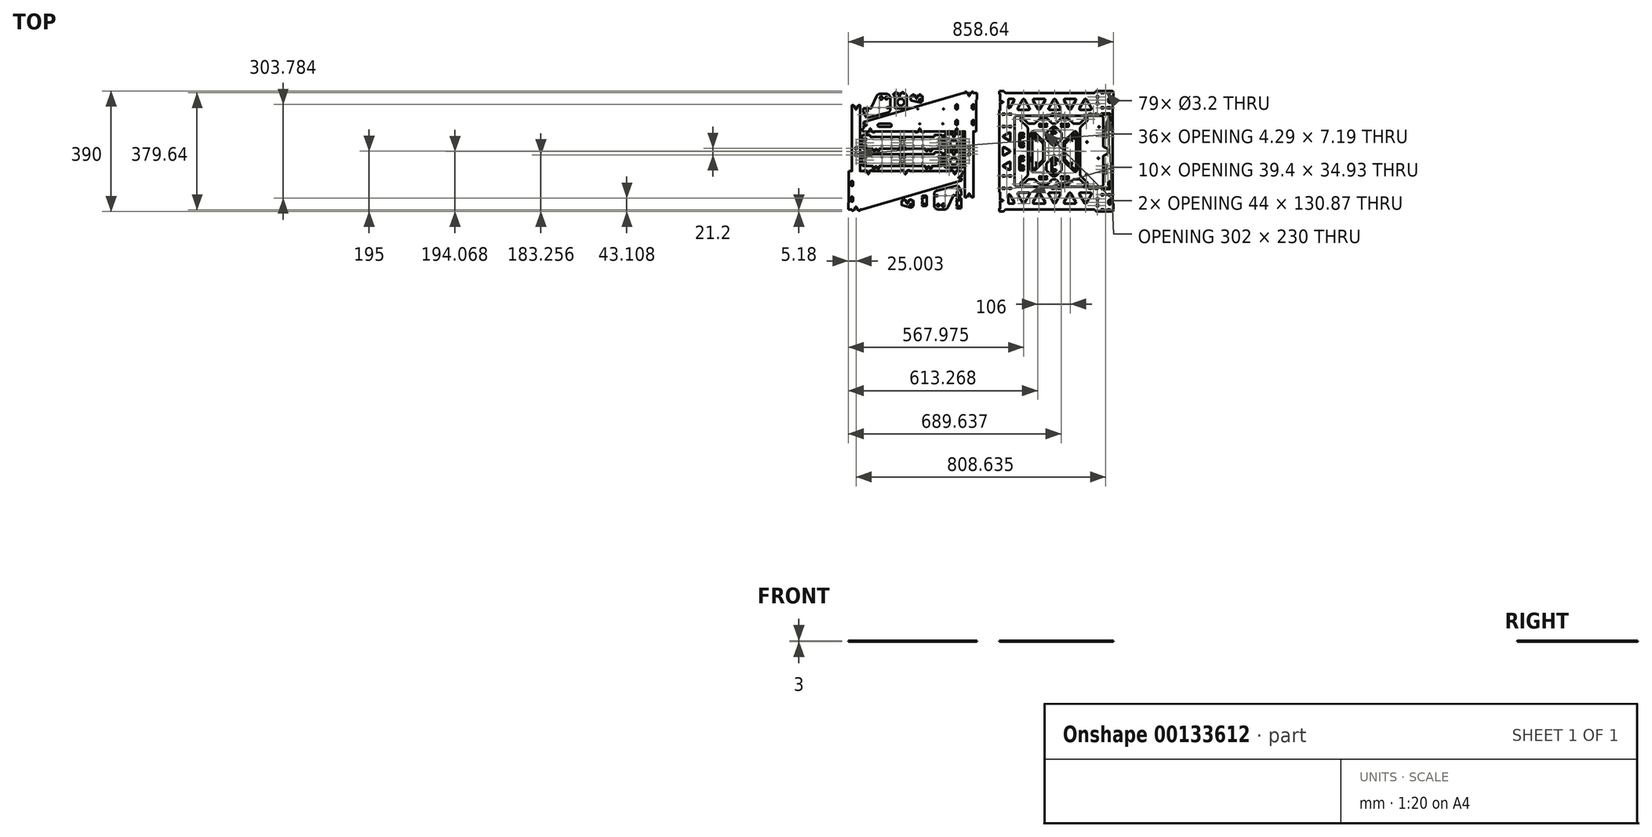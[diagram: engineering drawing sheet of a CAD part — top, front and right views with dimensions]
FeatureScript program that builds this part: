
annotation { "Feature Type Name" : "Feature", "Feature Type Description" : "" }
export const myFeature = defineFeature(function(context is Context, id is Id, definition is map)
    precondition{}
    {
        {
            var Q0;
            Q0=qCreatedBy(makeId("Top.planeOp"),FACE);
            var sketch = newSketch(context, id + "F0", { "sketchPlane" : qUnion([Q0])});
            skLineSegment(sketch, "E0", {"start": v(427.32, 168) * mm, "end": v(429.32, 170) * mm});
            skLineSegment(sketch, "E1", {"start": v(429.32, 170) * mm, "end": v(429.32, 190) * mm});
            skArc(sketch, "E2", {"start": v(429.32, 190) * mm, "mid": v(427.85, 193.54) * mm, "end": v(424.32, 195) * mm});
            skLineSegment(sketch, "E3", {"start": v(424.32, 195) * mm, "end": v(372.97, 195) * mm});
            skArc(sketch, "E4", {"start": v(365.22, 189) * mm, "mid": v(370.12, 190.68) * mm, "end": v(372.97, 195) * mm});
            skLineSegment(sketch, "E5", {"start": v(365.22, 189) * mm, "end": v(82.06, 189) * mm});
            skArc(sketch, "E6", {"start": v(74.32, 195) * mm, "mid": v(77.16, 190.68) * mm, "end": v(82.06, 189) * mm});
            skLineSegment(sketch, "E7", {"start": v(74.32, 195) * mm, "end": v(59.32, 195) * mm});
            skLineSegment(sketch, "E8", {"start": v(59.32, 195) * mm, "end": v(59.32, 185) * mm});
            skLineSegment(sketch, "E9", {"start": v(59.32, 185) * mm, "end": v(61.55, 185) * mm});
            skArc(sketch, "E10", {"start": v(61.55, 185) * mm, "mid": v(61.8, 185.07) * mm, "end": v(61.98, 185.25) * mm});
            skArc(sketch, "E11", {"start": v(62.67, 184.57) * mm, "mid": v(62.77, 185.35) * mm, "end": v(61.98, 185.25) * mm});
            skArc(sketch, "E12", {"start": v(62.67, 184.57) * mm, "mid": v(62.48, 184.38) * mm, "end": v(62.42, 184.13) * mm});
            skLineSegment(sketch, "E13", {"start": v(62.42, 184.13) * mm, "end": v(62.42, 160.78) * mm});
            skLineSegment(sketch, "E14", {"start": v(62.42, 160.78) * mm, "end": v(65.42, 160.78) * mm});
            skLineSegment(sketch, "E15", {"start": v(65.42, 160.78) * mm, "end": v(65.42, 162.05) * mm});
            skLineSegment(sketch, "E16", {"start": v(65.42, 162.05) * mm, "end": v(69.42, 162.05) * mm});
            skLineSegment(sketch, "E17", {"start": v(69.42, 162.05) * mm, "end": v(69.42, 160.78) * mm});
            skLineSegment(sketch, "E18", {"start": v(69.42, 160.78) * mm, "end": v(72.42, 160.78) * mm});
            skLineSegment(sketch, "E19", {"start": v(72.42, 160.78) * mm, "end": v(72.42, 157.57) * mm});
            skLineSegment(sketch, "E20", {"start": v(72.42, 157.57) * mm, "end": v(69.42, 157.57) * mm});
            skLineSegment(sketch, "E21", {"start": v(69.42, 157.57) * mm, "end": v(69.42, 156.3) * mm});
            skLineSegment(sketch, "E22", {"start": v(69.42, 156.3) * mm, "end": v(65.42, 156.3) * mm});
            skLineSegment(sketch, "E23", {"start": v(65.42, 156.3) * mm, "end": v(65.42, 157.57) * mm});
            skLineSegment(sketch, "E24", {"start": v(65.42, 157.57) * mm, "end": v(62.42, 157.57) * mm});
            skLineSegment(sketch, "E25", {"start": v(62.42, 157.57) * mm, "end": v(62.42, 134.22) * mm});
            skArc(sketch, "E26", {"start": v(62.42, 134.22) * mm, "mid": v(62.48, 133.97) * mm, "end": v(62.67, 133.78) * mm});
            skArc(sketch, "E27", {"start": v(61.98, 133.1) * mm, "mid": v(62.77, 133) * mm, "end": v(62.67, 133.78) * mm});
            skArc(sketch, "E28", {"start": v(61.98, 133.1) * mm, "mid": v(61.8, 133.28) * mm, "end": v(61.55, 133.35) * mm});
            skLineSegment(sketch, "E29", {"start": v(61.55, 133.35) * mm, "end": v(59.32, 133.35) * mm});
            skLineSegment(sketch, "E30", {"start": v(59.32, 133.35) * mm, "end": v(59.32, -133.35) * mm});
            skLineSegment(sketch, "E31", {"start": v(59.32, -133.35) * mm, "end": v(61.55, -133.35) * mm});
            skArc(sketch, "E32", {"start": v(61.55, -133.35) * mm, "mid": v(61.8, -133.28) * mm, "end": v(61.98, -133.1) * mm});
            skArc(sketch, "E33", {"start": v(62.67, -133.78) * mm, "mid": v(62.77, -133) * mm, "end": v(61.98, -133.1) * mm});
            skArc(sketch, "E34", {"start": v(62.67, -133.78) * mm, "mid": v(62.48, -133.97) * mm, "end": v(62.42, -134.22) * mm});
            skLineSegment(sketch, "E35", {"start": v(62.42, -134.22) * mm, "end": v(62.42, -157.57) * mm});
            skLineSegment(sketch, "E36", {"start": v(62.42, -157.57) * mm, "end": v(65.42, -157.57) * mm});
            skLineSegment(sketch, "E37", {"start": v(65.42, -157.57) * mm, "end": v(65.42, -156.3) * mm});
            skLineSegment(sketch, "E38", {"start": v(65.42, -156.3) * mm, "end": v(69.42, -156.3) * mm});
            skLineSegment(sketch, "E39", {"start": v(69.42, -156.3) * mm, "end": v(69.42, -157.57) * mm});
            skLineSegment(sketch, "E40", {"start": v(69.42, -157.57) * mm, "end": v(72.42, -157.57) * mm});
            skLineSegment(sketch, "E41", {"start": v(72.42, -157.57) * mm, "end": v(72.42, -160.78) * mm});
            skLineSegment(sketch, "E42", {"start": v(72.42, -160.78) * mm, "end": v(69.42, -160.78) * mm});
            skLineSegment(sketch, "E43", {"start": v(69.42, -160.78) * mm, "end": v(69.42, -162.05) * mm});
            skLineSegment(sketch, "E44", {"start": v(69.42, -162.05) * mm, "end": v(65.42, -162.05) * mm});
            skLineSegment(sketch, "E45", {"start": v(65.42, -162.05) * mm, "end": v(65.42, -160.78) * mm});
            skLineSegment(sketch, "E46", {"start": v(65.42, -160.78) * mm, "end": v(62.42, -160.78) * mm});
            skLineSegment(sketch, "E47", {"start": v(62.42, -160.78) * mm, "end": v(62.42, -184.13) * mm});
            skArc(sketch, "E48", {"start": v(62.42, -184.13) * mm, "mid": v(62.48, -184.38) * mm, "end": v(62.67, -184.57) * mm});
            skArc(sketch, "E49", {"start": v(61.98, -185.25) * mm, "mid": v(62.77, -185.35) * mm, "end": v(62.67, -184.57) * mm});
            skArc(sketch, "E50", {"start": v(61.98, -185.25) * mm, "mid": v(61.8, -185.07) * mm, "end": v(61.55, -185) * mm});
            skLineSegment(sketch, "E51", {"start": v(61.55, -185) * mm, "end": v(59.32, -185) * mm});
            skLineSegment(sketch, "E52", {"start": v(59.32, -185) * mm, "end": v(59.32, -195) * mm});
            skLineSegment(sketch, "E53", {"start": v(59.32, -195) * mm, "end": v(74.32, -195) * mm});
            skArc(sketch, "E54", {"start": v(82.06, -189) * mm, "mid": v(77.16, -190.68) * mm, "end": v(74.32, -195) * mm});
            skLineSegment(sketch, "E55", {"start": v(82.06, -189) * mm, "end": v(365.22, -189) * mm});
            skArc(sketch, "E56", {"start": v(372.97, -195) * mm, "mid": v(370.12, -190.68) * mm, "end": v(365.22, -189) * mm});
            skLineSegment(sketch, "E57", {"start": v(372.97, -195) * mm, "end": v(424.32, -195) * mm});
            skArc(sketch, "E58", {"start": v(424.32, -195) * mm, "mid": v(427.85, -193.54) * mm, "end": v(429.32, -190) * mm});
            skLineSegment(sketch, "E59", {"start": v(429.32, -190) * mm, "end": v(429.32, -170) * mm});
            skLineSegment(sketch, "E60", {"start": v(429.32, -170) * mm, "end": v(427.32, -168) * mm});
            skLineSegment(sketch, "E61", {"start": v(427.32, -168) * mm, "end": v(427.32, 168) * mm});
            skLineSegment(sketch, "E62", {"start": v(411.32, -6.72) * mm, "end": v(411.32, 6.73) * mm});
            skArc(sketch, "E63", {"start": v(411.32, 6.73) * mm, "mid": v(411, 7.8) * mm, "end": v(410.16, 8.54) * mm});
            skLineSegment(sketch, "E64", {"start": v(410.16, 8.54) * mm, "end": v(397.35, 14.51) * mm});
            skArc(sketch, "E65", {"start": v(396.2, 16.33) * mm, "mid": v(396.5, 15.25) * mm, "end": v(397.35, 14.51) * mm});
            skLineSegment(sketch, "E66", {"start": v(396.2, 16.33) * mm, "end": v(396.2, 107) * mm});
            skArc(sketch, "E67", {"start": v(396.2, 107) * mm, "mid": v(393.86, 112.65) * mm, "end": v(388.21, 115) * mm});
            skLineSegment(sketch, "E68", {"start": v(388.21, 115) * mm, "end": v(117.32, 115) * mm});
            skArc(sketch, "E69", {"start": v(117.32, 115) * mm, "mid": v(111.66, 112.66) * mm, "end": v(109.32, 107) * mm});
            skLineSegment(sketch, "E70", {"start": v(109.32, 107) * mm, "end": v(109.32, -107) * mm});
            skArc(sketch, "E71", {"start": v(109.32, -107) * mm, "mid": v(111.66, -112.66) * mm, "end": v(117.32, -115) * mm});
            skLineSegment(sketch, "E72", {"start": v(117.32, -115) * mm, "end": v(388.21, -115) * mm});
            skArc(sketch, "E73", {"start": v(388.21, -115) * mm, "mid": v(393.86, -112.65) * mm, "end": v(396.2, -107) * mm});
            skLineSegment(sketch, "E74", {"start": v(396.2, -107) * mm, "end": v(396.2, -16.23) * mm});
            skArc(sketch, "E75", {"start": v(397.36, -14.41) * mm, "mid": v(396.5, -15.15) * mm, "end": v(396.2, -16.23) * mm});
            skLineSegment(sketch, "E76", {"start": v(397.36, -14.41) * mm, "end": v(410.15, -8.54) * mm});
            skArc(sketch, "E77", {"start": v(410.15, -8.54) * mm, "mid": v(411, -7.8) * mm, "end": v(411.32, -6.72) * mm});
            skLineSegment(sketch, "E78", {"start": v(355.36, -134.43) * mm, "end": v(321.95, -134.43) * mm});
            skArc(sketch, "E79", {"start": v(321.95, -134.43) * mm, "mid": v(319.36, -135.93) * mm, "end": v(319.36, -138.93) * mm});
            skLineSegment(sketch, "E80", {"start": v(319.36, -138.93) * mm, "end": v(336.06, -167.86) * mm});
            skArc(sketch, "E81", {"start": v(336.06, -167.86) * mm, "mid": v(338.66, -169.36) * mm, "end": v(341.25, -167.86) * mm});
            skLineSegment(sketch, "E82", {"start": v(341.25, -167.86) * mm, "end": v(357.95, -138.93) * mm});
            skArc(sketch, "E83", {"start": v(357.95, -138.93) * mm, "mid": v(357.95, -135.93) * mm, "end": v(355.36, -134.43) * mm});
            skLineSegment(sketch, "E84", {"start": v(305.36, -169.36) * mm, "end": v(271.96, -169.36) * mm});
            skArc(sketch, "E85", {"start": v(269.36, -164.86) * mm, "mid": v(269.36, -167.86) * mm, "end": v(271.96, -169.36) * mm});
            skLineSegment(sketch, "E86", {"start": v(269.36, -164.86) * mm, "end": v(286.06, -135.93) * mm});
            skArc(sketch, "E87", {"start": v(291.25, -135.93) * mm, "mid": v(288.66, -134.43) * mm, "end": v(286.06, -135.93) * mm});
            skLineSegment(sketch, "E88", {"start": v(291.25, -135.93) * mm, "end": v(307.96, -164.86) * mm});
            skArc(sketch, "E89", {"start": v(305.36, -169.36) * mm, "mid": v(307.96, -167.86) * mm, "end": v(307.96, -164.86) * mm});
            skLineSegment(sketch, "E90", {"start": v(255.36, -134.43) * mm, "end": v(221.95, -134.43) * mm});
            skArc(sketch, "E91", {"start": v(221.95, -134.43) * mm, "mid": v(219.36, -135.93) * mm, "end": v(219.36, -138.93) * mm});
            skLineSegment(sketch, "E92", {"start": v(219.36, -138.93) * mm, "end": v(236.06, -167.86) * mm});
            skArc(sketch, "E93", {"start": v(236.06, -167.86) * mm, "mid": v(238.66, -169.36) * mm, "end": v(241.25, -167.86) * mm});
            skLineSegment(sketch, "E94", {"start": v(241.25, -167.86) * mm, "end": v(257.95, -138.93) * mm});
            skArc(sketch, "E95", {"start": v(257.95, -138.93) * mm, "mid": v(257.95, -135.93) * mm, "end": v(255.36, -134.43) * mm});
            skLineSegment(sketch, "E96", {"start": v(205.36, -169.36) * mm, "end": v(171.96, -169.36) * mm});
            skArc(sketch, "E97", {"start": v(169.36, -164.86) * mm, "mid": v(169.36, -167.86) * mm, "end": v(171.96, -169.36) * mm});
            skLineSegment(sketch, "E98", {"start": v(169.36, -164.86) * mm, "end": v(186.06, -135.93) * mm});
            skArc(sketch, "E99", {"start": v(191.25, -135.93) * mm, "mid": v(188.66, -134.43) * mm, "end": v(186.06, -135.93) * mm});
            skLineSegment(sketch, "E100", {"start": v(191.25, -135.93) * mm, "end": v(207.96, -164.86) * mm});
            skArc(sketch, "E101", {"start": v(205.36, -169.36) * mm, "mid": v(207.96, -167.86) * mm, "end": v(207.96, -164.86) * mm});
            skLineSegment(sketch, "E102", {"start": v(155.36, -134.43) * mm, "end": v(121.95, -134.43) * mm});
            skArc(sketch, "E103", {"start": v(121.95, -134.43) * mm, "mid": v(119.36, -135.93) * mm, "end": v(119.36, -138.93) * mm});
            skLineSegment(sketch, "E104", {"start": v(119.36, -138.93) * mm, "end": v(136.06, -167.86) * mm});
            skArc(sketch, "E105", {"start": v(136.06, -167.86) * mm, "mid": v(138.66, -169.36) * mm, "end": v(141.25, -167.86) * mm});
            skLineSegment(sketch, "E106", {"start": v(141.25, -167.86) * mm, "end": v(157.95, -138.93) * mm});
            skArc(sketch, "E107", {"start": v(157.95, -138.93) * mm, "mid": v(157.95, -135.93) * mm, "end": v(155.36, -134.43) * mm});
            skLineSegment(sketch, "E108", {"start": v(355.36, 134.43) * mm, "end": v(321.95, 134.43) * mm});
            skArc(sketch, "E109", {"start": v(319.36, 138.93) * mm, "mid": v(319.36, 135.93) * mm, "end": v(321.95, 134.43) * mm});
            skLineSegment(sketch, "E110", {"start": v(319.36, 138.93) * mm, "end": v(336.06, 167.86) * mm});
            skArc(sketch, "E111", {"start": v(341.25, 167.86) * mm, "mid": v(338.66, 169.36) * mm, "end": v(336.06, 167.86) * mm});
            skLineSegment(sketch, "E112", {"start": v(341.25, 167.86) * mm, "end": v(357.95, 138.93) * mm});
            skArc(sketch, "E113", {"start": v(355.36, 134.43) * mm, "mid": v(357.95, 135.93) * mm, "end": v(357.95, 138.93) * mm});
            skLineSegment(sketch, "E114", {"start": v(305.36, 169.36) * mm, "end": v(271.96, 169.36) * mm});
            skArc(sketch, "E115", {"start": v(271.96, 169.36) * mm, "mid": v(269.36, 167.86) * mm, "end": v(269.36, 164.86) * mm});
            skLineSegment(sketch, "E116", {"start": v(269.36, 164.86) * mm, "end": v(286.06, 135.93) * mm});
            skArc(sketch, "E117", {"start": v(286.06, 135.93) * mm, "mid": v(288.66, 134.43) * mm, "end": v(291.25, 135.93) * mm});
            skLineSegment(sketch, "E118", {"start": v(291.25, 135.93) * mm, "end": v(307.96, 164.86) * mm});
            skArc(sketch, "E119", {"start": v(307.96, 164.86) * mm, "mid": v(307.96, 167.86) * mm, "end": v(305.36, 169.36) * mm});
            skLineSegment(sketch, "E120", {"start": v(255.36, 134.43) * mm, "end": v(221.95, 134.43) * mm});
            skArc(sketch, "E121", {"start": v(219.36, 138.93) * mm, "mid": v(219.36, 135.93) * mm, "end": v(221.95, 134.43) * mm});
            skLineSegment(sketch, "E122", {"start": v(219.36, 138.93) * mm, "end": v(236.06, 167.86) * mm});
            skArc(sketch, "E123", {"start": v(241.25, 167.86) * mm, "mid": v(238.66, 169.36) * mm, "end": v(236.06, 167.86) * mm});
            skLineSegment(sketch, "E124", {"start": v(241.25, 167.86) * mm, "end": v(257.95, 138.93) * mm});
            skArc(sketch, "E125", {"start": v(255.36, 134.43) * mm, "mid": v(257.95, 135.93) * mm, "end": v(257.95, 138.93) * mm});
            skLineSegment(sketch, "E126", {"start": v(205.36, 169.36) * mm, "end": v(171.96, 169.36) * mm});
            skArc(sketch, "E127", {"start": v(171.96, 169.36) * mm, "mid": v(169.36, 167.86) * mm, "end": v(169.36, 164.86) * mm});
            skLineSegment(sketch, "E128", {"start": v(169.36, 164.86) * mm, "end": v(186.06, 135.93) * mm});
            skArc(sketch, "E129", {"start": v(186.06, 135.93) * mm, "mid": v(188.66, 134.43) * mm, "end": v(191.25, 135.93) * mm});
            skLineSegment(sketch, "E130", {"start": v(191.25, 135.93) * mm, "end": v(207.96, 164.86) * mm});
            skArc(sketch, "E131", {"start": v(207.96, 164.86) * mm, "mid": v(207.96, 167.86) * mm, "end": v(205.36, 169.36) * mm});
            skLineSegment(sketch, "E132", {"start": v(155.36, 134.43) * mm, "end": v(121.95, 134.43) * mm});
            skArc(sketch, "E133", {"start": v(119.36, 138.93) * mm, "mid": v(119.36, 135.93) * mm, "end": v(121.95, 134.43) * mm});
            skLineSegment(sketch, "E134", {"start": v(119.36, 138.93) * mm, "end": v(136.06, 167.86) * mm});
            skArc(sketch, "E135", {"start": v(141.25, 167.86) * mm, "mid": v(138.66, 169.36) * mm, "end": v(136.06, 167.86) * mm});
            skLineSegment(sketch, "E136", {"start": v(141.25, 167.86) * mm, "end": v(157.95, 138.93) * mm});
            skArc(sketch, "E137", {"start": v(155.36, 134.43) * mm, "mid": v(157.95, 135.93) * mm, "end": v(157.95, 138.93) * mm});
            skLineSegment(sketch, "E138", {"start": v(95.2, -36.24) * mm, "end": v(95.2, -58.78) * mm});
            skArc(sketch, "E139", {"start": v(92.16, -60.54) * mm, "mid": v(94.19, -60.54) * mm, "end": v(95.2, -58.78) * mm});
            skLineSegment(sketch, "E140", {"start": v(92.16, -60.54) * mm, "end": v(72.64, -49.26) * mm});
            skArc(sketch, "E141", {"start": v(72.64, -45.75) * mm, "mid": v(71.62, -47.5) * mm, "end": v(72.64, -49.26) * mm});
            skLineSegment(sketch, "E142", {"start": v(72.64, -45.75) * mm, "end": v(92.16, -34.48) * mm});
            skArc(sketch, "E143", {"start": v(95.2, -36.24) * mm, "mid": v(94.19, -34.48) * mm, "end": v(92.16, -34.48) * mm});
            skLineSegment(sketch, "E144", {"start": v(71.62, 11.26) * mm, "end": v(71.62, -11.28) * mm});
            skArc(sketch, "E145", {"start": v(71.62, -11.28) * mm, "mid": v(72.64, -13.04) * mm, "end": v(74.66, -13.04) * mm});
            skLineSegment(sketch, "E146", {"start": v(74.66, -13.04) * mm, "end": v(94.19, -1.76) * mm});
            skArc(sketch, "E147", {"start": v(94.19, -1.76) * mm, "mid": v(95.2, 0) * mm, "end": v(94.19, 1.75) * mm});
            skLineSegment(sketch, "E148", {"start": v(94.19, 1.75) * mm, "end": v(74.66, 13.02) * mm});
            skArc(sketch, "E149", {"start": v(74.66, 13.02) * mm, "mid": v(72.64, 13.02) * mm, "end": v(71.62, 11.26) * mm});
            skLineSegment(sketch, "E150", {"start": v(95.2, 58.77) * mm, "end": v(95.2, 36.23) * mm});
            skArc(sketch, "E151", {"start": v(92.16, 34.47) * mm, "mid": v(94.19, 34.47) * mm, "end": v(95.2, 36.23) * mm});
            skLineSegment(sketch, "E152", {"start": v(92.16, 34.47) * mm, "end": v(72.64, 45.75) * mm});
            skArc(sketch, "E153", {"start": v(72.64, 49.25) * mm, "mid": v(71.62, 47.5) * mm, "end": v(72.64, 45.75) * mm});
            skLineSegment(sketch, "E154", {"start": v(72.64, 49.25) * mm, "end": v(92.16, 60.53) * mm});
            skArc(sketch, "E155", {"start": v(95.2, 58.77) * mm, "mid": v(94.19, 60.53) * mm, "end": v(92.16, 60.53) * mm});
            skLineSegment(sketch, "E156", {"start": v(421.32, -169) * mm, "end": v(421.32, -161) * mm});
            skArc(sketch, "E157", {"start": v(421.32, -161) * mm, "mid": v(417.32, -157) * mm, "end": v(413.32, -161) * mm});
            skLineSegment(sketch, "E158", {"start": v(413.32, -161) * mm, "end": v(413.32, -169) * mm});
            skArc(sketch, "E159", {"start": v(413.32, -169) * mm, "mid": v(417.32, -173) * mm, "end": v(421.32, -169) * mm});
            skLineSegment(sketch, "E160", {"start": v(421.32, -109) * mm, "end": v(421.32, -101) * mm});
            skArc(sketch, "E161", {"start": v(421.32, -101) * mm, "mid": v(417.32, -97) * mm, "end": v(413.32, -101) * mm});
            skLineSegment(sketch, "E162", {"start": v(413.32, -101) * mm, "end": v(413.32, -109) * mm});
            skArc(sketch, "E163", {"start": v(413.32, -109) * mm, "mid": v(417.32, -113) * mm, "end": v(421.32, -109) * mm});
            skLineSegment(sketch, "E164", {"start": v(421.32, 101) * mm, "end": v(421.32, 109) * mm});
            skArc(sketch, "E165", {"start": v(421.32, 109) * mm, "mid": v(417.32, 113) * mm, "end": v(413.32, 109) * mm});
            skLineSegment(sketch, "E166", {"start": v(413.32, 109) * mm, "end": v(413.32, 101) * mm});
            skArc(sketch, "E167", {"start": v(413.32, 101) * mm, "mid": v(417.32, 97) * mm, "end": v(421.32, 101) * mm});
            skLineSegment(sketch, "E168", {"start": v(421.32, 161) * mm, "end": v(421.32, 169) * mm});
            skArc(sketch, "E169", {"start": v(421.32, 169) * mm, "mid": v(417.32, 173) * mm, "end": v(413.32, 169) * mm});
            skLineSegment(sketch, "E170", {"start": v(413.32, 169) * mm, "end": v(413.32, 161) * mm});
            skArc(sketch, "E171", {"start": v(413.32, 161) * mm, "mid": v(417.32, 157) * mm, "end": v(421.32, 161) * mm});
            skLineSegment(sketch, "E172", {"start": v(404.32, 118.38) * mm, "end": v(391.17, 118.38) * mm});
            skArc(sketch, "E173", {"start": v(390.27, 118.86) * mm, "mid": v(390.16, 118.07) * mm, "end": v(390.95, 118.18) * mm});
            skArc(sketch, "E174", {"start": v(390.27, 118.86) * mm, "mid": v(390.45, 119.04) * mm, "end": v(390.52, 119.3) * mm});
            skArc(sketch, "E175", {"start": v(411.82, -189.04) * mm, "mid": v(411.75, -188.79) * mm, "end": v(411.57, -188.6) * mm});
            skArc(sketch, "E176", {"start": v(412.25, -187.92) * mm, "mid": v(411.46, -187.82) * mm, "end": v(411.57, -188.6) * mm});
            skArc(sketch, "E177", {"start": v(412.25, -187.92) * mm, "mid": v(412.43, -188.1) * mm, "end": v(412.68, -188.17) * mm});
            skLineSegment(sketch, "E178", {"start": v(412.68, -188.17) * mm, "end": v(417.15, -188.17) * mm});
            skArc(sketch, "E179", {"start": v(417.15, -188.17) * mm, "mid": v(417.4, -188.1) * mm, "end": v(417.58, -187.92) * mm});
            skArc(sketch, "E180", {"start": v(418.27, -188.6) * mm, "mid": v(418.37, -187.82) * mm, "end": v(417.58, -187.92) * mm});
            skArc(sketch, "E181", {"start": v(418.27, -188.6) * mm, "mid": v(418.08, -188.79) * mm, "end": v(418.02, -189.04) * mm});
            skLineSegment(sketch, "E182", {"start": v(418.02, -189.04) * mm, "end": v(418.02, -190.6) * mm});
            skArc(sketch, "E183", {"start": v(418.02, -190.6) * mm, "mid": v(418.08, -190.85) * mm, "end": v(418.27, -191.04) * mm});
            skArc(sketch, "E184", {"start": v(417.58, -191.72) * mm, "mid": v(418.37, -191.82) * mm, "end": v(418.27, -191.04) * mm});
            skArc(sketch, "E185", {"start": v(417.58, -191.72) * mm, "mid": v(417.4, -191.54) * mm, "end": v(417.15, -191.47) * mm});
            skLineSegment(sketch, "E186", {"start": v(417.15, -191.47) * mm, "end": v(412.68, -191.47) * mm});
            skArc(sketch, "E187", {"start": v(412.68, -191.47) * mm, "mid": v(412.43, -191.54) * mm, "end": v(412.25, -191.72) * mm});
            skArc(sketch, "E188", {"start": v(411.57, -191.04) * mm, "mid": v(411.46, -191.82) * mm, "end": v(412.25, -191.72) * mm});
            skArc(sketch, "E189", {"start": v(411.57, -191.04) * mm, "mid": v(411.75, -190.85) * mm, "end": v(411.82, -190.6) * mm});
            skLineSegment(sketch, "E190", {"start": v(411.82, -190.6) * mm, "end": v(411.82, -189.04) * mm});
            skArc(sketch, "E191", {"start": v(390.62, -189.04) * mm, "mid": v(390.55, -188.79) * mm, "end": v(390.37, -188.6) * mm});
            skArc(sketch, "E192", {"start": v(391.05, -187.92) * mm, "mid": v(390.26, -187.82) * mm, "end": v(390.37, -188.6) * mm});
            skArc(sketch, "E193", {"start": v(391.05, -187.92) * mm, "mid": v(391.23, -188.1) * mm, "end": v(391.48, -188.17) * mm});
            skLineSegment(sketch, "E194", {"start": v(391.48, -188.17) * mm, "end": v(395.95, -188.17) * mm});
            skArc(sketch, "E195", {"start": v(395.95, -188.17) * mm, "mid": v(396.2, -188.1) * mm, "end": v(396.38, -187.92) * mm});
            skArc(sketch, "E196", {"start": v(397.07, -188.6) * mm, "mid": v(397.17, -187.82) * mm, "end": v(396.38, -187.92) * mm});
            skArc(sketch, "E197", {"start": v(397.07, -188.6) * mm, "mid": v(396.88, -188.79) * mm, "end": v(396.82, -189.04) * mm});
            skLineSegment(sketch, "E198", {"start": v(396.82, -189.04) * mm, "end": v(396.82, -190.6) * mm});
            skArc(sketch, "E199", {"start": v(396.82, -190.6) * mm, "mid": v(396.88, -190.85) * mm, "end": v(397.07, -191.04) * mm});
            skArc(sketch, "E200", {"start": v(396.38, -191.72) * mm, "mid": v(397.17, -191.82) * mm, "end": v(397.07, -191.04) * mm});
            skArc(sketch, "E201", {"start": v(396.38, -191.72) * mm, "mid": v(396.2, -191.54) * mm, "end": v(395.95, -191.47) * mm});
            skLineSegment(sketch, "E202", {"start": v(395.95, -191.47) * mm, "end": v(391.48, -191.47) * mm});
            skArc(sketch, "E203", {"start": v(391.48, -191.47) * mm, "mid": v(391.23, -191.54) * mm, "end": v(391.05, -191.72) * mm});
            skArc(sketch, "E204", {"start": v(390.37, -191.04) * mm, "mid": v(390.26, -191.82) * mm, "end": v(391.05, -191.72) * mm});
            skArc(sketch, "E205", {"start": v(390.37, -191.04) * mm, "mid": v(390.55, -190.85) * mm, "end": v(390.62, -190.6) * mm});
            skLineSegment(sketch, "E206", {"start": v(390.62, -190.6) * mm, "end": v(390.62, -189.04) * mm});
            skArc(sketch, "E207", {"start": v(376.89, -179) * mm, "mid": v(376.64, -179.07) * mm, "end": v(376.46, -179.25) * mm});
            skArc(sketch, "E208", {"start": v(375.77, -178.57) * mm, "mid": v(375.67, -179.35) * mm, "end": v(376.46, -179.25) * mm});
            skArc(sketch, "E209", {"start": v(375.77, -178.57) * mm, "mid": v(375.96, -178.38) * mm, "end": v(376.02, -178.13) * mm});
            skLineSegment(sketch, "E210", {"start": v(376.02, -178.13) * mm, "end": v(376.02, -173.67) * mm});
            skArc(sketch, "E211", {"start": v(376.02, -173.67) * mm, "mid": v(375.96, -173.42) * mm, "end": v(375.77, -173.23) * mm});
            skArc(sketch, "E212", {"start": v(376.46, -172.55) * mm, "mid": v(375.67, -172.45) * mm, "end": v(375.77, -173.23) * mm});
            skArc(sketch, "E213", {"start": v(376.46, -172.55) * mm, "mid": v(376.64, -172.73) * mm, "end": v(376.89, -172.8) * mm});
            skLineSegment(sketch, "E214", {"start": v(376.89, -172.8) * mm, "end": v(378.46, -172.8) * mm});
            skArc(sketch, "E215", {"start": v(378.46, -172.8) * mm, "mid": v(378.7, -172.73) * mm, "end": v(378.89, -172.55) * mm});
            skArc(sketch, "E216", {"start": v(379.57, -173.23) * mm, "mid": v(379.68, -172.45) * mm, "end": v(378.89, -172.55) * mm});
            skArc(sketch, "E217", {"start": v(379.57, -173.23) * mm, "mid": v(379.39, -173.42) * mm, "end": v(379.32, -173.67) * mm});
            skLineSegment(sketch, "E218", {"start": v(379.32, -173.67) * mm, "end": v(379.32, -178.13) * mm});
            skArc(sketch, "E219", {"start": v(379.32, -178.13) * mm, "mid": v(379.39, -178.38) * mm, "end": v(379.57, -178.57) * mm});
            skArc(sketch, "E220", {"start": v(378.89, -179.25) * mm, "mid": v(379.68, -179.35) * mm, "end": v(379.57, -178.57) * mm});
            skArc(sketch, "E221", {"start": v(378.89, -179.25) * mm, "mid": v(378.7, -179.07) * mm, "end": v(378.46, -179) * mm});
            skLineSegment(sketch, "E222", {"start": v(378.46, -179) * mm, "end": v(376.89, -179) * mm});
            skArc(sketch, "E223", {"start": v(376.89, -157.8) * mm, "mid": v(376.64, -157.87) * mm, "end": v(376.46, -158.05) * mm});
            skArc(sketch, "E224", {"start": v(375.77, -157.37) * mm, "mid": v(375.67, -158.15) * mm, "end": v(376.46, -158.05) * mm});
            skArc(sketch, "E225", {"start": v(375.77, -157.37) * mm, "mid": v(375.96, -157.18) * mm, "end": v(376.02, -156.93) * mm});
            skLineSegment(sketch, "E226", {"start": v(376.02, -156.93) * mm, "end": v(376.02, -152.47) * mm});
            skArc(sketch, "E227", {"start": v(376.02, -152.47) * mm, "mid": v(375.96, -152.22) * mm, "end": v(375.77, -152.03) * mm});
            skArc(sketch, "E228", {"start": v(376.46, -151.35) * mm, "mid": v(375.67, -151.25) * mm, "end": v(375.77, -152.03) * mm});
            skArc(sketch, "E229", {"start": v(376.46, -151.35) * mm, "mid": v(376.64, -151.53) * mm, "end": v(376.89, -151.6) * mm});
            skLineSegment(sketch, "E230", {"start": v(376.89, -151.6) * mm, "end": v(378.46, -151.6) * mm});
            skArc(sketch, "E231", {"start": v(378.46, -151.6) * mm, "mid": v(378.7, -151.53) * mm, "end": v(378.89, -151.35) * mm});
            skArc(sketch, "E232", {"start": v(379.57, -152.03) * mm, "mid": v(379.68, -151.25) * mm, "end": v(378.89, -151.35) * mm});
            skArc(sketch, "E233", {"start": v(379.57, -152.03) * mm, "mid": v(379.39, -152.22) * mm, "end": v(379.32, -152.47) * mm});
            skLineSegment(sketch, "E234", {"start": v(379.32, -152.47) * mm, "end": v(379.32, -156.93) * mm});
            skArc(sketch, "E235", {"start": v(379.32, -156.93) * mm, "mid": v(379.39, -157.18) * mm, "end": v(379.57, -157.37) * mm});
            skArc(sketch, "E236", {"start": v(378.89, -158.05) * mm, "mid": v(379.68, -158.15) * mm, "end": v(379.57, -157.37) * mm});
            skArc(sketch, "E237", {"start": v(378.89, -158.05) * mm, "mid": v(378.7, -157.87) * mm, "end": v(378.46, -157.8) * mm});
            skLineSegment(sketch, "E238", {"start": v(378.46, -157.8) * mm, "end": v(376.89, -157.8) * mm});
            skArc(sketch, "E239", {"start": v(411.82, -140) * mm, "mid": v(411.75, -139.75) * mm, "end": v(411.57, -139.56) * mm});
            skArc(sketch, "E240", {"start": v(412.25, -138.88) * mm, "mid": v(411.46, -138.78) * mm, "end": v(411.57, -139.56) * mm});
            skArc(sketch, "E241", {"start": v(412.25, -138.88) * mm, "mid": v(412.43, -139.06) * mm, "end": v(412.68, -139.13) * mm});
            skLineSegment(sketch, "E242", {"start": v(412.68, -139.13) * mm, "end": v(417.15, -139.13) * mm});
            skArc(sketch, "E243", {"start": v(417.15, -139.13) * mm, "mid": v(417.4, -139.06) * mm, "end": v(417.58, -138.88) * mm});
            skArc(sketch, "E244", {"start": v(418.27, -139.56) * mm, "mid": v(418.37, -138.78) * mm, "end": v(417.58, -138.88) * mm});
            skArc(sketch, "E245", {"start": v(418.27, -139.56) * mm, "mid": v(418.08, -139.75) * mm, "end": v(418.02, -140) * mm});
            skLineSegment(sketch, "E246", {"start": v(418.02, -140) * mm, "end": v(418.02, -141.56) * mm});
            skArc(sketch, "E247", {"start": v(418.02, -141.56) * mm, "mid": v(418.08, -141.81) * mm, "end": v(418.27, -142) * mm});
            skArc(sketch, "E248", {"start": v(417.58, -142.68) * mm, "mid": v(418.37, -142.78) * mm, "end": v(418.27, -142) * mm});
            skArc(sketch, "E249", {"start": v(417.58, -142.68) * mm, "mid": v(417.4, -142.5) * mm, "end": v(417.15, -142.43) * mm});
            skLineSegment(sketch, "E250", {"start": v(417.15, -142.43) * mm, "end": v(412.68, -142.43) * mm});
            skArc(sketch, "E251", {"start": v(412.68, -142.43) * mm, "mid": v(412.43, -142.5) * mm, "end": v(412.25, -142.68) * mm});
            skArc(sketch, "E252", {"start": v(411.57, -142) * mm, "mid": v(411.46, -142.78) * mm, "end": v(412.25, -142.68) * mm});
            skArc(sketch, "E253", {"start": v(411.57, -142) * mm, "mid": v(411.75, -141.81) * mm, "end": v(411.82, -141.56) * mm});
            skLineSegment(sketch, "E254", {"start": v(411.82, -141.56) * mm, "end": v(411.82, -140) * mm});
            skArc(sketch, "E255", {"start": v(390.62, -140) * mm, "mid": v(390.55, -139.75) * mm, "end": v(390.37, -139.56) * mm});
            skArc(sketch, "E256", {"start": v(391.05, -138.88) * mm, "mid": v(390.26, -138.78) * mm, "end": v(390.37, -139.56) * mm});
            skArc(sketch, "E257", {"start": v(391.05, -138.88) * mm, "mid": v(391.23, -139.06) * mm, "end": v(391.48, -139.13) * mm});
            skLineSegment(sketch, "E258", {"start": v(391.48, -139.13) * mm, "end": v(395.95, -139.13) * mm});
            skArc(sketch, "E259", {"start": v(395.95, -139.13) * mm, "mid": v(396.2, -139.06) * mm, "end": v(396.38, -138.88) * mm});
            skArc(sketch, "E260", {"start": v(397.07, -139.56) * mm, "mid": v(397.17, -138.78) * mm, "end": v(396.38, -138.88) * mm});
            skArc(sketch, "E261", {"start": v(397.07, -139.56) * mm, "mid": v(396.88, -139.75) * mm, "end": v(396.82, -140) * mm});
            skLineSegment(sketch, "E262", {"start": v(396.82, -140) * mm, "end": v(396.82, -141.56) * mm});
            skArc(sketch, "E263", {"start": v(396.82, -141.56) * mm, "mid": v(396.88, -141.81) * mm, "end": v(397.07, -142) * mm});
            skArc(sketch, "E264", {"start": v(396.38, -142.68) * mm, "mid": v(397.17, -142.78) * mm, "end": v(397.07, -142) * mm});
            skArc(sketch, "E265", {"start": v(396.38, -142.68) * mm, "mid": v(396.2, -142.5) * mm, "end": v(395.95, -142.43) * mm});
            skLineSegment(sketch, "E266", {"start": v(395.95, -142.43) * mm, "end": v(391.48, -142.43) * mm});
            skArc(sketch, "E267", {"start": v(391.48, -142.43) * mm, "mid": v(391.23, -142.5) * mm, "end": v(391.05, -142.68) * mm});
            skArc(sketch, "E268", {"start": v(390.37, -142) * mm, "mid": v(390.26, -142.78) * mm, "end": v(391.05, -142.68) * mm});
            skArc(sketch, "E269", {"start": v(390.37, -142) * mm, "mid": v(390.55, -141.81) * mm, "end": v(390.62, -141.56) * mm});
            skLineSegment(sketch, "E270", {"start": v(390.62, -141.56) * mm, "end": v(390.62, -140) * mm});
            skArc(sketch, "E271", {"start": v(371.57, -121.4) * mm, "mid": v(371.75, -121.2) * mm, "end": v(371.82, -120.96) * mm});
            skArc(sketch, "E272", {"start": v(371.57, -121.4) * mm, "mid": v(371.46, -122.18) * mm, "end": v(372.25, -122.07) * mm});
            skArc(sketch, "E273", {"start": v(372.68, -121.82) * mm, "mid": v(372.43, -121.9) * mm, "end": v(372.25, -122.07) * mm});
            skLineSegment(sketch, "E274", {"start": v(372.68, -121.82) * mm, "end": v(377.15, -121.82) * mm});
            skArc(sketch, "E275", {"start": v(377.58, -122.07) * mm, "mid": v(377.4, -121.9) * mm, "end": v(377.15, -121.82) * mm});
            skArc(sketch, "E276", {"start": v(377.58, -122.07) * mm, "mid": v(378.37, -122.18) * mm, "end": v(378.27, -121.4) * mm});
            skArc(sketch, "E277", {"start": v(378.02, -120.96) * mm, "mid": v(378.08, -121.2) * mm, "end": v(378.27, -121.4) * mm});
            skLineSegment(sketch, "E278", {"start": v(378.02, -120.96) * mm, "end": v(378.02, -119.4) * mm});
            skArc(sketch, "E279", {"start": v(378.27, -118.96) * mm, "mid": v(378.08, -119.14) * mm, "end": v(378.02, -119.4) * mm});
            skArc(sketch, "E280", {"start": v(378.27, -118.96) * mm, "mid": v(378.37, -118.17) * mm, "end": v(377.58, -118.28) * mm});
            skArc(sketch, "E281", {"start": v(377.15, -118.52) * mm, "mid": v(377.4, -118.46) * mm, "end": v(377.58, -118.28) * mm});
            skLineSegment(sketch, "E282", {"start": v(377.15, -118.52) * mm, "end": v(372.68, -118.53) * mm});
            skArc(sketch, "E283", {"start": v(372.25, -118.28) * mm, "mid": v(372.43, -118.46) * mm, "end": v(372.68, -118.53) * mm});
            skArc(sketch, "E284", {"start": v(372.25, -118.28) * mm, "mid": v(371.46, -118.17) * mm, "end": v(371.57, -118.96) * mm});
            skArc(sketch, "E285", {"start": v(371.82, -119.4) * mm, "mid": v(371.75, -119.14) * mm, "end": v(371.57, -118.96) * mm});
            skLineSegment(sketch, "E286", {"start": v(371.82, -119.4) * mm, "end": v(371.82, -120.96) * mm});
            skArc(sketch, "E287", {"start": v(350.37, -121.4) * mm, "mid": v(350.55, -121.2) * mm, "end": v(350.62, -120.96) * mm});
            skArc(sketch, "E288", {"start": v(350.37, -121.4) * mm, "mid": v(350.26, -122.18) * mm, "end": v(351.05, -122.07) * mm});
            skArc(sketch, "E289", {"start": v(351.48, -121.82) * mm, "mid": v(351.23, -121.9) * mm, "end": v(351.05, -122.07) * mm});
            skLineSegment(sketch, "E290", {"start": v(351.48, -121.82) * mm, "end": v(355.95, -121.82) * mm});
            skArc(sketch, "E291", {"start": v(356.38, -122.07) * mm, "mid": v(356.2, -121.9) * mm, "end": v(355.95, -121.82) * mm});
            skArc(sketch, "E292", {"start": v(356.38, -122.07) * mm, "mid": v(357.17, -122.18) * mm, "end": v(357.07, -121.4) * mm});
            skArc(sketch, "E293", {"start": v(356.82, -120.96) * mm, "mid": v(356.88, -121.2) * mm, "end": v(357.07, -121.4) * mm});
            skLineSegment(sketch, "E294", {"start": v(356.82, -120.96) * mm, "end": v(356.82, -119.4) * mm});
            skArc(sketch, "E295", {"start": v(357.07, -118.96) * mm, "mid": v(356.88, -119.14) * mm, "end": v(356.82, -119.4) * mm});
            skArc(sketch, "E296", {"start": v(357.07, -118.96) * mm, "mid": v(357.17, -118.17) * mm, "end": v(356.38, -118.28) * mm});
            skArc(sketch, "E297", {"start": v(355.95, -118.52) * mm, "mid": v(356.2, -118.46) * mm, "end": v(356.38, -118.28) * mm});
            skLineSegment(sketch, "E298", {"start": v(355.95, -118.52) * mm, "end": v(351.48, -118.53) * mm});
            skArc(sketch, "E299", {"start": v(351.05, -118.28) * mm, "mid": v(351.23, -118.46) * mm, "end": v(351.48, -118.53) * mm});
            skArc(sketch, "E300", {"start": v(351.05, -118.28) * mm, "mid": v(350.26, -118.17) * mm, "end": v(350.37, -118.96) * mm});
            skArc(sketch, "E301", {"start": v(350.62, -119.4) * mm, "mid": v(350.55, -119.14) * mm, "end": v(350.37, -118.96) * mm});
            skLineSegment(sketch, "E302", {"start": v(350.62, -119.4) * mm, "end": v(350.62, -120.96) * mm});
            skArc(sketch, "E303", {"start": v(251.82, -119.4) * mm, "mid": v(251.75, -119.14) * mm, "end": v(251.57, -118.96) * mm});
            skArc(sketch, "E304", {"start": v(252.25, -118.28) * mm, "mid": v(251.46, -118.17) * mm, "end": v(251.57, -118.96) * mm});
            skArc(sketch, "E305", {"start": v(252.25, -118.28) * mm, "mid": v(252.43, -118.46) * mm, "end": v(252.68, -118.53) * mm});
            skLineSegment(sketch, "E306", {"start": v(252.68, -118.53) * mm, "end": v(257.15, -118.53) * mm});
            skArc(sketch, "E307", {"start": v(257.15, -118.53) * mm, "mid": v(257.4, -118.46) * mm, "end": v(257.58, -118.28) * mm});
            skArc(sketch, "E308", {"start": v(258.27, -118.96) * mm, "mid": v(258.37, -118.17) * mm, "end": v(257.58, -118.28) * mm});
            skArc(sketch, "E309", {"start": v(258.27, -118.96) * mm, "mid": v(258.08, -119.14) * mm, "end": v(258.02, -119.4) * mm});
            skLineSegment(sketch, "E310", {"start": v(258.02, -119.4) * mm, "end": v(258.02, -120.96) * mm});
            skArc(sketch, "E311", {"start": v(258.02, -120.96) * mm, "mid": v(258.08, -121.2) * mm, "end": v(258.27, -121.4) * mm});
            skArc(sketch, "E312", {"start": v(257.58, -122.07) * mm, "mid": v(258.37, -122.18) * mm, "end": v(258.27, -121.4) * mm});
            skArc(sketch, "E313", {"start": v(257.58, -122.07) * mm, "mid": v(257.4, -121.9) * mm, "end": v(257.15, -121.82) * mm});
            skLineSegment(sketch, "E314", {"start": v(257.15, -121.82) * mm, "end": v(252.68, -121.82) * mm});
            skArc(sketch, "E315", {"start": v(252.68, -121.82) * mm, "mid": v(252.43, -121.9) * mm, "end": v(252.25, -122.07) * mm});
            skArc(sketch, "E316", {"start": v(251.57, -121.4) * mm, "mid": v(251.46, -122.18) * mm, "end": v(252.25, -122.07) * mm});
            skArc(sketch, "E317", {"start": v(251.57, -121.4) * mm, "mid": v(251.75, -121.2) * mm, "end": v(251.82, -120.96) * mm});
            skLineSegment(sketch, "E318", {"start": v(251.82, -120.96) * mm, "end": v(251.82, -119.4) * mm});
            skArc(sketch, "E319", {"start": v(230.62, -119.4) * mm, "mid": v(230.55, -119.14) * mm, "end": v(230.37, -118.96) * mm});
            skArc(sketch, "E320", {"start": v(231.05, -118.28) * mm, "mid": v(230.26, -118.17) * mm, "end": v(230.37, -118.96) * mm});
            skArc(sketch, "E321", {"start": v(231.05, -118.28) * mm, "mid": v(231.23, -118.46) * mm, "end": v(231.48, -118.53) * mm});
            skLineSegment(sketch, "E322", {"start": v(231.48, -118.53) * mm, "end": v(235.95, -118.53) * mm});
            skArc(sketch, "E323", {"start": v(235.95, -118.53) * mm, "mid": v(236.2, -118.46) * mm, "end": v(236.38, -118.28) * mm});
            skArc(sketch, "E324", {"start": v(237.07, -118.96) * mm, "mid": v(237.17, -118.17) * mm, "end": v(236.38, -118.28) * mm});
            skArc(sketch, "E325", {"start": v(237.07, -118.96) * mm, "mid": v(236.88, -119.14) * mm, "end": v(236.82, -119.4) * mm});
            skLineSegment(sketch, "E326", {"start": v(236.82, -119.4) * mm, "end": v(236.82, -120.96) * mm});
            skArc(sketch, "E327", {"start": v(236.82, -120.96) * mm, "mid": v(236.88, -121.2) * mm, "end": v(237.07, -121.4) * mm});
            skArc(sketch, "E328", {"start": v(236.38, -122.07) * mm, "mid": v(237.17, -122.18) * mm, "end": v(237.07, -121.4) * mm});
            skArc(sketch, "E329", {"start": v(236.38, -122.07) * mm, "mid": v(236.2, -121.9) * mm, "end": v(235.95, -121.82) * mm});
            skLineSegment(sketch, "E330", {"start": v(235.95, -121.82) * mm, "end": v(231.48, -121.82) * mm});
            skArc(sketch, "E331", {"start": v(231.48, -121.82) * mm, "mid": v(231.23, -121.9) * mm, "end": v(231.05, -122.07) * mm});
            skArc(sketch, "E332", {"start": v(230.37, -121.4) * mm, "mid": v(230.26, -122.18) * mm, "end": v(231.05, -122.07) * mm});
            skArc(sketch, "E333", {"start": v(230.37, -121.4) * mm, "mid": v(230.55, -121.2) * mm, "end": v(230.62, -120.96) * mm});
            skLineSegment(sketch, "E334", {"start": v(230.62, -120.96) * mm, "end": v(230.62, -119.4) * mm});
            skArc(sketch, "E335", {"start": v(91.82, -119.4) * mm, "mid": v(91.75, -119.14) * mm, "end": v(91.57, -118.96) * mm});
            skArc(sketch, "E336", {"start": v(92.25, -118.28) * mm, "mid": v(91.46, -118.17) * mm, "end": v(91.57, -118.96) * mm});
            skArc(sketch, "E337", {"start": v(92.25, -118.28) * mm, "mid": v(92.43, -118.46) * mm, "end": v(92.68, -118.53) * mm});
            skLineSegment(sketch, "E338", {"start": v(92.68, -118.53) * mm, "end": v(97.15, -118.53) * mm});
            skArc(sketch, "E339", {"start": v(97.15, -118.53) * mm, "mid": v(97.4, -118.46) * mm, "end": v(97.58, -118.28) * mm});
            skArc(sketch, "E340", {"start": v(98.27, -118.96) * mm, "mid": v(98.37, -118.17) * mm, "end": v(97.58, -118.28) * mm});
            skArc(sketch, "E341", {"start": v(98.27, -118.96) * mm, "mid": v(98.08, -119.14) * mm, "end": v(98.02, -119.4) * mm});
            skLineSegment(sketch, "E342", {"start": v(98.02, -119.4) * mm, "end": v(98.02, -120.96) * mm});
            skArc(sketch, "E343", {"start": v(98.02, -120.96) * mm, "mid": v(98.08, -121.2) * mm, "end": v(98.27, -121.4) * mm});
            skArc(sketch, "E344", {"start": v(97.58, -122.07) * mm, "mid": v(98.37, -122.18) * mm, "end": v(98.27, -121.4) * mm});
            skArc(sketch, "E345", {"start": v(97.58, -122.07) * mm, "mid": v(97.4, -121.9) * mm, "end": v(97.15, -121.82) * mm});
            skLineSegment(sketch, "E346", {"start": v(97.15, -121.82) * mm, "end": v(92.68, -121.82) * mm});
            skArc(sketch, "E347", {"start": v(92.68, -121.82) * mm, "mid": v(92.43, -121.9) * mm, "end": v(92.25, -122.07) * mm});
            skArc(sketch, "E348", {"start": v(91.57, -121.4) * mm, "mid": v(91.46, -122.18) * mm, "end": v(92.25, -122.07) * mm});
            skArc(sketch, "E349", {"start": v(91.57, -121.4) * mm, "mid": v(91.75, -121.2) * mm, "end": v(91.82, -120.96) * mm});
            skLineSegment(sketch, "E350", {"start": v(91.82, -120.96) * mm, "end": v(91.82, -119.4) * mm});
            skArc(sketch, "E351", {"start": v(70.62, -119.4) * mm, "mid": v(70.55, -119.14) * mm, "end": v(70.37, -118.96) * mm});
            skArc(sketch, "E352", {"start": v(71.05, -118.28) * mm, "mid": v(70.26, -118.17) * mm, "end": v(70.37, -118.96) * mm});
            skArc(sketch, "E353", {"start": v(71.05, -118.28) * mm, "mid": v(71.23, -118.46) * mm, "end": v(71.48, -118.53) * mm});
            skLineSegment(sketch, "E354", {"start": v(71.48, -118.53) * mm, "end": v(75.95, -118.53) * mm});
            skArc(sketch, "E355", {"start": v(75.95, -118.53) * mm, "mid": v(76.2, -118.46) * mm, "end": v(76.38, -118.28) * mm});
            skArc(sketch, "E356", {"start": v(77.07, -118.96) * mm, "mid": v(77.17, -118.17) * mm, "end": v(76.38, -118.28) * mm});
            skArc(sketch, "E357", {"start": v(77.07, -118.96) * mm, "mid": v(76.88, -119.14) * mm, "end": v(76.82, -119.4) * mm});
            skLineSegment(sketch, "E358", {"start": v(76.82, -119.4) * mm, "end": v(76.82, -120.96) * mm});
            skArc(sketch, "E359", {"start": v(76.82, -120.96) * mm, "mid": v(76.88, -121.2) * mm, "end": v(77.07, -121.4) * mm});
            skArc(sketch, "E360", {"start": v(76.38, -122.07) * mm, "mid": v(77.17, -122.18) * mm, "end": v(77.07, -121.4) * mm});
            skArc(sketch, "E361", {"start": v(76.38, -122.07) * mm, "mid": v(76.2, -121.9) * mm, "end": v(75.95, -121.82) * mm});
            skLineSegment(sketch, "E362", {"start": v(75.95, -121.82) * mm, "end": v(71.48, -121.82) * mm});
            skArc(sketch, "E363", {"start": v(71.48, -121.82) * mm, "mid": v(71.23, -121.9) * mm, "end": v(71.05, -122.07) * mm});
            skArc(sketch, "E364", {"start": v(70.37, -121.4) * mm, "mid": v(70.26, -122.18) * mm, "end": v(71.05, -122.07) * mm});
            skArc(sketch, "E365", {"start": v(70.37, -121.4) * mm, "mid": v(70.55, -121.2) * mm, "end": v(70.62, -120.96) * mm});
            skLineSegment(sketch, "E366", {"start": v(70.62, -120.96) * mm, "end": v(70.62, -119.4) * mm});
            skArc(sketch, "E367", {"start": v(371.57, 118.96) * mm, "mid": v(371.75, 119.14) * mm, "end": v(371.82, 119.4) * mm});
            skArc(sketch, "E368", {"start": v(371.57, 118.96) * mm, "mid": v(371.46, 118.17) * mm, "end": v(372.25, 118.28) * mm});
            skArc(sketch, "E369", {"start": v(372.68, 118.53) * mm, "mid": v(372.43, 118.46) * mm, "end": v(372.25, 118.28) * mm});
            skLineSegment(sketch, "E370", {"start": v(372.68, 118.53) * mm, "end": v(377.15, 118.53) * mm});
            skArc(sketch, "E371", {"start": v(377.58, 118.28) * mm, "mid": v(377.4, 118.46) * mm, "end": v(377.15, 118.53) * mm});
            skArc(sketch, "E372", {"start": v(377.58, 118.28) * mm, "mid": v(378.37, 118.17) * mm, "end": v(378.27, 118.96) * mm});
            skArc(sketch, "E373", {"start": v(378.02, 119.4) * mm, "mid": v(378.08, 119.14) * mm, "end": v(378.27, 118.96) * mm});
            skLineSegment(sketch, "E374", {"start": v(378.02, 119.4) * mm, "end": v(378.02, 120.96) * mm});
            skArc(sketch, "E375", {"start": v(378.27, 121.4) * mm, "mid": v(378.08, 121.2) * mm, "end": v(378.02, 120.96) * mm});
            skArc(sketch, "E376", {"start": v(378.27, 121.4) * mm, "mid": v(378.37, 122.18) * mm, "end": v(377.58, 122.07) * mm});
            skArc(sketch, "E377", {"start": v(377.15, 121.83) * mm, "mid": v(377.4, 121.9) * mm, "end": v(377.58, 122.07) * mm});
            skLineSegment(sketch, "E378", {"start": v(377.15, 121.83) * mm, "end": v(372.68, 121.82) * mm});
            skArc(sketch, "E379", {"start": v(372.25, 122.07) * mm, "mid": v(372.43, 121.9) * mm, "end": v(372.68, 121.82) * mm});
            skArc(sketch, "E380", {"start": v(372.25, 122.07) * mm, "mid": v(371.46, 122.18) * mm, "end": v(371.57, 121.4) * mm});
            skArc(sketch, "E381", {"start": v(371.82, 120.96) * mm, "mid": v(371.75, 121.2) * mm, "end": v(371.57, 121.4) * mm});
            skLineSegment(sketch, "E382", {"start": v(371.82, 120.96) * mm, "end": v(371.82, 119.4) * mm});
            skArc(sketch, "E383", {"start": v(350.37, 118.96) * mm, "mid": v(350.55, 119.14) * mm, "end": v(350.62, 119.4) * mm});
            skArc(sketch, "E384", {"start": v(350.37, 118.96) * mm, "mid": v(350.26, 118.17) * mm, "end": v(351.05, 118.28) * mm});
            skArc(sketch, "E385", {"start": v(351.48, 118.53) * mm, "mid": v(351.23, 118.46) * mm, "end": v(351.05, 118.28) * mm});
            skLineSegment(sketch, "E386", {"start": v(351.48, 118.53) * mm, "end": v(355.95, 118.53) * mm});
            skArc(sketch, "E387", {"start": v(356.38, 118.28) * mm, "mid": v(356.2, 118.46) * mm, "end": v(355.95, 118.53) * mm});
            skArc(sketch, "E388", {"start": v(356.38, 118.28) * mm, "mid": v(357.17, 118.17) * mm, "end": v(357.07, 118.96) * mm});
            skArc(sketch, "E389", {"start": v(356.82, 119.4) * mm, "mid": v(356.88, 119.14) * mm, "end": v(357.07, 118.96) * mm});
            skLineSegment(sketch, "E390", {"start": v(356.82, 119.4) * mm, "end": v(356.82, 120.96) * mm});
            skArc(sketch, "E391", {"start": v(357.07, 121.4) * mm, "mid": v(356.88, 121.2) * mm, "end": v(356.82, 120.96) * mm});
            skArc(sketch, "E392", {"start": v(357.07, 121.4) * mm, "mid": v(357.17, 122.18) * mm, "end": v(356.38, 122.07) * mm});
            skArc(sketch, "E393", {"start": v(355.95, 121.83) * mm, "mid": v(356.2, 121.9) * mm, "end": v(356.38, 122.07) * mm});
            skLineSegment(sketch, "E394", {"start": v(355.95, 121.83) * mm, "end": v(351.48, 121.82) * mm});
            skArc(sketch, "E395", {"start": v(351.05, 122.07) * mm, "mid": v(351.23, 121.9) * mm, "end": v(351.48, 121.82) * mm});
            skArc(sketch, "E396", {"start": v(351.05, 122.07) * mm, "mid": v(350.26, 122.18) * mm, "end": v(350.37, 121.4) * mm});
            skArc(sketch, "E397", {"start": v(350.62, 120.96) * mm, "mid": v(350.55, 121.2) * mm, "end": v(350.37, 121.4) * mm});
            skLineSegment(sketch, "E398", {"start": v(350.62, 120.96) * mm, "end": v(350.62, 119.4) * mm});
            skArc(sketch, "E399", {"start": v(251.82, 120.96) * mm, "mid": v(251.75, 121.2) * mm, "end": v(251.57, 121.4) * mm});
            skArc(sketch, "E400", {"start": v(252.25, 122.07) * mm, "mid": v(251.46, 122.18) * mm, "end": v(251.57, 121.4) * mm});
            skArc(sketch, "E401", {"start": v(252.25, 122.07) * mm, "mid": v(252.43, 121.9) * mm, "end": v(252.68, 121.82) * mm});
            skLineSegment(sketch, "E402", {"start": v(252.68, 121.82) * mm, "end": v(257.15, 121.82) * mm});
            skArc(sketch, "E403", {"start": v(257.15, 121.82) * mm, "mid": v(257.4, 121.9) * mm, "end": v(257.58, 122.07) * mm});
            skArc(sketch, "E404", {"start": v(258.27, 121.4) * mm, "mid": v(258.37, 122.18) * mm, "end": v(257.58, 122.07) * mm});
            skArc(sketch, "E405", {"start": v(258.27, 121.4) * mm, "mid": v(258.08, 121.2) * mm, "end": v(258.02, 120.96) * mm});
            skLineSegment(sketch, "E406", {"start": v(258.02, 120.96) * mm, "end": v(258.02, 119.4) * mm});
            skArc(sketch, "E407", {"start": v(258.02, 119.4) * mm, "mid": v(258.08, 119.14) * mm, "end": v(258.27, 118.96) * mm});
            skArc(sketch, "E408", {"start": v(257.58, 118.28) * mm, "mid": v(258.37, 118.17) * mm, "end": v(258.27, 118.96) * mm});
            skArc(sketch, "E409", {"start": v(257.58, 118.28) * mm, "mid": v(257.4, 118.46) * mm, "end": v(257.15, 118.53) * mm});
            skLineSegment(sketch, "E410", {"start": v(257.15, 118.53) * mm, "end": v(252.68, 118.53) * mm});
            skArc(sketch, "E411", {"start": v(252.68, 118.53) * mm, "mid": v(252.43, 118.46) * mm, "end": v(252.25, 118.28) * mm});
            skArc(sketch, "E412", {"start": v(251.57, 118.96) * mm, "mid": v(251.46, 118.17) * mm, "end": v(252.25, 118.28) * mm});
            skArc(sketch, "E413", {"start": v(251.57, 118.96) * mm, "mid": v(251.75, 119.14) * mm, "end": v(251.82, 119.4) * mm});
            skLineSegment(sketch, "E414", {"start": v(251.82, 119.4) * mm, "end": v(251.82, 120.96) * mm});
            skArc(sketch, "E415", {"start": v(230.62, 120.96) * mm, "mid": v(230.55, 121.2) * mm, "end": v(230.37, 121.4) * mm});
            skArc(sketch, "E416", {"start": v(231.05, 122.07) * mm, "mid": v(230.26, 122.18) * mm, "end": v(230.37, 121.4) * mm});
            skArc(sketch, "E417", {"start": v(231.05, 122.07) * mm, "mid": v(231.23, 121.9) * mm, "end": v(231.48, 121.82) * mm});
            skLineSegment(sketch, "E418", {"start": v(231.48, 121.82) * mm, "end": v(235.95, 121.82) * mm});
            skArc(sketch, "E419", {"start": v(235.95, 121.82) * mm, "mid": v(236.2, 121.9) * mm, "end": v(236.38, 122.07) * mm});
            skArc(sketch, "E420", {"start": v(237.07, 121.4) * mm, "mid": v(237.17, 122.18) * mm, "end": v(236.38, 122.07) * mm});
            skArc(sketch, "E421", {"start": v(237.07, 121.4) * mm, "mid": v(236.88, 121.2) * mm, "end": v(236.82, 120.96) * mm});
            skLineSegment(sketch, "E422", {"start": v(236.82, 120.96) * mm, "end": v(236.82, 119.4) * mm});
            skArc(sketch, "E423", {"start": v(236.82, 119.4) * mm, "mid": v(236.88, 119.14) * mm, "end": v(237.07, 118.96) * mm});
            skArc(sketch, "E424", {"start": v(236.38, 118.28) * mm, "mid": v(237.17, 118.17) * mm, "end": v(237.07, 118.96) * mm});
            skArc(sketch, "E425", {"start": v(236.38, 118.28) * mm, "mid": v(236.2, 118.46) * mm, "end": v(235.95, 118.53) * mm});
            skLineSegment(sketch, "E426", {"start": v(235.95, 118.53) * mm, "end": v(231.48, 118.53) * mm});
            skArc(sketch, "E427", {"start": v(231.48, 118.53) * mm, "mid": v(231.23, 118.46) * mm, "end": v(231.05, 118.28) * mm});
            skArc(sketch, "E428", {"start": v(230.37, 118.96) * mm, "mid": v(230.26, 118.17) * mm, "end": v(231.05, 118.28) * mm});
            skArc(sketch, "E429", {"start": v(230.37, 118.96) * mm, "mid": v(230.55, 119.14) * mm, "end": v(230.62, 119.4) * mm});
            skLineSegment(sketch, "E430", {"start": v(230.62, 119.4) * mm, "end": v(230.62, 120.96) * mm});
            skArc(sketch, "E431", {"start": v(91.82, 120.96) * mm, "mid": v(91.75, 121.2) * mm, "end": v(91.57, 121.4) * mm});
            skArc(sketch, "E432", {"start": v(92.25, 122.07) * mm, "mid": v(91.46, 122.18) * mm, "end": v(91.57, 121.4) * mm});
            skArc(sketch, "E433", {"start": v(92.25, 122.07) * mm, "mid": v(92.43, 121.9) * mm, "end": v(92.68, 121.82) * mm});
            skLineSegment(sketch, "E434", {"start": v(92.68, 121.82) * mm, "end": v(97.15, 121.82) * mm});
            skArc(sketch, "E435", {"start": v(97.15, 121.82) * mm, "mid": v(97.4, 121.9) * mm, "end": v(97.58, 122.07) * mm});
            skArc(sketch, "E436", {"start": v(98.27, 121.4) * mm, "mid": v(98.37, 122.18) * mm, "end": v(97.58, 122.07) * mm});
            skArc(sketch, "E437", {"start": v(98.27, 121.4) * mm, "mid": v(98.08, 121.2) * mm, "end": v(98.02, 120.96) * mm});
            skLineSegment(sketch, "E438", {"start": v(98.02, 120.96) * mm, "end": v(98.02, 119.4) * mm});
            skArc(sketch, "E439", {"start": v(98.02, 119.4) * mm, "mid": v(98.08, 119.14) * mm, "end": v(98.27, 118.96) * mm});
            skArc(sketch, "E440", {"start": v(97.58, 118.28) * mm, "mid": v(98.37, 118.17) * mm, "end": v(98.27, 118.96) * mm});
            skArc(sketch, "E441", {"start": v(97.58, 118.28) * mm, "mid": v(97.4, 118.46) * mm, "end": v(97.15, 118.53) * mm});
            skLineSegment(sketch, "E442", {"start": v(97.15, 118.53) * mm, "end": v(92.68, 118.53) * mm});
            skArc(sketch, "E443", {"start": v(92.68, 118.53) * mm, "mid": v(92.43, 118.46) * mm, "end": v(92.25, 118.28) * mm});
            skArc(sketch, "E444", {"start": v(91.57, 118.96) * mm, "mid": v(91.46, 118.17) * mm, "end": v(92.25, 118.28) * mm});
            skArc(sketch, "E445", {"start": v(91.57, 118.96) * mm, "mid": v(91.75, 119.14) * mm, "end": v(91.82, 119.4) * mm});
            skLineSegment(sketch, "E446", {"start": v(91.82, 119.4) * mm, "end": v(91.82, 120.96) * mm});
            skArc(sketch, "E447", {"start": v(70.62, 120.96) * mm, "mid": v(70.55, 121.2) * mm, "end": v(70.37, 121.4) * mm});
            skArc(sketch, "E448", {"start": v(71.05, 122.07) * mm, "mid": v(70.26, 122.18) * mm, "end": v(70.37, 121.4) * mm});
            skArc(sketch, "E449", {"start": v(71.05, 122.07) * mm, "mid": v(71.23, 121.9) * mm, "end": v(71.48, 121.82) * mm});
            skLineSegment(sketch, "E450", {"start": v(71.48, 121.82) * mm, "end": v(75.95, 121.82) * mm});
            skArc(sketch, "E451", {"start": v(75.95, 121.82) * mm, "mid": v(76.2, 121.9) * mm, "end": v(76.38, 122.07) * mm});
            skArc(sketch, "E452", {"start": v(77.07, 121.4) * mm, "mid": v(77.17, 122.18) * mm, "end": v(76.38, 122.07) * mm});
            skArc(sketch, "E453", {"start": v(77.07, 121.4) * mm, "mid": v(76.88, 121.2) * mm, "end": v(76.82, 120.96) * mm});
            skLineSegment(sketch, "E454", {"start": v(76.82, 120.96) * mm, "end": v(76.82, 119.4) * mm});
            skArc(sketch, "E455", {"start": v(76.82, 119.4) * mm, "mid": v(76.88, 119.14) * mm, "end": v(77.07, 118.96) * mm});
            skArc(sketch, "E456", {"start": v(76.38, 118.28) * mm, "mid": v(77.17, 118.17) * mm, "end": v(77.07, 118.96) * mm});
            skArc(sketch, "E457", {"start": v(76.38, 118.28) * mm, "mid": v(76.2, 118.46) * mm, "end": v(75.95, 118.53) * mm});
            skLineSegment(sketch, "E458", {"start": v(75.95, 118.53) * mm, "end": v(71.48, 118.53) * mm});
            skArc(sketch, "E459", {"start": v(71.48, 118.53) * mm, "mid": v(71.23, 118.46) * mm, "end": v(71.05, 118.28) * mm});
            skArc(sketch, "E460", {"start": v(70.37, 118.96) * mm, "mid": v(70.26, 118.17) * mm, "end": v(71.05, 118.28) * mm});
            skArc(sketch, "E461", {"start": v(70.37, 118.96) * mm, "mid": v(70.55, 119.14) * mm, "end": v(70.62, 119.4) * mm});
            skLineSegment(sketch, "E462", {"start": v(70.62, 119.4) * mm, "end": v(70.62, 120.96) * mm});
            skArc(sketch, "E463", {"start": v(411.57, 139.56) * mm, "mid": v(411.75, 139.75) * mm, "end": v(411.82, 140) * mm});
            skArc(sketch, "E464", {"start": v(411.57, 139.56) * mm, "mid": v(411.46, 138.78) * mm, "end": v(412.25, 138.88) * mm});
            skArc(sketch, "E465", {"start": v(412.68, 139.13) * mm, "mid": v(412.43, 139.06) * mm, "end": v(412.25, 138.88) * mm});
            skLineSegment(sketch, "E466", {"start": v(412.68, 139.13) * mm, "end": v(417.15, 139.13) * mm});
            skArc(sketch, "E467", {"start": v(417.58, 138.88) * mm, "mid": v(417.4, 139.06) * mm, "end": v(417.15, 139.13) * mm});
            skArc(sketch, "E468", {"start": v(417.58, 138.88) * mm, "mid": v(418.37, 138.78) * mm, "end": v(418.27, 139.56) * mm});
            skArc(sketch, "E469", {"start": v(418.02, 140) * mm, "mid": v(418.08, 139.75) * mm, "end": v(418.27, 139.56) * mm});
            skLineSegment(sketch, "E470", {"start": v(418.02, 140) * mm, "end": v(418.02, 141.56) * mm});
            skArc(sketch, "E471", {"start": v(418.27, 142) * mm, "mid": v(418.08, 141.81) * mm, "end": v(418.02, 141.56) * mm});
            skArc(sketch, "E472", {"start": v(418.27, 142) * mm, "mid": v(418.37, 142.78) * mm, "end": v(417.58, 142.68) * mm});
            skArc(sketch, "E473", {"start": v(417.15, 142.43) * mm, "mid": v(417.4, 142.5) * mm, "end": v(417.58, 142.68) * mm});
            skLineSegment(sketch, "E474", {"start": v(417.15, 142.43) * mm, "end": v(412.68, 142.43) * mm});
            skArc(sketch, "E475", {"start": v(412.25, 142.68) * mm, "mid": v(412.43, 142.5) * mm, "end": v(412.68, 142.43) * mm});
            skArc(sketch, "E476", {"start": v(412.25, 142.68) * mm, "mid": v(411.46, 142.78) * mm, "end": v(411.57, 142) * mm});
            skArc(sketch, "E477", {"start": v(411.82, 141.56) * mm, "mid": v(411.75, 141.81) * mm, "end": v(411.57, 142) * mm});
            skLineSegment(sketch, "E478", {"start": v(411.82, 141.56) * mm, "end": v(411.82, 140) * mm});
            skArc(sketch, "E479", {"start": v(390.37, 139.56) * mm, "mid": v(390.55, 139.75) * mm, "end": v(390.62, 140) * mm});
            skArc(sketch, "E480", {"start": v(390.37, 139.56) * mm, "mid": v(390.26, 138.78) * mm, "end": v(391.05, 138.88) * mm});
            skArc(sketch, "E481", {"start": v(391.48, 139.13) * mm, "mid": v(391.23, 139.06) * mm, "end": v(391.05, 138.88) * mm});
            skLineSegment(sketch, "E482", {"start": v(391.48, 139.13) * mm, "end": v(395.95, 139.13) * mm});
            skArc(sketch, "E483", {"start": v(396.38, 138.88) * mm, "mid": v(396.2, 139.06) * mm, "end": v(395.95, 139.13) * mm});
            skArc(sketch, "E484", {"start": v(396.38, 138.88) * mm, "mid": v(397.17, 138.78) * mm, "end": v(397.07, 139.56) * mm});
            skArc(sketch, "E485", {"start": v(396.82, 140) * mm, "mid": v(396.88, 139.75) * mm, "end": v(397.07, 139.56) * mm});
            skLineSegment(sketch, "E486", {"start": v(396.82, 140) * mm, "end": v(396.82, 141.56) * mm});
            skArc(sketch, "E487", {"start": v(397.07, 142) * mm, "mid": v(396.88, 141.81) * mm, "end": v(396.82, 141.56) * mm});
            skArc(sketch, "E488", {"start": v(397.07, 142) * mm, "mid": v(397.17, 142.78) * mm, "end": v(396.38, 142.68) * mm});
            skArc(sketch, "E489", {"start": v(395.95, 142.43) * mm, "mid": v(396.2, 142.5) * mm, "end": v(396.38, 142.68) * mm});
            skLineSegment(sketch, "E490", {"start": v(395.95, 142.43) * mm, "end": v(391.48, 142.43) * mm});
            skArc(sketch, "E491", {"start": v(391.05, 142.68) * mm, "mid": v(391.23, 142.5) * mm, "end": v(391.48, 142.43) * mm});
            skArc(sketch, "E492", {"start": v(391.05, 142.68) * mm, "mid": v(390.26, 142.78) * mm, "end": v(390.37, 142) * mm});
            skArc(sketch, "E493", {"start": v(390.62, 141.56) * mm, "mid": v(390.55, 141.81) * mm, "end": v(390.37, 142) * mm});
            skLineSegment(sketch, "E494", {"start": v(390.62, 141.56) * mm, "end": v(390.62, 140) * mm});
            skArc(sketch, "E495", {"start": v(376.46, 158.05) * mm, "mid": v(376.64, 157.87) * mm, "end": v(376.89, 157.8) * mm});
            skArc(sketch, "E496", {"start": v(376.46, 158.05) * mm, "mid": v(375.67, 158.15) * mm, "end": v(375.77, 157.37) * mm});
            skArc(sketch, "E497", {"start": v(376.02, 156.93) * mm, "mid": v(375.96, 157.18) * mm, "end": v(375.77, 157.37) * mm});
            skLineSegment(sketch, "E498", {"start": v(376.02, 156.93) * mm, "end": v(376.02, 152.47) * mm});
            skArc(sketch, "E499", {"start": v(375.77, 152.03) * mm, "mid": v(375.96, 152.22) * mm, "end": v(376.02, 152.47) * mm});
            skArc(sketch, "E500", {"start": v(375.77, 152.03) * mm, "mid": v(375.67, 151.25) * mm, "end": v(376.46, 151.35) * mm});
            skArc(sketch, "E501", {"start": v(376.89, 151.6) * mm, "mid": v(376.64, 151.53) * mm, "end": v(376.46, 151.35) * mm});
            skLineSegment(sketch, "E502", {"start": v(376.89, 151.6) * mm, "end": v(378.46, 151.6) * mm});
            skArc(sketch, "E503", {"start": v(378.89, 151.35) * mm, "mid": v(378.7, 151.53) * mm, "end": v(378.46, 151.6) * mm});
            skArc(sketch, "E504", {"start": v(378.89, 151.35) * mm, "mid": v(379.68, 151.25) * mm, "end": v(379.57, 152.03) * mm});
            skArc(sketch, "E505", {"start": v(379.32, 152.47) * mm, "mid": v(379.39, 152.22) * mm, "end": v(379.57, 152.03) * mm});
            skLineSegment(sketch, "E506", {"start": v(379.32, 152.47) * mm, "end": v(379.32, 156.93) * mm});
            skArc(sketch, "E507", {"start": v(379.57, 157.37) * mm, "mid": v(379.39, 157.18) * mm, "end": v(379.32, 156.93) * mm});
            skArc(sketch, "E508", {"start": v(379.57, 157.37) * mm, "mid": v(379.68, 158.15) * mm, "end": v(378.89, 158.05) * mm});
            skArc(sketch, "E509", {"start": v(378.46, 157.8) * mm, "mid": v(378.7, 157.87) * mm, "end": v(378.89, 158.05) * mm});
            skLineSegment(sketch, "E510", {"start": v(378.46, 157.8) * mm, "end": v(376.89, 157.8) * mm});
            skArc(sketch, "E511", {"start": v(376.46, 179.25) * mm, "mid": v(376.64, 179.07) * mm, "end": v(376.89, 179) * mm});
            skArc(sketch, "E512", {"start": v(376.46, 179.25) * mm, "mid": v(375.67, 179.35) * mm, "end": v(375.77, 178.57) * mm});
            skArc(sketch, "E513", {"start": v(376.02, 178.13) * mm, "mid": v(375.96, 178.38) * mm, "end": v(375.77, 178.57) * mm});
            skLineSegment(sketch, "E514", {"start": v(376.02, 178.13) * mm, "end": v(376.02, 173.67) * mm});
            skArc(sketch, "E515", {"start": v(375.77, 173.23) * mm, "mid": v(375.96, 173.42) * mm, "end": v(376.02, 173.67) * mm});
            skArc(sketch, "E516", {"start": v(375.77, 173.23) * mm, "mid": v(375.67, 172.45) * mm, "end": v(376.46, 172.55) * mm});
            skArc(sketch, "E517", {"start": v(376.89, 172.8) * mm, "mid": v(376.64, 172.73) * mm, "end": v(376.46, 172.55) * mm});
            skLineSegment(sketch, "E518", {"start": v(376.89, 172.8) * mm, "end": v(378.46, 172.8) * mm});
            skArc(sketch, "E519", {"start": v(378.89, 172.55) * mm, "mid": v(378.7, 172.73) * mm, "end": v(378.46, 172.8) * mm});
            skArc(sketch, "E520", {"start": v(378.89, 172.55) * mm, "mid": v(379.68, 172.45) * mm, "end": v(379.57, 173.23) * mm});
            skArc(sketch, "E521", {"start": v(379.32, 173.67) * mm, "mid": v(379.39, 173.42) * mm, "end": v(379.57, 173.23) * mm});
            skLineSegment(sketch, "E522", {"start": v(379.32, 173.67) * mm, "end": v(379.32, 178.13) * mm});
            skArc(sketch, "E523", {"start": v(379.57, 178.57) * mm, "mid": v(379.39, 178.38) * mm, "end": v(379.32, 178.13) * mm});
            skArc(sketch, "E524", {"start": v(379.57, 178.57) * mm, "mid": v(379.68, 179.35) * mm, "end": v(378.89, 179.25) * mm});
            skArc(sketch, "E525", {"start": v(378.46, 179) * mm, "mid": v(378.7, 179.07) * mm, "end": v(378.89, 179.25) * mm});
            skLineSegment(sketch, "E526", {"start": v(378.46, 179) * mm, "end": v(376.89, 179) * mm});
            skArc(sketch, "E527", {"start": v(411.57, 188.6) * mm, "mid": v(411.75, 188.79) * mm, "end": v(411.82, 189.04) * mm});
            skArc(sketch, "E528", {"start": v(411.57, 188.6) * mm, "mid": v(411.46, 187.82) * mm, "end": v(412.25, 187.92) * mm});
            skArc(sketch, "E529", {"start": v(412.68, 188.17) * mm, "mid": v(412.43, 188.1) * mm, "end": v(412.25, 187.92) * mm});
            skLineSegment(sketch, "E530", {"start": v(412.68, 188.17) * mm, "end": v(417.15, 188.17) * mm});
            skArc(sketch, "E531", {"start": v(417.58, 187.92) * mm, "mid": v(417.4, 188.1) * mm, "end": v(417.15, 188.17) * mm});
            skArc(sketch, "E532", {"start": v(417.58, 187.92) * mm, "mid": v(418.37, 187.82) * mm, "end": v(418.27, 188.6) * mm});
            skArc(sketch, "E533", {"start": v(418.02, 189.04) * mm, "mid": v(418.08, 188.79) * mm, "end": v(418.27, 188.6) * mm});
            skLineSegment(sketch, "E534", {"start": v(418.02, 189.04) * mm, "end": v(418.02, 190.6) * mm});
            skArc(sketch, "E535", {"start": v(418.27, 191.04) * mm, "mid": v(418.08, 190.85) * mm, "end": v(418.02, 190.6) * mm});
            skArc(sketch, "E536", {"start": v(418.27, 191.04) * mm, "mid": v(418.37, 191.82) * mm, "end": v(417.58, 191.72) * mm});
            skArc(sketch, "E537", {"start": v(417.15, 191.47) * mm, "mid": v(417.4, 191.54) * mm, "end": v(417.58, 191.72) * mm});
            skLineSegment(sketch, "E538", {"start": v(417.15, 191.47) * mm, "end": v(412.68, 191.47) * mm});
            skArc(sketch, "E539", {"start": v(412.25, 191.72) * mm, "mid": v(412.43, 191.54) * mm, "end": v(412.68, 191.47) * mm});
            skArc(sketch, "E540", {"start": v(412.25, 191.72) * mm, "mid": v(411.46, 191.82) * mm, "end": v(411.57, 191.04) * mm});
            skArc(sketch, "E541", {"start": v(411.82, 190.6) * mm, "mid": v(411.75, 190.85) * mm, "end": v(411.57, 191.04) * mm});
            skLineSegment(sketch, "E542", {"start": v(411.82, 190.6) * mm, "end": v(411.82, 189.04) * mm});
            skArc(sketch, "E543", {"start": v(390.37, 188.6) * mm, "mid": v(390.55, 188.79) * mm, "end": v(390.62, 189.04) * mm});
            skArc(sketch, "E544", {"start": v(390.37, 188.6) * mm, "mid": v(390.26, 187.82) * mm, "end": v(391.05, 187.92) * mm});
            skArc(sketch, "E545", {"start": v(391.48, 188.17) * mm, "mid": v(391.23, 188.1) * mm, "end": v(391.05, 187.92) * mm});
            skLineSegment(sketch, "E546", {"start": v(391.48, 188.17) * mm, "end": v(395.95, 188.17) * mm});
            skArc(sketch, "E547", {"start": v(396.38, 187.92) * mm, "mid": v(396.2, 188.1) * mm, "end": v(395.95, 188.17) * mm});
            skArc(sketch, "E548", {"start": v(396.38, 187.92) * mm, "mid": v(397.17, 187.82) * mm, "end": v(397.07, 188.6) * mm});
            skArc(sketch, "E549", {"start": v(396.82, 189.04) * mm, "mid": v(396.88, 188.79) * mm, "end": v(397.07, 188.6) * mm});
            skLineSegment(sketch, "E550", {"start": v(396.82, 189.04) * mm, "end": v(396.82, 190.6) * mm});
            skArc(sketch, "E551", {"start": v(397.07, 191.04) * mm, "mid": v(396.88, 190.85) * mm, "end": v(396.82, 190.6) * mm});
            skArc(sketch, "E552", {"start": v(397.07, 191.04) * mm, "mid": v(397.17, 191.82) * mm, "end": v(396.38, 191.72) * mm});
            skArc(sketch, "E553", {"start": v(395.95, 191.47) * mm, "mid": v(396.2, 191.54) * mm, "end": v(396.38, 191.72) * mm});
            skLineSegment(sketch, "E554", {"start": v(395.95, 191.47) * mm, "end": v(391.48, 191.47) * mm});
            skArc(sketch, "E555", {"start": v(391.05, 191.72) * mm, "mid": v(391.23, 191.54) * mm, "end": v(391.48, 191.47) * mm});
            skArc(sketch, "E556", {"start": v(391.05, 191.72) * mm, "mid": v(390.26, 191.82) * mm, "end": v(390.37, 191.04) * mm});
            skArc(sketch, "E557", {"start": v(390.62, 190.6) * mm, "mid": v(390.55, 190.85) * mm, "end": v(390.37, 191.04) * mm});
            skLineSegment(sketch, "E558", {"start": v(390.62, 190.6) * mm, "end": v(390.62, 189.04) * mm});
            skCircle(sketch, "E559", {"center": v(404.32, -189.82) * mm, "radius": 1.6 * mm});
            skCircle(sketch, "E560", {"center": v(377.67, -165.3) * mm, "radius": 1.6 * mm});
            skCircle(sketch, "E561", {"center": v(404.32, -140.78) * mm, "radius": 1.6 * mm});
            skCircle(sketch, "E562", {"center": v(364.32, -120.17) * mm, "radius": 1.6 * mm});
            skCircle(sketch, "E563", {"center": v(244.32, -120.18) * mm, "radius": 1.6 * mm});
            skCircle(sketch, "E564", {"center": v(84.32, -120.18) * mm, "radius": 1.6 * mm});
            skCircle(sketch, "E565", {"center": v(364.32, 120.18) * mm, "radius": 1.6 * mm});
            skCircle(sketch, "E566", {"center": v(244.32, 120.17) * mm, "radius": 1.6 * mm});
            skCircle(sketch, "E567", {"center": v(84.32, 120.17) * mm, "radius": 1.6 * mm});
            skCircle(sketch, "E568", {"center": v(404.32, 140.78) * mm, "radius": 1.6 * mm});
            skCircle(sketch, "E569", {"center": v(377.67, 165.3) * mm, "radius": 1.6 * mm});
            skCircle(sketch, "E570", {"center": v(404.32, 189.82) * mm, "radius": 1.6 * mm});
            skArc(sketch, "E571", {"start": v(-390.28, -188.9) * mm, "mid": v(-390.1, -189.08) * mm, "end": v(-389.85, -189.14) * mm});
            skArc(sketch, "E572", {"start": v(-390.28, -188.9) * mm, "mid": v(-391.07, -188.8) * mm, "end": v(-390.97, -189.58) * mm});
            skArc(sketch, "E573", {"start": v(-390.72, -190.01) * mm, "mid": v(-390.78, -189.76) * mm, "end": v(-390.97, -189.58) * mm});
            skLineSegment(sketch, "E574", {"start": v(-390.72, -190.01) * mm, "end": v(-390.72, -191.64) * mm});
            skArc(sketch, "E575", {"start": v(-391.22, -192.14) * mm, "mid": v(-390.86, -192) * mm, "end": v(-390.72, -191.64) * mm});
            skLineSegment(sketch, "E576", {"start": v(-391.22, -192.14) * mm, "end": v(-396.22, -192.14) * mm});
            skArc(sketch, "E577", {"start": v(-396.72, -191.64) * mm, "mid": v(-396.57, -192) * mm, "end": v(-396.22, -192.14) * mm});
            skLineSegment(sketch, "E578", {"start": v(-396.72, -191.64) * mm, "end": v(-396.72, -190.01) * mm});
            skArc(sketch, "E579", {"start": v(-396.47, -189.58) * mm, "mid": v(-396.65, -189.76) * mm, "end": v(-396.72, -190.01) * mm});
            skArc(sketch, "E580", {"start": v(-396.47, -189.58) * mm, "mid": v(-396.36, -188.8) * mm, "end": v(-397.15, -188.9) * mm});
            skArc(sketch, "E581", {"start": v(-397.58, -189.14) * mm, "mid": v(-397.33, -189.08) * mm, "end": v(-397.15, -188.9) * mm});
            skLineSegment(sketch, "E582", {"start": v(-397.58, -189.14) * mm, "end": v(-402.72, -189.14) * mm});
            skLineSegment(sketch, "E583", {"start": v(-402.72, -189.14) * mm, "end": v(-402.72, -186.14) * mm});
            skLineSegment(sketch, "E584", {"start": v(-402.72, -186.14) * mm, "end": v(-401.44, -186.14) * mm});
            skLineSegment(sketch, "E585", {"start": v(-401.44, -186.14) * mm, "end": v(-401.44, -182.14) * mm});
            skLineSegment(sketch, "E586", {"start": v(-401.44, -182.14) * mm, "end": v(-402.72, -182.14) * mm});
            skLineSegment(sketch, "E587", {"start": v(-402.72, -182.14) * mm, "end": v(-402.72, -179.14) * mm});
            skLineSegment(sketch, "E588", {"start": v(-402.72, -179.14) * mm, "end": v(-405.92, -179.14) * mm});
            skLineSegment(sketch, "E589", {"start": v(-405.92, -179.14) * mm, "end": v(-405.92, -182.14) * mm});
            skLineSegment(sketch, "E590", {"start": v(-405.92, -182.14) * mm, "end": v(-407.2, -182.14) * mm});
            skLineSegment(sketch, "E591", {"start": v(-407.2, -182.14) * mm, "end": v(-407.2, -186.14) * mm});
            skLineSegment(sketch, "E592", {"start": v(-407.2, -186.14) * mm, "end": v(-405.92, -186.14) * mm});
            skLineSegment(sketch, "E593", {"start": v(-405.92, -186.14) * mm, "end": v(-405.92, -189.14) * mm});
            skLineSegment(sketch, "E594", {"start": v(-405.92, -189.14) * mm, "end": v(-411.05, -189.14) * mm});
            skArc(sketch, "E595", {"start": v(-411.48, -188.9) * mm, "mid": v(-411.3, -189.08) * mm, "end": v(-411.05, -189.14) * mm});
            skArc(sketch, "E596", {"start": v(-411.48, -188.9) * mm, "mid": v(-412.27, -188.8) * mm, "end": v(-412.17, -189.58) * mm});
            skArc(sketch, "E597", {"start": v(-411.92, -190.01) * mm, "mid": v(-411.98, -189.76) * mm, "end": v(-412.17, -189.58) * mm});
            skLineSegment(sketch, "E598", {"start": v(-411.92, -190.01) * mm, "end": v(-411.92, -191.64) * mm});
            skArc(sketch, "E599", {"start": v(-412.42, -192.14) * mm, "mid": v(-412.06, -192) * mm, "end": v(-411.92, -191.64) * mm});
            skLineSegment(sketch, "E600", {"start": v(-412.42, -192.14) * mm, "end": v(-417.42, -192.14) * mm});
            skArc(sketch, "E601", {"start": v(-417.92, -191.64) * mm, "mid": v(-417.77, -192) * mm, "end": v(-417.42, -192.14) * mm});
            skLineSegment(sketch, "E602", {"start": v(-417.92, -191.64) * mm, "end": v(-417.92, -190.01) * mm});
            skArc(sketch, "E603", {"start": v(-417.67, -189.58) * mm, "mid": v(-417.85, -189.76) * mm, "end": v(-417.92, -190.01) * mm});
            skArc(sketch, "E604", {"start": v(-417.67, -189.58) * mm, "mid": v(-417.56, -188.8) * mm, "end": v(-418.35, -188.9) * mm});
            skArc(sketch, "E605", {"start": v(-418.78, -189.14) * mm, "mid": v(-418.53, -189.08) * mm, "end": v(-418.35, -188.9) * mm});
            skLineSegment(sketch, "E606", {"start": v(-418.78, -189.14) * mm, "end": v(-429.32, -189.14) * mm});
            skLineSegment(sketch, "E607", {"start": v(-429.32, -189.14) * mm, "end": v(-429.32, -168.14) * mm});
            skLineSegment(sketch, "E608", {"start": v(-429.32, -168.14) * mm, "end": v(-427.32, -166.14) * mm});
            skLineSegment(sketch, "E609", {"start": v(-427.32, -166.14) * mm, "end": v(-427.32, -64.14) * mm});
            skLineSegment(sketch, "E610", {"start": v(-427.32, -64.14) * mm, "end": v(-418.78, -64.14) * mm});
            skArc(sketch, "E611", {"start": v(-418.35, -64.4) * mm, "mid": v(-418.53, -64.21) * mm, "end": v(-418.78, -64.14) * mm});
            skArc(sketch, "E612", {"start": v(-418.35, -64.4) * mm, "mid": v(-417.56, -64.5) * mm, "end": v(-417.67, -63.71) * mm});
            skArc(sketch, "E613", {"start": v(-417.92, -63.28) * mm, "mid": v(-417.85, -63.53) * mm, "end": v(-417.67, -63.71) * mm});
            skLineSegment(sketch, "E614", {"start": v(-417.92, -63.28) * mm, "end": v(-417.92, 148.36) * mm});
            skArc(sketch, "E615", {"start": v(-417.42, 148.86) * mm, "mid": v(-417.77, 148.7) * mm, "end": v(-417.92, 148.36) * mm});
            skLineSegment(sketch, "E616", {"start": v(-417.42, 148.86) * mm, "end": v(-412.42, 148.86) * mm});
            skArc(sketch, "E617", {"start": v(-411.92, 148.36) * mm, "mid": v(-412.06, 148.7) * mm, "end": v(-412.42, 148.86) * mm});
            skLineSegment(sketch, "E618", {"start": v(-411.92, 148.36) * mm, "end": v(-411.92, 146.72) * mm});
            skArc(sketch, "E619", {"start": v(-412.17, 146.29) * mm, "mid": v(-411.98, 146.47) * mm, "end": v(-411.92, 146.72) * mm});
            skArc(sketch, "E620", {"start": v(-412.17, 146.29) * mm, "mid": v(-412.27, 145.5) * mm, "end": v(-411.48, 145.6) * mm});
            skArc(sketch, "E621", {"start": v(-411.05, 145.86) * mm, "mid": v(-411.3, 145.79) * mm, "end": v(-411.48, 145.6) * mm});
            skLineSegment(sketch, "E622", {"start": v(-411.05, 145.86) * mm, "end": v(-405.92, 145.86) * mm});
            skLineSegment(sketch, "E623", {"start": v(-405.92, 145.86) * mm, "end": v(-405.92, 142.86) * mm});
            skLineSegment(sketch, "E624", {"start": v(-405.92, 142.86) * mm, "end": v(-407.2, 142.86) * mm});
            skLineSegment(sketch, "E625", {"start": v(-407.2, 142.86) * mm, "end": v(-407.2, 138.86) * mm});
            skLineSegment(sketch, "E626", {"start": v(-407.2, 138.86) * mm, "end": v(-405.92, 138.86) * mm});
            skLineSegment(sketch, "E627", {"start": v(-405.92, 138.86) * mm, "end": v(-405.92, 135.86) * mm});
            skLineSegment(sketch, "E628", {"start": v(-405.92, 135.86) * mm, "end": v(-402.72, 135.86) * mm});
            skLineSegment(sketch, "E629", {"start": v(-402.72, 135.86) * mm, "end": v(-402.72, 138.86) * mm});
            skLineSegment(sketch, "E630", {"start": v(-402.72, 138.86) * mm, "end": v(-401.44, 138.86) * mm});
            skLineSegment(sketch, "E631", {"start": v(-401.44, 138.86) * mm, "end": v(-401.44, 142.86) * mm});
            skLineSegment(sketch, "E632", {"start": v(-401.44, 142.86) * mm, "end": v(-402.72, 142.86) * mm});
            skLineSegment(sketch, "E633", {"start": v(-402.72, 142.86) * mm, "end": v(-402.72, 145.86) * mm});
            skLineSegment(sketch, "E634", {"start": v(-402.72, 145.86) * mm, "end": v(-397.58, 145.86) * mm});
            skArc(sketch, "E635", {"start": v(-397.15, 145.6) * mm, "mid": v(-397.33, 145.79) * mm, "end": v(-397.58, 145.86) * mm});
            skArc(sketch, "E636", {"start": v(-397.15, 145.6) * mm, "mid": v(-396.36, 145.5) * mm, "end": v(-396.47, 146.29) * mm});
            skArc(sketch, "E637", {"start": v(-396.72, 146.72) * mm, "mid": v(-396.65, 146.47) * mm, "end": v(-396.47, 146.29) * mm});
            skLineSegment(sketch, "E638", {"start": v(-396.72, 146.72) * mm, "end": v(-396.72, 148.36) * mm});
            skArc(sketch, "E639", {"start": v(-396.22, 148.86) * mm, "mid": v(-396.57, 148.7) * mm, "end": v(-396.72, 148.36) * mm});
            skLineSegment(sketch, "E640", {"start": v(-396.22, 148.86) * mm, "end": v(-391.22, 148.86) * mm});
            skArc(sketch, "E641", {"start": v(-390.72, 148.36) * mm, "mid": v(-390.86, 148.7) * mm, "end": v(-391.22, 148.86) * mm});
            skLineSegment(sketch, "E642", {"start": v(-390.72, 148.36) * mm, "end": v(-390.72, -63.28) * mm});
            skArc(sketch, "E643", {"start": v(-390.97, -63.71) * mm, "mid": v(-390.78, -63.53) * mm, "end": v(-390.72, -63.28) * mm});
            skArc(sketch, "E644", {"start": v(-390.97, -63.71) * mm, "mid": v(-391.07, -64.5) * mm, "end": v(-390.28, -64.4) * mm});
            skArc(sketch, "E645", {"start": v(-389.85, -64.14) * mm, "mid": v(-390.1, -64.21) * mm, "end": v(-390.28, -64.4) * mm});
            skLineSegment(sketch, "E646", {"start": v(-389.85, -64.14) * mm, "end": v(-378.78, -64.14) * mm});
            skArc(sketch, "E647", {"start": v(-378.35, -64.4) * mm, "mid": v(-378.53, -64.21) * mm, "end": v(-378.78, -64.14) * mm});
            skArc(sketch, "E648", {"start": v(-378.35, -64.4) * mm, "mid": v(-377.56, -64.5) * mm, "end": v(-377.67, -63.71) * mm});
            skArc(sketch, "E649", {"start": v(-377.92, -63.28) * mm, "mid": v(-377.85, -63.53) * mm, "end": v(-377.67, -63.71) * mm});
            skLineSegment(sketch, "E650", {"start": v(-377.92, -63.28) * mm, "end": v(-377.92, -61.64) * mm});
            skArc(sketch, "E651", {"start": v(-377.42, -61.14) * mm, "mid": v(-377.77, -61.3) * mm, "end": v(-377.92, -61.64) * mm});
            skLineSegment(sketch, "E652", {"start": v(-377.42, -61.14) * mm, "end": v(-372.42, -61.14) * mm});
            skArc(sketch, "E653", {"start": v(-371.92, -61.64) * mm, "mid": v(-372.06, -61.3) * mm, "end": v(-372.42, -61.14) * mm});
            skLineSegment(sketch, "E654", {"start": v(-371.92, -61.64) * mm, "end": v(-371.92, -63.28) * mm});
            skArc(sketch, "E655", {"start": v(-372.17, -63.71) * mm, "mid": v(-371.98, -63.53) * mm, "end": v(-371.92, -63.28) * mm});
            skArc(sketch, "E656", {"start": v(-372.17, -63.71) * mm, "mid": v(-372.27, -64.5) * mm, "end": v(-371.48, -64.4) * mm});
            skArc(sketch, "E657", {"start": v(-371.05, -64.14) * mm, "mid": v(-371.3, -64.21) * mm, "end": v(-371.48, -64.4) * mm});
            skLineSegment(sketch, "E658", {"start": v(-371.05, -64.14) * mm, "end": v(-365.92, -64.14) * mm});
            skLineSegment(sketch, "E659", {"start": v(-365.92, -64.14) * mm, "end": v(-365.92, -67.14) * mm});
            skLineSegment(sketch, "E660", {"start": v(-365.92, -67.14) * mm, "end": v(-367.2, -67.14) * mm});
            skLineSegment(sketch, "E661", {"start": v(-367.2, -67.14) * mm, "end": v(-367.2, -71.14) * mm});
            skLineSegment(sketch, "E662", {"start": v(-367.2, -71.14) * mm, "end": v(-365.92, -71.14) * mm});
            skLineSegment(sketch, "E663", {"start": v(-365.92, -71.14) * mm, "end": v(-365.92, -74.14) * mm});
            skLineSegment(sketch, "E664", {"start": v(-365.92, -74.14) * mm, "end": v(-362.72, -74.14) * mm});
            skLineSegment(sketch, "E665", {"start": v(-362.72, -74.14) * mm, "end": v(-362.72, -71.14) * mm});
            skLineSegment(sketch, "E666", {"start": v(-362.72, -71.14) * mm, "end": v(-361.44, -71.14) * mm});
            skLineSegment(sketch, "E667", {"start": v(-361.44, -71.14) * mm, "end": v(-361.44, -67.14) * mm});
            skLineSegment(sketch, "E668", {"start": v(-361.44, -67.14) * mm, "end": v(-362.72, -67.14) * mm});
            skLineSegment(sketch, "E669", {"start": v(-362.72, -67.14) * mm, "end": v(-362.72, -64.14) * mm});
            skLineSegment(sketch, "E670", {"start": v(-362.72, -64.14) * mm, "end": v(-357.58, -64.14) * mm});
            skArc(sketch, "E671", {"start": v(-357.15, -64.4) * mm, "mid": v(-357.33, -64.21) * mm, "end": v(-357.58, -64.14) * mm});
            skArc(sketch, "E672", {"start": v(-357.15, -64.4) * mm, "mid": v(-356.36, -64.5) * mm, "end": v(-356.47, -63.71) * mm});
            skArc(sketch, "E673", {"start": v(-356.72, -63.28) * mm, "mid": v(-356.65, -63.53) * mm, "end": v(-356.47, -63.71) * mm});
            skLineSegment(sketch, "E674", {"start": v(-356.72, -63.28) * mm, "end": v(-356.72, -61.64) * mm});
            skArc(sketch, "E675", {"start": v(-356.22, -61.14) * mm, "mid": v(-356.57, -61.3) * mm, "end": v(-356.72, -61.64) * mm});
            skLineSegment(sketch, "E676", {"start": v(-356.22, -61.14) * mm, "end": v(-351.22, -61.14) * mm});
            skArc(sketch, "E677", {"start": v(-350.72, -61.64) * mm, "mid": v(-350.86, -61.3) * mm, "end": v(-351.22, -61.14) * mm});
            skLineSegment(sketch, "E678", {"start": v(-350.72, -61.64) * mm, "end": v(-350.72, -63.28) * mm});
            skArc(sketch, "E679", {"start": v(-350.97, -63.71) * mm, "mid": v(-350.78, -63.53) * mm, "end": v(-350.72, -63.28) * mm});
            skArc(sketch, "E680", {"start": v(-350.97, -63.71) * mm, "mid": v(-351.07, -64.5) * mm, "end": v(-350.28, -64.4) * mm});
            skArc(sketch, "E681", {"start": v(-349.85, -64.14) * mm, "mid": v(-350.1, -64.21) * mm, "end": v(-350.28, -64.4) * mm});
            skLineSegment(sketch, "E682", {"start": v(-349.85, -64.14) * mm, "end": v(-258.78, -64.14) * mm});
            skArc(sketch, "E683", {"start": v(-258.35, -64.4) * mm, "mid": v(-258.53, -64.21) * mm, "end": v(-258.78, -64.14) * mm});
            skArc(sketch, "E684", {"start": v(-258.35, -64.4) * mm, "mid": v(-257.56, -64.5) * mm, "end": v(-257.67, -63.71) * mm});
            skArc(sketch, "E685", {"start": v(-257.92, -63.28) * mm, "mid": v(-257.85, -63.53) * mm, "end": v(-257.67, -63.71) * mm});
            skLineSegment(sketch, "E686", {"start": v(-257.92, -63.28) * mm, "end": v(-257.92, -61.64) * mm});
            skArc(sketch, "E687", {"start": v(-257.42, -61.14) * mm, "mid": v(-257.77, -61.3) * mm, "end": v(-257.92, -61.64) * mm});
            skLineSegment(sketch, "E688", {"start": v(-257.42, -61.14) * mm, "end": v(-252.42, -61.14) * mm});
            skArc(sketch, "E689", {"start": v(-251.92, -61.64) * mm, "mid": v(-252.06, -61.3) * mm, "end": v(-252.42, -61.14) * mm});
            skLineSegment(sketch, "E690", {"start": v(-251.92, -61.64) * mm, "end": v(-251.92, -63.28) * mm});
            skArc(sketch, "E691", {"start": v(-252.17, -63.71) * mm, "mid": v(-251.98, -63.53) * mm, "end": v(-251.92, -63.28) * mm});
            skArc(sketch, "E692", {"start": v(-252.17, -63.71) * mm, "mid": v(-252.27, -64.5) * mm, "end": v(-251.48, -64.4) * mm});
            skArc(sketch, "E693", {"start": v(-251.05, -64.14) * mm, "mid": v(-251.3, -64.21) * mm, "end": v(-251.48, -64.4) * mm});
            skLineSegment(sketch, "E694", {"start": v(-251.05, -64.14) * mm, "end": v(-245.92, -64.14) * mm});
            skLineSegment(sketch, "E695", {"start": v(-245.92, -64.14) * mm, "end": v(-245.92, -67.14) * mm});
            skLineSegment(sketch, "E696", {"start": v(-245.92, -67.14) * mm, "end": v(-247.2, -67.14) * mm});
            skLineSegment(sketch, "E697", {"start": v(-247.2, -67.14) * mm, "end": v(-247.2, -71.14) * mm});
            skLineSegment(sketch, "E698", {"start": v(-247.2, -71.14) * mm, "end": v(-245.92, -71.14) * mm});
            skLineSegment(sketch, "E699", {"start": v(-245.92, -71.14) * mm, "end": v(-245.92, -74.14) * mm});
            skLineSegment(sketch, "E700", {"start": v(-245.92, -74.14) * mm, "end": v(-242.72, -74.14) * mm});
            skLineSegment(sketch, "E701", {"start": v(-242.72, -74.14) * mm, "end": v(-242.72, -71.14) * mm});
            skLineSegment(sketch, "E702", {"start": v(-242.72, -71.14) * mm, "end": v(-241.44, -71.14) * mm});
            skLineSegment(sketch, "E703", {"start": v(-241.44, -71.14) * mm, "end": v(-241.44, -67.14) * mm});
            skLineSegment(sketch, "E704", {"start": v(-241.44, -67.14) * mm, "end": v(-242.72, -67.14) * mm});
            skLineSegment(sketch, "E705", {"start": v(-242.72, -67.14) * mm, "end": v(-242.72, -64.14) * mm});
            skLineSegment(sketch, "E706", {"start": v(-242.72, -64.14) * mm, "end": v(-237.58, -64.14) * mm});
            skArc(sketch, "E707", {"start": v(-237.15, -64.4) * mm, "mid": v(-237.33, -64.21) * mm, "end": v(-237.58, -64.14) * mm});
            skArc(sketch, "E708", {"start": v(-237.15, -64.4) * mm, "mid": v(-236.36, -64.5) * mm, "end": v(-236.47, -63.71) * mm});
            skArc(sketch, "E709", {"start": v(-236.72, -63.28) * mm, "mid": v(-236.65, -63.53) * mm, "end": v(-236.47, -63.71) * mm});
            skLineSegment(sketch, "E710", {"start": v(-236.72, -63.28) * mm, "end": v(-236.72, -61.64) * mm});
            skArc(sketch, "E711", {"start": v(-236.22, -61.14) * mm, "mid": v(-236.57, -61.3) * mm, "end": v(-236.72, -61.64) * mm});
            skLineSegment(sketch, "E712", {"start": v(-236.22, -61.14) * mm, "end": v(-231.22, -61.14) * mm});
            skArc(sketch, "E713", {"start": v(-230.72, -61.64) * mm, "mid": v(-230.86, -61.3) * mm, "end": v(-231.22, -61.14) * mm});
            skLineSegment(sketch, "E714", {"start": v(-230.72, -61.64) * mm, "end": v(-230.72, -63.28) * mm});
            skArc(sketch, "E715", {"start": v(-230.97, -63.71) * mm, "mid": v(-230.78, -63.53) * mm, "end": v(-230.72, -63.28) * mm});
            skArc(sketch, "E716", {"start": v(-230.97, -63.71) * mm, "mid": v(-231.07, -64.5) * mm, "end": v(-230.28, -64.4) * mm});
            skArc(sketch, "E717", {"start": v(-229.85, -64.14) * mm, "mid": v(-230.1, -64.21) * mm, "end": v(-230.28, -64.4) * mm});
            skLineSegment(sketch, "E718", {"start": v(-229.85, -64.14) * mm, "end": v(-98.78, -64.14) * mm});
            skArc(sketch, "E719", {"start": v(-98.35, -64.4) * mm, "mid": v(-98.53, -64.21) * mm, "end": v(-98.78, -64.14) * mm});
            skArc(sketch, "E720", {"start": v(-98.35, -64.4) * mm, "mid": v(-97.56, -64.5) * mm, "end": v(-97.67, -63.71) * mm});
            skArc(sketch, "E721", {"start": v(-97.92, -63.28) * mm, "mid": v(-97.85, -63.53) * mm, "end": v(-97.67, -63.71) * mm});
            skLineSegment(sketch, "E722", {"start": v(-97.92, -63.28) * mm, "end": v(-97.92, -61.64) * mm});
            skArc(sketch, "E723", {"start": v(-97.42, -61.14) * mm, "mid": v(-97.77, -61.3) * mm, "end": v(-97.92, -61.64) * mm});
            skLineSegment(sketch, "E724", {"start": v(-97.42, -61.14) * mm, "end": v(-92.42, -61.14) * mm});
            skArc(sketch, "E725", {"start": v(-91.92, -61.64) * mm, "mid": v(-92.06, -61.3) * mm, "end": v(-92.42, -61.14) * mm});
            skLineSegment(sketch, "E726", {"start": v(-91.92, -61.64) * mm, "end": v(-91.92, -63.28) * mm});
            skArc(sketch, "E727", {"start": v(-92.17, -63.71) * mm, "mid": v(-91.98, -63.53) * mm, "end": v(-91.92, -63.28) * mm});
            skArc(sketch, "E728", {"start": v(-92.17, -63.71) * mm, "mid": v(-92.27, -64.5) * mm, "end": v(-91.48, -64.4) * mm});
            skArc(sketch, "E729", {"start": v(-91.05, -64.14) * mm, "mid": v(-91.3, -64.21) * mm, "end": v(-91.48, -64.4) * mm});
            skLineSegment(sketch, "E730", {"start": v(-91.05, -64.14) * mm, "end": v(-85.92, -64.14) * mm});
            skLineSegment(sketch, "E731", {"start": v(-85.92, -64.14) * mm, "end": v(-85.92, -67.14) * mm});
            skLineSegment(sketch, "E732", {"start": v(-85.92, -67.14) * mm, "end": v(-87.2, -67.14) * mm});
            skLineSegment(sketch, "E733", {"start": v(-87.2, -67.14) * mm, "end": v(-87.2, -71.14) * mm});
            skLineSegment(sketch, "E734", {"start": v(-87.2, -71.14) * mm, "end": v(-85.92, -71.14) * mm});
            skLineSegment(sketch, "E735", {"start": v(-85.92, -71.14) * mm, "end": v(-85.92, -74.14) * mm});
            skLineSegment(sketch, "E736", {"start": v(-85.92, -74.14) * mm, "end": v(-82.72, -74.14) * mm});
            skLineSegment(sketch, "E737", {"start": v(-82.72, -74.14) * mm, "end": v(-82.72, -71.14) * mm});
            skLineSegment(sketch, "E738", {"start": v(-82.72, -71.14) * mm, "end": v(-81.44, -71.14) * mm});
            skLineSegment(sketch, "E739", {"start": v(-81.44, -71.14) * mm, "end": v(-81.44, -67.14) * mm});
            skLineSegment(sketch, "E740", {"start": v(-81.44, -67.14) * mm, "end": v(-82.72, -67.14) * mm});
            skLineSegment(sketch, "E741", {"start": v(-82.72, -67.14) * mm, "end": v(-82.72, -64.14) * mm});
            skLineSegment(sketch, "E742", {"start": v(-82.72, -64.14) * mm, "end": v(-77.58, -64.14) * mm});
            skArc(sketch, "E743", {"start": v(-77.15, -64.4) * mm, "mid": v(-77.33, -64.21) * mm, "end": v(-77.58, -64.14) * mm});
            skArc(sketch, "E744", {"start": v(-77.15, -64.4) * mm, "mid": v(-76.36, -64.5) * mm, "end": v(-76.47, -63.71) * mm});
            skArc(sketch, "E745", {"start": v(-76.72, -63.28) * mm, "mid": v(-76.65, -63.53) * mm, "end": v(-76.47, -63.71) * mm});
            skLineSegment(sketch, "E746", {"start": v(-76.72, -63.28) * mm, "end": v(-76.72, -61.64) * mm});
            skArc(sketch, "E747", {"start": v(-76.22, -61.14) * mm, "mid": v(-76.57, -61.3) * mm, "end": v(-76.72, -61.64) * mm});
            skLineSegment(sketch, "E748", {"start": v(-76.22, -61.14) * mm, "end": v(-71.22, -61.14) * mm});
            skArc(sketch, "E749", {"start": v(-70.72, -61.64) * mm, "mid": v(-70.86, -61.3) * mm, "end": v(-71.22, -61.14) * mm});
            skLineSegment(sketch, "E750", {"start": v(-70.72, -61.64) * mm, "end": v(-70.72, -63.28) * mm});
            skArc(sketch, "E751", {"start": v(-70.97, -63.71) * mm, "mid": v(-70.78, -63.53) * mm, "end": v(-70.72, -63.28) * mm});
            skArc(sketch, "E752", {"start": v(-70.97, -63.71) * mm, "mid": v(-71.07, -64.5) * mm, "end": v(-70.28, -64.4) * mm});
            skArc(sketch, "E753", {"start": v(-69.85, -64.14) * mm, "mid": v(-70.1, -64.21) * mm, "end": v(-70.28, -64.4) * mm});
            skLineSegment(sketch, "E754", {"start": v(-69.85, -64.14) * mm, "end": v(-59.32, -64.14) * mm});
            skLineSegment(sketch, "E755", {"start": v(-59.32, -64.14) * mm, "end": v(-59.32, -74.8) * mm});
            skLineSegment(sketch, "E756", {"start": v(-59.32, -74.8) * mm, "end": v(-61.55, -74.8) * mm});
            skArc(sketch, "E757", {"start": v(-61.98, -74.54) * mm, "mid": v(-61.8, -74.73) * mm, "end": v(-61.55, -74.8) * mm});
            skArc(sketch, "E758", {"start": v(-61.98, -74.54) * mm, "mid": v(-62.77, -74.44) * mm, "end": v(-62.67, -75.23) * mm});
            skArc(sketch, "E759", {"start": v(-62.42, -75.66) * mm, "mid": v(-62.48, -75.41) * mm, "end": v(-62.67, -75.23) * mm});
            skLineSegment(sketch, "E760", {"start": v(-62.42, -75.66) * mm, "end": v(-62.42, -83.2) * mm});
            skLineSegment(sketch, "E761", {"start": v(-62.42, -83.2) * mm, "end": v(-65.42, -83.2) * mm});
            skLineSegment(sketch, "E762", {"start": v(-65.42, -83.2) * mm, "end": v(-65.42, -81.92) * mm});
            skLineSegment(sketch, "E763", {"start": v(-65.42, -81.92) * mm, "end": v(-69.42, -81.92) * mm});
            skLineSegment(sketch, "E764", {"start": v(-69.42, -81.92) * mm, "end": v(-69.42, -83.2) * mm});
            skLineSegment(sketch, "E765", {"start": v(-69.42, -83.2) * mm, "end": v(-72.42, -83.2) * mm});
            skLineSegment(sketch, "E766", {"start": v(-72.42, -83.2) * mm, "end": v(-72.42, -86.4) * mm});
            skLineSegment(sketch, "E767", {"start": v(-72.42, -86.4) * mm, "end": v(-69.42, -86.4) * mm});
            skLineSegment(sketch, "E768", {"start": v(-69.42, -86.4) * mm, "end": v(-69.42, -87.67) * mm});
            skLineSegment(sketch, "E769", {"start": v(-69.42, -87.67) * mm, "end": v(-65.42, -87.67) * mm});
            skLineSegment(sketch, "E770", {"start": v(-65.42, -87.67) * mm, "end": v(-65.42, -86.4) * mm});
            skLineSegment(sketch, "E771", {"start": v(-65.42, -86.4) * mm, "end": v(-62.42, -86.4) * mm});
            skLineSegment(sketch, "E772", {"start": v(-62.42, -86.4) * mm, "end": v(-62.42, -95.14) * mm});
            skLineSegment(sketch, "E773", {"start": v(-62.42, -95.14) * mm, "end": v(-384.87, -189.14) * mm});
            skLineSegment(sketch, "E774", {"start": v(-384.87, -189.14) * mm, "end": v(-389.85, -189.14) * mm});
            skArc(sketch, "E775", {"start": v(-244.48, -159.86) * mm, "mid": v(-244.73, -159.93) * mm, "end": v(-244.91, -160.1) * mm});
            skArc(sketch, "E776", {"start": v(-245.6, -159.43) * mm, "mid": v(-245.7, -160.21) * mm, "end": v(-244.91, -160.1) * mm});
            skArc(sketch, "E777", {"start": v(-245.6, -159.43) * mm, "mid": v(-245.41, -159.24) * mm, "end": v(-245.34, -159) * mm});
            skLineSegment(sketch, "E778", {"start": v(-245.34, -159) * mm, "end": v(-245.34, -157.36) * mm});
            skArc(sketch, "E779", {"start": v(-245.34, -157.36) * mm, "mid": v(-245.5, -157) * mm, "end": v(-245.84, -156.86) * mm});
            skLineSegment(sketch, "E780", {"start": v(-245.84, -156.86) * mm, "end": v(-250.84, -156.86) * mm});
            skArc(sketch, "E781", {"start": v(-250.84, -156.86) * mm, "mid": v(-251.2, -157) * mm, "end": v(-251.34, -157.36) * mm});
            skLineSegment(sketch, "E782", {"start": v(-251.34, -157.36) * mm, "end": v(-251.34, -159) * mm});
            skArc(sketch, "E783", {"start": v(-251.34, -159) * mm, "mid": v(-251.28, -159.24) * mm, "end": v(-251.1, -159.43) * mm});
            skArc(sketch, "E784", {"start": v(-251.78, -160.1) * mm, "mid": v(-251, -160.21) * mm, "end": v(-251.1, -159.43) * mm});
            skArc(sketch, "E785", {"start": v(-251.78, -160.1) * mm, "mid": v(-251.96, -159.93) * mm, "end": v(-252.21, -159.86) * mm});
            skLineSegment(sketch, "E786", {"start": v(-252.21, -159.86) * mm, "end": v(-256.74, -159.86) * mm});
            skLineSegment(sketch, "E787", {"start": v(-256.74, -159.86) * mm, "end": v(-256.74, -173.27) * mm});
            skArc(sketch, "E788", {"start": v(-256.74, -173.27) * mm, "mid": v(-256.31, -174.51) * mm, "end": v(-255.2, -175.22) * mm});
            skLineSegment(sketch, "E789", {"start": v(-255.2, -175.22) * mm, "end": v(-227.32, -181.68) * mm});
            skArc(sketch, "E790", {"start": v(-227.32, -181.68) * mm, "mid": v(-221.39, -180.34) * mm, "end": v(-218.74, -174.86) * mm});
            skLineSegment(sketch, "E791", {"start": v(-218.74, -174.86) * mm, "end": v(-218.74, -159.86) * mm});
            skLineSegment(sketch, "E792", {"start": v(-218.74, -159.86) * mm, "end": v(-223.28, -159.86) * mm});
            skArc(sketch, "E793", {"start": v(-223.28, -159.86) * mm, "mid": v(-223.53, -159.93) * mm, "end": v(-223.71, -160.1) * mm});
            skArc(sketch, "E794", {"start": v(-224.4, -159.43) * mm, "mid": v(-224.5, -160.21) * mm, "end": v(-223.71, -160.1) * mm});
            skArc(sketch, "E795", {"start": v(-224.4, -159.43) * mm, "mid": v(-224.21, -159.24) * mm, "end": v(-224.14, -159) * mm});
            skLineSegment(sketch, "E796", {"start": v(-224.14, -159) * mm, "end": v(-224.14, -157.36) * mm});
            skArc(sketch, "E797", {"start": v(-224.14, -157.36) * mm, "mid": v(-224.3, -157) * mm, "end": v(-224.64, -156.86) * mm});
            skLineSegment(sketch, "E798", {"start": v(-224.64, -156.86) * mm, "end": v(-229.64, -156.86) * mm});
            skArc(sketch, "E799", {"start": v(-229.64, -156.86) * mm, "mid": v(-230, -157) * mm, "end": v(-230.14, -157.36) * mm});
            skLineSegment(sketch, "E800", {"start": v(-230.14, -157.36) * mm, "end": v(-230.14, -159) * mm});
            skArc(sketch, "E801", {"start": v(-230.14, -159) * mm, "mid": v(-230.08, -159.24) * mm, "end": v(-229.9, -159.43) * mm});
            skArc(sketch, "E802", {"start": v(-230.58, -160.1) * mm, "mid": v(-229.8, -160.21) * mm, "end": v(-229.9, -159.43) * mm});
            skArc(sketch, "E803", {"start": v(-230.58, -160.1) * mm, "mid": v(-230.76, -159.93) * mm, "end": v(-231.01, -159.86) * mm});
            skLineSegment(sketch, "E804", {"start": v(-231.01, -159.86) * mm, "end": v(-236.14, -159.86) * mm});
            skLineSegment(sketch, "E805", {"start": v(-236.14, -159.86) * mm, "end": v(-236.14, -162.86) * mm});
            skLineSegment(sketch, "E806", {"start": v(-236.14, -162.86) * mm, "end": v(-234.87, -162.86) * mm});
            skLineSegment(sketch, "E807", {"start": v(-234.87, -162.86) * mm, "end": v(-234.87, -166.86) * mm});
            skLineSegment(sketch, "E808", {"start": v(-234.87, -166.86) * mm, "end": v(-236.14, -166.86) * mm});
            skLineSegment(sketch, "E809", {"start": v(-236.14, -166.86) * mm, "end": v(-236.14, -169.86) * mm});
            skLineSegment(sketch, "E810", {"start": v(-236.14, -169.86) * mm, "end": v(-239.34, -169.86) * mm});
            skLineSegment(sketch, "E811", {"start": v(-239.34, -169.86) * mm, "end": v(-239.34, -166.86) * mm});
            skLineSegment(sketch, "E812", {"start": v(-239.34, -166.86) * mm, "end": v(-240.62, -166.86) * mm});
            skLineSegment(sketch, "E813", {"start": v(-240.62, -166.86) * mm, "end": v(-240.62, -162.86) * mm});
            skLineSegment(sketch, "E814", {"start": v(-240.62, -162.86) * mm, "end": v(-239.34, -162.86) * mm});
            skLineSegment(sketch, "E815", {"start": v(-239.34, -162.86) * mm, "end": v(-239.34, -159.86) * mm});
            skLineSegment(sketch, "E816", {"start": v(-239.34, -159.86) * mm, "end": v(-244.48, -159.86) * mm});
            skCircle(sketch, "E817", {"center": v(-225.74, -174.86) * mm, "radius": 4 * mm});
            skArc(sketch, "E818", {"start": v(-214.7, 179.98) * mm, "mid": v(-214.95, 179.92) * mm, "end": v(-215.13, 179.73) * mm});
            skArc(sketch, "E819", {"start": v(-215.81, 180.42) * mm, "mid": v(-215.92, 179.63) * mm, "end": v(-215.13, 179.73) * mm});
            skArc(sketch, "E820", {"start": v(-215.81, 180.42) * mm, "mid": v(-215.63, 180.6) * mm, "end": v(-215.56, 180.85) * mm});
            skLineSegment(sketch, "E821", {"start": v(-215.56, 180.85) * mm, "end": v(-215.56, 182.48) * mm});
            skArc(sketch, "E822", {"start": v(-215.56, 182.48) * mm, "mid": v(-215.7, 182.84) * mm, "end": v(-216.06, 182.98) * mm});
            skLineSegment(sketch, "E823", {"start": v(-216.06, 182.98) * mm, "end": v(-221.06, 182.98) * mm});
            skArc(sketch, "E824", {"start": v(-221.06, 182.98) * mm, "mid": v(-221.42, 182.84) * mm, "end": v(-221.56, 182.48) * mm});
            skLineSegment(sketch, "E825", {"start": v(-221.56, 182.48) * mm, "end": v(-221.56, 180.85) * mm});
            skArc(sketch, "E826", {"start": v(-221.56, 180.85) * mm, "mid": v(-221.5, 180.6) * mm, "end": v(-221.31, 180.42) * mm});
            skArc(sketch, "E827", {"start": v(-222, 179.73) * mm, "mid": v(-221.2, 179.63) * mm, "end": v(-221.31, 180.42) * mm});
            skArc(sketch, "E828", {"start": v(-222, 179.73) * mm, "mid": v(-222.18, 179.92) * mm, "end": v(-222.43, 179.98) * mm});
            skLineSegment(sketch, "E829", {"start": v(-222.43, 179.98) * mm, "end": v(-226.96, 179.98) * mm});
            skLineSegment(sketch, "E830", {"start": v(-226.96, 179.98) * mm, "end": v(-226.96, 166.57) * mm});
            skArc(sketch, "E831", {"start": v(-226.96, 166.57) * mm, "mid": v(-226.53, 165.33) * mm, "end": v(-225.41, 164.62) * mm});
            skLineSegment(sketch, "E832", {"start": v(-225.41, 164.62) * mm, "end": v(-197.54, 158.17) * mm});
            skArc(sketch, "E833", {"start": v(-197.54, 158.17) * mm, "mid": v(-191.6, 159.5) * mm, "end": v(-188.96, 164.98) * mm});
            skLineSegment(sketch, "E834", {"start": v(-188.96, 164.98) * mm, "end": v(-188.96, 179.98) * mm});
            skLineSegment(sketch, "E835", {"start": v(-188.96, 179.98) * mm, "end": v(-193.5, 179.98) * mm});
            skArc(sketch, "E836", {"start": v(-193.5, 179.98) * mm, "mid": v(-193.75, 179.92) * mm, "end": v(-193.93, 179.73) * mm});
            skArc(sketch, "E837", {"start": v(-194.61, 180.42) * mm, "mid": v(-194.72, 179.63) * mm, "end": v(-193.93, 179.73) * mm});
            skArc(sketch, "E838", {"start": v(-194.61, 180.42) * mm, "mid": v(-194.43, 180.6) * mm, "end": v(-194.36, 180.85) * mm});
            skLineSegment(sketch, "E839", {"start": v(-194.36, 180.85) * mm, "end": v(-194.36, 182.48) * mm});
            skArc(sketch, "E840", {"start": v(-194.36, 182.48) * mm, "mid": v(-194.5, 182.84) * mm, "end": v(-194.86, 182.98) * mm});
            skLineSegment(sketch, "E841", {"start": v(-194.86, 182.98) * mm, "end": v(-199.86, 182.98) * mm});
            skArc(sketch, "E842", {"start": v(-199.86, 182.98) * mm, "mid": v(-200.22, 182.84) * mm, "end": v(-200.36, 182.48) * mm});
            skLineSegment(sketch, "E843", {"start": v(-200.36, 182.48) * mm, "end": v(-200.36, 180.85) * mm});
            skArc(sketch, "E844", {"start": v(-200.36, 180.85) * mm, "mid": v(-200.3, 180.6) * mm, "end": v(-200.11, 180.42) * mm});
            skArc(sketch, "E845", {"start": v(-200.8, 179.73) * mm, "mid": v(-200, 179.63) * mm, "end": v(-200.11, 180.42) * mm});
            skArc(sketch, "E846", {"start": v(-200.8, 179.73) * mm, "mid": v(-200.98, 179.92) * mm, "end": v(-201.23, 179.98) * mm});
            skLineSegment(sketch, "E847", {"start": v(-201.23, 179.98) * mm, "end": v(-206.36, 179.98) * mm});
            skLineSegment(sketch, "E848", {"start": v(-206.36, 179.98) * mm, "end": v(-206.36, 176.98) * mm});
            skLineSegment(sketch, "E849", {"start": v(-206.36, 176.98) * mm, "end": v(-205.09, 176.98) * mm});
            skLineSegment(sketch, "E850", {"start": v(-205.09, 176.98) * mm, "end": v(-205.09, 172.98) * mm});
            skLineSegment(sketch, "E851", {"start": v(-205.09, 172.98) * mm, "end": v(-206.36, 172.98) * mm});
            skLineSegment(sketch, "E852", {"start": v(-206.36, 172.98) * mm, "end": v(-206.36, 169.98) * mm});
            skLineSegment(sketch, "E853", {"start": v(-206.36, 169.98) * mm, "end": v(-209.56, 169.98) * mm});
            skLineSegment(sketch, "E854", {"start": v(-209.56, 169.98) * mm, "end": v(-209.56, 172.98) * mm});
            skLineSegment(sketch, "E855", {"start": v(-209.56, 172.98) * mm, "end": v(-210.84, 172.98) * mm});
            skLineSegment(sketch, "E856", {"start": v(-210.84, 172.98) * mm, "end": v(-210.84, 176.98) * mm});
            skLineSegment(sketch, "E857", {"start": v(-210.84, 176.98) * mm, "end": v(-209.56, 176.98) * mm});
            skLineSegment(sketch, "E858", {"start": v(-209.56, 176.98) * mm, "end": v(-209.56, 179.98) * mm});
            skLineSegment(sketch, "E859", {"start": v(-209.56, 179.98) * mm, "end": v(-214.7, 179.98) * mm});
            skCircle(sketch, "E860", {"center": v(-195.96, 164.98) * mm, "radius": 4 * mm});
            skLineSegment(sketch, "E861", {"start": v(94.25, -141.12) * mm, "end": v(107.96, -164.86) * mm});
            skArc(sketch, "E862", {"start": v(105.36, -169.36) * mm, "mid": v(107.96, -167.86) * mm, "end": v(107.96, -164.86) * mm});
            skLineSegment(sketch, "E863", {"start": v(88.66, -166.36) * mm, "end": v(88.66, -142.62) * mm});
            skArc(sketch, "E864", {"start": v(94.25, -141.12) * mm, "mid": v(90.88, -139.73) * mm, "end": v(88.66, -142.62) * mm});
            skLineSegment(sketch, "E865", {"start": v(91.66, -169.36) * mm, "end": v(105.36, -169.36) * mm});
            skArc(sketch, "E866", {"start": v(88.66, -166.36) * mm, "mid": v(89.53, -168.48) * mm, "end": v(91.66, -169.36) * mm});
            skLineSegment(sketch, "E867", {"start": v(94.25, 141.12) * mm, "end": v(107.96, 164.86) * mm});
            skArc(sketch, "E868", {"start": v(107.96, 164.86) * mm, "mid": v(107.96, 167.86) * mm, "end": v(105.36, 169.36) * mm});
            skLineSegment(sketch, "E869", {"start": v(88.66, 166.36) * mm, "end": v(88.66, 142.62) * mm});
            skArc(sketch, "E870", {"start": v(88.66, 142.62) * mm, "mid": v(90.88, 139.73) * mm, "end": v(94.25, 141.12) * mm});
            skLineSegment(sketch, "E871", {"start": v(91.66, 169.36) * mm, "end": v(105.36, 169.36) * mm});
            skArc(sketch, "E872", {"start": v(91.66, 169.36) * mm, "mid": v(89.53, 168.48) * mm, "end": v(88.66, 166.36) * mm});
            skArc(sketch, "E873", {"start": v(403.53, -72.23) * mm, "mid": v(403.28, -72.3) * mm, "end": v(403.1, -72.48) * mm});
            skArc(sketch, "E874", {"start": v(402.42, -71.8) * mm, "mid": v(402.31, -72.58) * mm, "end": v(403.1, -72.48) * mm});
            skArc(sketch, "E875", {"start": v(402.42, -71.8) * mm, "mid": v(402.6, -71.6) * mm, "end": v(402.67, -71.36) * mm});
            skLineSegment(sketch, "E876", {"start": v(402.67, -71.36) * mm, "end": v(402.67, -66.9) * mm});
            skArc(sketch, "E877", {"start": v(402.67, -66.9) * mm, "mid": v(402.6, -66.64) * mm, "end": v(402.42, -66.46) * mm});
            skArc(sketch, "E878", {"start": v(403.1, -65.78) * mm, "mid": v(402.31, -65.67) * mm, "end": v(402.42, -66.46) * mm});
            skArc(sketch, "E879", {"start": v(403.1, -65.78) * mm, "mid": v(403.28, -65.96) * mm, "end": v(403.53, -66.03) * mm});
            skLineSegment(sketch, "E880", {"start": v(403.53, -66.03) * mm, "end": v(405.1, -66.03) * mm});
            skArc(sketch, "E881", {"start": v(405.1, -66.03) * mm, "mid": v(405.35, -65.96) * mm, "end": v(405.53, -65.78) * mm});
            skArc(sketch, "E882", {"start": v(406.22, -66.46) * mm, "mid": v(406.32, -65.67) * mm, "end": v(405.53, -65.78) * mm});
            skArc(sketch, "E883", {"start": v(406.22, -66.46) * mm, "mid": v(406.03, -66.64) * mm, "end": v(405.97, -66.9) * mm});
            skLineSegment(sketch, "E884", {"start": v(405.97, -66.9) * mm, "end": v(405.97, -71.36) * mm});
            skArc(sketch, "E885", {"start": v(405.97, -71.36) * mm, "mid": v(406.03, -71.6) * mm, "end": v(406.22, -71.8) * mm});
            skArc(sketch, "E886", {"start": v(405.53, -72.48) * mm, "mid": v(406.32, -72.58) * mm, "end": v(406.22, -71.8) * mm});
            skArc(sketch, "E887", {"start": v(405.53, -72.48) * mm, "mid": v(405.35, -72.3) * mm, "end": v(405.1, -72.23) * mm});
            skLineSegment(sketch, "E888", {"start": v(405.1, -72.23) * mm, "end": v(403.53, -72.23) * mm});
            skArc(sketch, "E889", {"start": v(403.53, -51.03) * mm, "mid": v(403.28, -51.1) * mm, "end": v(403.1, -51.28) * mm});
            skArc(sketch, "E890", {"start": v(402.42, -50.6) * mm, "mid": v(402.31, -51.38) * mm, "end": v(403.1, -51.28) * mm});
            skArc(sketch, "E891", {"start": v(402.42, -50.6) * mm, "mid": v(402.6, -50.4) * mm, "end": v(402.67, -50.16) * mm});
            skLineSegment(sketch, "E892", {"start": v(402.67, -50.16) * mm, "end": v(402.67, -45.7) * mm});
            skArc(sketch, "E893", {"start": v(402.67, -45.7) * mm, "mid": v(402.6, -45.44) * mm, "end": v(402.42, -45.26) * mm});
            skArc(sketch, "E894", {"start": v(403.1, -44.58) * mm, "mid": v(402.31, -44.47) * mm, "end": v(402.42, -45.26) * mm});
            skArc(sketch, "E895", {"start": v(403.1, -44.58) * mm, "mid": v(403.28, -44.76) * mm, "end": v(403.53, -44.83) * mm});
            skLineSegment(sketch, "E896", {"start": v(403.53, -44.83) * mm, "end": v(405.1, -44.83) * mm});
            skArc(sketch, "E897", {"start": v(405.1, -44.83) * mm, "mid": v(405.35, -44.76) * mm, "end": v(405.53, -44.58) * mm});
            skArc(sketch, "E898", {"start": v(406.22, -45.26) * mm, "mid": v(406.32, -44.47) * mm, "end": v(405.53, -44.58) * mm});
            skArc(sketch, "E899", {"start": v(406.22, -45.26) * mm, "mid": v(406.03, -45.44) * mm, "end": v(405.97, -45.7) * mm});
            skLineSegment(sketch, "E900", {"start": v(405.97, -45.7) * mm, "end": v(405.97, -50.16) * mm});
            skArc(sketch, "E901", {"start": v(405.97, -50.16) * mm, "mid": v(406.03, -50.4) * mm, "end": v(406.22, -50.6) * mm});
            skArc(sketch, "E902", {"start": v(405.53, -51.28) * mm, "mid": v(406.32, -51.38) * mm, "end": v(406.22, -50.6) * mm});
            skArc(sketch, "E903", {"start": v(405.53, -51.28) * mm, "mid": v(405.35, -51.1) * mm, "end": v(405.1, -51.03) * mm});
            skLineSegment(sketch, "E904", {"start": v(405.1, -51.03) * mm, "end": v(403.53, -51.03) * mm});
            skCircle(sketch, "E905", {"center": v(404.32, -58.53) * mm, "radius": 1.6 * mm});
            skArc(sketch, "E906", {"start": v(-405.1, 6.36) * mm, "mid": v(-405.35, 6.29) * mm, "end": v(-405.53, 6.1) * mm});
            skArc(sketch, "E907", {"start": v(-406.22, 6.79) * mm, "mid": v(-406.32, 6) * mm, "end": v(-405.53, 6.1) * mm});
            skArc(sketch, "E908", {"start": v(-406.22, 6.79) * mm, "mid": v(-406.03, 6.97) * mm, "end": v(-405.97, 7.22) * mm});
            skLineSegment(sketch, "E909", {"start": v(-405.97, 7.22) * mm, "end": v(-405.97, 11.69) * mm});
            skArc(sketch, "E910", {"start": v(-405.97, 11.69) * mm, "mid": v(-406.03, 11.94) * mm, "end": v(-406.22, 12.12) * mm});
            skArc(sketch, "E911", {"start": v(-405.53, 12.8) * mm, "mid": v(-406.32, 12.9) * mm, "end": v(-406.22, 12.12) * mm});
            skArc(sketch, "E912", {"start": v(-405.53, 12.8) * mm, "mid": v(-405.35, 12.62) * mm, "end": v(-405.1, 12.56) * mm});
            skLineSegment(sketch, "E913", {"start": v(-405.1, 12.56) * mm, "end": v(-403.53, 12.56) * mm});
            skArc(sketch, "E914", {"start": v(-403.53, 12.56) * mm, "mid": v(-403.28, 12.62) * mm, "end": v(-403.1, 12.8) * mm});
            skArc(sketch, "E915", {"start": v(-402.42, 12.12) * mm, "mid": v(-402.31, 12.9) * mm, "end": v(-403.1, 12.8) * mm});
            skArc(sketch, "E916", {"start": v(-402.42, 12.12) * mm, "mid": v(-402.6, 11.94) * mm, "end": v(-402.67, 11.69) * mm});
            skLineSegment(sketch, "E917", {"start": v(-402.67, 11.69) * mm, "end": v(-402.67, 7.22) * mm});
            skArc(sketch, "E918", {"start": v(-402.67, 7.22) * mm, "mid": v(-402.6, 6.97) * mm, "end": v(-402.42, 6.79) * mm});
            skArc(sketch, "E919", {"start": v(-403.1, 6.1) * mm, "mid": v(-402.31, 6) * mm, "end": v(-402.42, 6.79) * mm});
            skArc(sketch, "E920", {"start": v(-403.1, 6.1) * mm, "mid": v(-403.28, 6.29) * mm, "end": v(-403.53, 6.36) * mm});
            skLineSegment(sketch, "E921", {"start": v(-403.53, 6.36) * mm, "end": v(-405.1, 6.36) * mm});
            skArc(sketch, "E922", {"start": v(-405.1, -14.84) * mm, "mid": v(-405.35, -14.91) * mm, "end": v(-405.53, -15.1) * mm});
            skArc(sketch, "E923", {"start": v(-406.22, -14.41) * mm, "mid": v(-406.32, -15.2) * mm, "end": v(-405.53, -15.1) * mm});
            skArc(sketch, "E924", {"start": v(-406.22, -14.41) * mm, "mid": v(-406.03, -14.23) * mm, "end": v(-405.97, -13.98) * mm});
            skLineSegment(sketch, "E925", {"start": v(-405.97, -13.98) * mm, "end": v(-405.97, -9.51) * mm});
            skArc(sketch, "E926", {"start": v(-405.97, -9.51) * mm, "mid": v(-406.03, -9.26) * mm, "end": v(-406.22, -9.08) * mm});
            skArc(sketch, "E927", {"start": v(-405.53, -8.4) * mm, "mid": v(-406.32, -8.3) * mm, "end": v(-406.22, -9.08) * mm});
            skArc(sketch, "E928", {"start": v(-405.53, -8.4) * mm, "mid": v(-405.35, -8.58) * mm, "end": v(-405.1, -8.64) * mm});
            skLineSegment(sketch, "E929", {"start": v(-405.1, -8.64) * mm, "end": v(-403.53, -8.64) * mm});
            skArc(sketch, "E930", {"start": v(-403.53, -8.64) * mm, "mid": v(-403.28, -8.58) * mm, "end": v(-403.1, -8.4) * mm});
            skArc(sketch, "E931", {"start": v(-402.42, -9.08) * mm, "mid": v(-402.31, -8.3) * mm, "end": v(-403.1, -8.4) * mm});
            skArc(sketch, "E932", {"start": v(-402.42, -9.08) * mm, "mid": v(-402.6, -9.26) * mm, "end": v(-402.67, -9.51) * mm});
            skLineSegment(sketch, "E933", {"start": v(-402.67, -9.51) * mm, "end": v(-402.67, -13.98) * mm});
            skArc(sketch, "E934", {"start": v(-402.67, -13.98) * mm, "mid": v(-402.6, -14.23) * mm, "end": v(-402.42, -14.41) * mm});
            skArc(sketch, "E935", {"start": v(-403.1, -15.1) * mm, "mid": v(-402.31, -15.2) * mm, "end": v(-402.42, -14.41) * mm});
            skArc(sketch, "E936", {"start": v(-403.1, -15.1) * mm, "mid": v(-403.28, -14.91) * mm, "end": v(-403.53, -14.84) * mm});
            skLineSegment(sketch, "E937", {"start": v(-403.53, -14.84) * mm, "end": v(-405.1, -14.84) * mm});
            skCircle(sketch, "E938", {"center": v(-404.32, -1.14) * mm, "radius": 1.6 * mm});
            skArc(sketch, "E939", {"start": v(403.53, 44.83) * mm, "mid": v(403.28, 44.76) * mm, "end": v(403.1, 44.58) * mm});
            skArc(sketch, "E940", {"start": v(402.42, 45.26) * mm, "mid": v(402.31, 44.47) * mm, "end": v(403.1, 44.58) * mm});
            skArc(sketch, "E941", {"start": v(402.42, 45.26) * mm, "mid": v(402.6, 45.44) * mm, "end": v(402.67, 45.7) * mm});
            skLineSegment(sketch, "E942", {"start": v(402.67, 45.7) * mm, "end": v(402.67, 50.16) * mm});
            skArc(sketch, "E943", {"start": v(402.67, 50.16) * mm, "mid": v(402.6, 50.4) * mm, "end": v(402.42, 50.6) * mm});
            skArc(sketch, "E944", {"start": v(403.1, 51.28) * mm, "mid": v(402.31, 51.38) * mm, "end": v(402.42, 50.6) * mm});
            skArc(sketch, "E945", {"start": v(403.1, 51.28) * mm, "mid": v(403.28, 51.1) * mm, "end": v(403.53, 51.03) * mm});
            skLineSegment(sketch, "E946", {"start": v(403.53, 51.03) * mm, "end": v(405.1, 51.03) * mm});
            skArc(sketch, "E947", {"start": v(405.1, 51.03) * mm, "mid": v(405.35, 51.1) * mm, "end": v(405.53, 51.28) * mm});
            skArc(sketch, "E948", {"start": v(406.22, 50.6) * mm, "mid": v(406.32, 51.38) * mm, "end": v(405.53, 51.28) * mm});
            skArc(sketch, "E949", {"start": v(406.22, 50.6) * mm, "mid": v(406.03, 50.4) * mm, "end": v(405.97, 50.16) * mm});
            skLineSegment(sketch, "E950", {"start": v(405.97, 50.16) * mm, "end": v(405.97, 45.7) * mm});
            skArc(sketch, "E951", {"start": v(405.97, 45.7) * mm, "mid": v(406.03, 45.44) * mm, "end": v(406.22, 45.26) * mm});
            skArc(sketch, "E952", {"start": v(405.53, 44.58) * mm, "mid": v(406.32, 44.47) * mm, "end": v(406.22, 45.26) * mm});
            skArc(sketch, "E953", {"start": v(405.53, 44.58) * mm, "mid": v(405.35, 44.76) * mm, "end": v(405.1, 44.83) * mm});
            skLineSegment(sketch, "E954", {"start": v(405.1, 44.83) * mm, "end": v(403.53, 44.83) * mm});
            skArc(sketch, "E955", {"start": v(403.53, 66.03) * mm, "mid": v(403.28, 65.96) * mm, "end": v(403.1, 65.78) * mm});
            skArc(sketch, "E956", {"start": v(402.42, 66.46) * mm, "mid": v(402.31, 65.67) * mm, "end": v(403.1, 65.78) * mm});
            skArc(sketch, "E957", {"start": v(402.42, 66.46) * mm, "mid": v(402.6, 66.64) * mm, "end": v(402.67, 66.9) * mm});
            skLineSegment(sketch, "E958", {"start": v(402.67, 66.9) * mm, "end": v(402.67, 71.36) * mm});
            skArc(sketch, "E959", {"start": v(402.67, 71.36) * mm, "mid": v(402.6, 71.6) * mm, "end": v(402.42, 71.8) * mm});
            skArc(sketch, "E960", {"start": v(403.1, 72.48) * mm, "mid": v(402.31, 72.58) * mm, "end": v(402.42, 71.8) * mm});
            skArc(sketch, "E961", {"start": v(403.1, 72.48) * mm, "mid": v(403.28, 72.3) * mm, "end": v(403.53, 72.23) * mm});
            skLineSegment(sketch, "E962", {"start": v(403.53, 72.23) * mm, "end": v(405.1, 72.23) * mm});
            skArc(sketch, "E963", {"start": v(405.1, 72.23) * mm, "mid": v(405.35, 72.3) * mm, "end": v(405.53, 72.48) * mm});
            skArc(sketch, "E964", {"start": v(406.22, 71.8) * mm, "mid": v(406.32, 72.58) * mm, "end": v(405.53, 72.48) * mm});
            skArc(sketch, "E965", {"start": v(406.22, 71.8) * mm, "mid": v(406.03, 71.6) * mm, "end": v(405.97, 71.36) * mm});
            skLineSegment(sketch, "E966", {"start": v(405.97, 71.36) * mm, "end": v(405.97, 66.9) * mm});
            skArc(sketch, "E967", {"start": v(405.97, 66.9) * mm, "mid": v(406.03, 66.64) * mm, "end": v(406.22, 66.46) * mm});
            skArc(sketch, "E968", {"start": v(405.53, 65.78) * mm, "mid": v(406.32, 65.67) * mm, "end": v(406.22, 66.46) * mm});
            skArc(sketch, "E969", {"start": v(405.53, 65.78) * mm, "mid": v(405.35, 65.96) * mm, "end": v(405.1, 66.03) * mm});
            skLineSegment(sketch, "E970", {"start": v(405.1, 66.03) * mm, "end": v(403.53, 66.03) * mm});
            skCircle(sketch, "E971", {"center": v(404.32, 58.53) * mm, "radius": 1.6 * mm});
            skArc(sketch, "E972", {"start": v(-51.9, 188.7) * mm, "mid": v(-52.08, 188.88) * mm, "end": v(-52.33, 188.95) * mm});
            skArc(sketch, "E973", {"start": v(-51.9, 188.7) * mm, "mid": v(-51.1, 188.6) * mm, "end": v(-51.21, 189.38) * mm});
            skArc(sketch, "E974", {"start": v(-51.46, 189.81) * mm, "mid": v(-51.4, 189.56) * mm, "end": v(-51.21, 189.38) * mm});
            skLineSegment(sketch, "E975", {"start": v(-51.46, 189.81) * mm, "end": v(-51.46, 191.45) * mm});
            skArc(sketch, "E976", {"start": v(-50.96, 191.95) * mm, "mid": v(-51.31, 191.8) * mm, "end": v(-51.46, 191.45) * mm});
            skLineSegment(sketch, "E977", {"start": v(-50.96, 191.95) * mm, "end": v(-45.96, 191.95) * mm});
            skArc(sketch, "E978", {"start": v(-45.46, 191.45) * mm, "mid": v(-45.6, 191.8) * mm, "end": v(-45.96, 191.95) * mm});
            skLineSegment(sketch, "E979", {"start": v(-45.46, 191.45) * mm, "end": v(-45.46, 189.81) * mm});
            skArc(sketch, "E980", {"start": v(-45.71, 189.38) * mm, "mid": v(-45.53, 189.56) * mm, "end": v(-45.46, 189.81) * mm});
            skArc(sketch, "E981", {"start": v(-45.71, 189.38) * mm, "mid": v(-45.81, 188.6) * mm, "end": v(-45.03, 188.7) * mm});
            skArc(sketch, "E982", {"start": v(-44.6, 188.95) * mm, "mid": v(-44.85, 188.88) * mm, "end": v(-45.03, 188.7) * mm});
            skLineSegment(sketch, "E983", {"start": v(-44.6, 188.95) * mm, "end": v(-39.46, 188.95) * mm});
            skLineSegment(sketch, "E984", {"start": v(-39.46, 188.95) * mm, "end": v(-39.46, 185.95) * mm});
            skLineSegment(sketch, "E985", {"start": v(-39.46, 185.95) * mm, "end": v(-40.74, 185.95) * mm});
            skLineSegment(sketch, "E986", {"start": v(-40.74, 185.95) * mm, "end": v(-40.74, 181.95) * mm});
            skLineSegment(sketch, "E987", {"start": v(-40.74, 181.95) * mm, "end": v(-39.46, 181.95) * mm});
            skLineSegment(sketch, "E988", {"start": v(-39.46, 181.95) * mm, "end": v(-39.46, 178.95) * mm});
            skLineSegment(sketch, "E989", {"start": v(-39.46, 178.95) * mm, "end": v(-36.26, 178.95) * mm});
            skLineSegment(sketch, "E990", {"start": v(-36.26, 178.95) * mm, "end": v(-36.26, 181.95) * mm});
            skLineSegment(sketch, "E991", {"start": v(-36.26, 181.95) * mm, "end": v(-34.99, 181.95) * mm});
            skLineSegment(sketch, "E992", {"start": v(-34.99, 181.95) * mm, "end": v(-34.99, 185.95) * mm});
            skLineSegment(sketch, "E993", {"start": v(-34.99, 185.95) * mm, "end": v(-36.26, 185.95) * mm});
            skLineSegment(sketch, "E994", {"start": v(-36.26, 185.95) * mm, "end": v(-36.26, 188.95) * mm});
            skLineSegment(sketch, "E995", {"start": v(-36.26, 188.95) * mm, "end": v(-31.13, 188.95) * mm});
            skArc(sketch, "E996", {"start": v(-30.7, 188.7) * mm, "mid": v(-30.88, 188.88) * mm, "end": v(-31.13, 188.95) * mm});
            skArc(sketch, "E997", {"start": v(-30.7, 188.7) * mm, "mid": v(-29.9, 188.6) * mm, "end": v(-30.01, 189.38) * mm});
            skArc(sketch, "E998", {"start": v(-30.26, 189.81) * mm, "mid": v(-30.2, 189.56) * mm, "end": v(-30.01, 189.38) * mm});
            skLineSegment(sketch, "E999", {"start": v(-30.26, 189.81) * mm, "end": v(-30.26, 191.45) * mm});
            skArc(sketch, "E1000", {"start": v(-29.76, 191.95) * mm, "mid": v(-30.11, 191.8) * mm, "end": v(-30.26, 191.45) * mm});
            skLineSegment(sketch, "E1001", {"start": v(-29.76, 191.95) * mm, "end": v(-24.76, 191.95) * mm});
            skArc(sketch, "E1002", {"start": v(-24.26, 191.45) * mm, "mid": v(-24.4, 191.8) * mm, "end": v(-24.76, 191.95) * mm});
            skLineSegment(sketch, "E1003", {"start": v(-24.26, 191.45) * mm, "end": v(-24.26, 189.81) * mm});
            skArc(sketch, "E1004", {"start": v(-24.51, 189.38) * mm, "mid": v(-24.33, 189.56) * mm, "end": v(-24.26, 189.81) * mm});
            skArc(sketch, "E1005", {"start": v(-24.51, 189.38) * mm, "mid": v(-24.61, 188.6) * mm, "end": v(-23.83, 188.7) * mm});
            skArc(sketch, "E1006", {"start": v(-23.4, 188.95) * mm, "mid": v(-23.65, 188.88) * mm, "end": v(-23.83, 188.7) * mm});
            skLineSegment(sketch, "E1007", {"start": v(-23.4, 188.95) * mm, "end": v(-12.86, 188.95) * mm});
            skLineSegment(sketch, "E1008", {"start": v(-12.86, 188.95) * mm, "end": v(-12.86, 167.95) * mm});
            skLineSegment(sketch, "E1009", {"start": v(-12.86, 167.95) * mm, "end": v(-14.86, 165.95) * mm});
            skLineSegment(sketch, "E1010", {"start": v(-14.86, 165.95) * mm, "end": v(-14.86, 63.95) * mm});
            skLineSegment(sketch, "E1011", {"start": v(-14.86, 63.95) * mm, "end": v(-23.4, 63.95) * mm});
            skArc(sketch, "E1012", {"start": v(-23.83, 64.2) * mm, "mid": v(-23.65, 64.02) * mm, "end": v(-23.4, 63.95) * mm});
            skArc(sketch, "E1013", {"start": v(-23.83, 64.2) * mm, "mid": v(-24.61, 64.3) * mm, "end": v(-24.51, 63.52) * mm});
            skArc(sketch, "E1014", {"start": v(-24.26, 63.08) * mm, "mid": v(-24.33, 63.33) * mm, "end": v(-24.51, 63.52) * mm});
            skArc(sketch, "E1015", {"start": v(-51.21, 63.52) * mm, "mid": v(-51.4, 63.33) * mm, "end": v(-51.46, 63.08) * mm});
            skArc(sketch, "E1016", {"start": v(-51.21, 63.52) * mm, "mid": v(-51.1, 64.3) * mm, "end": v(-51.9, 64.2) * mm});
            skArc(sketch, "E1017", {"start": v(-52.33, 63.95) * mm, "mid": v(-52.08, 64.02) * mm, "end": v(-51.9, 64.2) * mm});
            skLineSegment(sketch, "E1018", {"start": v(-52.33, 63.95) * mm, "end": v(-63.4, 63.95) * mm});
            skArc(sketch, "E1019", {"start": v(-63.83, 64.2) * mm, "mid": v(-63.65, 64.02) * mm, "end": v(-63.4, 63.95) * mm});
            skArc(sketch, "E1020", {"start": v(-63.83, 64.2) * mm, "mid": v(-64.61, 64.3) * mm, "end": v(-64.51, 63.52) * mm});
            skArc(sketch, "E1021", {"start": v(-64.26, 63.08) * mm, "mid": v(-64.33, 63.33) * mm, "end": v(-64.51, 63.52) * mm});
            skLineSegment(sketch, "E1022", {"start": v(-64.26, 63.08) * mm, "end": v(-64.26, 61.45) * mm});
            skArc(sketch, "E1023", {"start": v(-64.76, 60.95) * mm, "mid": v(-64.4, 61.1) * mm, "end": v(-64.26, 61.45) * mm});
            skLineSegment(sketch, "E1024", {"start": v(-64.76, 60.95) * mm, "end": v(-69.76, 60.95) * mm});
            skArc(sketch, "E1025", {"start": v(-70.26, 61.45) * mm, "mid": v(-70.11, 61.1) * mm, "end": v(-69.76, 60.95) * mm});
            skLineSegment(sketch, "E1026", {"start": v(-70.26, 61.45) * mm, "end": v(-70.26, 63.08) * mm});
            skArc(sketch, "E1027", {"start": v(-70.01, 63.52) * mm, "mid": v(-70.2, 63.33) * mm, "end": v(-70.26, 63.08) * mm});
            skArc(sketch, "E1028", {"start": v(-70.01, 63.52) * mm, "mid": v(-69.9, 64.3) * mm, "end": v(-70.7, 64.2) * mm});
            skArc(sketch, "E1029", {"start": v(-71.13, 63.95) * mm, "mid": v(-70.88, 64.02) * mm, "end": v(-70.7, 64.2) * mm});
            skLineSegment(sketch, "E1030", {"start": v(-71.13, 63.95) * mm, "end": v(-76.26, 63.95) * mm});
            skLineSegment(sketch, "E1031", {"start": v(-76.26, 63.95) * mm, "end": v(-76.26, 66.95) * mm});
            skLineSegment(sketch, "E1032", {"start": v(-76.26, 66.95) * mm, "end": v(-74.99, 66.95) * mm});
            skLineSegment(sketch, "E1033", {"start": v(-74.99, 66.95) * mm, "end": v(-74.99, 70.95) * mm});
            skLineSegment(sketch, "E1034", {"start": v(-74.99, 70.95) * mm, "end": v(-76.26, 70.95) * mm});
            skLineSegment(sketch, "E1035", {"start": v(-76.26, 70.95) * mm, "end": v(-76.26, 73.95) * mm});
            skLineSegment(sketch, "E1036", {"start": v(-76.26, 73.95) * mm, "end": v(-79.46, 73.95) * mm});
            skLineSegment(sketch, "E1037", {"start": v(-79.46, 73.95) * mm, "end": v(-79.46, 70.95) * mm});
            skLineSegment(sketch, "E1038", {"start": v(-79.46, 70.95) * mm, "end": v(-80.74, 70.95) * mm});
            skLineSegment(sketch, "E1039", {"start": v(-80.74, 70.95) * mm, "end": v(-80.74, 66.95) * mm});
            skLineSegment(sketch, "E1040", {"start": v(-80.74, 66.95) * mm, "end": v(-79.46, 66.95) * mm});
            skLineSegment(sketch, "E1041", {"start": v(-79.46, 66.95) * mm, "end": v(-79.46, 63.95) * mm});
            skLineSegment(sketch, "E1042", {"start": v(-79.46, 63.95) * mm, "end": v(-84.6, 63.95) * mm});
            skArc(sketch, "E1043", {"start": v(-85.03, 64.2) * mm, "mid": v(-84.85, 64.02) * mm, "end": v(-84.6, 63.95) * mm});
            skArc(sketch, "E1044", {"start": v(-85.03, 64.2) * mm, "mid": v(-85.81, 64.3) * mm, "end": v(-85.71, 63.52) * mm});
            skArc(sketch, "E1045", {"start": v(-85.46, 63.08) * mm, "mid": v(-85.53, 63.33) * mm, "end": v(-85.71, 63.52) * mm});
            skLineSegment(sketch, "E1046", {"start": v(-85.46, 63.08) * mm, "end": v(-85.46, 61.45) * mm});
            skArc(sketch, "E1047", {"start": v(-85.96, 60.95) * mm, "mid": v(-85.6, 61.1) * mm, "end": v(-85.46, 61.45) * mm});
            skLineSegment(sketch, "E1048", {"start": v(-85.96, 60.95) * mm, "end": v(-90.96, 60.95) * mm});
            skArc(sketch, "E1049", {"start": v(-91.46, 61.45) * mm, "mid": v(-91.31, 61.1) * mm, "end": v(-90.96, 60.95) * mm});
            skLineSegment(sketch, "E1050", {"start": v(-91.46, 61.45) * mm, "end": v(-91.46, 63.08) * mm});
            skArc(sketch, "E1051", {"start": v(-91.21, 63.52) * mm, "mid": v(-91.4, 63.33) * mm, "end": v(-91.46, 63.08) * mm});
            skArc(sketch, "E1052", {"start": v(-91.21, 63.52) * mm, "mid": v(-91.1, 64.3) * mm, "end": v(-91.9, 64.2) * mm});
            skArc(sketch, "E1053", {"start": v(-92.33, 63.95) * mm, "mid": v(-92.08, 64.02) * mm, "end": v(-91.9, 64.2) * mm});
            skLineSegment(sketch, "E1054", {"start": v(-92.33, 63.95) * mm, "end": v(-183.4, 63.95) * mm});
            skArc(sketch, "E1055", {"start": v(-183.83, 64.2) * mm, "mid": v(-183.65, 64.02) * mm, "end": v(-183.4, 63.95) * mm});
            skArc(sketch, "E1056", {"start": v(-183.83, 64.2) * mm, "mid": v(-184.61, 64.3) * mm, "end": v(-184.51, 63.52) * mm});
            skArc(sketch, "E1057", {"start": v(-184.26, 63.08) * mm, "mid": v(-184.33, 63.33) * mm, "end": v(-184.51, 63.52) * mm});
            skLineSegment(sketch, "E1058", {"start": v(-184.26, 63.08) * mm, "end": v(-184.26, 61.45) * mm});
            skArc(sketch, "E1059", {"start": v(-184.76, 60.95) * mm, "mid": v(-184.4, 61.1) * mm, "end": v(-184.26, 61.45) * mm});
            skLineSegment(sketch, "E1060", {"start": v(-184.76, 60.95) * mm, "end": v(-189.76, 60.95) * mm});
            skArc(sketch, "E1061", {"start": v(-190.26, 61.45) * mm, "mid": v(-190.11, 61.1) * mm, "end": v(-189.76, 60.95) * mm});
            skLineSegment(sketch, "E1062", {"start": v(-190.26, 61.45) * mm, "end": v(-190.26, 63.08) * mm});
            skArc(sketch, "E1063", {"start": v(-190.01, 63.52) * mm, "mid": v(-190.2, 63.33) * mm, "end": v(-190.26, 63.08) * mm});
            skArc(sketch, "E1064", {"start": v(-190.01, 63.52) * mm, "mid": v(-189.9, 64.3) * mm, "end": v(-190.7, 64.2) * mm});
            skArc(sketch, "E1065", {"start": v(-191.13, 63.95) * mm, "mid": v(-190.88, 64.02) * mm, "end": v(-190.7, 64.2) * mm});
            skLineSegment(sketch, "E1066", {"start": v(-191.13, 63.95) * mm, "end": v(-196.26, 63.95) * mm});
            skLineSegment(sketch, "E1067", {"start": v(-196.26, 63.95) * mm, "end": v(-196.26, 66.95) * mm});
            skLineSegment(sketch, "E1068", {"start": v(-196.26, 66.95) * mm, "end": v(-194.99, 66.95) * mm});
            skLineSegment(sketch, "E1069", {"start": v(-194.99, 66.95) * mm, "end": v(-194.99, 70.95) * mm});
            skLineSegment(sketch, "E1070", {"start": v(-194.99, 70.95) * mm, "end": v(-196.26, 70.95) * mm});
            skLineSegment(sketch, "E1071", {"start": v(-196.26, 70.95) * mm, "end": v(-196.26, 73.95) * mm});
            skLineSegment(sketch, "E1072", {"start": v(-196.26, 73.95) * mm, "end": v(-199.46, 73.95) * mm});
            skLineSegment(sketch, "E1073", {"start": v(-199.46, 73.95) * mm, "end": v(-199.46, 70.95) * mm});
            skLineSegment(sketch, "E1074", {"start": v(-199.46, 70.95) * mm, "end": v(-200.74, 70.95) * mm});
            skLineSegment(sketch, "E1075", {"start": v(-200.74, 70.95) * mm, "end": v(-200.74, 66.95) * mm});
            skLineSegment(sketch, "E1076", {"start": v(-200.74, 66.95) * mm, "end": v(-199.46, 66.95) * mm});
            skLineSegment(sketch, "E1077", {"start": v(-199.46, 66.95) * mm, "end": v(-199.46, 63.95) * mm});
            skLineSegment(sketch, "E1078", {"start": v(-199.46, 63.95) * mm, "end": v(-204.6, 63.95) * mm});
            skArc(sketch, "E1079", {"start": v(-205.03, 64.2) * mm, "mid": v(-204.85, 64.02) * mm, "end": v(-204.6, 63.95) * mm});
            skArc(sketch, "E1080", {"start": v(-205.03, 64.2) * mm, "mid": v(-205.81, 64.3) * mm, "end": v(-205.71, 63.52) * mm});
            skArc(sketch, "E1081", {"start": v(-205.46, 63.08) * mm, "mid": v(-205.53, 63.33) * mm, "end": v(-205.71, 63.52) * mm});
            skLineSegment(sketch, "E1082", {"start": v(-205.46, 63.08) * mm, "end": v(-205.46, 61.45) * mm});
            skArc(sketch, "E1083", {"start": v(-205.96, 60.95) * mm, "mid": v(-205.6, 61.1) * mm, "end": v(-205.46, 61.45) * mm});
            skLineSegment(sketch, "E1084", {"start": v(-205.96, 60.95) * mm, "end": v(-210.96, 60.95) * mm});
            skArc(sketch, "E1085", {"start": v(-211.46, 61.45) * mm, "mid": v(-211.31, 61.1) * mm, "end": v(-210.96, 60.95) * mm});
            skLineSegment(sketch, "E1086", {"start": v(-211.46, 61.45) * mm, "end": v(-211.46, 63.08) * mm});
            skArc(sketch, "E1087", {"start": v(-211.21, 63.52) * mm, "mid": v(-211.4, 63.33) * mm, "end": v(-211.46, 63.08) * mm});
            skArc(sketch, "E1088", {"start": v(-211.21, 63.52) * mm, "mid": v(-211.1, 64.3) * mm, "end": v(-211.9, 64.2) * mm});
            skArc(sketch, "E1089", {"start": v(-212.33, 63.95) * mm, "mid": v(-212.08, 64.02) * mm, "end": v(-211.9, 64.2) * mm});
            skLineSegment(sketch, "E1090", {"start": v(-212.33, 63.95) * mm, "end": v(-343.4, 63.95) * mm});
            skArc(sketch, "E1091", {"start": v(-343.83, 64.2) * mm, "mid": v(-343.65, 64.02) * mm, "end": v(-343.4, 63.95) * mm});
            skArc(sketch, "E1092", {"start": v(-343.83, 64.2) * mm, "mid": v(-344.61, 64.3) * mm, "end": v(-344.51, 63.52) * mm});
            skArc(sketch, "E1093", {"start": v(-344.26, 63.08) * mm, "mid": v(-344.33, 63.33) * mm, "end": v(-344.51, 63.52) * mm});
            skLineSegment(sketch, "E1094", {"start": v(-344.26, 63.08) * mm, "end": v(-344.26, 61.45) * mm});
            skArc(sketch, "E1095", {"start": v(-344.76, 60.95) * mm, "mid": v(-344.4, 61.1) * mm, "end": v(-344.26, 61.45) * mm});
            skLineSegment(sketch, "E1096", {"start": v(-344.76, 60.95) * mm, "end": v(-349.76, 60.95) * mm});
            skArc(sketch, "E1097", {"start": v(-350.26, 61.45) * mm, "mid": v(-350.11, 61.1) * mm, "end": v(-349.76, 60.95) * mm});
            skLineSegment(sketch, "E1098", {"start": v(-350.26, 61.45) * mm, "end": v(-350.26, 63.08) * mm});
            skArc(sketch, "E1099", {"start": v(-350.01, 63.52) * mm, "mid": v(-350.2, 63.33) * mm, "end": v(-350.26, 63.08) * mm});
            skArc(sketch, "E1100", {"start": v(-350.01, 63.52) * mm, "mid": v(-349.9, 64.3) * mm, "end": v(-350.7, 64.2) * mm});
            skArc(sketch, "E1101", {"start": v(-351.13, 63.95) * mm, "mid": v(-350.88, 64.02) * mm, "end": v(-350.7, 64.2) * mm});
            skLineSegment(sketch, "E1102", {"start": v(-351.13, 63.95) * mm, "end": v(-356.26, 63.95) * mm});
            skLineSegment(sketch, "E1103", {"start": v(-356.26, 63.95) * mm, "end": v(-356.26, 66.95) * mm});
            skLineSegment(sketch, "E1104", {"start": v(-356.26, 66.95) * mm, "end": v(-354.99, 66.95) * mm});
            skLineSegment(sketch, "E1105", {"start": v(-354.99, 66.95) * mm, "end": v(-354.99, 70.95) * mm});
            skLineSegment(sketch, "E1106", {"start": v(-354.99, 70.95) * mm, "end": v(-356.26, 70.95) * mm});
            skLineSegment(sketch, "E1107", {"start": v(-356.26, 70.95) * mm, "end": v(-356.26, 73.95) * mm});
            skLineSegment(sketch, "E1108", {"start": v(-356.26, 73.95) * mm, "end": v(-359.46, 73.95) * mm});
            skLineSegment(sketch, "E1109", {"start": v(-359.46, 73.95) * mm, "end": v(-359.46, 70.95) * mm});
            skLineSegment(sketch, "E1110", {"start": v(-359.46, 70.95) * mm, "end": v(-360.74, 70.95) * mm});
            skLineSegment(sketch, "E1111", {"start": v(-360.74, 70.95) * mm, "end": v(-360.74, 66.95) * mm});
            skLineSegment(sketch, "E1112", {"start": v(-360.74, 66.95) * mm, "end": v(-359.46, 66.95) * mm});
            skLineSegment(sketch, "E1113", {"start": v(-359.46, 66.95) * mm, "end": v(-359.46, 63.95) * mm});
            skLineSegment(sketch, "E1114", {"start": v(-359.46, 63.95) * mm, "end": v(-364.6, 63.95) * mm});
            skArc(sketch, "E1115", {"start": v(-365.03, 64.2) * mm, "mid": v(-364.85, 64.02) * mm, "end": v(-364.6, 63.95) * mm});
            skArc(sketch, "E1116", {"start": v(-365.03, 64.2) * mm, "mid": v(-365.81, 64.3) * mm, "end": v(-365.71, 63.52) * mm});
            skArc(sketch, "E1117", {"start": v(-365.46, 63.08) * mm, "mid": v(-365.53, 63.33) * mm, "end": v(-365.71, 63.52) * mm});
            skLineSegment(sketch, "E1118", {"start": v(-365.46, 63.08) * mm, "end": v(-365.46, 61.45) * mm});
            skArc(sketch, "E1119", {"start": v(-365.96, 60.95) * mm, "mid": v(-365.6, 61.1) * mm, "end": v(-365.46, 61.45) * mm});
            skLineSegment(sketch, "E1120", {"start": v(-365.96, 60.95) * mm, "end": v(-370.96, 60.95) * mm});
            skArc(sketch, "E1121", {"start": v(-371.46, 61.45) * mm, "mid": v(-371.31, 61.1) * mm, "end": v(-370.96, 60.95) * mm});
            skLineSegment(sketch, "E1122", {"start": v(-371.46, 61.45) * mm, "end": v(-371.46, 63.08) * mm});
            skArc(sketch, "E1123", {"start": v(-371.21, 63.52) * mm, "mid": v(-371.4, 63.33) * mm, "end": v(-371.46, 63.08) * mm});
            skArc(sketch, "E1124", {"start": v(-371.21, 63.52) * mm, "mid": v(-371.1, 64.3) * mm, "end": v(-371.9, 64.2) * mm});
            skArc(sketch, "E1125", {"start": v(-372.33, 63.95) * mm, "mid": v(-372.08, 64.02) * mm, "end": v(-371.9, 64.2) * mm});
            skLineSegment(sketch, "E1126", {"start": v(-372.33, 63.95) * mm, "end": v(-382.86, 63.95) * mm});
            skLineSegment(sketch, "E1127", {"start": v(-382.86, 63.95) * mm, "end": v(-382.86, 74.6) * mm});
            skLineSegment(sketch, "E1128", {"start": v(-382.86, 74.6) * mm, "end": v(-380.63, 74.6) * mm});
            skArc(sketch, "E1129", {"start": v(-380.2, 74.35) * mm, "mid": v(-380.38, 74.53) * mm, "end": v(-380.63, 74.6) * mm});
            skArc(sketch, "E1130", {"start": v(-380.2, 74.35) * mm, "mid": v(-379.4, 74.24) * mm, "end": v(-379.51, 75.03) * mm});
            skArc(sketch, "E1131", {"start": v(-379.76, 75.46) * mm, "mid": v(-379.7, 75.21) * mm, "end": v(-379.51, 75.03) * mm});
            skLineSegment(sketch, "E1132", {"start": v(-379.76, 75.46) * mm, "end": v(-379.76, 83) * mm});
            skLineSegment(sketch, "E1133", {"start": v(-379.76, 83) * mm, "end": v(-376.76, 83) * mm});
            skLineSegment(sketch, "E1134", {"start": v(-376.76, 83) * mm, "end": v(-376.76, 81.72) * mm});
            skLineSegment(sketch, "E1135", {"start": v(-376.76, 81.72) * mm, "end": v(-372.76, 81.72) * mm});
            skLineSegment(sketch, "E1136", {"start": v(-372.76, 81.72) * mm, "end": v(-372.76, 83) * mm});
            skLineSegment(sketch, "E1137", {"start": v(-372.76, 83) * mm, "end": v(-369.76, 83) * mm});
            skLineSegment(sketch, "E1138", {"start": v(-369.76, 83) * mm, "end": v(-369.76, 86.2) * mm});
            skLineSegment(sketch, "E1139", {"start": v(-369.76, 86.2) * mm, "end": v(-372.76, 86.2) * mm});
            skLineSegment(sketch, "E1140", {"start": v(-372.76, 86.2) * mm, "end": v(-372.76, 87.47) * mm});
            skLineSegment(sketch, "E1141", {"start": v(-372.76, 87.47) * mm, "end": v(-376.76, 87.47) * mm});
            skLineSegment(sketch, "E1142", {"start": v(-376.76, 87.47) * mm, "end": v(-376.76, 86.2) * mm});
            skLineSegment(sketch, "E1143", {"start": v(-376.76, 86.2) * mm, "end": v(-379.76, 86.2) * mm});
            skLineSegment(sketch, "E1144", {"start": v(-379.76, 86.2) * mm, "end": v(-379.76, 94.95) * mm});
            skLineSegment(sketch, "E1145", {"start": v(-379.76, 94.95) * mm, "end": v(-57.31, 188.95) * mm});
            skLineSegment(sketch, "E1146", {"start": v(-57.31, 188.95) * mm, "end": v(-52.33, 188.95) * mm});
            skLineSegment(sketch, "E1147", {"start": v(-293.86, 88.95) * mm, "end": v(-328.86, 88.95) * mm});
            skArc(sketch, "E1148", {"start": v(-328.86, 88.95) * mm, "mid": v(-333.86, 83.95) * mm, "end": v(-328.86, 78.95) * mm});
            skLineSegment(sketch, "E1149", {"start": v(-328.86, 78.95) * mm, "end": v(-293.86, 78.95) * mm});
            skArc(sketch, "E1150", {"start": v(-293.86, 78.95) * mm, "mid": v(-288.86, 83.95) * mm, "end": v(-293.86, 88.95) * mm});
            skLineSegment(sketch, "E1151", {"start": v(-20.86, 88.95) * mm, "end": v(-20.86, 96.95) * mm});
            skArc(sketch, "E1152", {"start": v(-20.86, 96.95) * mm, "mid": v(-24.86, 100.95) * mm, "end": v(-28.86, 96.95) * mm});
            skLineSegment(sketch, "E1153", {"start": v(-28.86, 96.95) * mm, "end": v(-28.86, 88.95) * mm});
            skArc(sketch, "E1154", {"start": v(-28.86, 88.95) * mm, "mid": v(-24.86, 84.95) * mm, "end": v(-20.86, 88.95) * mm});
            skLineSegment(sketch, "E1155", {"start": v(-20.86, 139.68) * mm, "end": v(-20.86, 147.68) * mm});
            skArc(sketch, "E1156", {"start": v(-20.86, 147.68) * mm, "mid": v(-24.86, 151.68) * mm, "end": v(-28.86, 147.68) * mm});
            skLineSegment(sketch, "E1157", {"start": v(-28.86, 147.68) * mm, "end": v(-28.86, 139.68) * mm});
            skArc(sketch, "E1158", {"start": v(-28.86, 139.68) * mm, "mid": v(-24.86, 135.68) * mm, "end": v(-20.86, 139.68) * mm});
            skLineSegment(sketch, "E1159", {"start": v(-24.26, 63.08) * mm, "end": v(-24.26, -148.55) * mm});
            skArc(sketch, "E1160", {"start": v(-24.76, -149.05) * mm, "mid": v(-24.4, -148.9) * mm, "end": v(-24.26, -148.55) * mm});
            skLineSegment(sketch, "E1161", {"start": v(-24.76, -149.05) * mm, "end": v(-29.76, -149.05) * mm});
            skArc(sketch, "E1162", {"start": v(-30.26, -148.55) * mm, "mid": v(-30.11, -148.9) * mm, "end": v(-29.76, -149.05) * mm});
            skLineSegment(sketch, "E1163", {"start": v(-30.26, -148.55) * mm, "end": v(-30.26, -146.92) * mm});
            skArc(sketch, "E1164", {"start": v(-30.01, -146.48) * mm, "mid": v(-30.2, -146.67) * mm, "end": v(-30.26, -146.92) * mm});
            skArc(sketch, "E1165", {"start": v(-30.01, -146.48) * mm, "mid": v(-29.9, -145.7) * mm, "end": v(-30.7, -145.8) * mm});
            skArc(sketch, "E1166", {"start": v(-31.13, -146.05) * mm, "mid": v(-30.88, -145.98) * mm, "end": v(-30.7, -145.8) * mm});
            skLineSegment(sketch, "E1167", {"start": v(-31.13, -146.05) * mm, "end": v(-36.26, -146.05) * mm});
            skLineSegment(sketch, "E1168", {"start": v(-36.26, -146.05) * mm, "end": v(-36.26, -143.05) * mm});
            skLineSegment(sketch, "E1169", {"start": v(-36.26, -143.05) * mm, "end": v(-34.99, -143.05) * mm});
            skLineSegment(sketch, "E1170", {"start": v(-34.99, -143.05) * mm, "end": v(-34.99, -139.05) * mm});
            skLineSegment(sketch, "E1171", {"start": v(-34.99, -139.05) * mm, "end": v(-36.26, -139.05) * mm});
            skLineSegment(sketch, "E1172", {"start": v(-36.26, -139.05) * mm, "end": v(-36.26, -136.05) * mm});
            skLineSegment(sketch, "E1173", {"start": v(-36.26, -136.05) * mm, "end": v(-39.46, -136.05) * mm});
            skLineSegment(sketch, "E1174", {"start": v(-39.46, -136.05) * mm, "end": v(-39.46, -139.05) * mm});
            skLineSegment(sketch, "E1175", {"start": v(-39.46, -139.05) * mm, "end": v(-40.74, -139.05) * mm});
            skLineSegment(sketch, "E1176", {"start": v(-40.74, -139.05) * mm, "end": v(-40.74, -143.05) * mm});
            skLineSegment(sketch, "E1177", {"start": v(-40.74, -143.05) * mm, "end": v(-39.46, -143.05) * mm});
            skLineSegment(sketch, "E1178", {"start": v(-39.46, -143.05) * mm, "end": v(-39.46, -146.05) * mm});
            skLineSegment(sketch, "E1179", {"start": v(-39.46, -146.05) * mm, "end": v(-44.6, -146.05) * mm});
            skArc(sketch, "E1180", {"start": v(-45.03, -145.8) * mm, "mid": v(-44.85, -145.98) * mm, "end": v(-44.6, -146.05) * mm});
            skArc(sketch, "E1181", {"start": v(-45.03, -145.8) * mm, "mid": v(-45.81, -145.7) * mm, "end": v(-45.71, -146.48) * mm});
            skArc(sketch, "E1182", {"start": v(-45.46, -146.92) * mm, "mid": v(-45.53, -146.67) * mm, "end": v(-45.71, -146.48) * mm});
            skLineSegment(sketch, "E1183", {"start": v(-45.46, -146.92) * mm, "end": v(-45.46, -148.55) * mm});
            skArc(sketch, "E1184", {"start": v(-45.96, -149.05) * mm, "mid": v(-45.6, -148.9) * mm, "end": v(-45.46, -148.55) * mm});
            skLineSegment(sketch, "E1185", {"start": v(-45.96, -149.05) * mm, "end": v(-50.96, -149.05) * mm});
            skArc(sketch, "E1186", {"start": v(-51.46, -148.55) * mm, "mid": v(-51.31, -148.9) * mm, "end": v(-50.96, -149.05) * mm});
            skLineSegment(sketch, "E1187", {"start": v(-51.46, -148.55) * mm, "end": v(-51.46, 63.08) * mm});
            skArc(sketch, "E1188", {"start": v(-37.08, -6.55) * mm, "mid": v(-36.83, -6.48) * mm, "end": v(-36.64, -6.3) * mm});
            skArc(sketch, "E1189", {"start": v(-35.96, -6.98) * mm, "mid": v(-35.86, -6.2) * mm, "end": v(-36.64, -6.3) * mm});
            skArc(sketch, "E1190", {"start": v(-35.96, -6.98) * mm, "mid": v(-36.14, -7.17) * mm, "end": v(-36.21, -7.42) * mm});
            skLineSegment(sketch, "E1191", {"start": v(-36.21, -7.42) * mm, "end": v(-36.21, -11.89) * mm});
            skArc(sketch, "E1192", {"start": v(-36.21, -11.89) * mm, "mid": v(-36.14, -12.14) * mm, "end": v(-35.96, -12.32) * mm});
            skArc(sketch, "E1193", {"start": v(-36.64, -13) * mm, "mid": v(-35.86, -13.1) * mm, "end": v(-35.96, -12.32) * mm});
            skArc(sketch, "E1194", {"start": v(-36.64, -13) * mm, "mid": v(-36.83, -12.82) * mm, "end": v(-37.08, -12.75) * mm});
            skLineSegment(sketch, "E1195", {"start": v(-37.08, -12.75) * mm, "end": v(-38.65, -12.75) * mm});
            skArc(sketch, "E1196", {"start": v(-38.65, -12.75) * mm, "mid": v(-38.9, -12.82) * mm, "end": v(-39.08, -13) * mm});
            skArc(sketch, "E1197", {"start": v(-39.76, -12.32) * mm, "mid": v(-39.86, -13.1) * mm, "end": v(-39.08, -13) * mm});
            skArc(sketch, "E1198", {"start": v(-39.76, -12.32) * mm, "mid": v(-39.58, -12.14) * mm, "end": v(-39.51, -11.89) * mm});
            skLineSegment(sketch, "E1199", {"start": v(-39.51, -11.89) * mm, "end": v(-39.51, -7.42) * mm});
            skArc(sketch, "E1200", {"start": v(-39.51, -7.42) * mm, "mid": v(-39.58, -7.17) * mm, "end": v(-39.76, -6.98) * mm});
            skArc(sketch, "E1201", {"start": v(-39.08, -6.3) * mm, "mid": v(-39.86, -6.2) * mm, "end": v(-39.76, -6.98) * mm});
            skArc(sketch, "E1202", {"start": v(-39.08, -6.3) * mm, "mid": v(-38.9, -6.48) * mm, "end": v(-38.65, -6.55) * mm});
            skLineSegment(sketch, "E1203", {"start": v(-38.65, -6.55) * mm, "end": v(-37.08, -6.55) * mm});
            skArc(sketch, "E1204", {"start": v(-37.08, 14.65) * mm, "mid": v(-36.83, 14.72) * mm, "end": v(-36.64, 14.9) * mm});
            skArc(sketch, "E1205", {"start": v(-35.96, 14.22) * mm, "mid": v(-35.86, 15) * mm, "end": v(-36.64, 14.9) * mm});
            skArc(sketch, "E1206", {"start": v(-35.96, 14.22) * mm, "mid": v(-36.14, 14.03) * mm, "end": v(-36.21, 13.78) * mm});
            skLineSegment(sketch, "E1207", {"start": v(-36.21, 13.78) * mm, "end": v(-36.21, 9.31) * mm});
            skArc(sketch, "E1208", {"start": v(-36.21, 9.31) * mm, "mid": v(-36.14, 9.06) * mm, "end": v(-35.96, 8.88) * mm});
            skArc(sketch, "E1209", {"start": v(-36.64, 8.2) * mm, "mid": v(-35.86, 8.1) * mm, "end": v(-35.96, 8.88) * mm});
            skArc(sketch, "E1210", {"start": v(-36.64, 8.2) * mm, "mid": v(-36.83, 8.38) * mm, "end": v(-37.08, 8.45) * mm});
            skLineSegment(sketch, "E1211", {"start": v(-37.08, 8.45) * mm, "end": v(-38.65, 8.45) * mm});
            skArc(sketch, "E1212", {"start": v(-38.65, 8.45) * mm, "mid": v(-38.9, 8.38) * mm, "end": v(-39.08, 8.2) * mm});
            skArc(sketch, "E1213", {"start": v(-39.76, 8.88) * mm, "mid": v(-39.86, 8.1) * mm, "end": v(-39.08, 8.2) * mm});
            skArc(sketch, "E1214", {"start": v(-39.76, 8.88) * mm, "mid": v(-39.58, 9.06) * mm, "end": v(-39.51, 9.31) * mm});
            skLineSegment(sketch, "E1215", {"start": v(-39.51, 9.31) * mm, "end": v(-39.51, 13.78) * mm});
            skArc(sketch, "E1216", {"start": v(-39.51, 13.78) * mm, "mid": v(-39.58, 14.03) * mm, "end": v(-39.76, 14.22) * mm});
            skArc(sketch, "E1217", {"start": v(-39.08, 14.9) * mm, "mid": v(-39.86, 15) * mm, "end": v(-39.76, 14.22) * mm});
            skArc(sketch, "E1218", {"start": v(-39.08, 14.9) * mm, "mid": v(-38.9, 14.72) * mm, "end": v(-38.65, 14.65) * mm});
            skLineSegment(sketch, "E1219", {"start": v(-38.65, 14.65) * mm, "end": v(-37.08, 14.65) * mm});
            skCircle(sketch, "E1220", {"center": v(-37.86, 0.95) * mm, "radius": 1.6 * mm});
            skLineSegment(sketch, "E1221", {"start": v(-262.47, 177.78) * mm, "end": v(-265.67, 177.78) * mm});
            skLineSegment(sketch, "E1222", {"start": v(-265.67, 177.78) * mm, "end": v(-265.67, 180.78) * mm});
            skLineSegment(sketch, "E1223", {"start": v(-265.67, 180.78) * mm, "end": v(-266.95, 180.78) * mm});
            skLineSegment(sketch, "E1224", {"start": v(-266.95, 180.78) * mm, "end": v(-266.95, 184.78) * mm});
            skLineSegment(sketch, "E1225", {"start": v(-266.95, 184.78) * mm, "end": v(-265.67, 184.78) * mm});
            skLineSegment(sketch, "E1226", {"start": v(-265.67, 184.78) * mm, "end": v(-265.67, 187.78) * mm});
            skLineSegment(sketch, "E1227", {"start": v(-265.67, 187.78) * mm, "end": v(-270.8, 187.78) * mm});
            skArc(sketch, "E1228", {"start": v(-270.8, 187.78) * mm, "mid": v(-271.05, 187.71) * mm, "end": v(-271.24, 187.53) * mm});
            skArc(sketch, "E1229", {"start": v(-271.92, 188.21) * mm, "mid": v(-272.02, 187.42) * mm, "end": v(-271.24, 187.53) * mm});
            skArc(sketch, "E1230", {"start": v(-271.92, 188.21) * mm, "mid": v(-271.74, 188.4) * mm, "end": v(-271.67, 188.64) * mm});
            skLineSegment(sketch, "E1231", {"start": v(-271.67, 188.64) * mm, "end": v(-271.67, 190.28) * mm});
            skArc(sketch, "E1232", {"start": v(-271.67, 190.28) * mm, "mid": v(-271.82, 190.63) * mm, "end": v(-272.17, 190.78) * mm});
            skLineSegment(sketch, "E1233", {"start": v(-272.17, 190.78) * mm, "end": v(-277.17, 190.78) * mm});
            skArc(sketch, "E1234", {"start": v(-277.17, 190.78) * mm, "mid": v(-277.52, 190.63) * mm, "end": v(-277.67, 190.28) * mm});
            skLineSegment(sketch, "E1235", {"start": v(-277.67, 190.28) * mm, "end": v(-277.67, 188.64) * mm});
            skArc(sketch, "E1236", {"start": v(-277.67, 188.64) * mm, "mid": v(-277.6, 188.4) * mm, "end": v(-277.42, 188.21) * mm});
            skArc(sketch, "E1237", {"start": v(-278.1, 187.53) * mm, "mid": v(-277.32, 187.42) * mm, "end": v(-277.42, 188.21) * mm});
            skArc(sketch, "E1238", {"start": v(-278.1, 187.53) * mm, "mid": v(-278.29, 187.71) * mm, "end": v(-278.54, 187.78) * mm});
            skLineSegment(sketch, "E1239", {"start": v(-278.54, 187.78) * mm, "end": v(-283.07, 187.78) * mm});
            skLineSegment(sketch, "E1240", {"start": v(-283.07, 187.78) * mm, "end": v(-283.07, 182.58) * mm});
            skLineSegment(sketch, "E1241", {"start": v(-278.07, 175.27) * mm, "end": v(-278.07, 140.78) * mm});
            skArc(sketch, "E1242", {"start": v(-278.07, 140.78) * mm, "mid": v(-277.48, 139.36) * mm, "end": v(-276.07, 138.78) * mm});
            skLineSegment(sketch, "E1243", {"start": v(-276.07, 138.78) * mm, "end": v(-242.07, 138.78) * mm});
            skArc(sketch, "E1244", {"start": v(-242.07, 138.78) * mm, "mid": v(-240.66, 139.36) * mm, "end": v(-240.07, 140.78) * mm});
            skLineSegment(sketch, "E1245", {"start": v(-240.07, 140.78) * mm, "end": v(-240.07, 180.8) * mm});
            skArc(sketch, "E1246", {"start": v(-249.6, 187.78) * mm, "mid": v(-249.85, 187.71) * mm, "end": v(-250.04, 187.53) * mm});
            skArc(sketch, "E1247", {"start": v(-250.72, 188.21) * mm, "mid": v(-250.82, 187.42) * mm, "end": v(-250.04, 187.53) * mm});
            skArc(sketch, "E1248", {"start": v(-250.72, 188.21) * mm, "mid": v(-250.54, 188.4) * mm, "end": v(-250.47, 188.64) * mm});
            skLineSegment(sketch, "E1249", {"start": v(-250.47, 188.64) * mm, "end": v(-250.47, 190.28) * mm});
            skArc(sketch, "E1250", {"start": v(-250.47, 190.28) * mm, "mid": v(-250.62, 190.63) * mm, "end": v(-250.97, 190.78) * mm});
            skLineSegment(sketch, "E1251", {"start": v(-250.97, 190.78) * mm, "end": v(-255.97, 190.78) * mm});
            skArc(sketch, "E1252", {"start": v(-255.97, 190.78) * mm, "mid": v(-256.32, 190.63) * mm, "end": v(-256.47, 190.28) * mm});
            skLineSegment(sketch, "E1253", {"start": v(-256.47, 190.28) * mm, "end": v(-256.47, 188.64) * mm});
            skArc(sketch, "E1254", {"start": v(-256.47, 188.64) * mm, "mid": v(-256.4, 188.4) * mm, "end": v(-256.22, 188.21) * mm});
            skArc(sketch, "E1255", {"start": v(-256.9, 187.53) * mm, "mid": v(-256.12, 187.42) * mm, "end": v(-256.22, 188.21) * mm});
            skArc(sketch, "E1256", {"start": v(-256.9, 187.53) * mm, "mid": v(-257.09, 187.71) * mm, "end": v(-257.34, 187.78) * mm});
            skLineSegment(sketch, "E1257", {"start": v(-257.34, 187.78) * mm, "end": v(-262.47, 187.78) * mm});
            skLineSegment(sketch, "E1258", {"start": v(-262.47, 187.78) * mm, "end": v(-262.47, 184.78) * mm});
            skLineSegment(sketch, "E1259", {"start": v(-262.47, 184.78) * mm, "end": v(-261.2, 184.78) * mm});
            skLineSegment(sketch, "E1260", {"start": v(-261.2, 184.78) * mm, "end": v(-261.2, 180.78) * mm});
            skLineSegment(sketch, "E1261", {"start": v(-261.2, 180.78) * mm, "end": v(-262.47, 180.78) * mm});
            skLineSegment(sketch, "E1262", {"start": v(-262.47, 180.78) * mm, "end": v(-262.47, 177.78) * mm});
            skCircle(sketch, "E1263", {"center": v(-259.07, 159) * mm, "radius": 11.1 * mm});
            skCircle(sketch, "E1264", {"center": v(-243.57, 174.5) * mm, "radius": 1.6 * mm});
            skCircle(sketch, "E1265", {"center": v(-243.57, 143.5) * mm, "radius": 1.6 * mm});
            skCircle(sketch, "E1266", {"center": v(-274.57, 174.5) * mm, "radius": 1.6 * mm});
            skCircle(sketch, "E1267", {"center": v(-274.57, 143.5) * mm, "radius": 1.6 * mm});
            skLineSegment(sketch, "E1268", {"start": v(-240.27, 181.4) * mm, "end": v(-245.07, 187.78) * mm});
            skLineSegment(sketch, "E1269", {"start": v(-278.27, 175.87) * mm, "end": v(-282.87, 181.97) * mm});
            skArc(sketch, "E1270", {"start": v(-240.07, 180.8) * mm, "mid": v(-240.12, 181.12) * mm, "end": v(-240.27, 181.4) * mm});
            skArc(sketch, "E1271", {"start": v(-278.07, 175.27) * mm, "mid": v(-278.12, 175.58) * mm, "end": v(-278.27, 175.87) * mm});
            skArc(sketch, "E1272", {"start": v(-283.07, 182.58) * mm, "mid": v(-283.02, 182.26) * mm, "end": v(-282.87, 181.97) * mm});
            skLineSegment(sketch, "E1273", {"start": v(-245.07, 187.78) * mm, "end": v(-249.6, 187.78) * mm});
            skLineSegment(sketch, "E1274", {"start": v(-151.77, -10.15) * mm, "end": v(-356.65, -10.15) * mm});
            skLineSegment(sketch, "E1275", {"start": v(-357.6, -9.45) * mm, "end": v(-359.17, -4.47) * mm});
            skLineSegment(sketch, "E1276", {"start": v(-360.12, -3.76) * mm, "end": v(-379.39, -3.76) * mm});
            skArc(sketch, "E1277", {"start": v(-379.39, -3.76) * mm, "mid": v(-382.92, -5.23) * mm, "end": v(-384.39, -8.76) * mm});
            skLineSegment(sketch, "E1278", {"start": v(-384.39, -8.76) * mm, "end": v(-384.39, -43.15) * mm});
            skArc(sketch, "E1279", {"start": v(-384.39, -43.15) * mm, "mid": v(-382.92, -46.69) * mm, "end": v(-379.39, -48.15) * mm});
            skLineSegment(sketch, "E1280", {"start": v(-379.39, -48.15) * mm, "end": v(-349.71, -48.15) * mm});
            skArc(sketch, "E1281", {"start": v(-349.21, -48.65) * mm, "mid": v(-349.36, -48.3) * mm, "end": v(-349.71, -48.15) * mm});
            skArc(sketch, "E1282", {"start": v(-328.71, -48.15) * mm, "mid": v(-329.07, -48.3) * mm, "end": v(-329.21, -48.65) * mm});
            skLineSegment(sketch, "E1283", {"start": v(-328.71, -48.15) * mm, "end": v(-179.7, -48.15) * mm});
            skArc(sketch, "E1284", {"start": v(-179.2, -48.65) * mm, "mid": v(-179.36, -48.3) * mm, "end": v(-179.7, -48.15) * mm});
            skLineSegment(sketch, "E1285", {"start": v(-179.2, -48.65) * mm, "end": v(-179.2, -54.15) * mm});
            skArc(sketch, "E1286", {"start": v(-179.2, -54.15) * mm, "mid": v(-178.62, -55.56) * mm, "end": v(-177.2, -56.15) * mm});
            skLineSegment(sketch, "E1287", {"start": v(-177.2, -56.15) * mm, "end": v(-172.9, -56.15) * mm});
            skArc(sketch, "E1288", {"start": v(-165.94, -55.37) * mm, "mid": v(-169.2, -49.2) * mm, "end": v(-172.48, -55.37) * mm});
            skLineSegment(sketch, "E1289", {"start": v(-165.53, -56.15) * mm, "end": v(-161.2, -56.15) * mm});
            skArc(sketch, "E1290", {"start": v(-161.2, -56.15) * mm, "mid": v(-159.8, -55.56) * mm, "end": v(-159.2, -54.15) * mm});
            skLineSegment(sketch, "E1291", {"start": v(-159.2, -54.15) * mm, "end": v(-159.2, -48.65) * mm});
            skArc(sketch, "E1292", {"start": v(-158.7, -48.15) * mm, "mid": v(-159.06, -48.3) * mm, "end": v(-159.2, -48.65) * mm});
            skLineSegment(sketch, "E1293", {"start": v(-158.7, -48.15) * mm, "end": v(-129.04, -48.15) * mm});
            skArc(sketch, "E1294", {"start": v(-129.04, -48.15) * mm, "mid": v(-125.5, -46.69) * mm, "end": v(-124.04, -43.15) * mm});
            skLineSegment(sketch, "E1295", {"start": v(-124.04, -43.15) * mm, "end": v(-124.04, -8.76) * mm});
            skArc(sketch, "E1296", {"start": v(-124.04, -8.76) * mm, "mid": v(-125.5, -5.23) * mm, "end": v(-129.04, -3.76) * mm});
            skLineSegment(sketch, "E1297", {"start": v(-129.04, -3.76) * mm, "end": v(-148.3, -3.76) * mm});
            skLineSegment(sketch, "E1298", {"start": v(-149.26, -4.47) * mm, "end": v(-150.82, -9.45) * mm});
            skArc(sketch, "E1299", {"start": v(-134.82, -21.26) * mm, "mid": v(-135.07, -21.33) * mm, "end": v(-135.25, -21.51) * mm});
            skArc(sketch, "E1300", {"start": v(-135.94, -20.83) * mm, "mid": v(-136.04, -21.62) * mm, "end": v(-135.25, -21.51) * mm});
            skArc(sketch, "E1301", {"start": v(-135.94, -20.83) * mm, "mid": v(-135.75, -20.65) * mm, "end": v(-135.69, -20.4) * mm});
            skLineSegment(sketch, "E1302", {"start": v(-135.69, -20.4) * mm, "end": v(-135.69, -15.93) * mm});
            skArc(sketch, "E1303", {"start": v(-135.69, -15.93) * mm, "mid": v(-135.75, -15.68) * mm, "end": v(-135.94, -15.5) * mm});
            skArc(sketch, "E1304", {"start": v(-135.25, -14.81) * mm, "mid": v(-136.04, -14.71) * mm, "end": v(-135.94, -15.5) * mm});
            skArc(sketch, "E1305", {"start": v(-135.25, -14.81) * mm, "mid": v(-135.07, -15) * mm, "end": v(-134.82, -15.06) * mm});
            skLineSegment(sketch, "E1306", {"start": v(-134.82, -15.06) * mm, "end": v(-133.25, -15.06) * mm});
            skArc(sketch, "E1307", {"start": v(-133.25, -15.06) * mm, "mid": v(-133, -15) * mm, "end": v(-132.82, -14.81) * mm});
            skArc(sketch, "E1308", {"start": v(-132.14, -15.5) * mm, "mid": v(-132.03, -14.71) * mm, "end": v(-132.82, -14.81) * mm});
            skArc(sketch, "E1309", {"start": v(-132.14, -15.5) * mm, "mid": v(-132.32, -15.68) * mm, "end": v(-132.39, -15.93) * mm});
            skLineSegment(sketch, "E1310", {"start": v(-132.39, -15.93) * mm, "end": v(-132.39, -20.4) * mm});
            skArc(sketch, "E1311", {"start": v(-132.39, -20.4) * mm, "mid": v(-132.32, -20.65) * mm, "end": v(-132.14, -20.83) * mm});
            skArc(sketch, "E1312", {"start": v(-132.82, -21.51) * mm, "mid": v(-132.03, -21.62) * mm, "end": v(-132.14, -20.83) * mm});
            skArc(sketch, "E1313", {"start": v(-132.82, -21.51) * mm, "mid": v(-133, -21.33) * mm, "end": v(-133.25, -21.26) * mm});
            skLineSegment(sketch, "E1314", {"start": v(-133.25, -21.26) * mm, "end": v(-134.82, -21.26) * mm});
            skArc(sketch, "E1315", {"start": v(-134.82, -42.46) * mm, "mid": v(-135.07, -42.53) * mm, "end": v(-135.25, -42.71) * mm});
            skArc(sketch, "E1316", {"start": v(-135.94, -42.03) * mm, "mid": v(-136.04, -42.82) * mm, "end": v(-135.25, -42.71) * mm});
            skArc(sketch, "E1317", {"start": v(-135.94, -42.03) * mm, "mid": v(-135.75, -41.85) * mm, "end": v(-135.69, -41.6) * mm});
            skLineSegment(sketch, "E1318", {"start": v(-135.69, -41.6) * mm, "end": v(-135.69, -37.13) * mm});
            skArc(sketch, "E1319", {"start": v(-135.69, -37.13) * mm, "mid": v(-135.75, -36.88) * mm, "end": v(-135.94, -36.7) * mm});
            skArc(sketch, "E1320", {"start": v(-135.25, -36.01) * mm, "mid": v(-136.04, -35.91) * mm, "end": v(-135.94, -36.7) * mm});
            skArc(sketch, "E1321", {"start": v(-135.25, -36.01) * mm, "mid": v(-135.07, -36.2) * mm, "end": v(-134.82, -36.26) * mm});
            skLineSegment(sketch, "E1322", {"start": v(-134.82, -36.26) * mm, "end": v(-133.25, -36.26) * mm});
            skArc(sketch, "E1323", {"start": v(-133.25, -36.26) * mm, "mid": v(-133, -36.2) * mm, "end": v(-132.82, -36.01) * mm});
            skArc(sketch, "E1324", {"start": v(-132.14, -36.7) * mm, "mid": v(-132.03, -35.91) * mm, "end": v(-132.82, -36.01) * mm});
            skArc(sketch, "E1325", {"start": v(-132.14, -36.7) * mm, "mid": v(-132.32, -36.88) * mm, "end": v(-132.39, -37.13) * mm});
            skLineSegment(sketch, "E1326", {"start": v(-132.39, -37.13) * mm, "end": v(-132.39, -41.6) * mm});
            skArc(sketch, "E1327", {"start": v(-132.39, -41.6) * mm, "mid": v(-132.32, -41.85) * mm, "end": v(-132.14, -42.03) * mm});
            skArc(sketch, "E1328", {"start": v(-132.82, -42.71) * mm, "mid": v(-132.03, -42.82) * mm, "end": v(-132.14, -42.03) * mm});
            skArc(sketch, "E1329", {"start": v(-132.82, -42.71) * mm, "mid": v(-133, -42.53) * mm, "end": v(-133.25, -42.46) * mm});
            skLineSegment(sketch, "E1330", {"start": v(-133.25, -42.46) * mm, "end": v(-134.82, -42.46) * mm});
            skArc(sketch, "E1331", {"start": v(-373.17, -21.51) * mm, "mid": v(-373.35, -21.33) * mm, "end": v(-373.6, -21.26) * mm});
            skArc(sketch, "E1332", {"start": v(-373.17, -21.51) * mm, "mid": v(-372.38, -21.62) * mm, "end": v(-372.49, -20.83) * mm});
            skArc(sketch, "E1333", {"start": v(-372.74, -20.4) * mm, "mid": v(-372.67, -20.65) * mm, "end": v(-372.49, -20.83) * mm});
            skLineSegment(sketch, "E1334", {"start": v(-372.74, -20.4) * mm, "end": v(-372.74, -15.93) * mm});
            skArc(sketch, "E1335", {"start": v(-372.49, -15.5) * mm, "mid": v(-372.67, -15.68) * mm, "end": v(-372.74, -15.93) * mm});
            skArc(sketch, "E1336", {"start": v(-372.49, -15.5) * mm, "mid": v(-372.38, -14.71) * mm, "end": v(-373.17, -14.81) * mm});
            skArc(sketch, "E1337", {"start": v(-373.6, -15.06) * mm, "mid": v(-373.35, -15) * mm, "end": v(-373.17, -14.81) * mm});
            skLineSegment(sketch, "E1338", {"start": v(-373.6, -15.06) * mm, "end": v(-375.17, -15.06) * mm});
            skArc(sketch, "E1339", {"start": v(-375.6, -14.81) * mm, "mid": v(-375.42, -15) * mm, "end": v(-375.17, -15.06) * mm});
            skArc(sketch, "E1340", {"start": v(-375.6, -14.81) * mm, "mid": v(-376.4, -14.71) * mm, "end": v(-376.29, -15.5) * mm});
            skArc(sketch, "E1341", {"start": v(-376.04, -15.93) * mm, "mid": v(-376.1, -15.68) * mm, "end": v(-376.29, -15.5) * mm});
            skLineSegment(sketch, "E1342", {"start": v(-376.04, -15.93) * mm, "end": v(-376.04, -20.4) * mm});
            skArc(sketch, "E1343", {"start": v(-376.29, -20.83) * mm, "mid": v(-376.1, -20.65) * mm, "end": v(-376.04, -20.4) * mm});
            skArc(sketch, "E1344", {"start": v(-376.29, -20.83) * mm, "mid": v(-376.4, -21.62) * mm, "end": v(-375.6, -21.51) * mm});
            skArc(sketch, "E1345", {"start": v(-375.17, -21.26) * mm, "mid": v(-375.42, -21.33) * mm, "end": v(-375.6, -21.51) * mm});
            skLineSegment(sketch, "E1346", {"start": v(-375.17, -21.26) * mm, "end": v(-373.6, -21.26) * mm});
            skArc(sketch, "E1347", {"start": v(-373.17, -42.71) * mm, "mid": v(-373.35, -42.53) * mm, "end": v(-373.6, -42.46) * mm});
            skArc(sketch, "E1348", {"start": v(-373.17, -42.71) * mm, "mid": v(-372.38, -42.82) * mm, "end": v(-372.49, -42.03) * mm});
            skArc(sketch, "E1349", {"start": v(-372.74, -41.6) * mm, "mid": v(-372.67, -41.85) * mm, "end": v(-372.49, -42.03) * mm});
            skLineSegment(sketch, "E1350", {"start": v(-372.74, -41.6) * mm, "end": v(-372.74, -37.13) * mm});
            skArc(sketch, "E1351", {"start": v(-372.49, -36.7) * mm, "mid": v(-372.67, -36.88) * mm, "end": v(-372.74, -37.13) * mm});
            skArc(sketch, "E1352", {"start": v(-372.49, -36.7) * mm, "mid": v(-372.38, -35.91) * mm, "end": v(-373.17, -36.01) * mm});
            skArc(sketch, "E1353", {"start": v(-373.6, -36.26) * mm, "mid": v(-373.35, -36.2) * mm, "end": v(-373.17, -36.01) * mm});
            skLineSegment(sketch, "E1354", {"start": v(-373.6, -36.26) * mm, "end": v(-375.17, -36.26) * mm});
            skArc(sketch, "E1355", {"start": v(-375.6, -36.01) * mm, "mid": v(-375.42, -36.2) * mm, "end": v(-375.17, -36.26) * mm});
            skArc(sketch, "E1356", {"start": v(-375.6, -36.01) * mm, "mid": v(-376.4, -35.91) * mm, "end": v(-376.29, -36.7) * mm});
            skArc(sketch, "E1357", {"start": v(-376.04, -37.13) * mm, "mid": v(-376.1, -36.88) * mm, "end": v(-376.29, -36.7) * mm});
            skLineSegment(sketch, "E1358", {"start": v(-376.04, -37.13) * mm, "end": v(-376.04, -41.6) * mm});
            skArc(sketch, "E1359", {"start": v(-376.29, -42.03) * mm, "mid": v(-376.1, -41.85) * mm, "end": v(-376.04, -41.6) * mm});
            skArc(sketch, "E1360", {"start": v(-376.29, -42.03) * mm, "mid": v(-376.4, -42.82) * mm, "end": v(-375.6, -42.71) * mm});
            skArc(sketch, "E1361", {"start": v(-375.17, -42.46) * mm, "mid": v(-375.42, -42.53) * mm, "end": v(-375.6, -42.71) * mm});
            skLineSegment(sketch, "E1362", {"start": v(-375.17, -42.46) * mm, "end": v(-373.6, -42.46) * mm});
            skCircle(sketch, "E1363", {"center": v(-134.04, -28.76) * mm, "radius": 1.6 * mm});
            skCircle(sketch, "E1364", {"center": v(-188.21, -18.76) * mm, "radius": 1.6 * mm});
            skCircle(sketch, "E1365", {"center": v(-188.21, -38.76) * mm, "radius": 1.6 * mm});
            skCircle(sketch, "E1366", {"center": v(-219.21, -18.76) * mm, "radius": 1.6 * mm});
            skCircle(sketch, "E1367", {"center": v(-219.21, -38.76) * mm, "radius": 1.6 * mm});
            skCircle(sketch, "E1368", {"center": v(-289.21, -18.76) * mm, "radius": 1.6 * mm});
            skCircle(sketch, "E1369", {"center": v(-289.21, -38.76) * mm, "radius": 1.6 * mm});
            skCircle(sketch, "E1370", {"center": v(-320.21, -18.76) * mm, "radius": 1.6 * mm});
            skCircle(sketch, "E1371", {"center": v(-320.21, -38.76) * mm, "radius": 1.6 * mm});
            skCircle(sketch, "E1372", {"center": v(-374.39, -28.76) * mm, "radius": 1.6 * mm});
            skArc(sketch, "E1373", {"start": v(-357.6, -9.45) * mm, "mid": v(-357.24, -9.96) * mm, "end": v(-356.65, -10.15) * mm});
            skArc(sketch, "E1374", {"start": v(-359.17, -4.47) * mm, "mid": v(-359.53, -3.96) * mm, "end": v(-360.12, -3.76) * mm});
            skArc(sketch, "E1375", {"start": v(-151.77, -10.15) * mm, "mid": v(-151.18, -9.96) * mm, "end": v(-150.82, -9.45) * mm});
            skArc(sketch, "E1376", {"start": v(-148.3, -3.76) * mm, "mid": v(-148.9, -3.96) * mm, "end": v(-149.26, -4.47) * mm});
            skArc(sketch, "E1377", {"start": v(-172.9, -56.15) * mm, "mid": v(-172.45, -55.88) * mm, "end": v(-172.48, -55.37) * mm});
            skArc(sketch, "E1378", {"start": v(-165.94, -55.37) * mm, "mid": v(-165.97, -55.88) * mm, "end": v(-165.53, -56.15) * mm});
            skArc(sketch, "E1379", {"start": v(-349.21, -54.15) * mm, "mid": v(-348.63, -55.56) * mm, "end": v(-347.21, -56.15) * mm});
            skLineSegment(sketch, "E1380", {"start": v(-347.21, -56.15) * mm, "end": v(-342.9, -56.15) * mm});
            skLineSegment(sketch, "E1381", {"start": v(-335.53, -56.15) * mm, "end": v(-331.21, -56.15) * mm});
            skArc(sketch, "E1382", {"start": v(-331.21, -56.15) * mm, "mid": v(-329.8, -55.56) * mm, "end": v(-329.21, -54.15) * mm});
            skArc(sketch, "E1383", {"start": v(-342.9, -56.15) * mm, "mid": v(-342.46, -55.88) * mm, "end": v(-342.48, -55.37) * mm});
            skArc(sketch, "E1384", {"start": v(-335.94, -55.37) * mm, "mid": v(-335.97, -55.88) * mm, "end": v(-335.53, -56.15) * mm});
            skLineSegment(sketch, "E1385", {"start": v(-329.21, -54.15) * mm, "end": v(-329.21, -48.65) * mm});
            skArc(sketch, "E1386", {"start": v(-335.94, -55.37) * mm, "mid": v(-339.21, -49.2) * mm, "end": v(-342.48, -55.37) * mm});
            skLineSegment(sketch, "E1387", {"start": v(-349.21, -48.65) * mm, "end": v(-349.21, -54.15) * mm});
            skLineSegment(sketch, "E1388", {"start": v(-151.77, 46.42) * mm, "end": v(-356.65, 46.42) * mm});
            skLineSegment(sketch, "E1389", {"start": v(-357.6, 47.12) * mm, "end": v(-359.17, 52.1) * mm});
            skLineSegment(sketch, "E1390", {"start": v(-360.12, 52.8) * mm, "end": v(-379.39, 52.8) * mm});
            skArc(sketch, "E1391", {"start": v(-379.39, 52.8) * mm, "mid": v(-382.92, 51.35) * mm, "end": v(-384.39, 47.8) * mm});
            skLineSegment(sketch, "E1392", {"start": v(-384.39, 47.8) * mm, "end": v(-384.39, 13.42) * mm});
            skArc(sketch, "E1393", {"start": v(-384.39, 13.42) * mm, "mid": v(-382.92, 9.89) * mm, "end": v(-379.39, 8.42) * mm});
            skLineSegment(sketch, "E1394", {"start": v(-379.39, 8.42) * mm, "end": v(-349.71, 8.42) * mm});
            skArc(sketch, "E1395", {"start": v(-349.21, 7.92) * mm, "mid": v(-349.36, 8.28) * mm, "end": v(-349.71, 8.42) * mm});
            skArc(sketch, "E1396", {"start": v(-328.71, 8.42) * mm, "mid": v(-329.07, 8.28) * mm, "end": v(-329.21, 7.92) * mm});
            skLineSegment(sketch, "E1397", {"start": v(-328.71, 8.42) * mm, "end": v(-179.7, 8.42) * mm});
            skArc(sketch, "E1398", {"start": v(-179.2, 7.92) * mm, "mid": v(-179.36, 8.28) * mm, "end": v(-179.7, 8.42) * mm});
            skLineSegment(sketch, "E1399", {"start": v(-179.2, 7.92) * mm, "end": v(-179.2, 2.42) * mm});
            skArc(sketch, "E1400", {"start": v(-179.2, 2.42) * mm, "mid": v(-178.62, 1) * mm, "end": v(-177.2, 0.42) * mm});
            skLineSegment(sketch, "E1401", {"start": v(-177.2, 0.42) * mm, "end": v(-172.9, 0.42) * mm});
            skArc(sketch, "E1402", {"start": v(-165.94, 1.2) * mm, "mid": v(-169.2, 7.37) * mm, "end": v(-172.48, 1.2) * mm});
            skLineSegment(sketch, "E1403", {"start": v(-165.53, 0.42) * mm, "end": v(-161.2, 0.42) * mm});
            skArc(sketch, "E1404", {"start": v(-161.2, 0.42) * mm, "mid": v(-159.8, 1) * mm, "end": v(-159.2, 2.42) * mm});
            skLineSegment(sketch, "E1405", {"start": v(-159.2, 2.42) * mm, "end": v(-159.2, 7.92) * mm});
            skArc(sketch, "E1406", {"start": v(-158.7, 8.42) * mm, "mid": v(-159.06, 8.28) * mm, "end": v(-159.2, 7.92) * mm});
            skLineSegment(sketch, "E1407", {"start": v(-158.7, 8.42) * mm, "end": v(-129.04, 8.42) * mm});
            skArc(sketch, "E1408", {"start": v(-129.04, 8.42) * mm, "mid": v(-125.5, 9.89) * mm, "end": v(-124.04, 13.42) * mm});
            skLineSegment(sketch, "E1409", {"start": v(-124.04, 13.42) * mm, "end": v(-124.04, 47.8) * mm});
            skArc(sketch, "E1410", {"start": v(-124.04, 47.8) * mm, "mid": v(-125.5, 51.35) * mm, "end": v(-129.04, 52.8) * mm});
            skLineSegment(sketch, "E1411", {"start": v(-129.04, 52.8) * mm, "end": v(-148.3, 52.8) * mm});
            skLineSegment(sketch, "E1412", {"start": v(-149.26, 52.1) * mm, "end": v(-150.82, 47.12) * mm});
            skArc(sketch, "E1413", {"start": v(-134.82, 35.3) * mm, "mid": v(-135.07, 35.24) * mm, "end": v(-135.25, 35.06) * mm});
            skArc(sketch, "E1414", {"start": v(-135.94, 35.74) * mm, "mid": v(-136.04, 34.96) * mm, "end": v(-135.25, 35.06) * mm});
            skArc(sketch, "E1415", {"start": v(-135.94, 35.74) * mm, "mid": v(-135.75, 35.93) * mm, "end": v(-135.69, 36.18) * mm});
            skLineSegment(sketch, "E1416", {"start": v(-135.69, 36.18) * mm, "end": v(-135.69, 40.64) * mm});
            skArc(sketch, "E1417", {"start": v(-135.69, 40.64) * mm, "mid": v(-135.75, 40.9) * mm, "end": v(-135.94, 41.08) * mm});
            skArc(sketch, "E1418", {"start": v(-135.25, 41.76) * mm, "mid": v(-136.04, 41.86) * mm, "end": v(-135.94, 41.08) * mm});
            skArc(sketch, "E1419", {"start": v(-135.25, 41.76) * mm, "mid": v(-135.07, 41.58) * mm, "end": v(-134.82, 41.5) * mm});
            skLineSegment(sketch, "E1420", {"start": v(-134.82, 41.5) * mm, "end": v(-133.25, 41.5) * mm});
            skArc(sketch, "E1421", {"start": v(-133.25, 41.5) * mm, "mid": v(-133, 41.58) * mm, "end": v(-132.82, 41.76) * mm});
            skArc(sketch, "E1422", {"start": v(-132.14, 41.08) * mm, "mid": v(-132.03, 41.86) * mm, "end": v(-132.82, 41.76) * mm});
            skArc(sketch, "E1423", {"start": v(-132.14, 41.08) * mm, "mid": v(-132.32, 40.9) * mm, "end": v(-132.39, 40.64) * mm});
            skLineSegment(sketch, "E1424", {"start": v(-132.39, 40.64) * mm, "end": v(-132.39, 36.18) * mm});
            skArc(sketch, "E1425", {"start": v(-132.39, 36.18) * mm, "mid": v(-132.32, 35.93) * mm, "end": v(-132.14, 35.74) * mm});
            skArc(sketch, "E1426", {"start": v(-132.82, 35.06) * mm, "mid": v(-132.03, 34.96) * mm, "end": v(-132.14, 35.74) * mm});
            skArc(sketch, "E1427", {"start": v(-132.82, 35.06) * mm, "mid": v(-133, 35.24) * mm, "end": v(-133.25, 35.3) * mm});
            skLineSegment(sketch, "E1428", {"start": v(-133.25, 35.3) * mm, "end": v(-134.82, 35.3) * mm});
            skArc(sketch, "E1429", {"start": v(-134.82, 14.1) * mm, "mid": v(-135.07, 14.04) * mm, "end": v(-135.25, 13.86) * mm});
            skArc(sketch, "E1430", {"start": v(-135.94, 14.54) * mm, "mid": v(-136.04, 13.76) * mm, "end": v(-135.25, 13.86) * mm});
            skArc(sketch, "E1431", {"start": v(-135.94, 14.54) * mm, "mid": v(-135.75, 14.73) * mm, "end": v(-135.69, 14.98) * mm});
            skLineSegment(sketch, "E1432", {"start": v(-135.69, 14.98) * mm, "end": v(-135.69, 19.44) * mm});
            skArc(sketch, "E1433", {"start": v(-135.69, 19.44) * mm, "mid": v(-135.75, 19.7) * mm, "end": v(-135.94, 19.88) * mm});
            skArc(sketch, "E1434", {"start": v(-135.25, 20.56) * mm, "mid": v(-136.04, 20.66) * mm, "end": v(-135.94, 19.88) * mm});
            skArc(sketch, "E1435", {"start": v(-135.25, 20.56) * mm, "mid": v(-135.07, 20.38) * mm, "end": v(-134.82, 20.3) * mm});
            skLineSegment(sketch, "E1436", {"start": v(-134.82, 20.3) * mm, "end": v(-133.25, 20.3) * mm});
            skArc(sketch, "E1437", {"start": v(-133.25, 20.3) * mm, "mid": v(-133, 20.38) * mm, "end": v(-132.82, 20.56) * mm});
            skArc(sketch, "E1438", {"start": v(-132.14, 19.88) * mm, "mid": v(-132.03, 20.66) * mm, "end": v(-132.82, 20.56) * mm});
            skArc(sketch, "E1439", {"start": v(-132.14, 19.88) * mm, "mid": v(-132.32, 19.7) * mm, "end": v(-132.39, 19.44) * mm});
            skLineSegment(sketch, "E1440", {"start": v(-132.39, 19.44) * mm, "end": v(-132.39, 14.98) * mm});
            skArc(sketch, "E1441", {"start": v(-132.39, 14.98) * mm, "mid": v(-132.32, 14.73) * mm, "end": v(-132.14, 14.54) * mm});
            skArc(sketch, "E1442", {"start": v(-132.82, 13.86) * mm, "mid": v(-132.03, 13.76) * mm, "end": v(-132.14, 14.54) * mm});
            skArc(sketch, "E1443", {"start": v(-132.82, 13.86) * mm, "mid": v(-133, 14.04) * mm, "end": v(-133.25, 14.1) * mm});
            skLineSegment(sketch, "E1444", {"start": v(-133.25, 14.1) * mm, "end": v(-134.82, 14.1) * mm});
            skArc(sketch, "E1445", {"start": v(-260.55, 34.92) * mm, "mid": v(-260.8, 34.85) * mm, "end": v(-260.98, 34.67) * mm});
            skArc(sketch, "E1446", {"start": v(-261.66, 35.35) * mm, "mid": v(-261.77, 34.57) * mm, "end": v(-260.98, 34.67) * mm});
            skArc(sketch, "E1447", {"start": v(-261.66, 35.35) * mm, "mid": v(-261.48, 35.54) * mm, "end": v(-261.41, 35.79) * mm});
            skLineSegment(sketch, "E1448", {"start": v(-261.41, 35.79) * mm, "end": v(-261.41, 40.26) * mm});
            skArc(sketch, "E1449", {"start": v(-261.41, 40.26) * mm, "mid": v(-261.48, 40.5) * mm, "end": v(-261.66, 40.69) * mm});
            skArc(sketch, "E1450", {"start": v(-260.98, 41.37) * mm, "mid": v(-261.77, 41.48) * mm, "end": v(-261.66, 40.69) * mm});
            skArc(sketch, "E1451", {"start": v(-260.98, 41.37) * mm, "mid": v(-260.8, 41.19) * mm, "end": v(-260.55, 41.12) * mm});
            skLineSegment(sketch, "E1452", {"start": v(-260.55, 41.12) * mm, "end": v(-258.98, 41.12) * mm});
            skArc(sketch, "E1453", {"start": v(-258.98, 41.12) * mm, "mid": v(-258.73, 41.19) * mm, "end": v(-258.55, 41.37) * mm});
            skArc(sketch, "E1454", {"start": v(-257.86, 40.69) * mm, "mid": v(-257.76, 41.48) * mm, "end": v(-258.55, 41.37) * mm});
            skArc(sketch, "E1455", {"start": v(-257.86, 40.69) * mm, "mid": v(-258.05, 40.5) * mm, "end": v(-258.11, 40.26) * mm});
            skLineSegment(sketch, "E1456", {"start": v(-258.11, 40.26) * mm, "end": v(-258.11, 35.79) * mm});
            skArc(sketch, "E1457", {"start": v(-258.11, 35.79) * mm, "mid": v(-258.05, 35.54) * mm, "end": v(-257.86, 35.35) * mm});
            skArc(sketch, "E1458", {"start": v(-258.55, 34.67) * mm, "mid": v(-257.76, 34.57) * mm, "end": v(-257.86, 35.35) * mm});
            skArc(sketch, "E1459", {"start": v(-258.55, 34.67) * mm, "mid": v(-258.73, 34.85) * mm, "end": v(-258.98, 34.92) * mm});
            skLineSegment(sketch, "E1460", {"start": v(-258.98, 34.92) * mm, "end": v(-260.55, 34.92) * mm});
            skArc(sketch, "E1461", {"start": v(-260.55, 13.72) * mm, "mid": v(-260.8, 13.65) * mm, "end": v(-260.98, 13.47) * mm});
            skArc(sketch, "E1462", {"start": v(-261.66, 14.15) * mm, "mid": v(-261.77, 13.37) * mm, "end": v(-260.98, 13.47) * mm});
            skArc(sketch, "E1463", {"start": v(-261.66, 14.15) * mm, "mid": v(-261.48, 14.34) * mm, "end": v(-261.41, 14.59) * mm});
            skLineSegment(sketch, "E1464", {"start": v(-261.41, 14.59) * mm, "end": v(-261.41, 19.06) * mm});
            skArc(sketch, "E1465", {"start": v(-261.41, 19.06) * mm, "mid": v(-261.48, 19.3) * mm, "end": v(-261.66, 19.49) * mm});
            skArc(sketch, "E1466", {"start": v(-260.98, 20.17) * mm, "mid": v(-261.77, 20.28) * mm, "end": v(-261.66, 19.49) * mm});
            skArc(sketch, "E1467", {"start": v(-260.98, 20.17) * mm, "mid": v(-260.8, 19.99) * mm, "end": v(-260.55, 19.92) * mm});
            skLineSegment(sketch, "E1468", {"start": v(-260.55, 19.92) * mm, "end": v(-258.98, 19.92) * mm});
            skArc(sketch, "E1469", {"start": v(-258.98, 19.92) * mm, "mid": v(-258.73, 19.99) * mm, "end": v(-258.55, 20.17) * mm});
            skArc(sketch, "E1470", {"start": v(-257.86, 19.49) * mm, "mid": v(-257.76, 20.28) * mm, "end": v(-258.55, 20.17) * mm});
            skArc(sketch, "E1471", {"start": v(-257.86, 19.49) * mm, "mid": v(-258.05, 19.3) * mm, "end": v(-258.11, 19.06) * mm});
            skLineSegment(sketch, "E1472", {"start": v(-258.11, 19.06) * mm, "end": v(-258.11, 14.59) * mm});
            skArc(sketch, "E1473", {"start": v(-258.11, 14.59) * mm, "mid": v(-258.05, 14.34) * mm, "end": v(-257.86, 14.15) * mm});
            skArc(sketch, "E1474", {"start": v(-258.55, 13.47) * mm, "mid": v(-257.76, 13.37) * mm, "end": v(-257.86, 14.15) * mm});
            skArc(sketch, "E1475", {"start": v(-258.55, 13.47) * mm, "mid": v(-258.73, 13.65) * mm, "end": v(-258.98, 13.72) * mm});
            skLineSegment(sketch, "E1476", {"start": v(-258.98, 13.72) * mm, "end": v(-260.55, 13.72) * mm});
            skArc(sketch, "E1477", {"start": v(-373.17, 35.06) * mm, "mid": v(-373.35, 35.24) * mm, "end": v(-373.6, 35.3) * mm});
            skArc(sketch, "E1478", {"start": v(-373.17, 35.06) * mm, "mid": v(-372.38, 34.96) * mm, "end": v(-372.49, 35.74) * mm});
            skArc(sketch, "E1479", {"start": v(-372.74, 36.18) * mm, "mid": v(-372.67, 35.93) * mm, "end": v(-372.49, 35.74) * mm});
            skLineSegment(sketch, "E1480", {"start": v(-372.74, 36.18) * mm, "end": v(-372.74, 40.64) * mm});
            skArc(sketch, "E1481", {"start": v(-372.49, 41.08) * mm, "mid": v(-372.67, 40.9) * mm, "end": v(-372.74, 40.64) * mm});
            skArc(sketch, "E1482", {"start": v(-372.49, 41.08) * mm, "mid": v(-372.38, 41.86) * mm, "end": v(-373.17, 41.76) * mm});
            skArc(sketch, "E1483", {"start": v(-373.6, 41.5) * mm, "mid": v(-373.35, 41.58) * mm, "end": v(-373.17, 41.76) * mm});
            skLineSegment(sketch, "E1484", {"start": v(-373.6, 41.5) * mm, "end": v(-375.17, 41.5) * mm});
            skArc(sketch, "E1485", {"start": v(-375.6, 41.76) * mm, "mid": v(-375.42, 41.58) * mm, "end": v(-375.17, 41.5) * mm});
            skArc(sketch, "E1486", {"start": v(-375.6, 41.76) * mm, "mid": v(-376.4, 41.86) * mm, "end": v(-376.29, 41.08) * mm});
            skArc(sketch, "E1487", {"start": v(-376.04, 40.64) * mm, "mid": v(-376.1, 40.9) * mm, "end": v(-376.29, 41.08) * mm});
            skLineSegment(sketch, "E1488", {"start": v(-376.04, 40.64) * mm, "end": v(-376.04, 36.18) * mm});
            skArc(sketch, "E1489", {"start": v(-376.29, 35.74) * mm, "mid": v(-376.1, 35.93) * mm, "end": v(-376.04, 36.18) * mm});
            skArc(sketch, "E1490", {"start": v(-376.29, 35.74) * mm, "mid": v(-376.4, 34.96) * mm, "end": v(-375.6, 35.06) * mm});
            skArc(sketch, "E1491", {"start": v(-375.17, 35.3) * mm, "mid": v(-375.42, 35.24) * mm, "end": v(-375.6, 35.06) * mm});
            skLineSegment(sketch, "E1492", {"start": v(-375.17, 35.3) * mm, "end": v(-373.6, 35.3) * mm});
            skArc(sketch, "E1493", {"start": v(-373.17, 13.86) * mm, "mid": v(-373.35, 14.04) * mm, "end": v(-373.6, 14.1) * mm});
            skArc(sketch, "E1494", {"start": v(-373.17, 13.86) * mm, "mid": v(-372.38, 13.76) * mm, "end": v(-372.49, 14.54) * mm});
            skArc(sketch, "E1495", {"start": v(-372.74, 14.98) * mm, "mid": v(-372.67, 14.73) * mm, "end": v(-372.49, 14.54) * mm});
            skLineSegment(sketch, "E1496", {"start": v(-372.74, 14.98) * mm, "end": v(-372.74, 19.44) * mm});
            skArc(sketch, "E1497", {"start": v(-372.49, 19.88) * mm, "mid": v(-372.67, 19.7) * mm, "end": v(-372.74, 19.44) * mm});
            skArc(sketch, "E1498", {"start": v(-372.49, 19.88) * mm, "mid": v(-372.38, 20.66) * mm, "end": v(-373.17, 20.56) * mm});
            skArc(sketch, "E1499", {"start": v(-373.6, 20.3) * mm, "mid": v(-373.35, 20.38) * mm, "end": v(-373.17, 20.56) * mm});
            skLineSegment(sketch, "E1500", {"start": v(-373.6, 20.3) * mm, "end": v(-375.17, 20.3) * mm});
            skArc(sketch, "E1501", {"start": v(-375.6, 20.56) * mm, "mid": v(-375.42, 20.38) * mm, "end": v(-375.17, 20.3) * mm});
            skArc(sketch, "E1502", {"start": v(-375.6, 20.56) * mm, "mid": v(-376.4, 20.66) * mm, "end": v(-376.29, 19.88) * mm});
            skArc(sketch, "E1503", {"start": v(-376.04, 19.44) * mm, "mid": v(-376.1, 19.7) * mm, "end": v(-376.29, 19.88) * mm});
            skLineSegment(sketch, "E1504", {"start": v(-376.04, 19.44) * mm, "end": v(-376.04, 14.98) * mm});
            skArc(sketch, "E1505", {"start": v(-376.29, 14.54) * mm, "mid": v(-376.1, 14.73) * mm, "end": v(-376.04, 14.98) * mm});
            skArc(sketch, "E1506", {"start": v(-376.29, 14.54) * mm, "mid": v(-376.4, 13.76) * mm, "end": v(-375.6, 13.86) * mm});
            skArc(sketch, "E1507", {"start": v(-375.17, 14.1) * mm, "mid": v(-375.42, 14.04) * mm, "end": v(-375.6, 13.86) * mm});
            skLineSegment(sketch, "E1508", {"start": v(-375.17, 14.1) * mm, "end": v(-373.6, 14.1) * mm});
            skCircle(sketch, "E1509", {"center": v(-134.04, 27.8) * mm, "radius": 1.6 * mm});
            skCircle(sketch, "E1510", {"center": v(-188.21, 37.8) * mm, "radius": 1.6 * mm});
            skCircle(sketch, "E1511", {"center": v(-188.21, 17.8) * mm, "radius": 1.6 * mm});
            skCircle(sketch, "E1512", {"center": v(-219.21, 37.8) * mm, "radius": 1.6 * mm});
            skCircle(sketch, "E1513", {"center": v(-219.21, 17.8) * mm, "radius": 1.6 * mm});
            skCircle(sketch, "E1514", {"center": v(-259.76, 27.42) * mm, "radius": 1.6 * mm});
            skCircle(sketch, "E1515", {"center": v(-289.21, 37.8) * mm, "radius": 1.6 * mm});
            skCircle(sketch, "E1516", {"center": v(-289.21, 17.8) * mm, "radius": 1.6 * mm});
            skCircle(sketch, "E1517", {"center": v(-320.21, 37.8) * mm, "radius": 1.6 * mm});
            skCircle(sketch, "E1518", {"center": v(-320.21, 17.8) * mm, "radius": 1.6 * mm});
            skCircle(sketch, "E1519", {"center": v(-374.39, 27.8) * mm, "radius": 1.6 * mm});
            skArc(sketch, "E1520", {"start": v(-357.6, 47.12) * mm, "mid": v(-357.24, 46.62) * mm, "end": v(-356.65, 46.42) * mm});
            skArc(sketch, "E1521", {"start": v(-359.17, 52.1) * mm, "mid": v(-359.53, 52.62) * mm, "end": v(-360.12, 52.8) * mm});
            skArc(sketch, "E1522", {"start": v(-151.77, 46.42) * mm, "mid": v(-151.18, 46.62) * mm, "end": v(-150.82, 47.12) * mm});
            skArc(sketch, "E1523", {"start": v(-148.3, 52.8) * mm, "mid": v(-148.9, 52.62) * mm, "end": v(-149.26, 52.1) * mm});
            skArc(sketch, "E1524", {"start": v(-172.9, 0.42) * mm, "mid": v(-172.45, 0.69) * mm, "end": v(-172.48, 1.2) * mm});
            skArc(sketch, "E1525", {"start": v(-165.94, 1.2) * mm, "mid": v(-165.97, 0.69) * mm, "end": v(-165.53, 0.42) * mm});
            skArc(sketch, "E1526", {"start": v(-349.21, 2.42) * mm, "mid": v(-348.63, 1) * mm, "end": v(-347.21, 0.42) * mm});
            skLineSegment(sketch, "E1527", {"start": v(-347.21, 0.42) * mm, "end": v(-342.9, 0.42) * mm});
            skLineSegment(sketch, "E1528", {"start": v(-335.53, 0.42) * mm, "end": v(-331.21, 0.42) * mm});
            skArc(sketch, "E1529", {"start": v(-331.21, 0.42) * mm, "mid": v(-329.8, 1) * mm, "end": v(-329.21, 2.42) * mm});
            skArc(sketch, "E1530", {"start": v(-342.9, 0.42) * mm, "mid": v(-342.46, 0.69) * mm, "end": v(-342.48, 1.2) * mm});
            skArc(sketch, "E1531", {"start": v(-335.94, 1.2) * mm, "mid": v(-335.97, 0.69) * mm, "end": v(-335.53, 0.42) * mm});
            skLineSegment(sketch, "E1532", {"start": v(-329.21, 2.42) * mm, "end": v(-329.21, 7.92) * mm});
            skArc(sketch, "E1533", {"start": v(-335.94, 1.2) * mm, "mid": v(-339.21, 7.37) * mm, "end": v(-342.48, 1.2) * mm});
            skLineSegment(sketch, "E1534", {"start": v(-349.21, 7.92) * mm, "end": v(-349.21, 2.42) * mm});
            skLineSegment(sketch, "E1535", {"start": v(-57.63, 54.65) * mm, "end": v(-57.63, 9.65) * mm});
            skArc(sketch, "E1536", {"start": v(-62.63, 4.65) * mm, "mid": v(-59.1, 6.11) * mm, "end": v(-57.63, 9.65) * mm});
            skLineSegment(sketch, "E1537", {"start": v(-62.63, 4.65) * mm, "end": v(-112.63, 4.65) * mm});
            skArc(sketch, "E1538", {"start": v(-117.63, 9.65) * mm, "mid": v(-116.17, 6.11) * mm, "end": v(-112.63, 4.65) * mm});
            skLineSegment(sketch, "E1539", {"start": v(-117.63, 9.65) * mm, "end": v(-117.63, 54.65) * mm});
            skLineSegment(sketch, "E1540", {"start": v(-117.63, 54.65) * mm, "end": v(-102.1, 54.65) * mm});
            skArc(sketch, "E1541", {"start": v(-101.66, 54.4) * mm, "mid": v(-101.85, 54.58) * mm, "end": v(-102.1, 54.65) * mm});
            skArc(sketch, "E1542", {"start": v(-101.66, 54.4) * mm, "mid": v(-100.88, 54.3) * mm, "end": v(-100.98, 55.08) * mm});
            skArc(sketch, "E1543", {"start": v(-101.23, 55.51) * mm, "mid": v(-101.16, 55.26) * mm, "end": v(-100.98, 55.08) * mm});
            skLineSegment(sketch, "E1544", {"start": v(-101.23, 55.51) * mm, "end": v(-101.23, 57.15) * mm});
            skArc(sketch, "E1545", {"start": v(-100.73, 57.65) * mm, "mid": v(-101.08, 57.5) * mm, "end": v(-101.23, 57.15) * mm});
            skLineSegment(sketch, "E1546", {"start": v(-100.73, 57.65) * mm, "end": v(-95.73, 57.65) * mm});
            skArc(sketch, "E1547", {"start": v(-95.23, 57.15) * mm, "mid": v(-95.38, 57.5) * mm, "end": v(-95.73, 57.65) * mm});
            skLineSegment(sketch, "E1548", {"start": v(-95.23, 57.15) * mm, "end": v(-95.23, 55.51) * mm});
            skArc(sketch, "E1549", {"start": v(-95.48, 55.08) * mm, "mid": v(-95.3, 55.26) * mm, "end": v(-95.23, 55.51) * mm});
            skArc(sketch, "E1550", {"start": v(-95.48, 55.08) * mm, "mid": v(-95.58, 54.3) * mm, "end": v(-94.8, 54.4) * mm});
            skArc(sketch, "E1551", {"start": v(-94.36, 54.65) * mm, "mid": v(-94.61, 54.58) * mm, "end": v(-94.8, 54.4) * mm});
            skLineSegment(sketch, "E1552", {"start": v(-94.36, 54.65) * mm, "end": v(-89.23, 54.65) * mm});
            skLineSegment(sketch, "E1553", {"start": v(-89.23, 54.65) * mm, "end": v(-89.23, 51.65) * mm});
            skLineSegment(sketch, "E1554", {"start": v(-89.23, 51.65) * mm, "end": v(-90.5, 51.65) * mm});
            skLineSegment(sketch, "E1555", {"start": v(-90.5, 51.65) * mm, "end": v(-90.5, 47.65) * mm});
            skLineSegment(sketch, "E1556", {"start": v(-90.5, 47.65) * mm, "end": v(-89.23, 47.65) * mm});
            skLineSegment(sketch, "E1557", {"start": v(-89.23, 47.65) * mm, "end": v(-89.23, 44.65) * mm});
            skLineSegment(sketch, "E1558", {"start": v(-89.23, 44.65) * mm, "end": v(-86.03, 44.65) * mm});
            skLineSegment(sketch, "E1559", {"start": v(-86.03, 44.65) * mm, "end": v(-86.03, 47.65) * mm});
            skLineSegment(sketch, "E1560", {"start": v(-86.03, 47.65) * mm, "end": v(-84.76, 47.65) * mm});
            skLineSegment(sketch, "E1561", {"start": v(-84.76, 47.65) * mm, "end": v(-84.76, 51.65) * mm});
            skLineSegment(sketch, "E1562", {"start": v(-84.76, 51.65) * mm, "end": v(-86.03, 51.65) * mm});
            skLineSegment(sketch, "E1563", {"start": v(-86.03, 51.65) * mm, "end": v(-86.03, 54.65) * mm});
            skLineSegment(sketch, "E1564", {"start": v(-86.03, 54.65) * mm, "end": v(-80.9, 54.65) * mm});
            skArc(sketch, "E1565", {"start": v(-80.46, 54.4) * mm, "mid": v(-80.65, 54.58) * mm, "end": v(-80.9, 54.65) * mm});
            skArc(sketch, "E1566", {"start": v(-80.46, 54.4) * mm, "mid": v(-79.68, 54.3) * mm, "end": v(-79.78, 55.08) * mm});
            skArc(sketch, "E1567", {"start": v(-80.03, 55.51) * mm, "mid": v(-79.96, 55.26) * mm, "end": v(-79.78, 55.08) * mm});
            skLineSegment(sketch, "E1568", {"start": v(-80.03, 55.51) * mm, "end": v(-80.03, 57.15) * mm});
            skArc(sketch, "E1569", {"start": v(-79.53, 57.65) * mm, "mid": v(-79.88, 57.5) * mm, "end": v(-80.03, 57.15) * mm});
            skLineSegment(sketch, "E1570", {"start": v(-79.53, 57.65) * mm, "end": v(-74.53, 57.65) * mm});
            skArc(sketch, "E1571", {"start": v(-74.03, 57.15) * mm, "mid": v(-74.18, 57.5) * mm, "end": v(-74.53, 57.65) * mm});
            skLineSegment(sketch, "E1572", {"start": v(-74.03, 57.15) * mm, "end": v(-74.03, 55.51) * mm});
            skArc(sketch, "E1573", {"start": v(-74.28, 55.08) * mm, "mid": v(-74.1, 55.26) * mm, "end": v(-74.03, 55.51) * mm});
            skArc(sketch, "E1574", {"start": v(-74.28, 55.08) * mm, "mid": v(-74.38, 54.3) * mm, "end": v(-73.6, 54.4) * mm});
            skArc(sketch, "E1575", {"start": v(-73.16, 54.65) * mm, "mid": v(-73.41, 54.58) * mm, "end": v(-73.6, 54.4) * mm});
            skLineSegment(sketch, "E1576", {"start": v(-73.16, 54.65) * mm, "end": v(-57.63, 54.65) * mm});
            skCircle(sketch, "E1577", {"center": v(-87.63, 25.35) * mm, "radius": 11.1 * mm});
            skCircle(sketch, "E1578", {"center": v(-70.63, 25.35) * mm, "radius": 4 * mm});
            skArc(sketch, "E1579", {"start": v(-63.9, 37.15) * mm, "mid": v(-64.14, 37.08) * mm, "end": v(-64.33, 36.9) * mm});
            skArc(sketch, "E1580", {"start": v(-65.01, 37.58) * mm, "mid": v(-65.11, 36.8) * mm, "end": v(-64.33, 36.9) * mm});
            skArc(sketch, "E1581", {"start": v(-65.01, 37.58) * mm, "mid": v(-64.83, 37.76) * mm, "end": v(-64.76, 38.01) * mm});
            skLineSegment(sketch, "E1582", {"start": v(-64.76, 38.01) * mm, "end": v(-64.76, 42.48) * mm});
            skArc(sketch, "E1583", {"start": v(-64.76, 42.48) * mm, "mid": v(-64.83, 42.73) * mm, "end": v(-65.01, 42.91) * mm});
            skArc(sketch, "E1584", {"start": v(-64.33, 43.6) * mm, "mid": v(-65.11, 43.7) * mm, "end": v(-65.01, 42.91) * mm});
            skArc(sketch, "E1585", {"start": v(-64.33, 43.6) * mm, "mid": v(-64.14, 43.41) * mm, "end": v(-63.9, 43.35) * mm});
            skLineSegment(sketch, "E1586", {"start": v(-63.9, 43.35) * mm, "end": v(-62.33, 43.35) * mm});
            skArc(sketch, "E1587", {"start": v(-62.33, 43.35) * mm, "mid": v(-62.08, 43.41) * mm, "end": v(-61.9, 43.6) * mm});
            skArc(sketch, "E1588", {"start": v(-61.21, 42.91) * mm, "mid": v(-61.1, 43.7) * mm, "end": v(-61.9, 43.6) * mm});
            skArc(sketch, "E1589", {"start": v(-61.21, 42.91) * mm, "mid": v(-61.4, 42.73) * mm, "end": v(-61.46, 42.48) * mm});
            skLineSegment(sketch, "E1590", {"start": v(-61.46, 42.48) * mm, "end": v(-61.46, 38.01) * mm});
            skArc(sketch, "E1591", {"start": v(-61.46, 38.01) * mm, "mid": v(-61.4, 37.76) * mm, "end": v(-61.21, 37.58) * mm});
            skArc(sketch, "E1592", {"start": v(-61.9, 36.9) * mm, "mid": v(-61.1, 36.8) * mm, "end": v(-61.21, 37.58) * mm});
            skArc(sketch, "E1593", {"start": v(-61.9, 36.9) * mm, "mid": v(-62.08, 37.08) * mm, "end": v(-62.33, 37.15) * mm});
            skLineSegment(sketch, "E1594", {"start": v(-62.33, 37.15) * mm, "end": v(-63.9, 37.15) * mm});
            skArc(sketch, "E1595", {"start": v(-63.9, 15.95) * mm, "mid": v(-64.14, 15.88) * mm, "end": v(-64.33, 15.7) * mm});
            skArc(sketch, "E1596", {"start": v(-65.01, 16.38) * mm, "mid": v(-65.11, 15.6) * mm, "end": v(-64.33, 15.7) * mm});
            skArc(sketch, "E1597", {"start": v(-65.01, 16.38) * mm, "mid": v(-64.83, 16.56) * mm, "end": v(-64.76, 16.81) * mm});
            skLineSegment(sketch, "E1598", {"start": v(-64.76, 16.81) * mm, "end": v(-64.76, 21.28) * mm});
            skArc(sketch, "E1599", {"start": v(-64.76, 21.28) * mm, "mid": v(-64.83, 21.53) * mm, "end": v(-65.01, 21.71) * mm});
            skArc(sketch, "E1600", {"start": v(-64.33, 22.4) * mm, "mid": v(-65.11, 22.5) * mm, "end": v(-65.01, 21.71) * mm});
            skArc(sketch, "E1601", {"start": v(-64.33, 22.4) * mm, "mid": v(-64.14, 22.21) * mm, "end": v(-63.9, 22.15) * mm});
            skLineSegment(sketch, "E1602", {"start": v(-63.9, 22.15) * mm, "end": v(-62.33, 22.15) * mm});
            skArc(sketch, "E1603", {"start": v(-62.33, 22.15) * mm, "mid": v(-62.08, 22.21) * mm, "end": v(-61.9, 22.4) * mm});
            skArc(sketch, "E1604", {"start": v(-61.21, 21.71) * mm, "mid": v(-61.1, 22.5) * mm, "end": v(-61.9, 22.4) * mm});
            skArc(sketch, "E1605", {"start": v(-61.21, 21.71) * mm, "mid": v(-61.4, 21.53) * mm, "end": v(-61.46, 21.28) * mm});
            skLineSegment(sketch, "E1606", {"start": v(-61.46, 21.28) * mm, "end": v(-61.46, 16.81) * mm});
            skArc(sketch, "E1607", {"start": v(-61.46, 16.81) * mm, "mid": v(-61.4, 16.56) * mm, "end": v(-61.21, 16.38) * mm});
            skArc(sketch, "E1608", {"start": v(-61.9, 15.7) * mm, "mid": v(-61.1, 15.6) * mm, "end": v(-61.21, 16.38) * mm});
            skArc(sketch, "E1609", {"start": v(-61.9, 15.7) * mm, "mid": v(-62.08, 15.88) * mm, "end": v(-62.33, 15.95) * mm});
            skLineSegment(sketch, "E1610", {"start": v(-62.33, 15.95) * mm, "end": v(-63.9, 15.95) * mm});
            skArc(sketch, "E1611", {"start": v(-112.93, 37.15) * mm, "mid": v(-113.18, 37.08) * mm, "end": v(-113.37, 36.9) * mm});
            skArc(sketch, "E1612", {"start": v(-114.05, 37.58) * mm, "mid": v(-114.15, 36.8) * mm, "end": v(-113.37, 36.9) * mm});
            skArc(sketch, "E1613", {"start": v(-114.05, 37.58) * mm, "mid": v(-113.87, 37.76) * mm, "end": v(-113.8, 38.01) * mm});
            skLineSegment(sketch, "E1614", {"start": v(-113.8, 38.01) * mm, "end": v(-113.8, 42.48) * mm});
            skArc(sketch, "E1615", {"start": v(-113.8, 42.48) * mm, "mid": v(-113.87, 42.73) * mm, "end": v(-114.05, 42.91) * mm});
            skArc(sketch, "E1616", {"start": v(-113.37, 43.6) * mm, "mid": v(-114.15, 43.7) * mm, "end": v(-114.05, 42.91) * mm});
            skArc(sketch, "E1617", {"start": v(-113.37, 43.6) * mm, "mid": v(-113.18, 43.41) * mm, "end": v(-112.93, 43.35) * mm});
            skLineSegment(sketch, "E1618", {"start": v(-112.93, 43.35) * mm, "end": v(-111.37, 43.35) * mm});
            skArc(sketch, "E1619", {"start": v(-111.37, 43.35) * mm, "mid": v(-111.12, 43.41) * mm, "end": v(-110.93, 43.6) * mm});
            skArc(sketch, "E1620", {"start": v(-110.25, 42.91) * mm, "mid": v(-110.15, 43.7) * mm, "end": v(-110.93, 43.6) * mm});
            skArc(sketch, "E1621", {"start": v(-110.25, 42.91) * mm, "mid": v(-110.43, 42.73) * mm, "end": v(-110.5, 42.48) * mm});
            skLineSegment(sketch, "E1622", {"start": v(-110.5, 42.48) * mm, "end": v(-110.5, 38.01) * mm});
            skArc(sketch, "E1623", {"start": v(-110.5, 38.01) * mm, "mid": v(-110.43, 37.76) * mm, "end": v(-110.25, 37.58) * mm});
            skArc(sketch, "E1624", {"start": v(-110.93, 36.9) * mm, "mid": v(-110.15, 36.8) * mm, "end": v(-110.25, 37.58) * mm});
            skArc(sketch, "E1625", {"start": v(-110.93, 36.9) * mm, "mid": v(-111.12, 37.08) * mm, "end": v(-111.37, 37.15) * mm});
            skLineSegment(sketch, "E1626", {"start": v(-111.37, 37.15) * mm, "end": v(-112.93, 37.15) * mm});
            skArc(sketch, "E1627", {"start": v(-112.93, 15.95) * mm, "mid": v(-113.18, 15.88) * mm, "end": v(-113.37, 15.7) * mm});
            skArc(sketch, "E1628", {"start": v(-114.05, 16.38) * mm, "mid": v(-114.15, 15.6) * mm, "end": v(-113.37, 15.7) * mm});
            skArc(sketch, "E1629", {"start": v(-114.05, 16.38) * mm, "mid": v(-113.87, 16.56) * mm, "end": v(-113.8, 16.81) * mm});
            skLineSegment(sketch, "E1630", {"start": v(-113.8, 16.81) * mm, "end": v(-113.8, 21.28) * mm});
            skArc(sketch, "E1631", {"start": v(-113.8, 21.28) * mm, "mid": v(-113.87, 21.53) * mm, "end": v(-114.05, 21.71) * mm});
            skArc(sketch, "E1632", {"start": v(-113.37, 22.4) * mm, "mid": v(-114.15, 22.5) * mm, "end": v(-114.05, 21.71) * mm});
            skArc(sketch, "E1633", {"start": v(-113.37, 22.4) * mm, "mid": v(-113.18, 22.21) * mm, "end": v(-112.93, 22.15) * mm});
            skLineSegment(sketch, "E1634", {"start": v(-112.93, 22.15) * mm, "end": v(-111.37, 22.15) * mm});
            skArc(sketch, "E1635", {"start": v(-111.37, 22.15) * mm, "mid": v(-111.12, 22.21) * mm, "end": v(-110.93, 22.4) * mm});
            skArc(sketch, "E1636", {"start": v(-110.25, 21.71) * mm, "mid": v(-110.15, 22.5) * mm, "end": v(-110.93, 22.4) * mm});
            skArc(sketch, "E1637", {"start": v(-110.25, 21.71) * mm, "mid": v(-110.43, 21.53) * mm, "end": v(-110.5, 21.28) * mm});
            skLineSegment(sketch, "E1638", {"start": v(-110.5, 21.28) * mm, "end": v(-110.5, 16.81) * mm});
            skArc(sketch, "E1639", {"start": v(-110.5, 16.81) * mm, "mid": v(-110.43, 16.56) * mm, "end": v(-110.25, 16.38) * mm});
            skArc(sketch, "E1640", {"start": v(-110.93, 15.7) * mm, "mid": v(-110.15, 15.6) * mm, "end": v(-110.25, 16.38) * mm});
            skArc(sketch, "E1641", {"start": v(-110.93, 15.7) * mm, "mid": v(-111.12, 15.88) * mm, "end": v(-111.37, 15.95) * mm});
            skLineSegment(sketch, "E1642", {"start": v(-111.37, 15.95) * mm, "end": v(-112.93, 15.95) * mm});
            skCircle(sketch, "E1643", {"center": v(-63.11, 29.65) * mm, "radius": 1.6 * mm});
            skCircle(sketch, "E1644", {"center": v(-72.13, 40.85) * mm, "radius": 1.6 * mm});
            skCircle(sketch, "E1645", {"center": v(-72.13, 9.85) * mm, "radius": 1.6 * mm});
            skCircle(sketch, "E1646", {"center": v(-103.13, 40.85) * mm, "radius": 1.6 * mm});
            skCircle(sketch, "E1647", {"center": v(-103.13, 9.85) * mm, "radius": 1.6 * mm});
            skCircle(sketch, "E1648", {"center": v(-112.15, 29.65) * mm, "radius": 1.6 * mm});
            skLineSegment(sketch, "E1649", {"start": v(-57.63, -3.16) * mm, "end": v(-57.63, -48.16) * mm});
            skArc(sketch, "E1650", {"start": v(-62.63, -53.16) * mm, "mid": v(-59.1, -51.7) * mm, "end": v(-57.63, -48.16) * mm});
            skLineSegment(sketch, "E1651", {"start": v(-62.63, -53.16) * mm, "end": v(-112.63, -53.16) * mm});
            skArc(sketch, "E1652", {"start": v(-117.63, -48.16) * mm, "mid": v(-116.17, -51.7) * mm, "end": v(-112.63, -53.16) * mm});
            skLineSegment(sketch, "E1653", {"start": v(-117.63, -48.16) * mm, "end": v(-117.63, -3.16) * mm});
            skLineSegment(sketch, "E1654", {"start": v(-117.63, -3.16) * mm, "end": v(-102.1, -3.16) * mm});
            skArc(sketch, "E1655", {"start": v(-101.66, -3.41) * mm, "mid": v(-101.85, -3.23) * mm, "end": v(-102.1, -3.16) * mm});
            skArc(sketch, "E1656", {"start": v(-101.66, -3.41) * mm, "mid": v(-100.88, -3.51) * mm, "end": v(-100.98, -2.73) * mm});
            skArc(sketch, "E1657", {"start": v(-101.23, -2.3) * mm, "mid": v(-101.16, -2.54) * mm, "end": v(-100.98, -2.73) * mm});
            skLineSegment(sketch, "E1658", {"start": v(-101.23, -2.3) * mm, "end": v(-101.23, -0.66) * mm});
            skArc(sketch, "E1659", {"start": v(-100.73, -0.16) * mm, "mid": v(-101.08, -0.3) * mm, "end": v(-101.23, -0.66) * mm});
            skLineSegment(sketch, "E1660", {"start": v(-100.73, -0.16) * mm, "end": v(-95.73, -0.16) * mm});
            skArc(sketch, "E1661", {"start": v(-95.23, -0.66) * mm, "mid": v(-95.38, -0.3) * mm, "end": v(-95.73, -0.16) * mm});
            skLineSegment(sketch, "E1662", {"start": v(-95.23, -0.66) * mm, "end": v(-95.23, -2.3) * mm});
            skArc(sketch, "E1663", {"start": v(-95.48, -2.73) * mm, "mid": v(-95.3, -2.54) * mm, "end": v(-95.23, -2.3) * mm});
            skArc(sketch, "E1664", {"start": v(-95.48, -2.73) * mm, "mid": v(-95.58, -3.51) * mm, "end": v(-94.8, -3.41) * mm});
            skArc(sketch, "E1665", {"start": v(-94.36, -3.16) * mm, "mid": v(-94.61, -3.23) * mm, "end": v(-94.8, -3.41) * mm});
            skLineSegment(sketch, "E1666", {"start": v(-94.36, -3.16) * mm, "end": v(-89.23, -3.16) * mm});
            skLineSegment(sketch, "E1667", {"start": v(-89.23, -3.16) * mm, "end": v(-89.23, -6.16) * mm});
            skLineSegment(sketch, "E1668", {"start": v(-89.23, -6.16) * mm, "end": v(-90.5, -6.16) * mm});
            skLineSegment(sketch, "E1669", {"start": v(-90.5, -6.16) * mm, "end": v(-90.5, -10.16) * mm});
            skLineSegment(sketch, "E1670", {"start": v(-90.5, -10.16) * mm, "end": v(-89.23, -10.16) * mm});
            skLineSegment(sketch, "E1671", {"start": v(-89.23, -10.16) * mm, "end": v(-89.23, -13.16) * mm});
            skLineSegment(sketch, "E1672", {"start": v(-89.23, -13.16) * mm, "end": v(-86.03, -13.16) * mm});
            skLineSegment(sketch, "E1673", {"start": v(-86.03, -13.16) * mm, "end": v(-86.03, -10.16) * mm});
            skLineSegment(sketch, "E1674", {"start": v(-86.03, -10.16) * mm, "end": v(-84.76, -10.16) * mm});
            skLineSegment(sketch, "E1675", {"start": v(-84.76, -10.16) * mm, "end": v(-84.76, -6.16) * mm});
            skLineSegment(sketch, "E1676", {"start": v(-84.76, -6.16) * mm, "end": v(-86.03, -6.16) * mm});
            skLineSegment(sketch, "E1677", {"start": v(-86.03, -6.16) * mm, "end": v(-86.03, -3.16) * mm});
            skLineSegment(sketch, "E1678", {"start": v(-86.03, -3.16) * mm, "end": v(-80.9, -3.16) * mm});
            skArc(sketch, "E1679", {"start": v(-80.46, -3.41) * mm, "mid": v(-80.65, -3.23) * mm, "end": v(-80.9, -3.16) * mm});
            skArc(sketch, "E1680", {"start": v(-80.46, -3.41) * mm, "mid": v(-79.68, -3.51) * mm, "end": v(-79.78, -2.73) * mm});
            skArc(sketch, "E1681", {"start": v(-80.03, -2.3) * mm, "mid": v(-79.96, -2.54) * mm, "end": v(-79.78, -2.73) * mm});
            skLineSegment(sketch, "E1682", {"start": v(-80.03, -2.3) * mm, "end": v(-80.03, -0.66) * mm});
            skArc(sketch, "E1683", {"start": v(-79.53, -0.16) * mm, "mid": v(-79.88, -0.3) * mm, "end": v(-80.03, -0.66) * mm});
            skLineSegment(sketch, "E1684", {"start": v(-79.53, -0.16) * mm, "end": v(-74.53, -0.16) * mm});
            skArc(sketch, "E1685", {"start": v(-74.03, -0.66) * mm, "mid": v(-74.18, -0.3) * mm, "end": v(-74.53, -0.16) * mm});
            skLineSegment(sketch, "E1686", {"start": v(-74.03, -0.66) * mm, "end": v(-74.03, -2.3) * mm});
            skArc(sketch, "E1687", {"start": v(-74.28, -2.73) * mm, "mid": v(-74.1, -2.54) * mm, "end": v(-74.03, -2.3) * mm});
            skArc(sketch, "E1688", {"start": v(-74.28, -2.73) * mm, "mid": v(-74.38, -3.51) * mm, "end": v(-73.6, -3.41) * mm});
            skArc(sketch, "E1689", {"start": v(-73.16, -3.16) * mm, "mid": v(-73.41, -3.23) * mm, "end": v(-73.6, -3.41) * mm});
            skLineSegment(sketch, "E1690", {"start": v(-73.16, -3.16) * mm, "end": v(-57.63, -3.16) * mm});
            skCircle(sketch, "E1691", {"center": v(-87.63, -32.46) * mm, "radius": 11.1 * mm});
            skCircle(sketch, "E1692", {"center": v(-70.63, -32.46) * mm, "radius": 4 * mm});
            skArc(sketch, "E1693", {"start": v(-63.9, -20.66) * mm, "mid": v(-64.14, -20.73) * mm, "end": v(-64.33, -20.91) * mm});
            skArc(sketch, "E1694", {"start": v(-65.01, -20.23) * mm, "mid": v(-65.11, -21.01) * mm, "end": v(-64.33, -20.91) * mm});
            skArc(sketch, "E1695", {"start": v(-65.01, -20.23) * mm, "mid": v(-64.83, -20.04) * mm, "end": v(-64.76, -19.8) * mm});
            skLineSegment(sketch, "E1696", {"start": v(-64.76, -19.8) * mm, "end": v(-64.76, -15.33) * mm});
            skArc(sketch, "E1697", {"start": v(-64.76, -15.33) * mm, "mid": v(-64.83, -15.08) * mm, "end": v(-65.01, -14.9) * mm});
            skArc(sketch, "E1698", {"start": v(-64.33, -14.21) * mm, "mid": v(-65.11, -14.1) * mm, "end": v(-65.01, -14.9) * mm});
            skArc(sketch, "E1699", {"start": v(-64.33, -14.21) * mm, "mid": v(-64.14, -14.4) * mm, "end": v(-63.9, -14.46) * mm});
            skLineSegment(sketch, "E1700", {"start": v(-63.9, -14.46) * mm, "end": v(-62.33, -14.46) * mm});
            skArc(sketch, "E1701", {"start": v(-62.33, -14.46) * mm, "mid": v(-62.08, -14.4) * mm, "end": v(-61.9, -14.21) * mm});
            skArc(sketch, "E1702", {"start": v(-61.21, -14.9) * mm, "mid": v(-61.1, -14.1) * mm, "end": v(-61.9, -14.21) * mm});
            skArc(sketch, "E1703", {"start": v(-61.21, -14.9) * mm, "mid": v(-61.4, -15.08) * mm, "end": v(-61.46, -15.33) * mm});
            skLineSegment(sketch, "E1704", {"start": v(-61.46, -15.33) * mm, "end": v(-61.46, -19.8) * mm});
            skArc(sketch, "E1705", {"start": v(-61.46, -19.8) * mm, "mid": v(-61.4, -20.04) * mm, "end": v(-61.21, -20.23) * mm});
            skArc(sketch, "E1706", {"start": v(-61.9, -20.91) * mm, "mid": v(-61.1, -21.01) * mm, "end": v(-61.21, -20.23) * mm});
            skArc(sketch, "E1707", {"start": v(-61.9, -20.91) * mm, "mid": v(-62.08, -20.73) * mm, "end": v(-62.33, -20.66) * mm});
            skLineSegment(sketch, "E1708", {"start": v(-62.33, -20.66) * mm, "end": v(-63.9, -20.66) * mm});
            skArc(sketch, "E1709", {"start": v(-63.9, -41.86) * mm, "mid": v(-64.14, -41.93) * mm, "end": v(-64.33, -42.11) * mm});
            skArc(sketch, "E1710", {"start": v(-65.01, -41.43) * mm, "mid": v(-65.11, -42.21) * mm, "end": v(-64.33, -42.11) * mm});
            skArc(sketch, "E1711", {"start": v(-65.01, -41.43) * mm, "mid": v(-64.83, -41.24) * mm, "end": v(-64.76, -41) * mm});
            skLineSegment(sketch, "E1712", {"start": v(-64.76, -41) * mm, "end": v(-64.76, -36.53) * mm});
            skArc(sketch, "E1713", {"start": v(-64.76, -36.53) * mm, "mid": v(-64.83, -36.28) * mm, "end": v(-65.01, -36.1) * mm});
            skArc(sketch, "E1714", {"start": v(-64.33, -35.41) * mm, "mid": v(-65.11, -35.3) * mm, "end": v(-65.01, -36.1) * mm});
            skArc(sketch, "E1715", {"start": v(-64.33, -35.41) * mm, "mid": v(-64.14, -35.6) * mm, "end": v(-63.9, -35.66) * mm});
            skLineSegment(sketch, "E1716", {"start": v(-63.9, -35.66) * mm, "end": v(-62.33, -35.66) * mm});
            skArc(sketch, "E1717", {"start": v(-62.33, -35.66) * mm, "mid": v(-62.08, -35.6) * mm, "end": v(-61.9, -35.41) * mm});
            skArc(sketch, "E1718", {"start": v(-61.21, -36.1) * mm, "mid": v(-61.1, -35.3) * mm, "end": v(-61.9, -35.41) * mm});
            skArc(sketch, "E1719", {"start": v(-61.21, -36.1) * mm, "mid": v(-61.4, -36.28) * mm, "end": v(-61.46, -36.53) * mm});
            skLineSegment(sketch, "E1720", {"start": v(-61.46, -36.53) * mm, "end": v(-61.46, -41) * mm});
            skArc(sketch, "E1721", {"start": v(-61.46, -41) * mm, "mid": v(-61.4, -41.24) * mm, "end": v(-61.21, -41.43) * mm});
            skArc(sketch, "E1722", {"start": v(-61.9, -42.11) * mm, "mid": v(-61.1, -42.21) * mm, "end": v(-61.21, -41.43) * mm});
            skArc(sketch, "E1723", {"start": v(-61.9, -42.11) * mm, "mid": v(-62.08, -41.93) * mm, "end": v(-62.33, -41.86) * mm});
            skLineSegment(sketch, "E1724", {"start": v(-62.33, -41.86) * mm, "end": v(-63.9, -41.86) * mm});
            skArc(sketch, "E1725", {"start": v(-112.93, -20.66) * mm, "mid": v(-113.18, -20.73) * mm, "end": v(-113.37, -20.91) * mm});
            skArc(sketch, "E1726", {"start": v(-114.05, -20.23) * mm, "mid": v(-114.15, -21.01) * mm, "end": v(-113.37, -20.91) * mm});
            skArc(sketch, "E1727", {"start": v(-114.05, -20.23) * mm, "mid": v(-113.87, -20.04) * mm, "end": v(-113.8, -19.8) * mm});
            skLineSegment(sketch, "E1728", {"start": v(-113.8, -19.8) * mm, "end": v(-113.8, -15.33) * mm});
            skArc(sketch, "E1729", {"start": v(-113.8, -15.33) * mm, "mid": v(-113.87, -15.08) * mm, "end": v(-114.05, -14.9) * mm});
            skArc(sketch, "E1730", {"start": v(-113.37, -14.21) * mm, "mid": v(-114.15, -14.1) * mm, "end": v(-114.05, -14.9) * mm});
            skArc(sketch, "E1731", {"start": v(-113.37, -14.21) * mm, "mid": v(-113.18, -14.4) * mm, "end": v(-112.93, -14.46) * mm});
            skLineSegment(sketch, "E1732", {"start": v(-112.93, -14.46) * mm, "end": v(-111.37, -14.46) * mm});
            skArc(sketch, "E1733", {"start": v(-111.37, -14.46) * mm, "mid": v(-111.12, -14.4) * mm, "end": v(-110.93, -14.21) * mm});
            skArc(sketch, "E1734", {"start": v(-110.25, -14.9) * mm, "mid": v(-110.15, -14.1) * mm, "end": v(-110.93, -14.21) * mm});
            skArc(sketch, "E1735", {"start": v(-110.25, -14.9) * mm, "mid": v(-110.43, -15.08) * mm, "end": v(-110.5, -15.33) * mm});
            skLineSegment(sketch, "E1736", {"start": v(-110.5, -15.33) * mm, "end": v(-110.5, -19.8) * mm});
            skArc(sketch, "E1737", {"start": v(-110.5, -19.8) * mm, "mid": v(-110.43, -20.04) * mm, "end": v(-110.25, -20.23) * mm});
            skArc(sketch, "E1738", {"start": v(-110.93, -20.91) * mm, "mid": v(-110.15, -21.01) * mm, "end": v(-110.25, -20.23) * mm});
            skArc(sketch, "E1739", {"start": v(-110.93, -20.91) * mm, "mid": v(-111.12, -20.73) * mm, "end": v(-111.37, -20.66) * mm});
            skLineSegment(sketch, "E1740", {"start": v(-111.37, -20.66) * mm, "end": v(-112.93, -20.66) * mm});
            skArc(sketch, "E1741", {"start": v(-112.93, -41.86) * mm, "mid": v(-113.18, -41.93) * mm, "end": v(-113.37, -42.11) * mm});
            skArc(sketch, "E1742", {"start": v(-114.05, -41.43) * mm, "mid": v(-114.15, -42.21) * mm, "end": v(-113.37, -42.11) * mm});
            skArc(sketch, "E1743", {"start": v(-114.05, -41.43) * mm, "mid": v(-113.87, -41.24) * mm, "end": v(-113.8, -41) * mm});
            skLineSegment(sketch, "E1744", {"start": v(-113.8, -41) * mm, "end": v(-113.8, -36.53) * mm});
            skArc(sketch, "E1745", {"start": v(-113.8, -36.53) * mm, "mid": v(-113.87, -36.28) * mm, "end": v(-114.05, -36.1) * mm});
            skArc(sketch, "E1746", {"start": v(-113.37, -35.41) * mm, "mid": v(-114.15, -35.3) * mm, "end": v(-114.05, -36.1) * mm});
            skArc(sketch, "E1747", {"start": v(-113.37, -35.41) * mm, "mid": v(-113.18, -35.6) * mm, "end": v(-112.93, -35.66) * mm});
            skLineSegment(sketch, "E1748", {"start": v(-112.93, -35.66) * mm, "end": v(-111.37, -35.66) * mm});
            skArc(sketch, "E1749", {"start": v(-111.37, -35.66) * mm, "mid": v(-111.12, -35.6) * mm, "end": v(-110.93, -35.41) * mm});
            skArc(sketch, "E1750", {"start": v(-110.25, -36.1) * mm, "mid": v(-110.15, -35.3) * mm, "end": v(-110.93, -35.41) * mm});
            skArc(sketch, "E1751", {"start": v(-110.25, -36.1) * mm, "mid": v(-110.43, -36.28) * mm, "end": v(-110.5, -36.53) * mm});
            skLineSegment(sketch, "E1752", {"start": v(-110.5, -36.53) * mm, "end": v(-110.5, -41) * mm});
            skArc(sketch, "E1753", {"start": v(-110.5, -41) * mm, "mid": v(-110.43, -41.24) * mm, "end": v(-110.25, -41.43) * mm});
            skArc(sketch, "E1754", {"start": v(-110.93, -42.11) * mm, "mid": v(-110.15, -42.21) * mm, "end": v(-110.25, -41.43) * mm});
            skArc(sketch, "E1755", {"start": v(-110.93, -42.11) * mm, "mid": v(-111.12, -41.93) * mm, "end": v(-111.37, -41.86) * mm});
            skLineSegment(sketch, "E1756", {"start": v(-111.37, -41.86) * mm, "end": v(-112.93, -41.86) * mm});
            skCircle(sketch, "E1757", {"center": v(-63.11, -28.16) * mm, "radius": 1.6 * mm});
            skCircle(sketch, "E1758", {"center": v(-72.13, -16.96) * mm, "radius": 1.6 * mm});
            skCircle(sketch, "E1759", {"center": v(-72.13, -47.96) * mm, "radius": 1.6 * mm});
            skCircle(sketch, "E1760", {"center": v(-103.13, -16.96) * mm, "radius": 1.6 * mm});
            skCircle(sketch, "E1761", {"center": v(-103.13, -47.96) * mm, "radius": 1.6 * mm});
            skCircle(sketch, "E1762", {"center": v(-112.15, -28.16) * mm, "radius": 1.6 * mm});
            skArc(sketch, "E1763", {"start": v(-142.52, -127.6) * mm, "mid": v(-148.7, -131.92) * mm, "end": v(-151.08, -139.09) * mm});
            skLineSegment(sketch, "E1764", {"start": v(-151.08, -139.09) * mm, "end": v(-151.08, -142.33) * mm});
            skLineSegment(sketch, "E1765", {"start": v(-151.08, -142.33) * mm, "end": v(-141.95, -142.33) * mm});
            skArc(sketch, "E1766", {"start": v(-141.95, -142.33) * mm, "mid": v(-141.7, -142.26) * mm, "end": v(-141.52, -142.08) * mm});
            skArc(sketch, "E1767", {"start": v(-140.83, -142.76) * mm, "mid": v(-140.73, -141.97) * mm, "end": v(-141.52, -142.08) * mm});
            skArc(sketch, "E1768", {"start": v(-140.83, -142.76) * mm, "mid": v(-141.02, -142.94) * mm, "end": v(-141.08, -143.2) * mm});
            skLineSegment(sketch, "E1769", {"start": v(-141.08, -143.2) * mm, "end": v(-141.08, -144.76) * mm});
            skArc(sketch, "E1770", {"start": v(-141.08, -144.76) * mm, "mid": v(-141.02, -145) * mm, "end": v(-140.83, -145.2) * mm});
            skArc(sketch, "E1771", {"start": v(-141.52, -145.88) * mm, "mid": v(-140.73, -145.98) * mm, "end": v(-140.83, -145.2) * mm});
            skArc(sketch, "E1772", {"start": v(-141.52, -145.88) * mm, "mid": v(-141.7, -145.7) * mm, "end": v(-141.95, -145.63) * mm});
            skLineSegment(sketch, "E1773", {"start": v(-141.95, -145.63) * mm, "end": v(-151.08, -145.63) * mm});
            skLineSegment(sketch, "E1774", {"start": v(-151.08, -145.63) * mm, "end": v(-151.08, -176.15) * mm});
            skArc(sketch, "E1775", {"start": v(-151.08, -176.15) * mm, "mid": v(-147.57, -184.64) * mm, "end": v(-139.08, -188.15) * mm});
            skLineSegment(sketch, "E1776", {"start": v(-139.08, -188.15) * mm, "end": v(-117.48, -188.15) * mm});
            skArc(sketch, "E1777", {"start": v(-117.48, -188.15) * mm, "mid": v(-111.18, -186.37) * mm, "end": v(-106.76, -181.55) * mm});
            skCircle(sketch, "E1778", {"center": v(-121.38, -174.78) * mm, "radius": 5 * mm});
            skCircle(sketch, "E1779", {"center": v(-138.38, -174.78) * mm, "radius": 4 * mm});
            skCircle(sketch, "E1780", {"center": v(-115.26, -143.98) * mm, "radius": 1.6 * mm});
            skLineSegment(sketch, "E1781", {"start": v(-74.6, -142.28) * mm, "end": v(-63.08, -142.28) * mm});
            skLineSegment(sketch, "E1782", {"start": v(-63.08, -142.28) * mm, "end": v(-63.08, -132.82) * mm});
            skArc(sketch, "E1783", {"start": v(-63.08, -132.82) * mm, "mid": v(-63.37, -130.21) * mm, "end": v(-64.21, -127.74) * mm});
            skLineSegment(sketch, "E1784", {"start": v(-64.21, -127.74) * mm, "end": v(-74.6, -111.28) * mm});
            skLineSegment(sketch, "E1785", {"start": v(-74.6, -111.28) * mm, "end": v(-77.7, -111.28) * mm});
            skLineSegment(sketch, "E1786", {"start": v(-89.43, -145.64) * mm, "end": v(-89.43, -143.15) * mm});
            skArc(sketch, "E1787", {"start": v(-89.43, -143.15) * mm, "mid": v(-89.5, -142.9) * mm, "end": v(-89.68, -142.71) * mm});
            skArc(sketch, "E1788", {"start": v(-89, -142.03) * mm, "mid": v(-89.79, -141.93) * mm, "end": v(-89.68, -142.71) * mm});
            skArc(sketch, "E1789", {"start": v(-89, -142.03) * mm, "mid": v(-88.82, -142.21) * mm, "end": v(-88.57, -142.28) * mm});
            skLineSegment(sketch, "E1790", {"start": v(-88.57, -142.28) * mm, "end": v(-77.9, -142.28) * mm});
            skLineSegment(sketch, "E1791", {"start": v(-77.9, -142.28) * mm, "end": v(-77.9, -132.5) * mm});
            skArc(sketch, "E1792", {"start": v(-77.9, -132.5) * mm, "mid": v(-77.97, -132.25) * mm, "end": v(-78.16, -132.07) * mm});
            skArc(sketch, "E1793", {"start": v(-77.47, -131.38) * mm, "mid": v(-78.26, -131.28) * mm, "end": v(-78.16, -132.07) * mm});
            skArc(sketch, "E1794", {"start": v(-77.47, -131.38) * mm, "mid": v(-77.3, -131.57) * mm, "end": v(-77.04, -131.63) * mm});
            skLineSegment(sketch, "E1795", {"start": v(-77.04, -131.63) * mm, "end": v(-75.47, -131.63) * mm});
            skArc(sketch, "E1796", {"start": v(-75.47, -131.63) * mm, "mid": v(-75.22, -131.57) * mm, "end": v(-75.04, -131.38) * mm});
            skArc(sketch, "E1797", {"start": v(-74.36, -132.07) * mm, "mid": v(-74.25, -131.28) * mm, "end": v(-75.04, -131.38) * mm});
            skArc(sketch, "E1798", {"start": v(-74.36, -132.07) * mm, "mid": v(-74.54, -132.25) * mm, "end": v(-74.6, -132.5) * mm});
            skLineSegment(sketch, "E1799", {"start": v(-74.6, -132.5) * mm, "end": v(-74.6, -142.28) * mm});
            skCircle(sketch, "E1800", {"center": v(-76.26, -121.63) * mm, "radius": 1.6 * mm});
            skLineSegment(sketch, "E1801", {"start": v(-77.7, -111.28) * mm, "end": v(-142.52, -127.6) * mm});
            skLineSegment(sketch, "E1802", {"start": v(-106.76, -181.55) * mm, "end": v(-89.43, -145.64) * mm});
            skArc(sketch, "E1803", {"start": v(-301.7, 124.98) * mm, "mid": v(-295.52, 129.3) * mm, "end": v(-293.14, 136.48) * mm});
            skLineSegment(sketch, "E1804", {"start": v(-293.14, 136.48) * mm, "end": v(-293.14, 139.71) * mm});
            skLineSegment(sketch, "E1805", {"start": v(-293.14, 139.71) * mm, "end": v(-302.28, 139.71) * mm});
            skArc(sketch, "E1806", {"start": v(-302.28, 139.71) * mm, "mid": v(-302.53, 139.65) * mm, "end": v(-302.71, 139.46) * mm});
            skArc(sketch, "E1807", {"start": v(-303.4, 140.15) * mm, "mid": v(-303.5, 139.36) * mm, "end": v(-302.71, 139.46) * mm});
            skArc(sketch, "E1808", {"start": v(-303.4, 140.15) * mm, "mid": v(-303.21, 140.33) * mm, "end": v(-303.14, 140.58) * mm});
            skLineSegment(sketch, "E1809", {"start": v(-303.14, 140.58) * mm, "end": v(-303.14, 142.15) * mm});
            skArc(sketch, "E1810", {"start": v(-303.14, 142.15) * mm, "mid": v(-303.21, 142.4) * mm, "end": v(-303.4, 142.58) * mm});
            skArc(sketch, "E1811", {"start": v(-302.71, 143.26) * mm, "mid": v(-303.5, 143.37) * mm, "end": v(-303.4, 142.58) * mm});
            skArc(sketch, "E1812", {"start": v(-302.71, 143.26) * mm, "mid": v(-302.53, 143.08) * mm, "end": v(-302.28, 143.01) * mm});
            skLineSegment(sketch, "E1813", {"start": v(-302.28, 143.01) * mm, "end": v(-293.14, 143.01) * mm});
            skLineSegment(sketch, "E1814", {"start": v(-293.14, 143.01) * mm, "end": v(-293.14, 173.54) * mm});
            skArc(sketch, "E1815", {"start": v(-293.14, 173.54) * mm, "mid": v(-296.66, 182.03) * mm, "end": v(-305.14, 185.54) * mm});
            skLineSegment(sketch, "E1816", {"start": v(-305.14, 185.54) * mm, "end": v(-326.75, 185.54) * mm});
            skArc(sketch, "E1817", {"start": v(-326.75, 185.54) * mm, "mid": v(-333.05, 183.76) * mm, "end": v(-337.47, 178.94) * mm});
            skCircle(sketch, "E1818", {"center": v(-322.84, 172.17) * mm, "radius": 5 * mm});
            skCircle(sketch, "E1819", {"center": v(-305.84, 172.17) * mm, "radius": 4 * mm});
            skCircle(sketch, "E1820", {"center": v(-328.97, 141.37) * mm, "radius": 1.6 * mm});
            skLineSegment(sketch, "E1821", {"start": v(-369.62, 139.67) * mm, "end": v(-381.14, 139.67) * mm});
            skLineSegment(sketch, "E1822", {"start": v(-381.14, 139.67) * mm, "end": v(-381.14, 130.2) * mm});
            skArc(sketch, "E1823", {"start": v(-381.14, 130.2) * mm, "mid": v(-380.86, 127.6) * mm, "end": v(-380.02, 125.13) * mm});
            skLineSegment(sketch, "E1824", {"start": v(-380.02, 125.13) * mm, "end": v(-369.62, 108.67) * mm});
            skLineSegment(sketch, "E1825", {"start": v(-369.62, 108.67) * mm, "end": v(-366.53, 108.67) * mm});
            skLineSegment(sketch, "E1826", {"start": v(-354.8, 143.03) * mm, "end": v(-354.8, 140.54) * mm});
            skArc(sketch, "E1827", {"start": v(-354.8, 140.54) * mm, "mid": v(-354.73, 140.29) * mm, "end": v(-354.54, 140.1) * mm});
            skArc(sketch, "E1828", {"start": v(-355.23, 139.42) * mm, "mid": v(-354.44, 139.32) * mm, "end": v(-354.54, 140.1) * mm});
            skArc(sketch, "E1829", {"start": v(-355.23, 139.42) * mm, "mid": v(-355.41, 139.6) * mm, "end": v(-355.66, 139.67) * mm});
            skLineSegment(sketch, "E1830", {"start": v(-355.66, 139.67) * mm, "end": v(-366.32, 139.67) * mm});
            skLineSegment(sketch, "E1831", {"start": v(-366.32, 139.67) * mm, "end": v(-366.32, 129.89) * mm});
            skArc(sketch, "E1832", {"start": v(-366.32, 129.89) * mm, "mid": v(-366.25, 129.64) * mm, "end": v(-366.07, 129.45) * mm});
            skArc(sketch, "E1833", {"start": v(-366.75, 128.77) * mm, "mid": v(-365.97, 128.67) * mm, "end": v(-366.07, 129.45) * mm});
            skArc(sketch, "E1834", {"start": v(-366.75, 128.77) * mm, "mid": v(-366.94, 128.95) * mm, "end": v(-367.19, 129.02) * mm});
            skLineSegment(sketch, "E1835", {"start": v(-367.19, 129.02) * mm, "end": v(-368.75, 129.02) * mm});
            skArc(sketch, "E1836", {"start": v(-368.75, 129.02) * mm, "mid": v(-369, 128.96) * mm, "end": v(-369.19, 128.77) * mm});
            skArc(sketch, "E1837", {"start": v(-369.87, 129.46) * mm, "mid": v(-369.97, 128.67) * mm, "end": v(-369.19, 128.77) * mm});
            skArc(sketch, "E1838", {"start": v(-369.87, 129.46) * mm, "mid": v(-369.69, 129.64) * mm, "end": v(-369.62, 129.89) * mm});
            skLineSegment(sketch, "E1839", {"start": v(-369.62, 129.89) * mm, "end": v(-369.62, 139.67) * mm});
            skCircle(sketch, "E1840", {"center": v(-367.97, 119.02) * mm, "radius": 1.6 * mm});
            skLineSegment(sketch, "E1841", {"start": v(-366.53, 108.67) * mm, "end": v(-301.7, 124.98) * mm});
            skLineSegment(sketch, "E1842", {"start": v(-337.47, 178.94) * mm, "end": v(-354.8, 143.03) * mm});
            skLineSegment(sketch, "E1843", {"start": v(190.2, -107.17) * mm, "end": v(175.7, -92.69) * mm});
            skArc(sketch, "E1844", {"start": v(175.7, -92.69) * mm, "mid": v(173.76, -91.39) * mm, "end": v(171.46, -90.93) * mm});
            skLineSegment(sketch, "E1845", {"start": v(171.46, -90.93) * mm, "end": v(156.43, -90.93) * mm});
            skArc(sketch, "E1846", {"start": v(156.43, -90.93) * mm, "mid": v(154.14, -91.39) * mm, "end": v(152.2, -92.69) * mm});
            skLineSegment(sketch, "E1847", {"start": v(152.2, -92.69) * mm, "end": v(135.95, -108.93) * mm});
            skArc(sketch, "E1848", {"start": v(128.95, -101.93) * mm, "mid": v(128.95, -108.93) * mm, "end": v(135.95, -108.93) * mm});
            skLineSegment(sketch, "E1849", {"start": v(128.95, -101.93) * mm, "end": v(150.2, -80.69) * mm});
            skArc(sketch, "E1850", {"start": v(150.2, -80.69) * mm, "mid": v(151.5, -78.74) * mm, "end": v(151.95, -76.45) * mm});
            skLineSegment(sketch, "E1851", {"start": v(151.95, -76.45) * mm, "end": v(151.95, 74.58) * mm});
            skArc(sketch, "E1852", {"start": v(151.95, 74.58) * mm, "mid": v(151.5, 76.88) * mm, "end": v(150.2, 78.83) * mm});
            skLineSegment(sketch, "E1853", {"start": v(150.2, 78.83) * mm, "end": v(128.95, 100.07) * mm});
            skArc(sketch, "E1854", {"start": v(135.95, 107.07) * mm, "mid": v(128.95, 107.07) * mm, "end": v(128.95, 100.07) * mm});
            skLineSegment(sketch, "E1855", {"start": v(135.95, 107.07) * mm, "end": v(152.2, 90.83) * mm});
            skLineSegment(sketch, "E1856", {"start": v(321.7, 90.82) * mm, "end": v(337.95, 107.07) * mm});
            skArc(sketch, "E1857", {"start": v(344.95, 100.07) * mm, "mid": v(344.95, 107.07) * mm, "end": v(337.95, 107.07) * mm});
            skLineSegment(sketch, "E1858", {"start": v(344.95, 100.07) * mm, "end": v(323.7, 78.83) * mm});
            skArc(sketch, "E1859", {"start": v(323.7, 78.83) * mm, "mid": v(322.4, 76.88) * mm, "end": v(321.95, 74.58) * mm});
            skLineSegment(sketch, "E1860", {"start": v(321.95, 74.58) * mm, "end": v(321.95, 14.02) * mm});
            skArc(sketch, "E1861", {"start": v(321.95, -76.45) * mm, "mid": v(322.4, -78.74) * mm, "end": v(323.7, -80.69) * mm});
            skLineSegment(sketch, "E1862", {"start": v(323.7, -80.69) * mm, "end": v(344.95, -101.93) * mm});
            skArc(sketch, "E1863", {"start": v(337.95, -108.93) * mm, "mid": v(344.95, -108.93) * mm, "end": v(344.95, -101.93) * mm});
            skLineSegment(sketch, "E1864", {"start": v(337.95, -108.93) * mm, "end": v(321.7, -92.69) * mm});
            skArc(sketch, "E1865", {"start": v(321.7, -92.69) * mm, "mid": v(319.76, -91.39) * mm, "end": v(317.46, -90.93) * mm});
            skLineSegment(sketch, "E1866", {"start": v(317.46, -90.93) * mm, "end": v(302.43, -90.93) * mm});
            skArc(sketch, "E1867", {"start": v(302.43, -90.93) * mm, "mid": v(300.14, -91.39) * mm, "end": v(298.2, -92.69) * mm});
            skLineSegment(sketch, "E1868", {"start": v(298.2, -92.69) * mm, "end": v(283.7, -107.17) * mm});
            skArc(sketch, "E1869", {"start": v(279.46, -108.93) * mm, "mid": v(281.76, -108.48) * mm, "end": v(283.7, -107.17) * mm});
            skLineSegment(sketch, "E1870", {"start": v(279.46, -108.93) * mm, "end": v(262.43, -108.93) * mm});
            skArc(sketch, "E1871", {"start": v(258.2, -107.17) * mm, "mid": v(260.14, -108.48) * mm, "end": v(262.43, -108.93) * mm});
            skLineSegment(sketch, "E1872", {"start": v(258.2, -107.17) * mm, "end": v(243.7, -92.69) * mm});
            skArc(sketch, "E1873", {"start": v(243.7, -92.69) * mm, "mid": v(241.76, -91.39) * mm, "end": v(239.46, -90.93) * mm});
            skLineSegment(sketch, "E1874", {"start": v(239.46, -90.93) * mm, "end": v(234.43, -90.93) * mm});
            skArc(sketch, "E1875", {"start": v(234.43, -90.93) * mm, "mid": v(232.14, -91.39) * mm, "end": v(230.2, -92.69) * mm});
            skLineSegment(sketch, "E1876", {"start": v(230.2, -92.69) * mm, "end": v(215.7, -107.17) * mm});
            skArc(sketch, "E1877", {"start": v(211.46, -108.93) * mm, "mid": v(213.76, -108.48) * mm, "end": v(215.7, -107.17) * mm});
            skLineSegment(sketch, "E1878", {"start": v(211.46, -108.93) * mm, "end": v(194.43, -108.93) * mm});
            skArc(sketch, "E1879", {"start": v(190.2, -107.17) * mm, "mid": v(192.14, -108.48) * mm, "end": v(194.43, -108.93) * mm});
            skLineSegment(sketch, "E1880", {"start": v(269.88, 31.8) * mm, "end": v(300.68, 62.6) * mm});
            skArc(sketch, "E1881", {"start": v(311.95, 57.93) * mm, "mid": v(307.87, 64.03) * mm, "end": v(300.68, 62.6) * mm});
            skLineSegment(sketch, "E1882", {"start": v(311.95, 57.93) * mm, "end": v(311.95, -59.8) * mm});
            skArc(sketch, "E1883", {"start": v(300.68, -64.47) * mm, "mid": v(307.87, -65.9) * mm, "end": v(311.95, -59.8) * mm});
            skLineSegment(sketch, "E1884", {"start": v(300.68, -64.47) * mm, "end": v(269.88, -33.67) * mm});
            skArc(sketch, "E1885", {"start": v(267.95, -29) * mm, "mid": v(268.45, -31.52) * mm, "end": v(269.88, -33.67) * mm});
            skLineSegment(sketch, "E1886", {"start": v(267.95, -29) * mm, "end": v(267.95, 27.13) * mm});
            skArc(sketch, "E1887", {"start": v(269.88, 31.8) * mm, "mid": v(268.45, 29.66) * mm, "end": v(267.95, 27.13) * mm});
            skLineSegment(sketch, "E1888", {"start": v(230.2, -79.17) * mm, "end": v(213.7, -62.69) * mm});
            skArc(sketch, "E1889", {"start": v(211.95, -58.45) * mm, "mid": v(212.4, -60.74) * mm, "end": v(213.7, -62.69) * mm});
            skLineSegment(sketch, "E1890", {"start": v(211.95, -58.45) * mm, "end": v(211.95, -43.42) * mm});
            skArc(sketch, "E1891", {"start": v(213.7, -39.17) * mm, "mid": v(212.4, -41.12) * mm, "end": v(211.95, -43.42) * mm});
            skLineSegment(sketch, "E1892", {"start": v(213.7, -39.17) * mm, "end": v(230.2, -22.69) * mm});
            skArc(sketch, "E1893", {"start": v(234.43, -20.93) * mm, "mid": v(232.14, -21.39) * mm, "end": v(230.2, -22.69) * mm});
            skLineSegment(sketch, "E1894", {"start": v(234.43, -20.93) * mm, "end": v(239.46, -20.93) * mm});
            skArc(sketch, "E1895", {"start": v(243.7, -22.69) * mm, "mid": v(241.76, -21.39) * mm, "end": v(239.46, -20.93) * mm});
            skLineSegment(sketch, "E1896", {"start": v(243.7, -22.69) * mm, "end": v(260.2, -39.17) * mm});
            skArc(sketch, "E1897", {"start": v(261.95, -43.42) * mm, "mid": v(261.5, -41.12) * mm, "end": v(260.2, -39.17) * mm});
            skLineSegment(sketch, "E1898", {"start": v(261.95, -43.42) * mm, "end": v(261.95, -58.45) * mm});
            skArc(sketch, "E1899", {"start": v(260.2, -62.69) * mm, "mid": v(261.5, -60.74) * mm, "end": v(261.95, -58.45) * mm});
            skLineSegment(sketch, "E1900", {"start": v(260.2, -62.69) * mm, "end": v(243.7, -79.17) * mm});
            skArc(sketch, "E1901", {"start": v(239.46, -80.93) * mm, "mid": v(241.76, -80.48) * mm, "end": v(243.7, -79.17) * mm});
            skLineSegment(sketch, "E1902", {"start": v(239.46, -80.93) * mm, "end": v(234.43, -80.93) * mm});
            skArc(sketch, "E1903", {"start": v(230.2, -79.17) * mm, "mid": v(232.14, -80.48) * mm, "end": v(234.43, -80.93) * mm});
            skLineSegment(sketch, "E1904", {"start": v(260.2, 37.31) * mm, "end": v(243.7, 20.83) * mm});
            skArc(sketch, "E1905", {"start": v(239.46, 19.07) * mm, "mid": v(241.76, 19.52) * mm, "end": v(243.7, 20.83) * mm});
            skLineSegment(sketch, "E1906", {"start": v(239.46, 19.07) * mm, "end": v(234.43, 19.07) * mm});
            skArc(sketch, "E1907", {"start": v(230.2, 20.83) * mm, "mid": v(232.14, 19.52) * mm, "end": v(234.43, 19.07) * mm});
            skLineSegment(sketch, "E1908", {"start": v(230.2, 20.83) * mm, "end": v(213.7, 37.31) * mm});
            skArc(sketch, "E1909", {"start": v(211.95, 41.55) * mm, "mid": v(212.4, 39.26) * mm, "end": v(213.7, 37.31) * mm});
            skArc(sketch, "E1910", {"start": v(260.2, 37.31) * mm, "mid": v(261.5, 39.26) * mm, "end": v(261.95, 41.55) * mm});
            skLineSegment(sketch, "E1911", {"start": v(284, -89.57) * mm, "end": v(284, -82.3) * mm});
            skLineSegment(sketch, "E1912", {"start": v(190.76, -90.43) * mm, "end": v(213.13, -90.43) * mm});
            skArc(sketch, "E1913", {"start": v(213.57, -90.68) * mm, "mid": v(213.38, -90.5) * mm, "end": v(213.13, -90.43) * mm});
            skArc(sketch, "E1914", {"start": v(213.57, -90.68) * mm, "mid": v(214.35, -90.79) * mm, "end": v(214.25, -90) * mm});
            skArc(sketch, "E1915", {"start": v(214, -89.57) * mm, "mid": v(214.07, -89.82) * mm, "end": v(214.25, -90) * mm});
            skLineSegment(sketch, "E1916", {"start": v(214, -89.57) * mm, "end": v(214, -82.3) * mm});
            skArc(sketch, "E1917", {"start": v(214.25, -81.87) * mm, "mid": v(214.07, -82.05) * mm, "end": v(214, -82.3) * mm});
            skArc(sketch, "E1918", {"start": v(214.25, -81.87) * mm, "mid": v(214.35, -81.08) * mm, "end": v(213.57, -81.18) * mm});
            skArc(sketch, "E1919", {"start": v(213.13, -81.43) * mm, "mid": v(213.38, -81.37) * mm, "end": v(213.57, -81.18) * mm});
            skLineSegment(sketch, "E1920", {"start": v(213.13, -81.43) * mm, "end": v(190.76, -81.43) * mm});
            skArc(sketch, "E1921", {"start": v(190.33, -81.18) * mm, "mid": v(190.51, -81.37) * mm, "end": v(190.76, -81.43) * mm});
            skArc(sketch, "E1922", {"start": v(190.33, -81.18) * mm, "mid": v(189.54, -81.08) * mm, "end": v(189.65, -81.87) * mm});
            skArc(sketch, "E1923", {"start": v(189.9, -82.3) * mm, "mid": v(189.83, -82.05) * mm, "end": v(189.65, -81.87) * mm});
            skLineSegment(sketch, "E1924", {"start": v(189.9, -82.3) * mm, "end": v(189.9, -89.57) * mm});
            skArc(sketch, "E1925", {"start": v(189.65, -90) * mm, "mid": v(189.83, -89.82) * mm, "end": v(189.9, -89.57) * mm});
            skArc(sketch, "E1926", {"start": v(189.65, -90) * mm, "mid": v(189.54, -90.79) * mm, "end": v(190.33, -90.68) * mm});
            skArc(sketch, "E1927", {"start": v(190.76, -90.43) * mm, "mid": v(190.51, -90.5) * mm, "end": v(190.33, -90.68) * mm});
            skCircle(sketch, "E1928", {"center": v(341.45, -105.43) * mm, "radius": 1.6 * mm});
            skCircle(sketch, "E1929", {"center": v(132.45, -105.43) * mm, "radius": 1.6 * mm});
            skCircle(sketch, "E1930", {"center": v(271.95, -100.93) * mm, "radius": 1.6 * mm});
            skCircle(sketch, "E1931", {"center": v(201.95, -100.93) * mm, "radius": 1.6 * mm});
            skCircle(sketch, "E1932", {"center": v(271.95, -70.93) * mm, "radius": 1.6 * mm});
            skCircle(sketch, "E1933", {"center": v(201.95, -70.93) * mm, "radius": 1.6 * mm});
            skCircle(sketch, "E1934", {"center": v(254.45, -12.93) * mm, "radius": 1.6 * mm});
            skCircle(sketch, "E1935", {"center": v(219.45, -0.93) * mm, "radius": 1.6 * mm});
            skCircle(sketch, "E1936", {"center": v(254.45, 11.07) * mm, "radius": 1.6 * mm});
            skCircle(sketch, "E1937", {"center": v(341.45, 103.57) * mm, "radius": 1.6 * mm});
            skCircle(sketch, "E1938", {"center": v(132.45, 103.57) * mm, "radius": 1.6 * mm});
            skLineSegment(sketch, "E1939", {"start": v(260.76, -90.43) * mm, "end": v(283.13, -90.43) * mm});
            skArc(sketch, "E1940", {"start": v(283.57, -90.68) * mm, "mid": v(283.38, -90.5) * mm, "end": v(283.13, -90.43) * mm});
            skArc(sketch, "E1941", {"start": v(283.57, -90.68) * mm, "mid": v(284.35, -90.79) * mm, "end": v(284.25, -90) * mm});
            skArc(sketch, "E1942", {"start": v(284, -89.57) * mm, "mid": v(284.07, -89.82) * mm, "end": v(284.25, -90) * mm});
            skArc(sketch, "E1943", {"start": v(284.25, -81.87) * mm, "mid": v(284.07, -82.05) * mm, "end": v(284, -82.3) * mm});
            skArc(sketch, "E1944", {"start": v(284.25, -81.87) * mm, "mid": v(284.35, -81.08) * mm, "end": v(283.57, -81.18) * mm});
            skArc(sketch, "E1945", {"start": v(283.13, -81.43) * mm, "mid": v(283.38, -81.37) * mm, "end": v(283.57, -81.18) * mm});
            skLineSegment(sketch, "E1946", {"start": v(283.13, -81.43) * mm, "end": v(260.76, -81.43) * mm});
            skArc(sketch, "E1947", {"start": v(260.33, -81.18) * mm, "mid": v(260.51, -81.37) * mm, "end": v(260.76, -81.43) * mm});
            skArc(sketch, "E1948", {"start": v(260.33, -81.18) * mm, "mid": v(259.54, -81.08) * mm, "end": v(259.65, -81.87) * mm});
            skArc(sketch, "E1949", {"start": v(259.9, -82.3) * mm, "mid": v(259.83, -82.05) * mm, "end": v(259.65, -81.87) * mm});
            skLineSegment(sketch, "E1950", {"start": v(259.9, -82.3) * mm, "end": v(259.9, -89.57) * mm});
            skArc(sketch, "E1951", {"start": v(259.65, -90) * mm, "mid": v(259.83, -89.82) * mm, "end": v(259.9, -89.57) * mm});
            skArc(sketch, "E1952", {"start": v(259.65, -90) * mm, "mid": v(259.54, -90.79) * mm, "end": v(260.33, -90.68) * mm});
            skArc(sketch, "E1953", {"start": v(260.76, -90.43) * mm, "mid": v(260.51, -90.5) * mm, "end": v(260.33, -90.68) * mm});
            skLineSegment(sketch, "E1954", {"start": v(202.38, -25.97) * mm, "end": v(195.23, -33.11) * mm});
            skArc(sketch, "E1955", {"start": v(194.75, -33.24) * mm, "mid": v(195, -33.24) * mm, "end": v(195.23, -33.11) * mm});
            skArc(sketch, "E1956", {"start": v(194.75, -33.24) * mm, "mid": v(194.12, -33.72) * mm, "end": v(194.75, -34.2) * mm});
            skArc(sketch, "E1957", {"start": v(195.23, -34.34) * mm, "mid": v(195, -34.2) * mm, "end": v(194.75, -34.2) * mm});
            skLineSegment(sketch, "E1958", {"start": v(195.23, -34.34) * mm, "end": v(196.39, -35.5) * mm});
            skArc(sketch, "E1959", {"start": v(196.39, -36.2) * mm, "mid": v(196.53, -35.85) * mm, "end": v(196.39, -35.5) * mm});
            skLineSegment(sketch, "E1960", {"start": v(196.39, -36.2) * mm, "end": v(192.85, -39.73) * mm});
            skArc(sketch, "E1961", {"start": v(192.14, -39.73) * mm, "mid": v(192.5, -39.88) * mm, "end": v(192.85, -39.73) * mm});
            skLineSegment(sketch, "E1962", {"start": v(192.14, -39.73) * mm, "end": v(190.99, -38.58) * mm});
            skArc(sketch, "E1963", {"start": v(190.86, -38.1) * mm, "mid": v(190.86, -38.36) * mm, "end": v(190.99, -38.58) * mm});
            skArc(sketch, "E1964", {"start": v(190.86, -38.1) * mm, "mid": v(190.38, -37.47) * mm, "end": v(189.9, -38.1) * mm});
            skArc(sketch, "E1965", {"start": v(189.76, -38.58) * mm, "mid": v(189.9, -38.36) * mm, "end": v(189.9, -38.1) * mm});
            skLineSegment(sketch, "E1966", {"start": v(189.76, -38.58) * mm, "end": v(186.13, -42.2) * mm});
            skLineSegment(sketch, "E1967", {"start": v(186.13, -42.2) * mm, "end": v(184.01, -40.09) * mm});
            skLineSegment(sketch, "E1968", {"start": v(184.01, -40.09) * mm, "end": v(184.91, -39.19) * mm});
            skLineSegment(sketch, "E1969", {"start": v(180.85, -43.25) * mm, "end": v(181.75, -42.35) * mm});
            skLineSegment(sketch, "E1970", {"start": v(181.75, -42.35) * mm, "end": v(183.87, -44.47) * mm});
            skLineSegment(sketch, "E1971", {"start": v(183.87, -44.47) * mm, "end": v(180.24, -48.1) * mm});
            skArc(sketch, "E1972", {"start": v(179.76, -48.23) * mm, "mid": v(180.02, -48.23) * mm, "end": v(180.24, -48.1) * mm});
            skArc(sketch, "E1973", {"start": v(179.76, -48.23) * mm, "mid": v(179.13, -48.72) * mm, "end": v(179.76, -49.2) * mm});
            skArc(sketch, "E1974", {"start": v(180.24, -49.33) * mm, "mid": v(180.02, -49.2) * mm, "end": v(179.76, -49.2) * mm});
            skLineSegment(sketch, "E1975", {"start": v(180.24, -49.33) * mm, "end": v(181.4, -50.48) * mm});
            skArc(sketch, "E1976", {"start": v(181.4, -51.19) * mm, "mid": v(181.54, -50.84) * mm, "end": v(181.4, -50.48) * mm});
            skLineSegment(sketch, "E1977", {"start": v(181.4, -51.19) * mm, "end": v(177.86, -54.73) * mm});
            skArc(sketch, "E1978", {"start": v(177.15, -54.73) * mm, "mid": v(177.5, -54.87) * mm, "end": v(177.86, -54.73) * mm});
            skLineSegment(sketch, "E1979", {"start": v(177.15, -54.73) * mm, "end": v(176, -53.57) * mm});
            skArc(sketch, "E1980", {"start": v(175.87, -53.09) * mm, "mid": v(175.87, -53.35) * mm, "end": v(176, -53.57) * mm});
            skArc(sketch, "E1981", {"start": v(175.87, -53.09) * mm, "mid": v(175.38, -52.46) * mm, "end": v(174.9, -53.09) * mm});
            skArc(sketch, "E1982", {"start": v(174.77, -53.57) * mm, "mid": v(174.9, -53.35) * mm, "end": v(174.9, -53.09) * mm});
            skLineSegment(sketch, "E1983", {"start": v(174.77, -53.57) * mm, "end": v(168.74, -59.6) * mm});
            skLineSegment(sketch, "E1984", {"start": v(168.74, -59.6) * mm, "end": v(168.25, -59.12) * mm});
            skLineSegment(sketch, "E1985", {"start": v(184.91, -39.19) * mm, "end": v(182.08, -36.36) * mm});
            skLineSegment(sketch, "E1986", {"start": v(182.08, -36.36) * mm, "end": v(181.18, -37.26) * mm});
            skLineSegment(sketch, "E1987", {"start": v(181.18, -37.26) * mm, "end": v(179.06, -35.14) * mm});
            skLineSegment(sketch, "E1988", {"start": v(179.06, -35.14) * mm, "end": v(176.8, -37.4) * mm});
            skLineSegment(sketch, "E1989", {"start": v(176.8, -37.4) * mm, "end": v(178.92, -39.52) * mm});
            skLineSegment(sketch, "E1990", {"start": v(178.92, -39.52) * mm, "end": v(178.02, -40.42) * mm});
            skLineSegment(sketch, "E1991", {"start": v(178.02, -40.42) * mm, "end": v(180.85, -43.25) * mm});
            skArc(sketch, "E1992", {"start": v(165.9, -53.46) * mm, "mid": v(166.52, -56.52) * mm, "end": v(168.25, -59.12) * mm});
            skArc(sketch, "E1993", {"start": v(202.38, -25.97) * mm, "mid": v(202.6, -25.63) * mm, "end": v(202.67, -25.24) * mm});
            skArc(sketch, "E1994", {"start": v(168.22, 57.25) * mm, "mid": v(166.48, 54.66) * mm, "end": v(165.87, 51.6) * mm});
            skLineSegment(sketch, "E1995", {"start": v(168.22, 57.25) * mm, "end": v(168.7, 57.74) * mm});
            skLineSegment(sketch, "E1996", {"start": v(168.7, 57.74) * mm, "end": v(174.74, 51.7) * mm});
            skArc(sketch, "E1997", {"start": v(174.87, 51.22) * mm, "mid": v(174.87, 51.48) * mm, "end": v(174.74, 51.7) * mm});
            skArc(sketch, "E1998", {"start": v(174.87, 51.22) * mm, "mid": v(175.35, 50.6) * mm, "end": v(175.83, 51.22) * mm});
            skArc(sketch, "E1999", {"start": v(175.96, 51.7) * mm, "mid": v(175.83, 51.48) * mm, "end": v(175.83, 51.22) * mm});
            skLineSegment(sketch, "E2000", {"start": v(175.96, 51.7) * mm, "end": v(177.12, 52.86) * mm});
            skArc(sketch, "E2001", {"start": v(177.82, 52.86) * mm, "mid": v(177.47, 53) * mm, "end": v(177.12, 52.86) * mm});
            skLineSegment(sketch, "E2002", {"start": v(177.82, 52.86) * mm, "end": v(181.36, 49.33) * mm});
            skArc(sketch, "E2003", {"start": v(181.36, 48.62) * mm, "mid": v(181.5, 48.97) * mm, "end": v(181.36, 49.33) * mm});
            skLineSegment(sketch, "E2004", {"start": v(181.36, 48.62) * mm, "end": v(180.2, 47.46) * mm});
            skArc(sketch, "E2005", {"start": v(179.72, 47.33) * mm, "mid": v(179.98, 47.33) * mm, "end": v(180.2, 47.46) * mm});
            skArc(sketch, "E2006", {"start": v(179.72, 47.33) * mm, "mid": v(179.1, 46.85) * mm, "end": v(179.72, 46.37) * mm});
            skArc(sketch, "E2007", {"start": v(180.2, 46.24) * mm, "mid": v(179.98, 46.37) * mm, "end": v(179.72, 46.37) * mm});
            skLineSegment(sketch, "E2008", {"start": v(180.2, 46.24) * mm, "end": v(183.83, 42.6) * mm});
            skLineSegment(sketch, "E2009", {"start": v(183.83, 42.6) * mm, "end": v(181.71, 40.49) * mm});
            skLineSegment(sketch, "E2010", {"start": v(181.71, 40.49) * mm, "end": v(180.81, 41.39) * mm});
            skLineSegment(sketch, "E2011", {"start": v(180.81, 41.39) * mm, "end": v(177.98, 38.56) * mm});
            skLineSegment(sketch, "E2012", {"start": v(177.98, 38.56) * mm, "end": v(178.88, 37.66) * mm});
            skLineSegment(sketch, "E2013", {"start": v(178.88, 37.66) * mm, "end": v(176.76, 35.54) * mm});
            skLineSegment(sketch, "E2014", {"start": v(176.76, 35.54) * mm, "end": v(179.03, 33.27) * mm});
            skLineSegment(sketch, "E2015", {"start": v(179.03, 33.27) * mm, "end": v(181.15, 35.4) * mm});
            skLineSegment(sketch, "E2016", {"start": v(181.15, 35.4) * mm, "end": v(182.05, 34.5) * mm});
            skLineSegment(sketch, "E2017", {"start": v(182.05, 34.5) * mm, "end": v(184.88, 37.32) * mm});
            skLineSegment(sketch, "E2018", {"start": v(184.88, 37.32) * mm, "end": v(183.98, 38.22) * mm});
            skLineSegment(sketch, "E2019", {"start": v(183.98, 38.22) * mm, "end": v(186.1, 40.35) * mm});
            skLineSegment(sketch, "E2020", {"start": v(186.1, 40.35) * mm, "end": v(189.73, 36.71) * mm});
            skArc(sketch, "E2021", {"start": v(189.86, 36.23) * mm, "mid": v(189.86, 36.5) * mm, "end": v(189.73, 36.71) * mm});
            skArc(sketch, "E2022", {"start": v(189.86, 36.23) * mm, "mid": v(190.34, 35.6) * mm, "end": v(190.82, 36.23) * mm});
            skArc(sketch, "E2023", {"start": v(190.95, 36.71) * mm, "mid": v(190.82, 36.5) * mm, "end": v(190.82, 36.23) * mm});
            skLineSegment(sketch, "E2024", {"start": v(190.95, 36.71) * mm, "end": v(192.1, 37.87) * mm});
            skArc(sketch, "E2025", {"start": v(192.82, 37.87) * mm, "mid": v(192.46, 38.02) * mm, "end": v(192.1, 37.87) * mm});
            skLineSegment(sketch, "E2026", {"start": v(192.82, 37.87) * mm, "end": v(196.35, 34.33) * mm});
            skArc(sketch, "E2027", {"start": v(196.35, 33.63) * mm, "mid": v(196.5, 33.98) * mm, "end": v(196.35, 34.33) * mm});
            skLineSegment(sketch, "E2028", {"start": v(196.35, 33.63) * mm, "end": v(195.2, 32.47) * mm});
            skArc(sketch, "E2029", {"start": v(194.71, 32.34) * mm, "mid": v(194.97, 32.34) * mm, "end": v(195.2, 32.47) * mm});
            skArc(sketch, "E2030", {"start": v(194.71, 32.34) * mm, "mid": v(194.08, 31.86) * mm, "end": v(194.71, 31.38) * mm});
            skArc(sketch, "E2031", {"start": v(195.2, 31.25) * mm, "mid": v(194.97, 31.38) * mm, "end": v(194.71, 31.38) * mm});
            skLineSegment(sketch, "E2032", {"start": v(195.2, 31.25) * mm, "end": v(202.36, 24.08) * mm});
            skArc(sketch, "E2033", {"start": v(202.65, 23.4) * mm, "mid": v(202.57, 23.77) * mm, "end": v(202.36, 24.08) * mm});
            skLineSegment(sketch, "E2034", {"start": v(202.65, 23.4) * mm, "end": v(202.67, -25.24) * mm});
            skLineSegment(sketch, "E2035", {"start": v(165.87, 51.6) * mm, "end": v(165.9, -53.46) * mm});
            skCircle(sketch, "E2036", {"center": v(236.95, -12.93) * mm, "radius": 1.6 * mm});
            skCircle(sketch, "E2037", {"center": v(236.95, 11.07) * mm, "radius": 1.6 * mm});
            skArc(sketch, "E2038", {"start": v(205.95, 27.13) * mm, "mid": v(205.45, 29.66) * mm, "end": v(204.02, 31.8) * mm});
            skLineSegment(sketch, "E2039", {"start": v(205.95, 27.13) * mm, "end": v(205.95, -29) * mm});
            skArc(sketch, "E2040", {"start": v(204.02, -33.67) * mm, "mid": v(205.45, -31.52) * mm, "end": v(205.95, -29) * mm});
            skArc(sketch, "E2041", {"start": v(173.22, 62.6) * mm, "mid": v(166.02, 64.03) * mm, "end": v(161.95, 57.93) * mm});
            skArc(sketch, "E2042", {"start": v(161.95, -59.8) * mm, "mid": v(166.02, -65.9) * mm, "end": v(173.22, -64.47) * mm});
            skLineSegment(sketch, "E2043", {"start": v(204.02, -33.67) * mm, "end": v(173.22, -64.47) * mm});
            skLineSegment(sketch, "E2044", {"start": v(173.22, 62.6) * mm, "end": v(204.02, 31.8) * mm});
            skLineSegment(sketch, "E2045", {"start": v(161.95, -59.8) * mm, "end": v(161.95, 57.93) * mm});
            skLineSegment(sketch, "E2046", {"start": v(271.95, 23.48) * mm, "end": v(279.1, 30.62) * mm});
            skArc(sketch, "E2047", {"start": v(279.58, 30.75) * mm, "mid": v(279.32, 30.75) * mm, "end": v(279.1, 30.62) * mm});
            skArc(sketch, "E2048", {"start": v(279.58, 30.75) * mm, "mid": v(280.2, 31.24) * mm, "end": v(279.58, 31.72) * mm});
            skArc(sketch, "E2049", {"start": v(279.1, 31.85) * mm, "mid": v(279.32, 31.72) * mm, "end": v(279.58, 31.72) * mm});
            skLineSegment(sketch, "E2050", {"start": v(279.1, 31.85) * mm, "end": v(277.94, 33) * mm});
            skArc(sketch, "E2051", {"start": v(277.94, 33.71) * mm, "mid": v(277.8, 33.36) * mm, "end": v(277.94, 33) * mm});
            skLineSegment(sketch, "E2052", {"start": v(277.94, 33.71) * mm, "end": v(281.47, 37.25) * mm});
            skArc(sketch, "E2053", {"start": v(282.18, 37.25) * mm, "mid": v(281.83, 37.4) * mm, "end": v(281.47, 37.25) * mm});
            skLineSegment(sketch, "E2054", {"start": v(282.18, 37.25) * mm, "end": v(283.34, 36.1) * mm});
            skArc(sketch, "E2055", {"start": v(283.47, 35.6) * mm, "mid": v(283.47, 35.87) * mm, "end": v(283.34, 36.1) * mm});
            skArc(sketch, "E2056", {"start": v(283.47, 35.6) * mm, "mid": v(283.95, 34.98) * mm, "end": v(284.43, 35.6) * mm});
            skArc(sketch, "E2057", {"start": v(284.56, 36.1) * mm, "mid": v(284.43, 35.87) * mm, "end": v(284.43, 35.6) * mm});
            skLineSegment(sketch, "E2058", {"start": v(284.56, 36.1) * mm, "end": v(288.2, 39.72) * mm});
            skLineSegment(sketch, "E2059", {"start": v(288.2, 39.72) * mm, "end": v(290.31, 37.6) * mm});
            skLineSegment(sketch, "E2060", {"start": v(290.31, 37.6) * mm, "end": v(289.41, 36.7) * mm});
            skLineSegment(sketch, "E2061", {"start": v(293.48, 40.77) * mm, "end": v(292.58, 39.86) * mm});
            skLineSegment(sketch, "E2062", {"start": v(292.58, 39.86) * mm, "end": v(290.45, 41.98) * mm});
            skLineSegment(sketch, "E2063", {"start": v(290.45, 41.98) * mm, "end": v(294.08, 45.62) * mm});
            skArc(sketch, "E2064", {"start": v(294.57, 45.74) * mm, "mid": v(294.3, 45.74) * mm, "end": v(294.08, 45.62) * mm});
            skArc(sketch, "E2065", {"start": v(294.57, 45.74) * mm, "mid": v(295.2, 46.23) * mm, "end": v(294.57, 46.71) * mm});
            skArc(sketch, "E2066", {"start": v(294.08, 46.84) * mm, "mid": v(294.3, 46.71) * mm, "end": v(294.57, 46.71) * mm});
            skLineSegment(sketch, "E2067", {"start": v(294.08, 46.84) * mm, "end": v(292.93, 48) * mm});
            skArc(sketch, "E2068", {"start": v(292.93, 48.7) * mm, "mid": v(292.78, 48.35) * mm, "end": v(292.93, 48) * mm});
            skLineSegment(sketch, "E2069", {"start": v(292.93, 48.7) * mm, "end": v(296.46, 52.24) * mm});
            skArc(sketch, "E2070", {"start": v(297.17, 52.24) * mm, "mid": v(296.82, 52.38) * mm, "end": v(296.46, 52.24) * mm});
            skLineSegment(sketch, "E2071", {"start": v(297.17, 52.24) * mm, "end": v(298.33, 51.08) * mm});
            skArc(sketch, "E2072", {"start": v(298.46, 50.6) * mm, "mid": v(298.46, 50.86) * mm, "end": v(298.33, 51.08) * mm});
            skArc(sketch, "E2073", {"start": v(298.46, 50.6) * mm, "mid": v(298.94, 49.97) * mm, "end": v(299.42, 50.6) * mm});
            skArc(sketch, "E2074", {"start": v(299.55, 51.08) * mm, "mid": v(299.42, 50.86) * mm, "end": v(299.42, 50.6) * mm});
            skLineSegment(sketch, "E2075", {"start": v(299.55, 51.08) * mm, "end": v(305.59, 57.12) * mm});
            skLineSegment(sketch, "E2076", {"start": v(305.59, 57.12) * mm, "end": v(306.07, 56.63) * mm});
            skLineSegment(sketch, "E2077", {"start": v(289.41, 36.7) * mm, "end": v(292.24, 33.87) * mm});
            skLineSegment(sketch, "E2078", {"start": v(292.24, 33.87) * mm, "end": v(293.14, 34.77) * mm});
            skLineSegment(sketch, "E2079", {"start": v(293.14, 34.77) * mm, "end": v(295.26, 32.65) * mm});
            skLineSegment(sketch, "E2080", {"start": v(295.26, 32.65) * mm, "end": v(297.53, 34.91) * mm});
            skLineSegment(sketch, "E2081", {"start": v(297.53, 34.91) * mm, "end": v(295.4, 37.04) * mm});
            skLineSegment(sketch, "E2082", {"start": v(295.4, 37.04) * mm, "end": v(296.3, 37.94) * mm});
            skLineSegment(sketch, "E2083", {"start": v(296.3, 37.94) * mm, "end": v(293.48, 40.77) * mm});
            skArc(sketch, "E2084", {"start": v(308.41, 50.97) * mm, "mid": v(307.8, 54.04) * mm, "end": v(306.07, 56.63) * mm});
            skArc(sketch, "E2085", {"start": v(271.95, 23.48) * mm, "mid": v(271.73, 23.14) * mm, "end": v(271.66, 22.75) * mm});
            skArc(sketch, "E2086", {"start": v(306.1, -59.74) * mm, "mid": v(307.84, -57.15) * mm, "end": v(308.45, -54.09) * mm});
            skLineSegment(sketch, "E2087", {"start": v(306.1, -59.74) * mm, "end": v(305.62, -60.23) * mm});
            skLineSegment(sketch, "E2088", {"start": v(305.62, -60.23) * mm, "end": v(299.59, -54.2) * mm});
            skArc(sketch, "E2089", {"start": v(299.46, -53.7) * mm, "mid": v(299.46, -53.97) * mm, "end": v(299.59, -54.2) * mm});
            skArc(sketch, "E2090", {"start": v(299.46, -53.7) * mm, "mid": v(298.97, -53.08) * mm, "end": v(298.5, -53.7) * mm});
            skArc(sketch, "E2091", {"start": v(298.36, -54.2) * mm, "mid": v(298.5, -53.97) * mm, "end": v(298.5, -53.7) * mm});
            skLineSegment(sketch, "E2092", {"start": v(298.36, -54.2) * mm, "end": v(297.2, -55.35) * mm});
            skArc(sketch, "E2093", {"start": v(296.5, -55.35) * mm, "mid": v(296.85, -55.5) * mm, "end": v(297.2, -55.35) * mm});
            skLineSegment(sketch, "E2094", {"start": v(296.5, -55.35) * mm, "end": v(292.96, -51.81) * mm});
            skArc(sketch, "E2095", {"start": v(292.96, -51.1) * mm, "mid": v(292.82, -51.46) * mm, "end": v(292.96, -51.81) * mm});
            skLineSegment(sketch, "E2096", {"start": v(292.96, -51.1) * mm, "end": v(294.12, -49.95) * mm});
            skArc(sketch, "E2097", {"start": v(294.6, -49.82) * mm, "mid": v(294.34, -49.82) * mm, "end": v(294.12, -49.95) * mm});
            skArc(sketch, "E2098", {"start": v(294.6, -49.82) * mm, "mid": v(295.23, -49.34) * mm, "end": v(294.6, -48.85) * mm});
            skArc(sketch, "E2099", {"start": v(294.12, -48.73) * mm, "mid": v(294.34, -48.85) * mm, "end": v(294.6, -48.85) * mm});
            skLineSegment(sketch, "E2100", {"start": v(294.12, -48.73) * mm, "end": v(290.49, -45.1) * mm});
            skLineSegment(sketch, "E2101", {"start": v(290.49, -45.1) * mm, "end": v(292.61, -42.97) * mm});
            skLineSegment(sketch, "E2102", {"start": v(292.61, -42.97) * mm, "end": v(293.51, -43.88) * mm});
            skLineSegment(sketch, "E2103", {"start": v(293.51, -43.88) * mm, "end": v(296.34, -41.05) * mm});
            skLineSegment(sketch, "E2104", {"start": v(296.34, -41.05) * mm, "end": v(295.44, -40.15) * mm});
            skLineSegment(sketch, "E2105", {"start": v(295.44, -40.15) * mm, "end": v(297.56, -38.02) * mm});
            skLineSegment(sketch, "E2106", {"start": v(297.56, -38.02) * mm, "end": v(295.3, -35.76) * mm});
            skLineSegment(sketch, "E2107", {"start": v(295.3, -35.76) * mm, "end": v(293.18, -37.88) * mm});
            skLineSegment(sketch, "E2108", {"start": v(293.18, -37.88) * mm, "end": v(292.28, -36.98) * mm});
            skLineSegment(sketch, "E2109", {"start": v(292.28, -36.98) * mm, "end": v(289.45, -39.8) * mm});
            skLineSegment(sketch, "E2110", {"start": v(289.45, -39.8) * mm, "end": v(290.35, -40.71) * mm});
            skLineSegment(sketch, "E2111", {"start": v(290.35, -40.71) * mm, "end": v(288.23, -42.83) * mm});
            skLineSegment(sketch, "E2112", {"start": v(288.23, -42.83) * mm, "end": v(284.6, -39.2) * mm});
            skArc(sketch, "E2113", {"start": v(284.47, -38.72) * mm, "mid": v(284.47, -38.98) * mm, "end": v(284.6, -39.2) * mm});
            skArc(sketch, "E2114", {"start": v(284.47, -38.72) * mm, "mid": v(283.98, -38.09) * mm, "end": v(283.5, -38.72) * mm});
            skArc(sketch, "E2115", {"start": v(283.37, -39.2) * mm, "mid": v(283.5, -38.98) * mm, "end": v(283.5, -38.72) * mm});
            skLineSegment(sketch, "E2116", {"start": v(283.37, -39.2) * mm, "end": v(282.22, -40.36) * mm});
            skArc(sketch, "E2117", {"start": v(281.5, -40.36) * mm, "mid": v(281.86, -40.5) * mm, "end": v(282.22, -40.36) * mm});
            skLineSegment(sketch, "E2118", {"start": v(281.5, -40.36) * mm, "end": v(277.97, -36.82) * mm});
            skArc(sketch, "E2119", {"start": v(277.97, -36.12) * mm, "mid": v(277.83, -36.47) * mm, "end": v(277.97, -36.82) * mm});
            skLineSegment(sketch, "E2120", {"start": v(277.97, -36.12) * mm, "end": v(279.13, -34.96) * mm});
            skArc(sketch, "E2121", {"start": v(279.61, -34.83) * mm, "mid": v(279.35, -34.83) * mm, "end": v(279.13, -34.96) * mm});
            skArc(sketch, "E2122", {"start": v(279.61, -34.83) * mm, "mid": v(280.24, -34.35) * mm, "end": v(279.61, -33.86) * mm});
            skArc(sketch, "E2123", {"start": v(279.13, -33.73) * mm, "mid": v(279.35, -33.86) * mm, "end": v(279.61, -33.86) * mm});
            skLineSegment(sketch, "E2124", {"start": v(279.13, -33.73) * mm, "end": v(271.96, -26.57) * mm});
            skArc(sketch, "E2125", {"start": v(271.67, -25.89) * mm, "mid": v(271.75, -26.26) * mm, "end": v(271.96, -26.57) * mm});
            skLineSegment(sketch, "E2126", {"start": v(271.67, -25.89) * mm, "end": v(271.66, 22.75) * mm});
            skLineSegment(sketch, "E2127", {"start": v(308.45, -54.09) * mm, "end": v(308.41, 50.97) * mm});
            skLineSegment(sketch, "E2128", {"start": v(190.2, 105.31) * mm, "end": v(175.7, 90.83) * mm});
            skArc(sketch, "E2129", {"start": v(171.46, 89.07) * mm, "mid": v(173.76, 89.52) * mm, "end": v(175.7, 90.83) * mm});
            skArc(sketch, "E2130", {"start": v(298.2, 90.82) * mm, "mid": v(300.14, 89.52) * mm, "end": v(302.43, 89.07) * mm});
            skLineSegment(sketch, "E2131", {"start": v(298.2, 90.82) * mm, "end": v(283.7, 105.31) * mm});
            skArc(sketch, "E2132", {"start": v(283.7, 105.31) * mm, "mid": v(281.76, 106.61) * mm, "end": v(279.46, 107.07) * mm});
            skLineSegment(sketch, "E2133", {"start": v(279.46, 107.07) * mm, "end": v(262.43, 107.07) * mm});
            skArc(sketch, "E2134", {"start": v(262.43, 107.07) * mm, "mid": v(260.14, 106.61) * mm, "end": v(258.2, 105.31) * mm});
            skLineSegment(sketch, "E2135", {"start": v(258.2, 105.31) * mm, "end": v(243.7, 90.82) * mm});
            skArc(sketch, "E2136", {"start": v(239.46, 89.07) * mm, "mid": v(241.76, 89.52) * mm, "end": v(243.7, 90.82) * mm});
            skLineSegment(sketch, "E2137", {"start": v(239.46, 89.07) * mm, "end": v(234.43, 89.07) * mm});
            skArc(sketch, "E2138", {"start": v(230.2, 90.83) * mm, "mid": v(232.14, 89.52) * mm, "end": v(234.43, 89.07) * mm});
            skLineSegment(sketch, "E2139", {"start": v(230.2, 90.83) * mm, "end": v(215.7, 105.31) * mm});
            skArc(sketch, "E2140", {"start": v(215.7, 105.31) * mm, "mid": v(213.76, 106.61) * mm, "end": v(211.46, 107.07) * mm});
            skLineSegment(sketch, "E2141", {"start": v(211.46, 107.07) * mm, "end": v(194.43, 107.07) * mm});
            skArc(sketch, "E2142", {"start": v(194.43, 107.07) * mm, "mid": v(192.14, 106.61) * mm, "end": v(190.2, 105.31) * mm});
            skArc(sketch, "E2143", {"start": v(243.7, 77.31) * mm, "mid": v(241.76, 78.61) * mm, "end": v(239.46, 79.07) * mm});
            skLineSegment(sketch, "E2144", {"start": v(239.46, 79.07) * mm, "end": v(234.43, 79.07) * mm});
            skArc(sketch, "E2145", {"start": v(234.43, 79.07) * mm, "mid": v(232.14, 78.61) * mm, "end": v(230.2, 77.31) * mm});
            skLineSegment(sketch, "E2146", {"start": v(284, 87.7) * mm, "end": v(284, 80.43) * mm});
            skLineSegment(sketch, "E2147", {"start": v(190.76, 88.57) * mm, "end": v(213.13, 88.57) * mm});
            skArc(sketch, "E2148", {"start": v(213.13, 88.57) * mm, "mid": v(213.38, 88.63) * mm, "end": v(213.57, 88.82) * mm});
            skArc(sketch, "E2149", {"start": v(214.25, 88.13) * mm, "mid": v(214.35, 88.92) * mm, "end": v(213.57, 88.82) * mm});
            skArc(sketch, "E2150", {"start": v(214.25, 88.13) * mm, "mid": v(214.07, 87.95) * mm, "end": v(214, 87.7) * mm});
            skLineSegment(sketch, "E2151", {"start": v(214, 87.7) * mm, "end": v(214, 80.43) * mm});
            skArc(sketch, "E2152", {"start": v(214, 80.43) * mm, "mid": v(214.07, 80.18) * mm, "end": v(214.25, 80) * mm});
            skArc(sketch, "E2153", {"start": v(213.57, 79.32) * mm, "mid": v(214.35, 79.21) * mm, "end": v(214.25, 80) * mm});
            skArc(sketch, "E2154", {"start": v(213.57, 79.32) * mm, "mid": v(213.38, 79.5) * mm, "end": v(213.13, 79.57) * mm});
            skLineSegment(sketch, "E2155", {"start": v(213.13, 79.57) * mm, "end": v(190.76, 79.57) * mm});
            skArc(sketch, "E2156", {"start": v(190.76, 79.57) * mm, "mid": v(190.51, 79.5) * mm, "end": v(190.33, 79.32) * mm});
            skArc(sketch, "E2157", {"start": v(189.65, 80) * mm, "mid": v(189.54, 79.21) * mm, "end": v(190.33, 79.32) * mm});
            skArc(sketch, "E2158", {"start": v(189.65, 80) * mm, "mid": v(189.83, 80.18) * mm, "end": v(189.9, 80.43) * mm});
            skLineSegment(sketch, "E2159", {"start": v(189.9, 80.43) * mm, "end": v(189.9, 87.7) * mm});
            skArc(sketch, "E2160", {"start": v(189.9, 87.7) * mm, "mid": v(189.83, 87.95) * mm, "end": v(189.65, 88.13) * mm});
            skArc(sketch, "E2161", {"start": v(190.33, 88.82) * mm, "mid": v(189.54, 88.92) * mm, "end": v(189.65, 88.13) * mm});
            skArc(sketch, "E2162", {"start": v(190.33, 88.82) * mm, "mid": v(190.51, 88.63) * mm, "end": v(190.76, 88.57) * mm});
            skCircle(sketch, "E2163", {"center": v(271.95, 99.07) * mm, "radius": 1.6 * mm});
            skCircle(sketch, "E2164", {"center": v(201.95, 99.07) * mm, "radius": 1.6 * mm});
            skLineSegment(sketch, "E2165", {"start": v(260.76, 88.57) * mm, "end": v(283.13, 88.57) * mm});
            skArc(sketch, "E2166", {"start": v(283.13, 88.57) * mm, "mid": v(283.38, 88.63) * mm, "end": v(283.57, 88.82) * mm});
            skArc(sketch, "E2167", {"start": v(284.25, 88.13) * mm, "mid": v(284.35, 88.92) * mm, "end": v(283.57, 88.82) * mm});
            skArc(sketch, "E2168", {"start": v(284.25, 88.13) * mm, "mid": v(284.07, 87.95) * mm, "end": v(284, 87.7) * mm});
            skArc(sketch, "E2169", {"start": v(284, 80.43) * mm, "mid": v(284.07, 80.18) * mm, "end": v(284.25, 80) * mm});
            skArc(sketch, "E2170", {"start": v(283.57, 79.32) * mm, "mid": v(284.35, 79.21) * mm, "end": v(284.25, 80) * mm});
            skArc(sketch, "E2171", {"start": v(283.57, 79.32) * mm, "mid": v(283.38, 79.5) * mm, "end": v(283.13, 79.57) * mm});
            skLineSegment(sketch, "E2172", {"start": v(283.13, 79.57) * mm, "end": v(260.76, 79.57) * mm});
            skArc(sketch, "E2173", {"start": v(260.76, 79.57) * mm, "mid": v(260.51, 79.5) * mm, "end": v(260.33, 79.32) * mm});
            skArc(sketch, "E2174", {"start": v(259.65, 80) * mm, "mid": v(259.54, 79.21) * mm, "end": v(260.33, 79.32) * mm});
            skArc(sketch, "E2175", {"start": v(259.65, 80) * mm, "mid": v(259.83, 80.18) * mm, "end": v(259.9, 80.43) * mm});
            skLineSegment(sketch, "E2176", {"start": v(259.9, 80.43) * mm, "end": v(259.9, 87.7) * mm});
            skArc(sketch, "E2177", {"start": v(259.9, 87.7) * mm, "mid": v(259.83, 87.95) * mm, "end": v(259.65, 88.13) * mm});
            skArc(sketch, "E2178", {"start": v(260.33, 88.82) * mm, "mid": v(259.54, 88.92) * mm, "end": v(259.65, 88.13) * mm});
            skArc(sketch, "E2179", {"start": v(260.33, 88.82) * mm, "mid": v(260.51, 88.63) * mm, "end": v(260.76, 88.57) * mm});
            skLineSegment(sketch, "E2180", {"start": v(230.2, 77.31) * mm, "end": v(213.7, 60.83) * mm});
            skArc(sketch, "E2181", {"start": v(213.7, 60.83) * mm, "mid": v(212.4, 58.88) * mm, "end": v(211.95, 56.58) * mm});
            skArc(sketch, "E2182", {"start": v(261.95, 56.58) * mm, "mid": v(261.5, 58.88) * mm, "end": v(260.2, 60.82) * mm});
            skLineSegment(sketch, "E2183", {"start": v(260.2, 60.82) * mm, "end": v(243.7, 77.31) * mm});
            skCircle(sketch, "E2184", {"center": v(271.95, 69.07) * mm, "radius": 1.6 * mm});
            skCircle(sketch, "E2185", {"center": v(201.95, 69.07) * mm, "radius": 1.6 * mm});
            skLineSegment(sketch, "E2186", {"start": v(211.95, 56.58) * mm, "end": v(211.95, 41.55) * mm});
            skLineSegment(sketch, "E2187", {"start": v(261.95, 41.55) * mm, "end": v(261.95, 56.58) * mm});
            skLineSegment(sketch, "E2188", {"start": v(171.46, 89.07) * mm, "end": v(156.43, 89.07) * mm});
            skLineSegment(sketch, "E2189", {"start": v(317.46, 89.07) * mm, "end": v(302.43, 89.07) * mm});
            skArc(sketch, "E2190", {"start": v(317.46, 89.07) * mm, "mid": v(319.76, 89.52) * mm, "end": v(321.7, 90.82) * mm});
            skArc(sketch, "E2191", {"start": v(152.2, 90.83) * mm, "mid": v(154.14, 89.52) * mm, "end": v(156.43, 89.07) * mm});
            skLineSegment(sketch, "E2192", {"start": v(321.95, -76.45) * mm, "end": v(321.95, -15.88) * mm});
            skLineSegment(sketch, "E2193", {"start": v(321.95, -15.88) * mm, "end": v(321.95, 14.02) * mm});
            skLineSegment(sketch, "E2194", {"start": v(390.95, 118.18) * mm, "end": v(391.17, 118.38) * mm});
            skCircle(sketch, "E2195", {"center": v(382.81, 79.01) * mm, "radius": 2 * mm});
            skCircle(sketch, "E2196", {"center": v(343.47, 29.85) * mm, "radius": 2 * mm});
            skCircle(sketch, "E2197", {"center": v(380.68, -22.72) * mm, "radius": 2 * mm});
            skCircle(sketch, "E2198", {"center": v(343.03, -75.42) * mm, "radius": 2 * mm});
            skCircle(sketch, "E2199", {"center": v(171.7, 43.74) * mm, "radius": 2 * mm});
            skCircle(sketch, "E2200", {"center": v(302.59, 43.12) * mm, "radius": 2 * mm});
            skArc(sketch, "E2201", {"start": v(-247.45, 34.67) * mm, "mid": v(-247.63, 34.85) * mm, "end": v(-247.88, 34.92) * mm});
            skArc(sketch, "E2202", {"start": v(-247.45, 34.67) * mm, "mid": v(-246.66, 34.57) * mm, "end": v(-246.76, 35.35) * mm});
            skArc(sketch, "E2203", {"start": v(-247.01, 35.79) * mm, "mid": v(-246.95, 35.54) * mm, "end": v(-246.76, 35.35) * mm});
            skLineSegment(sketch, "E2204", {"start": v(-247.01, 35.79) * mm, "end": v(-247.01, 40.26) * mm});
            skArc(sketch, "E2205", {"start": v(-246.76, 40.69) * mm, "mid": v(-246.95, 40.5) * mm, "end": v(-247.01, 40.26) * mm});
            skArc(sketch, "E2206", {"start": v(-246.76, 40.69) * mm, "mid": v(-246.66, 41.48) * mm, "end": v(-247.45, 41.37) * mm});
            skArc(sketch, "E2207", {"start": v(-247.88, 41.12) * mm, "mid": v(-247.63, 41.19) * mm, "end": v(-247.45, 41.37) * mm});
            skLineSegment(sketch, "E2208", {"start": v(-247.88, 41.12) * mm, "end": v(-249.45, 41.12) * mm});
            skArc(sketch, "E2209", {"start": v(-249.88, 41.37) * mm, "mid": v(-249.7, 41.19) * mm, "end": v(-249.45, 41.12) * mm});
            skArc(sketch, "E2210", {"start": v(-249.88, 41.37) * mm, "mid": v(-250.67, 41.48) * mm, "end": v(-250.56, 40.69) * mm});
            skArc(sketch, "E2211", {"start": v(-250.31, 40.26) * mm, "mid": v(-250.38, 40.5) * mm, "end": v(-250.56, 40.69) * mm});
            skLineSegment(sketch, "E2212", {"start": v(-250.31, 40.26) * mm, "end": v(-250.31, 35.79) * mm});
            skArc(sketch, "E2213", {"start": v(-250.56, 35.35) * mm, "mid": v(-250.38, 35.54) * mm, "end": v(-250.31, 35.79) * mm});
            skArc(sketch, "E2214", {"start": v(-250.56, 35.35) * mm, "mid": v(-250.67, 34.57) * mm, "end": v(-249.88, 34.67) * mm});
            skArc(sketch, "E2215", {"start": v(-249.45, 34.92) * mm, "mid": v(-249.7, 34.85) * mm, "end": v(-249.88, 34.67) * mm});
            skLineSegment(sketch, "E2216", {"start": v(-249.45, 34.92) * mm, "end": v(-247.88, 34.92) * mm});
            skArc(sketch, "E2217", {"start": v(-247.45, 13.47) * mm, "mid": v(-247.63, 13.65) * mm, "end": v(-247.88, 13.72) * mm});
            skArc(sketch, "E2218", {"start": v(-247.45, 13.47) * mm, "mid": v(-246.66, 13.37) * mm, "end": v(-246.76, 14.15) * mm});
            skArc(sketch, "E2219", {"start": v(-247.01, 14.59) * mm, "mid": v(-246.95, 14.34) * mm, "end": v(-246.76, 14.15) * mm});
            skLineSegment(sketch, "E2220", {"start": v(-247.01, 14.59) * mm, "end": v(-247.01, 19.06) * mm});
            skArc(sketch, "E2221", {"start": v(-246.76, 19.49) * mm, "mid": v(-246.95, 19.3) * mm, "end": v(-247.01, 19.06) * mm});
            skArc(sketch, "E2222", {"start": v(-246.76, 19.49) * mm, "mid": v(-246.66, 20.28) * mm, "end": v(-247.45, 20.17) * mm});
            skArc(sketch, "E2223", {"start": v(-247.88, 19.92) * mm, "mid": v(-247.63, 19.99) * mm, "end": v(-247.45, 20.17) * mm});
            skLineSegment(sketch, "E2224", {"start": v(-247.88, 19.92) * mm, "end": v(-249.45, 19.92) * mm});
            skArc(sketch, "E2225", {"start": v(-249.88, 20.17) * mm, "mid": v(-249.7, 19.99) * mm, "end": v(-249.45, 19.92) * mm});
            skArc(sketch, "E2226", {"start": v(-249.88, 20.17) * mm, "mid": v(-250.67, 20.28) * mm, "end": v(-250.56, 19.49) * mm});
            skArc(sketch, "E2227", {"start": v(-250.31, 19.06) * mm, "mid": v(-250.38, 19.3) * mm, "end": v(-250.56, 19.49) * mm});
            skLineSegment(sketch, "E2228", {"start": v(-250.31, 19.06) * mm, "end": v(-250.31, 14.59) * mm});
            skArc(sketch, "E2229", {"start": v(-250.56, 14.15) * mm, "mid": v(-250.38, 14.34) * mm, "end": v(-250.31, 14.59) * mm});
            skArc(sketch, "E2230", {"start": v(-250.56, 14.15) * mm, "mid": v(-250.67, 13.37) * mm, "end": v(-249.88, 13.47) * mm});
            skArc(sketch, "E2231", {"start": v(-249.45, 13.72) * mm, "mid": v(-249.7, 13.65) * mm, "end": v(-249.88, 13.47) * mm});
            skLineSegment(sketch, "E2232", {"start": v(-249.45, 13.72) * mm, "end": v(-247.88, 13.72) * mm});
            skCircle(sketch, "E2233", {"center": v(-248.66, 27.42) * mm, "radius": 1.6 * mm});
            skArc(sketch, "E2234", {"start": v(-260.55, -21.65) * mm, "mid": v(-260.8, -21.72) * mm, "end": v(-260.98, -21.9) * mm});
            skArc(sketch, "E2235", {"start": v(-261.66, -21.22) * mm, "mid": v(-261.77, -22) * mm, "end": v(-260.98, -21.9) * mm});
            skArc(sketch, "E2236", {"start": v(-261.66, -21.22) * mm, "mid": v(-261.48, -21.04) * mm, "end": v(-261.41, -20.79) * mm});
            skLineSegment(sketch, "E2237", {"start": v(-261.41, -20.79) * mm, "end": v(-261.41, -16.32) * mm});
            skArc(sketch, "E2238", {"start": v(-261.41, -16.32) * mm, "mid": v(-261.48, -16.07) * mm, "end": v(-261.66, -15.89) * mm});
            skArc(sketch, "E2239", {"start": v(-260.98, -15.2) * mm, "mid": v(-261.77, -15.1) * mm, "end": v(-261.66, -15.89) * mm});
            skArc(sketch, "E2240", {"start": v(-260.98, -15.2) * mm, "mid": v(-260.8, -15.39) * mm, "end": v(-260.55, -15.45) * mm});
            skLineSegment(sketch, "E2241", {"start": v(-260.55, -15.45) * mm, "end": v(-258.98, -15.45) * mm});
            skArc(sketch, "E2242", {"start": v(-258.98, -15.45) * mm, "mid": v(-258.73, -15.39) * mm, "end": v(-258.55, -15.2) * mm});
            skArc(sketch, "E2243", {"start": v(-257.86, -15.89) * mm, "mid": v(-257.76, -15.1) * mm, "end": v(-258.55, -15.2) * mm});
            skArc(sketch, "E2244", {"start": v(-257.86, -15.89) * mm, "mid": v(-258.05, -16.07) * mm, "end": v(-258.11, -16.32) * mm});
            skLineSegment(sketch, "E2245", {"start": v(-258.11, -16.32) * mm, "end": v(-258.11, -20.79) * mm});
            skArc(sketch, "E2246", {"start": v(-258.11, -20.79) * mm, "mid": v(-258.05, -21.04) * mm, "end": v(-257.86, -21.22) * mm});
            skArc(sketch, "E2247", {"start": v(-258.55, -21.9) * mm, "mid": v(-257.76, -22) * mm, "end": v(-257.86, -21.22) * mm});
            skArc(sketch, "E2248", {"start": v(-258.55, -21.9) * mm, "mid": v(-258.73, -21.72) * mm, "end": v(-258.98, -21.65) * mm});
            skLineSegment(sketch, "E2249", {"start": v(-258.98, -21.65) * mm, "end": v(-260.55, -21.65) * mm});
            skArc(sketch, "E2250", {"start": v(-260.55, -42.85) * mm, "mid": v(-260.8, -42.92) * mm, "end": v(-260.98, -43.1) * mm});
            skArc(sketch, "E2251", {"start": v(-261.66, -42.42) * mm, "mid": v(-261.77, -43.2) * mm, "end": v(-260.98, -43.1) * mm});
            skArc(sketch, "E2252", {"start": v(-261.66, -42.42) * mm, "mid": v(-261.48, -42.24) * mm, "end": v(-261.41, -41.99) * mm});
            skLineSegment(sketch, "E2253", {"start": v(-261.41, -41.99) * mm, "end": v(-261.41, -37.52) * mm});
            skArc(sketch, "E2254", {"start": v(-261.41, -37.52) * mm, "mid": v(-261.48, -37.27) * mm, "end": v(-261.66, -37.09) * mm});
            skArc(sketch, "E2255", {"start": v(-260.98, -36.4) * mm, "mid": v(-261.77, -36.3) * mm, "end": v(-261.66, -37.09) * mm});
            skArc(sketch, "E2256", {"start": v(-260.98, -36.4) * mm, "mid": v(-260.8, -36.59) * mm, "end": v(-260.55, -36.65) * mm});
            skLineSegment(sketch, "E2257", {"start": v(-260.55, -36.65) * mm, "end": v(-258.98, -36.65) * mm});
            skArc(sketch, "E2258", {"start": v(-258.98, -36.65) * mm, "mid": v(-258.73, -36.59) * mm, "end": v(-258.55, -36.4) * mm});
            skArc(sketch, "E2259", {"start": v(-257.86, -37.09) * mm, "mid": v(-257.76, -36.3) * mm, "end": v(-258.55, -36.4) * mm});
            skArc(sketch, "E2260", {"start": v(-257.86, -37.09) * mm, "mid": v(-258.05, -37.27) * mm, "end": v(-258.11, -37.52) * mm});
            skLineSegment(sketch, "E2261", {"start": v(-258.11, -37.52) * mm, "end": v(-258.11, -41.99) * mm});
            skArc(sketch, "E2262", {"start": v(-258.11, -41.99) * mm, "mid": v(-258.05, -42.24) * mm, "end": v(-257.86, -42.42) * mm});
            skArc(sketch, "E2263", {"start": v(-258.55, -43.1) * mm, "mid": v(-257.76, -43.2) * mm, "end": v(-257.86, -42.42) * mm});
            skArc(sketch, "E2264", {"start": v(-258.55, -43.1) * mm, "mid": v(-258.73, -42.92) * mm, "end": v(-258.98, -42.85) * mm});
            skLineSegment(sketch, "E2265", {"start": v(-258.98, -42.85) * mm, "end": v(-260.55, -42.85) * mm});
            skCircle(sketch, "E2266", {"center": v(-259.76, -29.15) * mm, "radius": 1.6 * mm});
            skArc(sketch, "E2267", {"start": v(-247.45, -21.9) * mm, "mid": v(-247.63, -21.72) * mm, "end": v(-247.88, -21.65) * mm});
            skArc(sketch, "E2268", {"start": v(-247.45, -21.9) * mm, "mid": v(-246.66, -22) * mm, "end": v(-246.76, -21.22) * mm});
            skArc(sketch, "E2269", {"start": v(-247.01, -20.79) * mm, "mid": v(-246.95, -21.04) * mm, "end": v(-246.76, -21.22) * mm});
            skLineSegment(sketch, "E2270", {"start": v(-247.01, -20.79) * mm, "end": v(-247.01, -16.32) * mm});
            skArc(sketch, "E2271", {"start": v(-246.76, -15.89) * mm, "mid": v(-246.95, -16.07) * mm, "end": v(-247.01, -16.32) * mm});
            skArc(sketch, "E2272", {"start": v(-246.76, -15.89) * mm, "mid": v(-246.66, -15.1) * mm, "end": v(-247.45, -15.2) * mm});
            skArc(sketch, "E2273", {"start": v(-247.88, -15.45) * mm, "mid": v(-247.63, -15.39) * mm, "end": v(-247.45, -15.2) * mm});
            skLineSegment(sketch, "E2274", {"start": v(-247.88, -15.45) * mm, "end": v(-249.45, -15.45) * mm});
            skArc(sketch, "E2275", {"start": v(-249.88, -15.2) * mm, "mid": v(-249.7, -15.39) * mm, "end": v(-249.45, -15.45) * mm});
            skArc(sketch, "E2276", {"start": v(-249.88, -15.2) * mm, "mid": v(-250.67, -15.1) * mm, "end": v(-250.56, -15.89) * mm});
            skArc(sketch, "E2277", {"start": v(-250.31, -16.32) * mm, "mid": v(-250.38, -16.07) * mm, "end": v(-250.56, -15.89) * mm});
            skLineSegment(sketch, "E2278", {"start": v(-250.31, -16.32) * mm, "end": v(-250.31, -20.79) * mm});
            skArc(sketch, "E2279", {"start": v(-250.56, -21.22) * mm, "mid": v(-250.38, -21.04) * mm, "end": v(-250.31, -20.79) * mm});
            skArc(sketch, "E2280", {"start": v(-250.56, -21.22) * mm, "mid": v(-250.67, -22) * mm, "end": v(-249.88, -21.9) * mm});
            skArc(sketch, "E2281", {"start": v(-249.45, -21.65) * mm, "mid": v(-249.7, -21.72) * mm, "end": v(-249.88, -21.9) * mm});
            skLineSegment(sketch, "E2282", {"start": v(-249.45, -21.65) * mm, "end": v(-247.88, -21.65) * mm});
            skArc(sketch, "E2283", {"start": v(-247.45, -43.1) * mm, "mid": v(-247.63, -42.92) * mm, "end": v(-247.88, -42.85) * mm});
            skArc(sketch, "E2284", {"start": v(-247.45, -43.1) * mm, "mid": v(-246.66, -43.2) * mm, "end": v(-246.76, -42.42) * mm});
            skArc(sketch, "E2285", {"start": v(-247.01, -41.99) * mm, "mid": v(-246.95, -42.24) * mm, "end": v(-246.76, -42.42) * mm});
            skLineSegment(sketch, "E2286", {"start": v(-247.01, -41.99) * mm, "end": v(-247.01, -37.52) * mm});
            skArc(sketch, "E2287", {"start": v(-246.76, -37.09) * mm, "mid": v(-246.95, -37.27) * mm, "end": v(-247.01, -37.52) * mm});
            skArc(sketch, "E2288", {"start": v(-246.76, -37.09) * mm, "mid": v(-246.66, -36.3) * mm, "end": v(-247.45, -36.4) * mm});
            skArc(sketch, "E2289", {"start": v(-247.88, -36.65) * mm, "mid": v(-247.63, -36.59) * mm, "end": v(-247.45, -36.4) * mm});
            skLineSegment(sketch, "E2290", {"start": v(-247.88, -36.65) * mm, "end": v(-249.45, -36.65) * mm});
            skArc(sketch, "E2291", {"start": v(-249.88, -36.4) * mm, "mid": v(-249.7, -36.59) * mm, "end": v(-249.45, -36.65) * mm});
            skArc(sketch, "E2292", {"start": v(-249.88, -36.4) * mm, "mid": v(-250.67, -36.3) * mm, "end": v(-250.56, -37.09) * mm});
            skArc(sketch, "E2293", {"start": v(-250.31, -37.52) * mm, "mid": v(-250.38, -37.27) * mm, "end": v(-250.56, -37.09) * mm});
            skLineSegment(sketch, "E2294", {"start": v(-250.31, -37.52) * mm, "end": v(-250.31, -41.99) * mm});
            skArc(sketch, "E2295", {"start": v(-250.56, -42.42) * mm, "mid": v(-250.38, -42.24) * mm, "end": v(-250.31, -41.99) * mm});
            skArc(sketch, "E2296", {"start": v(-250.56, -42.42) * mm, "mid": v(-250.67, -43.2) * mm, "end": v(-249.88, -43.1) * mm});
            skArc(sketch, "E2297", {"start": v(-249.45, -42.85) * mm, "mid": v(-249.7, -42.92) * mm, "end": v(-249.88, -43.1) * mm});
            skLineSegment(sketch, "E2298", {"start": v(-249.45, -42.85) * mm, "end": v(-247.88, -42.85) * mm});
            skCircle(sketch, "E2299", {"center": v(-248.66, -29.15) * mm, "radius": 1.6 * mm});
            skArc(sketch, "E2300", {"start": v(91.82, -79.22) * mm, "mid": v(91.75, -78.97) * mm, "end": v(91.57, -78.78) * mm});
            skArc(sketch, "E2301", {"start": v(92.25, -78.1) * mm, "mid": v(91.46, -78) * mm, "end": v(91.57, -78.78) * mm});
            skArc(sketch, "E2302", {"start": v(92.25, -78.1) * mm, "mid": v(92.43, -78.28) * mm, "end": v(92.68, -78.35) * mm});
            skLineSegment(sketch, "E2303", {"start": v(92.68, -78.35) * mm, "end": v(97.15, -78.35) * mm});
            skArc(sketch, "E2304", {"start": v(97.15, -78.35) * mm, "mid": v(97.4, -78.28) * mm, "end": v(97.58, -78.1) * mm});
            skArc(sketch, "E2305", {"start": v(98.27, -78.78) * mm, "mid": v(98.37, -78) * mm, "end": v(97.58, -78.1) * mm});
            skArc(sketch, "E2306", {"start": v(98.27, -78.78) * mm, "mid": v(98.08, -78.97) * mm, "end": v(98.02, -79.22) * mm});
            skLineSegment(sketch, "E2307", {"start": v(98.02, -79.22) * mm, "end": v(98.02, -80.78) * mm});
            skArc(sketch, "E2308", {"start": v(98.02, -80.78) * mm, "mid": v(98.08, -81.03) * mm, "end": v(98.27, -81.22) * mm});
            skArc(sketch, "E2309", {"start": v(97.58, -81.9) * mm, "mid": v(98.37, -82) * mm, "end": v(98.27, -81.22) * mm});
            skArc(sketch, "E2310", {"start": v(97.58, -81.9) * mm, "mid": v(97.4, -81.72) * mm, "end": v(97.15, -81.65) * mm});
            skLineSegment(sketch, "E2311", {"start": v(97.15, -81.65) * mm, "end": v(92.68, -81.65) * mm});
            skArc(sketch, "E2312", {"start": v(92.68, -81.65) * mm, "mid": v(92.43, -81.72) * mm, "end": v(92.25, -81.9) * mm});
            skArc(sketch, "E2313", {"start": v(91.57, -81.22) * mm, "mid": v(91.46, -82) * mm, "end": v(92.25, -81.9) * mm});
            skArc(sketch, "E2314", {"start": v(91.57, -81.22) * mm, "mid": v(91.75, -81.03) * mm, "end": v(91.82, -80.78) * mm});
            skLineSegment(sketch, "E2315", {"start": v(91.82, -80.78) * mm, "end": v(91.82, -79.22) * mm});
            skArc(sketch, "E2316", {"start": v(70.62, -79.22) * mm, "mid": v(70.55, -78.97) * mm, "end": v(70.37, -78.78) * mm});
            skArc(sketch, "E2317", {"start": v(71.05, -78.1) * mm, "mid": v(70.26, -78) * mm, "end": v(70.37, -78.78) * mm});
            skArc(sketch, "E2318", {"start": v(71.05, -78.1) * mm, "mid": v(71.23, -78.28) * mm, "end": v(71.48, -78.35) * mm});
            skLineSegment(sketch, "E2319", {"start": v(71.48, -78.35) * mm, "end": v(75.95, -78.35) * mm});
            skArc(sketch, "E2320", {"start": v(75.95, -78.35) * mm, "mid": v(76.2, -78.28) * mm, "end": v(76.38, -78.1) * mm});
            skArc(sketch, "E2321", {"start": v(77.07, -78.78) * mm, "mid": v(77.17, -78) * mm, "end": v(76.38, -78.1) * mm});
            skArc(sketch, "E2322", {"start": v(77.07, -78.78) * mm, "mid": v(76.88, -78.97) * mm, "end": v(76.82, -79.22) * mm});
            skLineSegment(sketch, "E2323", {"start": v(76.82, -79.22) * mm, "end": v(76.82, -80.78) * mm});
            skArc(sketch, "E2324", {"start": v(76.82, -80.78) * mm, "mid": v(76.88, -81.03) * mm, "end": v(77.07, -81.22) * mm});
            skArc(sketch, "E2325", {"start": v(76.38, -81.9) * mm, "mid": v(77.17, -82) * mm, "end": v(77.07, -81.22) * mm});
            skArc(sketch, "E2326", {"start": v(76.38, -81.9) * mm, "mid": v(76.2, -81.72) * mm, "end": v(75.95, -81.65) * mm});
            skLineSegment(sketch, "E2327", {"start": v(75.95, -81.65) * mm, "end": v(71.48, -81.65) * mm});
            skArc(sketch, "E2328", {"start": v(71.48, -81.65) * mm, "mid": v(71.23, -81.72) * mm, "end": v(71.05, -81.9) * mm});
            skArc(sketch, "E2329", {"start": v(70.37, -81.22) * mm, "mid": v(70.26, -82) * mm, "end": v(71.05, -81.9) * mm});
            skArc(sketch, "E2330", {"start": v(70.37, -81.22) * mm, "mid": v(70.55, -81.03) * mm, "end": v(70.62, -80.78) * mm});
            skLineSegment(sketch, "E2331", {"start": v(70.62, -80.78) * mm, "end": v(70.62, -79.22) * mm});
            skCircle(sketch, "E2332", {"center": v(84.32, -80) * mm, "radius": 1.6 * mm});
            skArc(sketch, "E2333", {"start": v(91.82, 80.78) * mm, "mid": v(91.75, 81.03) * mm, "end": v(91.57, 81.22) * mm});
            skArc(sketch, "E2334", {"start": v(92.25, 81.9) * mm, "mid": v(91.46, 82) * mm, "end": v(91.57, 81.22) * mm});
            skArc(sketch, "E2335", {"start": v(92.25, 81.9) * mm, "mid": v(92.43, 81.72) * mm, "end": v(92.68, 81.65) * mm});
            skLineSegment(sketch, "E2336", {"start": v(92.68, 81.65) * mm, "end": v(97.15, 81.65) * mm});
            skArc(sketch, "E2337", {"start": v(97.15, 81.65) * mm, "mid": v(97.4, 81.72) * mm, "end": v(97.58, 81.9) * mm});
            skArc(sketch, "E2338", {"start": v(98.27, 81.22) * mm, "mid": v(98.37, 82) * mm, "end": v(97.58, 81.9) * mm});
            skArc(sketch, "E2339", {"start": v(98.27, 81.22) * mm, "mid": v(98.08, 81.03) * mm, "end": v(98.02, 80.78) * mm});
            skLineSegment(sketch, "E2340", {"start": v(98.02, 80.78) * mm, "end": v(98.02, 79.22) * mm});
            skArc(sketch, "E2341", {"start": v(98.02, 79.22) * mm, "mid": v(98.08, 78.97) * mm, "end": v(98.27, 78.78) * mm});
            skArc(sketch, "E2342", {"start": v(97.58, 78.1) * mm, "mid": v(98.37, 78) * mm, "end": v(98.27, 78.78) * mm});
            skArc(sketch, "E2343", {"start": v(97.58, 78.1) * mm, "mid": v(97.4, 78.28) * mm, "end": v(97.15, 78.35) * mm});
            skLineSegment(sketch, "E2344", {"start": v(97.15, 78.35) * mm, "end": v(92.68, 78.35) * mm});
            skArc(sketch, "E2345", {"start": v(92.68, 78.35) * mm, "mid": v(92.43, 78.28) * mm, "end": v(92.25, 78.1) * mm});
            skArc(sketch, "E2346", {"start": v(91.57, 78.78) * mm, "mid": v(91.46, 78) * mm, "end": v(92.25, 78.1) * mm});
            skArc(sketch, "E2347", {"start": v(91.57, 78.78) * mm, "mid": v(91.75, 78.97) * mm, "end": v(91.82, 79.22) * mm});
            skLineSegment(sketch, "E2348", {"start": v(91.82, 79.22) * mm, "end": v(91.82, 80.78) * mm});
            skArc(sketch, "E2349", {"start": v(70.62, 80.78) * mm, "mid": v(70.55, 81.03) * mm, "end": v(70.37, 81.22) * mm});
            skArc(sketch, "E2350", {"start": v(71.05, 81.9) * mm, "mid": v(70.26, 82) * mm, "end": v(70.37, 81.22) * mm});
            skArc(sketch, "E2351", {"start": v(71.05, 81.9) * mm, "mid": v(71.23, 81.72) * mm, "end": v(71.48, 81.65) * mm});
            skLineSegment(sketch, "E2352", {"start": v(71.48, 81.65) * mm, "end": v(75.95, 81.65) * mm});
            skArc(sketch, "E2353", {"start": v(75.95, 81.65) * mm, "mid": v(76.2, 81.72) * mm, "end": v(76.38, 81.9) * mm});
            skArc(sketch, "E2354", {"start": v(77.07, 81.22) * mm, "mid": v(77.17, 82) * mm, "end": v(76.38, 81.9) * mm});
            skArc(sketch, "E2355", {"start": v(77.07, 81.22) * mm, "mid": v(76.88, 81.03) * mm, "end": v(76.82, 80.78) * mm});
            skLineSegment(sketch, "E2356", {"start": v(76.82, 80.78) * mm, "end": v(76.82, 79.22) * mm});
            skArc(sketch, "E2357", {"start": v(76.82, 79.22) * mm, "mid": v(76.88, 78.97) * mm, "end": v(77.07, 78.78) * mm});
            skArc(sketch, "E2358", {"start": v(76.38, 78.1) * mm, "mid": v(77.17, 78) * mm, "end": v(77.07, 78.78) * mm});
            skArc(sketch, "E2359", {"start": v(76.38, 78.1) * mm, "mid": v(76.2, 78.28) * mm, "end": v(75.95, 78.35) * mm});
            skLineSegment(sketch, "E2360", {"start": v(75.95, 78.35) * mm, "end": v(71.48, 78.35) * mm});
            skArc(sketch, "E2361", {"start": v(71.48, 78.35) * mm, "mid": v(71.23, 78.28) * mm, "end": v(71.05, 78.1) * mm});
            skArc(sketch, "E2362", {"start": v(70.37, 78.78) * mm, "mid": v(70.26, 78) * mm, "end": v(71.05, 78.1) * mm});
            skArc(sketch, "E2363", {"start": v(70.37, 78.78) * mm, "mid": v(70.55, 78.97) * mm, "end": v(70.62, 79.22) * mm});
            skLineSegment(sketch, "E2364", {"start": v(70.62, 79.22) * mm, "end": v(70.62, 80.78) * mm});
            skCircle(sketch, "E2365", {"center": v(84.32, 80) * mm, "radius": 1.6 * mm});
            skCircle(sketch, "E2366", {"center": v(-204.24, 137.06) * mm, "radius": 1.3 * mm});
            skCircle(sketch, "E2367", {"center": v(-121.04, 137.08) * mm, "radius": 1.3 * mm});
            skCircle(sketch, "E2368", {"center": v(-198.02, 88.86) * mm, "radius": 1.3 * mm});
            skCircle(sketch, "E2369", {"center": v(-123.52, 88.88) * mm, "radius": 1.3 * mm});
            skLineSegment(sketch, "E2370", {"start": v(-74.17, 88.9) * mm, "end": v(-74.17, 96.9) * mm});
            skArc(sketch, "E2371", {"start": v(-74.17, 96.9) * mm, "mid": v(-78.17, 100.9) * mm, "end": v(-82.17, 96.9) * mm});
            skLineSegment(sketch, "E2372", {"start": v(-82.17, 96.9) * mm, "end": v(-82.17, 88.9) * mm});
            skArc(sketch, "E2373", {"start": v(-82.17, 88.9) * mm, "mid": v(-78.17, 84.9) * mm, "end": v(-74.17, 88.9) * mm});
            skLineSegment(sketch, "E2374", {"start": v(-74.17, 139.63) * mm, "end": v(-74.17, 147.63) * mm});
            skArc(sketch, "E2375", {"start": v(-74.17, 147.63) * mm, "mid": v(-78.17, 151.63) * mm, "end": v(-82.17, 147.63) * mm});
            skLineSegment(sketch, "E2376", {"start": v(-82.17, 147.63) * mm, "end": v(-82.17, 139.63) * mm});
            skArc(sketch, "E2377", {"start": v(-82.17, 139.63) * mm, "mid": v(-78.17, 135.63) * mm, "end": v(-74.17, 139.63) * mm});
            skLineSegment(sketch, "E2378", {"start": v(-413.32, -159.14) * mm, "end": v(-413.32, -151.14) * mm});
            skArc(sketch, "E2379", {"start": v(-413.32, -151.14) * mm, "mid": v(-417.32, -147.14) * mm, "end": v(-421.32, -151.14) * mm});
            skLineSegment(sketch, "E2380", {"start": v(-421.32, -151.14) * mm, "end": v(-421.32, -159.14) * mm});
            skArc(sketch, "E2381", {"start": v(-421.32, -159.14) * mm, "mid": v(-417.32, -163.14) * mm, "end": v(-413.32, -159.14) * mm});
            skLineSegment(sketch, "E2382", {"start": v(-413.32, -108.41) * mm, "end": v(-413.32, -100.41) * mm});
            skArc(sketch, "E2383", {"start": v(-413.32, -100.41) * mm, "mid": v(-417.32, -96.41) * mm, "end": v(-421.32, -100.41) * mm});
            skLineSegment(sketch, "E2384", {"start": v(-421.32, -100.41) * mm, "end": v(-421.32, -108.41) * mm});
            skArc(sketch, "E2385", {"start": v(-421.32, -108.41) * mm, "mid": v(-417.32, -112.41) * mm, "end": v(-413.32, -108.41) * mm});
            skLineSegment(sketch, "E2386", {"start": v(390.52, 119.3) * mm, "end": v(390.52, 120.17) * mm});
            skLineSegment(sketch, "E2387", {"start": v(404.32, 121.97) * mm, "end": v(391.17, 121.97) * mm});
            skArc(sketch, "E2388", {"start": v(390.95, 122.17) * mm, "mid": v(390.16, 122.28) * mm, "end": v(390.27, 121.5) * mm});
            skArc(sketch, "E2389", {"start": v(390.52, 121.06) * mm, "mid": v(390.45, 121.3) * mm, "end": v(390.27, 121.5) * mm});
            skLineSegment(sketch, "E2390", {"start": v(390.95, 122.17) * mm, "end": v(391.17, 121.97) * mm});
            skLineSegment(sketch, "E2391", {"start": v(390.52, 121.06) * mm, "end": v(390.52, 120.17) * mm});
            skLineSegment(sketch, "E2392", {"start": v(404.32, 118.38) * mm, "end": v(417.47, 118.38) * mm});
            skArc(sketch, "E2393", {"start": v(417.68, 118.18) * mm, "mid": v(418.47, 118.07) * mm, "end": v(418.37, 118.86) * mm});
            skArc(sketch, "E2394", {"start": v(418.12, 119.3) * mm, "mid": v(418.18, 119.04) * mm, "end": v(418.37, 118.86) * mm});
            skLineSegment(sketch, "E2395", {"start": v(417.68, 118.18) * mm, "end": v(417.47, 118.38) * mm});
            skLineSegment(sketch, "E2396", {"start": v(418.12, 119.3) * mm, "end": v(418.12, 120.17) * mm});
            skLineSegment(sketch, "E2397", {"start": v(404.32, 121.97) * mm, "end": v(417.47, 121.97) * mm});
            skArc(sketch, "E2398", {"start": v(418.37, 121.5) * mm, "mid": v(418.47, 122.28) * mm, "end": v(417.68, 122.17) * mm});
            skArc(sketch, "E2399", {"start": v(418.37, 121.5) * mm, "mid": v(418.18, 121.3) * mm, "end": v(418.12, 121.06) * mm});
            skLineSegment(sketch, "E2400", {"start": v(417.68, 122.17) * mm, "end": v(417.47, 121.97) * mm});
            skLineSegment(sketch, "E2401", {"start": v(418.12, 121.06) * mm, "end": v(418.12, 120.17) * mm});
            skLineSegment(sketch, "E2402", {"start": v(404.32, -121.97) * mm, "end": v(391.17, -121.97) * mm});
            skArc(sketch, "E2403", {"start": v(390.27, -121.5) * mm, "mid": v(390.16, -122.28) * mm, "end": v(390.95, -122.17) * mm});
            skArc(sketch, "E2404", {"start": v(390.27, -121.5) * mm, "mid": v(390.45, -121.3) * mm, "end": v(390.52, -121.06) * mm});
            skLineSegment(sketch, "E2405", {"start": v(390.95, -122.17) * mm, "end": v(391.17, -121.97) * mm});
            skLineSegment(sketch, "E2406", {"start": v(390.52, -121.06) * mm, "end": v(390.52, -120.18) * mm});
            skLineSegment(sketch, "E2407", {"start": v(404.32, -118.38) * mm, "end": v(391.17, -118.38) * mm});
            skArc(sketch, "E2408", {"start": v(390.95, -118.18) * mm, "mid": v(390.16, -118.07) * mm, "end": v(390.27, -118.86) * mm});
            skArc(sketch, "E2409", {"start": v(390.52, -119.3) * mm, "mid": v(390.45, -119.04) * mm, "end": v(390.27, -118.86) * mm});
            skLineSegment(sketch, "E2410", {"start": v(390.95, -118.18) * mm, "end": v(391.17, -118.38) * mm});
            skLineSegment(sketch, "E2411", {"start": v(390.52, -119.3) * mm, "end": v(390.52, -120.18) * mm});
            skLineSegment(sketch, "E2412", {"start": v(404.32, -121.97) * mm, "end": v(417.47, -121.97) * mm});
            skArc(sketch, "E2413", {"start": v(417.68, -122.17) * mm, "mid": v(418.47, -122.28) * mm, "end": v(418.37, -121.5) * mm});
            skArc(sketch, "E2414", {"start": v(418.12, -121.06) * mm, "mid": v(418.18, -121.3) * mm, "end": v(418.37, -121.5) * mm});
            skLineSegment(sketch, "E2415", {"start": v(417.68, -122.17) * mm, "end": v(417.47, -121.97) * mm});
            skLineSegment(sketch, "E2416", {"start": v(418.12, -121.06) * mm, "end": v(418.12, -120.18) * mm});
            skLineSegment(sketch, "E2417", {"start": v(404.32, -118.38) * mm, "end": v(417.47, -118.38) * mm});
            skArc(sketch, "E2418", {"start": v(418.37, -118.86) * mm, "mid": v(418.47, -118.07) * mm, "end": v(417.68, -118.18) * mm});
            skArc(sketch, "E2419", {"start": v(418.37, -118.86) * mm, "mid": v(418.18, -119.04) * mm, "end": v(418.12, -119.3) * mm});
            skLineSegment(sketch, "E2420", {"start": v(417.68, -118.18) * mm, "end": v(417.47, -118.38) * mm});
            skLineSegment(sketch, "E2421", {"start": v(418.12, -119.3) * mm, "end": v(418.12, -120.18) * mm});
            skLineSegment(sketch, "E2422", {"start": v(-75.54, -153.69) * mm, "end": v(-71.54, -153.69) * mm});
            skLineSegment(sketch, "E2423", {"start": v(-71.54, -153.69) * mm, "end": v(-71.54, -154.96) * mm});
            skLineSegment(sketch, "E2424", {"start": v(-71.54, -154.96) * mm, "end": v(-68.54, -154.96) * mm});
            skLineSegment(sketch, "E2425", {"start": v(-68.54, -154.96) * mm, "end": v(-68.54, -158.16) * mm});
            skLineSegment(sketch, "E2426", {"start": v(-68.54, -158.16) * mm, "end": v(-71.54, -158.16) * mm});
            skLineSegment(sketch, "E2427", {"start": v(-71.54, -158.16) * mm, "end": v(-71.54, -159.44) * mm});
            skLineSegment(sketch, "E2428", {"start": v(-71.54, -159.44) * mm, "end": v(-75.54, -159.44) * mm});
            skLineSegment(sketch, "E2429", {"start": v(-75.54, -159.44) * mm, "end": v(-75.54, -158.16) * mm});
            skLineSegment(sketch, "E2430", {"start": v(-75.54, -158.16) * mm, "end": v(-78.54, -158.16) * mm});
            skLineSegment(sketch, "E2431", {"start": v(-78.54, -158.16) * mm, "end": v(-78.54, -165.06) * mm});
            skLineSegment(sketch, "E2432", {"start": v(-78.54, -172.06) * mm, "end": v(-78.54, -178.96) * mm});
            skLineSegment(sketch, "E2433", {"start": v(-78.54, -178.96) * mm, "end": v(-75.54, -178.96) * mm});
            skLineSegment(sketch, "E2434", {"start": v(-75.54, -178.96) * mm, "end": v(-75.54, -177.69) * mm});
            skLineSegment(sketch, "E2435", {"start": v(-75.54, -177.69) * mm, "end": v(-71.54, -177.69) * mm});
            skLineSegment(sketch, "E2436", {"start": v(-71.54, -177.69) * mm, "end": v(-71.54, -178.96) * mm});
            skLineSegment(sketch, "E2437", {"start": v(-71.54, -178.96) * mm, "end": v(-68.54, -178.96) * mm});
            skLineSegment(sketch, "E2438", {"start": v(-68.54, -178.96) * mm, "end": v(-68.54, -182.16) * mm});
            skLineSegment(sketch, "E2439", {"start": v(-68.54, -182.16) * mm, "end": v(-71.54, -182.16) * mm});
            skLineSegment(sketch, "E2440", {"start": v(-71.54, -182.16) * mm, "end": v(-71.54, -183.44) * mm});
            skLineSegment(sketch, "E2441", {"start": v(-71.54, -183.44) * mm, "end": v(-75.54, -183.44) * mm});
            skLineSegment(sketch, "E2442", {"start": v(-75.54, -183.44) * mm, "end": v(-75.54, -182.16) * mm});
            skLineSegment(sketch, "E2443", {"start": v(-75.54, -182.16) * mm, "end": v(-78.54, -182.16) * mm});
            skLineSegment(sketch, "E2444", {"start": v(-78.54, -182.16) * mm, "end": v(-78.54, -185.16) * mm});
            skLineSegment(sketch, "E2445", {"start": v(-78.54, -185.16) * mm, "end": v(-66.54, -185.16) * mm});
            skArc(sketch, "E2446", {"start": v(-66.54, -185.16) * mm, "mid": v(-64.41, -184.28) * mm, "end": v(-63.54, -182.16) * mm});
            skLineSegment(sketch, "E2447", {"start": v(-63.54, -182.16) * mm, "end": v(-63.54, -154.96) * mm});
            skArc(sketch, "E2448", {"start": v(-63.54, -154.96) * mm, "mid": v(-64.41, -152.84) * mm, "end": v(-66.54, -151.96) * mm});
            skLineSegment(sketch, "E2449", {"start": v(-66.54, -151.96) * mm, "end": v(-78.54, -151.96) * mm});
            skLineSegment(sketch, "E2450", {"start": v(-78.54, -151.96) * mm, "end": v(-78.54, -154.96) * mm});
            skLineSegment(sketch, "E2451", {"start": v(-78.54, -154.96) * mm, "end": v(-75.54, -154.96) * mm});
            skLineSegment(sketch, "E2452", {"start": v(-75.54, -154.96) * mm, "end": v(-75.54, -153.69) * mm});
            skLineSegment(sketch, "E2453", {"start": v(-77.04, -168.56) * mm, "end": v(-77.04, -165.06) * mm});
            skLineSegment(sketch, "E2454", {"start": v(-77.04, -165.06) * mm, "end": v(-78.54, -165.06) * mm});
            skLineSegment(sketch, "E2455", {"start": v(-77.04, -168.56) * mm, "end": v(-77.04, -172.06) * mm});
            skLineSegment(sketch, "E2456", {"start": v(-77.04, -172.06) * mm, "end": v(-78.54, -172.06) * mm});
            skLineSegment(sketch, "E2457", {"start": v(240.86, -69.26) * mm, "end": v(236.86, -69.26) * mm});
            skLineSegment(sketch, "E2458", {"start": v(236.86, -69.26) * mm, "end": v(236.86, -67.98) * mm});
            skLineSegment(sketch, "E2459", {"start": v(236.86, -67.98) * mm, "end": v(233.86, -67.98) * mm});
            skLineSegment(sketch, "E2460", {"start": v(233.86, -67.98) * mm, "end": v(233.86, -64.78) * mm});
            skLineSegment(sketch, "E2461", {"start": v(233.86, -64.78) * mm, "end": v(236.86, -64.78) * mm});
            skLineSegment(sketch, "E2462", {"start": v(236.86, -64.78) * mm, "end": v(236.86, -63.5) * mm});
            skLineSegment(sketch, "E2463", {"start": v(236.86, -63.5) * mm, "end": v(240.86, -63.5) * mm});
            skLineSegment(sketch, "E2464", {"start": v(240.86, -63.5) * mm, "end": v(240.86, -64.78) * mm});
            skLineSegment(sketch, "E2465", {"start": v(240.86, -64.78) * mm, "end": v(243.86, -64.78) * mm});
            skLineSegment(sketch, "E2466", {"start": v(243.86, -64.78) * mm, "end": v(243.86, -58.88) * mm});
            skLineSegment(sketch, "E2467", {"start": v(243.86, -58.88) * mm, "end": v(238.76, -58.88) * mm});
            skArc(sketch, "E2468", {"start": v(238.76, -43.88) * mm, "mid": v(231.26, -51.38) * mm, "end": v(238.76, -58.88) * mm});
            skLineSegment(sketch, "E2469", {"start": v(238.76, -43.88) * mm, "end": v(243.86, -43.88) * mm});
            skLineSegment(sketch, "E2470", {"start": v(243.86, -43.88) * mm, "end": v(243.86, -37.98) * mm});
            skLineSegment(sketch, "E2471", {"start": v(243.86, -37.98) * mm, "end": v(240.86, -37.98) * mm});
            skLineSegment(sketch, "E2472", {"start": v(240.86, -37.98) * mm, "end": v(240.86, -39.26) * mm});
            skLineSegment(sketch, "E2473", {"start": v(240.86, -39.26) * mm, "end": v(236.86, -39.26) * mm});
            skLineSegment(sketch, "E2474", {"start": v(236.86, -39.26) * mm, "end": v(236.86, -37.98) * mm});
            skLineSegment(sketch, "E2475", {"start": v(236.86, -37.98) * mm, "end": v(233.86, -37.98) * mm});
            skLineSegment(sketch, "E2476", {"start": v(233.86, -37.98) * mm, "end": v(233.86, -34.78) * mm});
            skLineSegment(sketch, "E2477", {"start": v(233.86, -34.78) * mm, "end": v(236.86, -34.78) * mm});
            skLineSegment(sketch, "E2478", {"start": v(236.86, -34.78) * mm, "end": v(236.86, -33.5) * mm});
            skLineSegment(sketch, "E2479", {"start": v(236.86, -33.5) * mm, "end": v(240.86, -33.5) * mm});
            skLineSegment(sketch, "E2480", {"start": v(240.86, -33.5) * mm, "end": v(240.86, -34.78) * mm});
            skLineSegment(sketch, "E2481", {"start": v(240.86, -34.78) * mm, "end": v(243.86, -34.78) * mm});
            skLineSegment(sketch, "E2482", {"start": v(243.86, -34.78) * mm, "end": v(243.86, -31.78) * mm});
            skLineSegment(sketch, "E2483", {"start": v(243.86, -28.78) * mm, "end": v(231.85, -28.78) * mm});
            skArc(sketch, "E2484", {"start": v(231.85, -28.78) * mm, "mid": v(229.73, -29.66) * mm, "end": v(228.85, -31.78) * mm});
            skLineSegment(sketch, "E2485", {"start": v(228.85, -34.78) * mm, "end": v(228.85, -67.98) * mm});
            skArc(sketch, "E2486", {"start": v(228.85, -70.98) * mm, "mid": v(229.73, -73.1) * mm, "end": v(231.85, -73.98) * mm});
            skLineSegment(sketch, "E2487", {"start": v(231.85, -73.98) * mm, "end": v(243.86, -73.98) * mm});
            skLineSegment(sketch, "E2488", {"start": v(243.86, -70.98) * mm, "end": v(243.86, -67.98) * mm});
            skLineSegment(sketch, "E2489", {"start": v(243.86, -67.98) * mm, "end": v(240.86, -67.98) * mm});
            skLineSegment(sketch, "E2490", {"start": v(240.86, -67.98) * mm, "end": v(240.86, -69.26) * mm});
            skLineSegment(sketch, "E2491", {"start": v(228.85, -34.78) * mm, "end": v(228.85, -31.78) * mm});
            skLineSegment(sketch, "E2492", {"start": v(243.86, -28.78) * mm, "end": v(243.86, -31.78) * mm});
            skLineSegment(sketch, "E2493", {"start": v(228.85, -70.98) * mm, "end": v(228.85, -67.98) * mm});
            skLineSegment(sketch, "E2494", {"start": v(243.86, -73.98) * mm, "end": v(243.86, -70.98) * mm});
            skLineSegment(sketch, "E2495", {"start": v(137.05, -56.84) * mm, "end": v(133.05, -56.84) * mm});
            skLineSegment(sketch, "E2496", {"start": v(133.05, -56.84) * mm, "end": v(133.05, -55.56) * mm});
            skLineSegment(sketch, "E2497", {"start": v(133.05, -55.56) * mm, "end": v(130.05, -55.56) * mm});
            skLineSegment(sketch, "E2498", {"start": v(130.05, -55.56) * mm, "end": v(130.05, -52.36) * mm});
            skLineSegment(sketch, "E2499", {"start": v(130.05, -52.36) * mm, "end": v(133.05, -52.36) * mm});
            skLineSegment(sketch, "E2500", {"start": v(133.05, -52.36) * mm, "end": v(133.05, -51.09) * mm});
            skLineSegment(sketch, "E2501", {"start": v(133.05, -51.09) * mm, "end": v(137.05, -51.09) * mm});
            skLineSegment(sketch, "E2502", {"start": v(137.05, -51.09) * mm, "end": v(137.05, -52.36) * mm});
            skLineSegment(sketch, "E2503", {"start": v(137.05, -52.36) * mm, "end": v(140.05, -52.36) * mm});
            skLineSegment(sketch, "E2504", {"start": v(140.05, -52.36) * mm, "end": v(140.05, -46.46) * mm});
            skLineSegment(sketch, "E2505", {"start": v(140.05, -46.46) * mm, "end": v(134.95, -46.46) * mm});
            skArc(sketch, "E2506", {"start": v(134.95, -31.46) * mm, "mid": v(127.45, -38.96) * mm, "end": v(134.95, -46.46) * mm});
            skLineSegment(sketch, "E2507", {"start": v(134.95, -31.46) * mm, "end": v(140.05, -31.46) * mm});
            skLineSegment(sketch, "E2508", {"start": v(140.05, -31.46) * mm, "end": v(140.05, -25.56) * mm});
            skLineSegment(sketch, "E2509", {"start": v(140.05, -25.56) * mm, "end": v(137.05, -25.56) * mm});
            skLineSegment(sketch, "E2510", {"start": v(137.05, -25.56) * mm, "end": v(137.05, -26.84) * mm});
            skLineSegment(sketch, "E2511", {"start": v(137.05, -26.84) * mm, "end": v(133.05, -26.84) * mm});
            skLineSegment(sketch, "E2512", {"start": v(133.05, -26.84) * mm, "end": v(133.05, -25.56) * mm});
            skLineSegment(sketch, "E2513", {"start": v(133.05, -25.56) * mm, "end": v(130.05, -25.56) * mm});
            skLineSegment(sketch, "E2514", {"start": v(130.05, -25.56) * mm, "end": v(130.05, -22.36) * mm});
            skLineSegment(sketch, "E2515", {"start": v(130.05, -22.36) * mm, "end": v(133.05, -22.36) * mm});
            skLineSegment(sketch, "E2516", {"start": v(133.05, -22.36) * mm, "end": v(133.05, -21.09) * mm});
            skLineSegment(sketch, "E2517", {"start": v(133.05, -21.09) * mm, "end": v(137.05, -21.09) * mm});
            skLineSegment(sketch, "E2518", {"start": v(137.05, -21.09) * mm, "end": v(137.05, -22.36) * mm});
            skLineSegment(sketch, "E2519", {"start": v(137.05, -22.36) * mm, "end": v(140.05, -22.36) * mm});
            skLineSegment(sketch, "E2520", {"start": v(140.05, -22.36) * mm, "end": v(140.05, -19.36) * mm});
            skLineSegment(sketch, "E2521", {"start": v(140.05, -16.36) * mm, "end": v(128.04, -16.36) * mm});
            skArc(sketch, "E2522", {"start": v(128.04, -16.36) * mm, "mid": v(125.92, -17.24) * mm, "end": v(125.04, -19.36) * mm});
            skLineSegment(sketch, "E2523", {"start": v(125.04, -22.36) * mm, "end": v(125.04, -55.56) * mm});
            skArc(sketch, "E2524", {"start": v(125.04, -58.56) * mm, "mid": v(125.92, -60.69) * mm, "end": v(128.04, -61.56) * mm});
            skLineSegment(sketch, "E2525", {"start": v(128.04, -61.56) * mm, "end": v(140.05, -61.56) * mm});
            skLineSegment(sketch, "E2526", {"start": v(140.05, -58.56) * mm, "end": v(140.05, -55.56) * mm});
            skLineSegment(sketch, "E2527", {"start": v(140.05, -55.56) * mm, "end": v(137.05, -55.56) * mm});
            skLineSegment(sketch, "E2528", {"start": v(137.05, -55.56) * mm, "end": v(137.05, -56.84) * mm});
            skLineSegment(sketch, "E2529", {"start": v(125.04, -22.36) * mm, "end": v(125.04, -19.36) * mm});
            skLineSegment(sketch, "E2530", {"start": v(140.05, -16.36) * mm, "end": v(140.05, -19.36) * mm});
            skLineSegment(sketch, "E2531", {"start": v(125.04, -58.56) * mm, "end": v(125.04, -55.56) * mm});
            skLineSegment(sketch, "E2532", {"start": v(140.05, -61.56) * mm, "end": v(140.05, -58.56) * mm});
            skLineSegment(sketch, "E2533", {"start": v(137.05, 18.3) * mm, "end": v(133.05, 18.3) * mm});
            skLineSegment(sketch, "E2534", {"start": v(133.05, 18.3) * mm, "end": v(133.05, 19.58) * mm});
            skLineSegment(sketch, "E2535", {"start": v(133.05, 19.58) * mm, "end": v(130.05, 19.58) * mm});
            skLineSegment(sketch, "E2536", {"start": v(130.05, 19.58) * mm, "end": v(130.05, 22.78) * mm});
            skLineSegment(sketch, "E2537", {"start": v(130.05, 22.78) * mm, "end": v(133.05, 22.78) * mm});
            skLineSegment(sketch, "E2538", {"start": v(133.05, 22.78) * mm, "end": v(133.05, 24.06) * mm});
            skLineSegment(sketch, "E2539", {"start": v(133.05, 24.06) * mm, "end": v(137.05, 24.06) * mm});
            skLineSegment(sketch, "E2540", {"start": v(137.05, 24.06) * mm, "end": v(137.05, 22.78) * mm});
            skLineSegment(sketch, "E2541", {"start": v(137.05, 22.78) * mm, "end": v(140.05, 22.78) * mm});
            skLineSegment(sketch, "E2542", {"start": v(140.05, 22.78) * mm, "end": v(140.05, 28.68) * mm});
            skLineSegment(sketch, "E2543", {"start": v(140.05, 28.68) * mm, "end": v(134.95, 28.68) * mm});
            skArc(sketch, "E2544", {"start": v(134.95, 43.68) * mm, "mid": v(127.45, 36.18) * mm, "end": v(134.95, 28.68) * mm});
            skLineSegment(sketch, "E2545", {"start": v(134.95, 43.68) * mm, "end": v(140.05, 43.68) * mm});
            skLineSegment(sketch, "E2546", {"start": v(140.05, 43.68) * mm, "end": v(140.05, 49.58) * mm});
            skLineSegment(sketch, "E2547", {"start": v(140.05, 49.58) * mm, "end": v(137.05, 49.58) * mm});
            skLineSegment(sketch, "E2548", {"start": v(137.05, 49.58) * mm, "end": v(137.05, 48.3) * mm});
            skLineSegment(sketch, "E2549", {"start": v(137.05, 48.3) * mm, "end": v(133.05, 48.3) * mm});
            skLineSegment(sketch, "E2550", {"start": v(133.05, 48.3) * mm, "end": v(133.05, 49.58) * mm});
            skLineSegment(sketch, "E2551", {"start": v(133.05, 49.58) * mm, "end": v(130.05, 49.58) * mm});
            skLineSegment(sketch, "E2552", {"start": v(130.05, 49.58) * mm, "end": v(130.05, 52.78) * mm});
            skLineSegment(sketch, "E2553", {"start": v(130.05, 52.78) * mm, "end": v(133.05, 52.78) * mm});
            skLineSegment(sketch, "E2554", {"start": v(133.05, 52.78) * mm, "end": v(133.05, 54.06) * mm});
            skLineSegment(sketch, "E2555", {"start": v(133.05, 54.06) * mm, "end": v(137.05, 54.06) * mm});
            skLineSegment(sketch, "E2556", {"start": v(137.05, 54.06) * mm, "end": v(137.05, 52.78) * mm});
            skLineSegment(sketch, "E2557", {"start": v(137.05, 52.78) * mm, "end": v(140.05, 52.78) * mm});
            skLineSegment(sketch, "E2558", {"start": v(140.05, 52.78) * mm, "end": v(140.05, 55.78) * mm});
            skLineSegment(sketch, "E2559", {"start": v(140.05, 58.78) * mm, "end": v(128.04, 58.78) * mm});
            skArc(sketch, "E2560", {"start": v(128.04, 58.78) * mm, "mid": v(125.92, 57.9) * mm, "end": v(125.04, 55.78) * mm});
            skLineSegment(sketch, "E2561", {"start": v(125.04, 52.78) * mm, "end": v(125.04, 19.58) * mm});
            skArc(sketch, "E2562", {"start": v(125.04, 16.58) * mm, "mid": v(125.92, 14.46) * mm, "end": v(128.04, 13.58) * mm});
            skLineSegment(sketch, "E2563", {"start": v(128.04, 13.58) * mm, "end": v(140.05, 13.58) * mm});
            skLineSegment(sketch, "E2564", {"start": v(140.05, 16.58) * mm, "end": v(140.05, 19.58) * mm});
            skLineSegment(sketch, "E2565", {"start": v(140.05, 19.58) * mm, "end": v(137.05, 19.58) * mm});
            skLineSegment(sketch, "E2566", {"start": v(137.05, 19.58) * mm, "end": v(137.05, 18.3) * mm});
            skLineSegment(sketch, "E2567", {"start": v(125.04, 52.78) * mm, "end": v(125.04, 55.78) * mm});
            skLineSegment(sketch, "E2568", {"start": v(140.05, 58.78) * mm, "end": v(140.05, 55.78) * mm});
            skLineSegment(sketch, "E2569", {"start": v(125.04, 16.58) * mm, "end": v(125.04, 19.58) * mm});
            skLineSegment(sketch, "E2570", {"start": v(140.05, 13.58) * mm, "end": v(140.05, 16.58) * mm});
            skLineSegment(sketch, "E2571", {"start": v(240.43, 32.02) * mm, "end": v(236.43, 32.02) * mm});
            skLineSegment(sketch, "E2572", {"start": v(236.43, 32.02) * mm, "end": v(236.43, 33.3) * mm});
            skLineSegment(sketch, "E2573", {"start": v(236.43, 33.3) * mm, "end": v(233.43, 33.3) * mm});
            skLineSegment(sketch, "E2574", {"start": v(233.43, 33.3) * mm, "end": v(233.43, 36.5) * mm});
            skLineSegment(sketch, "E2575", {"start": v(233.43, 36.5) * mm, "end": v(236.43, 36.5) * mm});
            skLineSegment(sketch, "E2576", {"start": v(236.43, 36.5) * mm, "end": v(236.43, 37.77) * mm});
            skLineSegment(sketch, "E2577", {"start": v(236.43, 37.77) * mm, "end": v(240.43, 37.77) * mm});
            skLineSegment(sketch, "E2578", {"start": v(240.43, 37.77) * mm, "end": v(240.43, 36.5) * mm});
            skLineSegment(sketch, "E2579", {"start": v(240.43, 36.5) * mm, "end": v(243.43, 36.5) * mm});
            skLineSegment(sketch, "E2580", {"start": v(243.43, 36.5) * mm, "end": v(243.43, 42.4) * mm});
            skLineSegment(sketch, "E2581", {"start": v(243.43, 42.4) * mm, "end": v(238.33, 42.4) * mm});
            skArc(sketch, "E2582", {"start": v(238.33, 57.4) * mm, "mid": v(230.83, 49.9) * mm, "end": v(238.33, 42.4) * mm});
            skLineSegment(sketch, "E2583", {"start": v(238.33, 57.4) * mm, "end": v(243.43, 57.4) * mm});
            skLineSegment(sketch, "E2584", {"start": v(243.43, 57.4) * mm, "end": v(243.43, 63.3) * mm});
            skLineSegment(sketch, "E2585", {"start": v(243.43, 63.3) * mm, "end": v(240.43, 63.3) * mm});
            skLineSegment(sketch, "E2586", {"start": v(240.43, 63.3) * mm, "end": v(240.43, 62.02) * mm});
            skLineSegment(sketch, "E2587", {"start": v(240.43, 62.02) * mm, "end": v(236.43, 62.02) * mm});
            skLineSegment(sketch, "E2588", {"start": v(236.43, 62.02) * mm, "end": v(236.43, 63.3) * mm});
            skLineSegment(sketch, "E2589", {"start": v(236.43, 63.3) * mm, "end": v(233.43, 63.3) * mm});
            skLineSegment(sketch, "E2590", {"start": v(233.43, 63.3) * mm, "end": v(233.43, 66.5) * mm});
            skLineSegment(sketch, "E2591", {"start": v(233.43, 66.5) * mm, "end": v(236.43, 66.5) * mm});
            skLineSegment(sketch, "E2592", {"start": v(236.43, 66.5) * mm, "end": v(236.43, 67.77) * mm});
            skLineSegment(sketch, "E2593", {"start": v(236.43, 67.77) * mm, "end": v(240.43, 67.77) * mm});
            skLineSegment(sketch, "E2594", {"start": v(240.43, 67.77) * mm, "end": v(240.43, 66.5) * mm});
            skLineSegment(sketch, "E2595", {"start": v(240.43, 66.5) * mm, "end": v(243.43, 66.5) * mm});
            skLineSegment(sketch, "E2596", {"start": v(243.43, 66.5) * mm, "end": v(243.43, 69.5) * mm});
            skLineSegment(sketch, "E2597", {"start": v(243.43, 72.5) * mm, "end": v(231.42, 72.5) * mm});
            skArc(sketch, "E2598", {"start": v(231.42, 72.5) * mm, "mid": v(229.3, 71.62) * mm, "end": v(228.42, 69.5) * mm});
            skLineSegment(sketch, "E2599", {"start": v(228.42, 66.5) * mm, "end": v(228.42, 33.3) * mm});
            skArc(sketch, "E2600", {"start": v(228.42, 30.3) * mm, "mid": v(229.3, 28.17) * mm, "end": v(231.42, 27.3) * mm});
            skLineSegment(sketch, "E2601", {"start": v(231.42, 27.3) * mm, "end": v(243.43, 27.3) * mm});
            skLineSegment(sketch, "E2602", {"start": v(243.43, 30.3) * mm, "end": v(243.43, 33.3) * mm});
            skLineSegment(sketch, "E2603", {"start": v(243.43, 33.3) * mm, "end": v(240.43, 33.3) * mm});
            skLineSegment(sketch, "E2604", {"start": v(240.43, 33.3) * mm, "end": v(240.43, 32.02) * mm});
            skLineSegment(sketch, "E2605", {"start": v(228.42, 66.5) * mm, "end": v(228.42, 69.5) * mm});
            skLineSegment(sketch, "E2606", {"start": v(243.43, 72.5) * mm, "end": v(243.43, 69.5) * mm});
            skLineSegment(sketch, "E2607", {"start": v(228.42, 30.3) * mm, "end": v(228.42, 33.3) * mm});
            skLineSegment(sketch, "E2608", {"start": v(243.43, 27.3) * mm, "end": v(243.43, 30.3) * mm});
            skLineSegment(sketch, "E2609", {"start": v(-187.11, -145.3) * mm, "end": v(-183.11, -145.3) * mm});
            skLineSegment(sketch, "E2610", {"start": v(-183.11, -145.3) * mm, "end": v(-183.11, -146.57) * mm});
            skLineSegment(sketch, "E2611", {"start": v(-183.11, -146.57) * mm, "end": v(-180.11, -146.57) * mm});
            skLineSegment(sketch, "E2612", {"start": v(-180.11, -146.57) * mm, "end": v(-180.11, -149.77) * mm});
            skLineSegment(sketch, "E2613", {"start": v(-180.11, -149.77) * mm, "end": v(-183.11, -149.77) * mm});
            skLineSegment(sketch, "E2614", {"start": v(-183.11, -149.77) * mm, "end": v(-183.11, -151.05) * mm});
            skLineSegment(sketch, "E2615", {"start": v(-183.11, -151.05) * mm, "end": v(-187.11, -151.05) * mm});
            skLineSegment(sketch, "E2616", {"start": v(-187.11, -151.05) * mm, "end": v(-187.11, -149.77) * mm});
            skLineSegment(sketch, "E2617", {"start": v(-187.11, -149.77) * mm, "end": v(-190.11, -149.77) * mm});
            skLineSegment(sketch, "E2618", {"start": v(-190.11, -149.77) * mm, "end": v(-190.11, -156.67) * mm});
            skLineSegment(sketch, "E2619", {"start": v(-190.11, -163.67) * mm, "end": v(-190.11, -170.57) * mm});
            skLineSegment(sketch, "E2620", {"start": v(-190.11, -170.57) * mm, "end": v(-187.11, -170.57) * mm});
            skLineSegment(sketch, "E2621", {"start": v(-187.11, -170.57) * mm, "end": v(-187.11, -169.3) * mm});
            skLineSegment(sketch, "E2622", {"start": v(-187.11, -169.3) * mm, "end": v(-183.11, -169.3) * mm});
            skLineSegment(sketch, "E2623", {"start": v(-183.11, -169.3) * mm, "end": v(-183.11, -170.57) * mm});
            skLineSegment(sketch, "E2624", {"start": v(-183.11, -170.57) * mm, "end": v(-180.11, -170.57) * mm});
            skLineSegment(sketch, "E2625", {"start": v(-180.11, -170.57) * mm, "end": v(-180.11, -173.77) * mm});
            skLineSegment(sketch, "E2626", {"start": v(-180.11, -173.77) * mm, "end": v(-183.11, -173.77) * mm});
            skLineSegment(sketch, "E2627", {"start": v(-183.11, -173.77) * mm, "end": v(-183.11, -175.05) * mm});
            skLineSegment(sketch, "E2628", {"start": v(-183.11, -175.05) * mm, "end": v(-187.11, -175.05) * mm});
            skLineSegment(sketch, "E2629", {"start": v(-187.11, -175.05) * mm, "end": v(-187.11, -173.77) * mm});
            skLineSegment(sketch, "E2630", {"start": v(-187.11, -173.77) * mm, "end": v(-190.11, -173.77) * mm});
            skLineSegment(sketch, "E2631", {"start": v(-190.11, -173.77) * mm, "end": v(-190.11, -176.77) * mm});
            skLineSegment(sketch, "E2632", {"start": v(-190.11, -176.77) * mm, "end": v(-178.1, -176.77) * mm});
            skArc(sketch, "E2633", {"start": v(-178.1, -176.77) * mm, "mid": v(-175.98, -175.9) * mm, "end": v(-175.1, -173.77) * mm});
            skLineSegment(sketch, "E2634", {"start": v(-175.1, -173.77) * mm, "end": v(-175.1, -146.57) * mm});
            skArc(sketch, "E2635", {"start": v(-175.1, -146.57) * mm, "mid": v(-175.98, -144.45) * mm, "end": v(-178.1, -143.57) * mm});
            skLineSegment(sketch, "E2636", {"start": v(-178.1, -143.57) * mm, "end": v(-190.11, -143.57) * mm});
            skLineSegment(sketch, "E2637", {"start": v(-190.11, -143.57) * mm, "end": v(-190.11, -146.57) * mm});
            skLineSegment(sketch, "E2638", {"start": v(-190.11, -146.57) * mm, "end": v(-187.11, -146.57) * mm});
            skLineSegment(sketch, "E2639", {"start": v(-187.11, -146.57) * mm, "end": v(-187.11, -145.3) * mm});
            skLineSegment(sketch, "E2640", {"start": v(-188.61, -160.17) * mm, "end": v(-188.61, -156.67) * mm});
            skLineSegment(sketch, "E2641", {"start": v(-188.61, -156.67) * mm, "end": v(-190.11, -156.67) * mm});
            skLineSegment(sketch, "E2642", {"start": v(-188.61, -160.17) * mm, "end": v(-188.61, -163.67) * mm});
            skLineSegment(sketch, "E2643", {"start": v(-188.61, -163.67) * mm, "end": v(-190.11, -163.67) * mm});
            skLineSegment(sketch, "E2644", {"start": v(325.8, -109.13) * mm, "end": v(331.73, -109.13) * mm});
            skLineSegment(sketch, "E2645", {"start": v(331.73, -109.13) * mm, "end": v(339.78, -106.06) * mm});
            skLineSegment(sketch, "E2646", {"start": v(341.36, -105.43) * mm, "end": v(341.54, -105.43) * mm});
            skLineSegment(sketch, "E2647", {"start": v(341.45, -105.52) * mm, "end": v(341.45, -105.34) * mm});
            skLineSegment(sketch, "E2648", {"start": v(355.16, 107.43) * mm, "end": v(349.23, 107.43) * mm});
            skLineSegment(sketch, "E2649", {"start": v(349.23, 107.43) * mm, "end": v(343.04, 104.36) * mm});
            skLineSegment(sketch, "E2650", {"start": v(341.36, 103.57) * mm, "end": v(341.54, 103.57) * mm});
            skLineSegment(sketch, "E2651", {"start": v(341.45, 103.48) * mm, "end": v(341.45, 103.66) * mm});
            skLineSegment(sketch, "E2652", {"start": v(142.97, 109.72) * mm, "end": v(137.04, 109.72) * mm});
            skLineSegment(sketch, "E2653", {"start": v(137.04, 109.72) * mm, "end": v(133.51, 105) * mm});
            skLineSegment(sketch, "E2654", {"start": v(132.36, 103.57) * mm, "end": v(132.54, 103.57) * mm});
            skLineSegment(sketch, "E2655", {"start": v(132.45, 103.48) * mm, "end": v(132.45, 103.66) * mm});
            skLineSegment(sketch, "E2656", {"start": v(147.36, -109.9) * mm, "end": v(141.43, -109.9) * mm});
            skLineSegment(sketch, "E2657", {"start": v(141.43, -109.9) * mm, "end": v(134.04, -106.23) * mm});
            skLineSegment(sketch, "E2658", {"start": v(132.36, -105.43) * mm, "end": v(132.54, -105.43) * mm});
            skLineSegment(sketch, "E2659", {"start": v(132.45, -105.52) * mm, "end": v(132.45, -105.34) * mm});
            skLineSegment(sketch, "E2660", {"start": v(337.47, 23.85) * mm, "end": v(337.47, 34.38) * mm});
            skArc(sketch, "E2661", {"start": v(337.72, 34.82) * mm, "mid": v(337.54, 34.63) * mm, "end": v(337.47, 34.38) * mm});
            skArc(sketch, "E2662", {"start": v(337.72, 34.82) * mm, "mid": v(337.83, 35.6) * mm, "end": v(337.04, 35.5) * mm});
            skArc(sketch, "E2663", {"start": v(336.6, 35.25) * mm, "mid": v(336.86, 35.32) * mm, "end": v(337.04, 35.5) * mm});
            skLineSegment(sketch, "E2664", {"start": v(336.6, 35.25) * mm, "end": v(334.97, 35.25) * mm});
            skLineSegment(sketch, "E2665", {"start": v(334.97, 41.25) * mm, "end": v(336.6, 41.25) * mm});
            skArc(sketch, "E2666", {"start": v(337.04, 41) * mm, "mid": v(336.86, 41.18) * mm, "end": v(336.6, 41.25) * mm});
            skArc(sketch, "E2667", {"start": v(337.04, 41) * mm, "mid": v(337.83, 40.9) * mm, "end": v(337.72, 41.68) * mm});
            skArc(sketch, "E2668", {"start": v(337.47, 42.12) * mm, "mid": v(337.54, 41.87) * mm, "end": v(337.72, 41.68) * mm});
            skLineSegment(sketch, "E2669", {"start": v(337.47, 42.12) * mm, "end": v(337.47, 47.25) * mm});
            skLineSegment(sketch, "E2670", {"start": v(337.47, 47.25) * mm, "end": v(340.47, 47.25) * mm});
            skLineSegment(sketch, "E2671", {"start": v(340.47, 47.25) * mm, "end": v(340.47, 45.97) * mm});
            skLineSegment(sketch, "E2672", {"start": v(340.47, 45.97) * mm, "end": v(344.47, 45.97) * mm});
            skLineSegment(sketch, "E2673", {"start": v(344.47, 45.97) * mm, "end": v(344.47, 47.25) * mm});
            skLineSegment(sketch, "E2674", {"start": v(344.47, 47.25) * mm, "end": v(347.47, 47.25) * mm});
            skLineSegment(sketch, "E2675", {"start": v(347.47, 47.25) * mm, "end": v(347.47, 50.45) * mm});
            skLineSegment(sketch, "E2676", {"start": v(347.47, 50.45) * mm, "end": v(344.47, 50.45) * mm});
            skLineSegment(sketch, "E2677", {"start": v(344.47, 50.45) * mm, "end": v(344.47, 51.72) * mm});
            skLineSegment(sketch, "E2678", {"start": v(344.47, 51.72) * mm, "end": v(340.47, 51.72) * mm});
            skLineSegment(sketch, "E2679", {"start": v(340.47, 51.72) * mm, "end": v(340.47, 50.45) * mm});
            skLineSegment(sketch, "E2680", {"start": v(340.47, 50.45) * mm, "end": v(337.47, 50.45) * mm});
            skLineSegment(sketch, "E2681", {"start": v(337.47, 50.45) * mm, "end": v(337.47, 55.58) * mm});
            skArc(sketch, "E2682", {"start": v(337.72, 56.02) * mm, "mid": v(337.54, 55.83) * mm, "end": v(337.47, 55.58) * mm});
            skArc(sketch, "E2683", {"start": v(337.72, 56.02) * mm, "mid": v(337.83, 56.8) * mm, "end": v(337.04, 56.7) * mm});
            skArc(sketch, "E2684", {"start": v(336.6, 56.45) * mm, "mid": v(336.86, 56.52) * mm, "end": v(337.04, 56.7) * mm});
            skLineSegment(sketch, "E2685", {"start": v(336.6, 56.45) * mm, "end": v(334.97, 56.45) * mm});
            skLineSegment(sketch, "E2686", {"start": v(334.97, 62.45) * mm, "end": v(336.6, 62.45) * mm});
            skArc(sketch, "E2687", {"start": v(337.04, 62.2) * mm, "mid": v(336.86, 62.38) * mm, "end": v(336.6, 62.45) * mm});
            skArc(sketch, "E2688", {"start": v(337.04, 62.2) * mm, "mid": v(337.83, 62.1) * mm, "end": v(337.72, 62.88) * mm});
            skArc(sketch, "E2689", {"start": v(337.47, 63.32) * mm, "mid": v(337.54, 63.07) * mm, "end": v(337.72, 62.88) * mm});
            skLineSegment(sketch, "E2690", {"start": v(337.47, 63.32) * mm, "end": v(337.47, 71.85) * mm});
            skLineSegment(sketch, "E2691", {"start": v(337.47, 71.85) * mm, "end": v(338.16, 71.85) * mm});
            skArc(sketch, "E2692", {"start": v(343.82, 69.5) * mm, "mid": v(341.22, 71.24) * mm, "end": v(338.16, 71.85) * mm});
            skArc(sketch, "E2693", {"start": v(355.3, 24.1) * mm, "mid": v(355.49, 23.92) * mm, "end": v(355.74, 23.85) * mm});
            skArc(sketch, "E2694", {"start": v(355.3, 24.1) * mm, "mid": v(354.52, 24.2) * mm, "end": v(354.62, 23.42) * mm});
            skArc(sketch, "E2695", {"start": v(354.87, 22.98) * mm, "mid": v(354.8, 23.23) * mm, "end": v(354.62, 23.42) * mm});
            skLineSegment(sketch, "E2696", {"start": v(354.87, 22.98) * mm, "end": v(354.87, 21.35) * mm});
            skArc(sketch, "E2697", {"start": v(354.37, 20.85) * mm, "mid": v(354.73, 21) * mm, "end": v(354.87, 21.35) * mm});
            skLineSegment(sketch, "E2698", {"start": v(354.37, 20.85) * mm, "end": v(349.37, 20.85) * mm});
            skArc(sketch, "E2699", {"start": v(348.87, 21.35) * mm, "mid": v(349.02, 21) * mm, "end": v(349.37, 20.85) * mm});
            skLineSegment(sketch, "E2700", {"start": v(348.87, 21.35) * mm, "end": v(348.87, 22.98) * mm});
            skArc(sketch, "E2701", {"start": v(349.12, 23.42) * mm, "mid": v(348.94, 23.23) * mm, "end": v(348.87, 22.98) * mm});
            skArc(sketch, "E2702", {"start": v(349.12, 23.42) * mm, "mid": v(349.23, 24.2) * mm, "end": v(348.44, 24.1) * mm});
            skArc(sketch, "E2703", {"start": v(348, 23.85) * mm, "mid": v(348.26, 23.92) * mm, "end": v(348.44, 24.1) * mm});
            skLineSegment(sketch, "E2704", {"start": v(348, 23.85) * mm, "end": v(337.47, 23.85) * mm});
            skArc(sketch, "E2705", {"start": v(334.47, 35.75) * mm, "mid": v(334.62, 35.4) * mm, "end": v(334.97, 35.25) * mm});
            skLineSegment(sketch, "E2706", {"start": v(334.47, 35.75) * mm, "end": v(334.47, 40.75) * mm});
            skArc(sketch, "E2707", {"start": v(334.97, 41.25) * mm, "mid": v(334.62, 41.1) * mm, "end": v(334.47, 40.75) * mm});
            skArc(sketch, "E2708", {"start": v(334.47, 56.95) * mm, "mid": v(334.62, 56.6) * mm, "end": v(334.97, 56.45) * mm});
            skLineSegment(sketch, "E2709", {"start": v(334.47, 56.95) * mm, "end": v(334.47, 61.95) * mm});
            skArc(sketch, "E2710", {"start": v(334.97, 62.45) * mm, "mid": v(334.62, 62.3) * mm, "end": v(334.47, 61.95) * mm});
            skArc(sketch, "E2711", {"start": v(385.47, 24.54) * mm, "mid": v(384.86, 27.6) * mm, "end": v(383.13, 30.2) * mm});
            skLineSegment(sketch, "E2712", {"start": v(385.47, 24.54) * mm, "end": v(385.47, 23.85) * mm});
            skLineSegment(sketch, "E2713", {"start": v(385.47, 23.85) * mm, "end": v(376.94, 23.85) * mm});
            skArc(sketch, "E2714", {"start": v(376.5, 24.1) * mm, "mid": v(376.69, 23.92) * mm, "end": v(376.94, 23.85) * mm});
            skArc(sketch, "E2715", {"start": v(376.5, 24.1) * mm, "mid": v(375.72, 24.2) * mm, "end": v(375.82, 23.42) * mm});
            skArc(sketch, "E2716", {"start": v(376.07, 22.98) * mm, "mid": v(376, 23.23) * mm, "end": v(375.82, 23.42) * mm});
            skLineSegment(sketch, "E2717", {"start": v(376.07, 22.98) * mm, "end": v(376.07, 21.35) * mm});
            skArc(sketch, "E2718", {"start": v(375.57, 20.85) * mm, "mid": v(375.93, 21) * mm, "end": v(376.07, 21.35) * mm});
            skLineSegment(sketch, "E2719", {"start": v(375.57, 20.85) * mm, "end": v(370.57, 20.85) * mm});
            skArc(sketch, "E2720", {"start": v(370.07, 21.35) * mm, "mid": v(370.22, 21) * mm, "end": v(370.57, 20.85) * mm});
            skLineSegment(sketch, "E2721", {"start": v(370.07, 21.35) * mm, "end": v(370.07, 22.98) * mm});
            skArc(sketch, "E2722", {"start": v(370.32, 23.42) * mm, "mid": v(370.14, 23.23) * mm, "end": v(370.07, 22.98) * mm});
            skArc(sketch, "E2723", {"start": v(370.32, 23.42) * mm, "mid": v(370.43, 24.2) * mm, "end": v(369.64, 24.1) * mm});
            skArc(sketch, "E2724", {"start": v(369.2, 23.85) * mm, "mid": v(369.46, 23.92) * mm, "end": v(369.64, 24.1) * mm});
            skLineSegment(sketch, "E2725", {"start": v(369.2, 23.85) * mm, "end": v(364.07, 23.85) * mm});
            skLineSegment(sketch, "E2726", {"start": v(364.07, 23.85) * mm, "end": v(364.07, 26.85) * mm});
            skLineSegment(sketch, "E2727", {"start": v(364.07, 26.85) * mm, "end": v(365.35, 26.85) * mm});
            skLineSegment(sketch, "E2728", {"start": v(365.35, 26.85) * mm, "end": v(365.35, 30.85) * mm});
            skLineSegment(sketch, "E2729", {"start": v(365.35, 30.85) * mm, "end": v(364.07, 30.85) * mm});
            skLineSegment(sketch, "E2730", {"start": v(364.07, 30.85) * mm, "end": v(364.07, 33.85) * mm});
            skLineSegment(sketch, "E2731", {"start": v(364.07, 33.85) * mm, "end": v(360.87, 33.85) * mm});
            skLineSegment(sketch, "E2732", {"start": v(360.87, 33.85) * mm, "end": v(360.87, 30.85) * mm});
            skLineSegment(sketch, "E2733", {"start": v(360.87, 30.85) * mm, "end": v(359.6, 30.85) * mm});
            skLineSegment(sketch, "E2734", {"start": v(359.6, 30.85) * mm, "end": v(359.6, 26.85) * mm});
            skLineSegment(sketch, "E2735", {"start": v(359.6, 26.85) * mm, "end": v(360.87, 26.85) * mm});
            skLineSegment(sketch, "E2736", {"start": v(360.87, 26.85) * mm, "end": v(360.87, 23.85) * mm});
            skLineSegment(sketch, "E2737", {"start": v(360.87, 23.85) * mm, "end": v(355.74, 23.85) * mm});
            skLineSegment(sketch, "E2738", {"start": v(343.82, 69.5) * mm, "end": v(383.13, 30.2) * mm});
            skLineSegment(sketch, "E2739", {"start": v(337.03, -81.42) * mm, "end": v(337.03, -70.89) * mm});
            skArc(sketch, "E2740", {"start": v(337.28, -70.45) * mm, "mid": v(337.1, -70.64) * mm, "end": v(337.03, -70.89) * mm});
            skArc(sketch, "E2741", {"start": v(337.28, -70.45) * mm, "mid": v(337.38, -69.67) * mm, "end": v(336.6, -69.77) * mm});
            skArc(sketch, "E2742", {"start": v(336.16, -70.02) * mm, "mid": v(336.41, -69.95) * mm, "end": v(336.6, -69.77) * mm});
            skLineSegment(sketch, "E2743", {"start": v(336.16, -70.02) * mm, "end": v(334.53, -70.02) * mm});
            skLineSegment(sketch, "E2744", {"start": v(334.53, -64.02) * mm, "end": v(336.16, -64.02) * mm});
            skArc(sketch, "E2745", {"start": v(336.6, -64.27) * mm, "mid": v(336.41, -64.09) * mm, "end": v(336.16, -64.02) * mm});
            skArc(sketch, "E2746", {"start": v(336.6, -64.27) * mm, "mid": v(337.38, -64.37) * mm, "end": v(337.28, -63.59) * mm});
            skArc(sketch, "E2747", {"start": v(337.03, -63.15) * mm, "mid": v(337.1, -63.4) * mm, "end": v(337.28, -63.59) * mm});
            skLineSegment(sketch, "E2748", {"start": v(337.03, -63.15) * mm, "end": v(337.03, -58.02) * mm});
            skLineSegment(sketch, "E2749", {"start": v(337.03, -58.02) * mm, "end": v(340.03, -58.02) * mm});
            skLineSegment(sketch, "E2750", {"start": v(340.03, -58.02) * mm, "end": v(340.03, -59.3) * mm});
            skLineSegment(sketch, "E2751", {"start": v(340.03, -59.3) * mm, "end": v(344.03, -59.3) * mm});
            skLineSegment(sketch, "E2752", {"start": v(344.03, -59.3) * mm, "end": v(344.03, -58.02) * mm});
            skLineSegment(sketch, "E2753", {"start": v(344.03, -58.02) * mm, "end": v(347.03, -58.02) * mm});
            skLineSegment(sketch, "E2754", {"start": v(347.03, -58.02) * mm, "end": v(347.03, -54.82) * mm});
            skLineSegment(sketch, "E2755", {"start": v(347.03, -54.82) * mm, "end": v(344.03, -54.82) * mm});
            skLineSegment(sketch, "E2756", {"start": v(344.03, -54.82) * mm, "end": v(344.03, -53.54) * mm});
            skLineSegment(sketch, "E2757", {"start": v(344.03, -53.54) * mm, "end": v(340.03, -53.54) * mm});
            skLineSegment(sketch, "E2758", {"start": v(340.03, -53.54) * mm, "end": v(340.03, -54.82) * mm});
            skLineSegment(sketch, "E2759", {"start": v(340.03, -54.82) * mm, "end": v(337.03, -54.82) * mm});
            skLineSegment(sketch, "E2760", {"start": v(337.03, -54.82) * mm, "end": v(337.03, -49.69) * mm});
            skArc(sketch, "E2761", {"start": v(337.28, -49.25) * mm, "mid": v(337.1, -49.44) * mm, "end": v(337.03, -49.69) * mm});
            skArc(sketch, "E2762", {"start": v(337.28, -49.25) * mm, "mid": v(337.38, -48.47) * mm, "end": v(336.6, -48.57) * mm});
            skArc(sketch, "E2763", {"start": v(336.16, -48.82) * mm, "mid": v(336.41, -48.75) * mm, "end": v(336.6, -48.57) * mm});
            skLineSegment(sketch, "E2764", {"start": v(336.16, -48.82) * mm, "end": v(334.53, -48.82) * mm});
            skLineSegment(sketch, "E2765", {"start": v(334.53, -42.82) * mm, "end": v(336.16, -42.82) * mm});
            skArc(sketch, "E2766", {"start": v(336.6, -43.07) * mm, "mid": v(336.41, -42.89) * mm, "end": v(336.16, -42.82) * mm});
            skArc(sketch, "E2767", {"start": v(336.6, -43.07) * mm, "mid": v(337.38, -43.17) * mm, "end": v(337.28, -42.39) * mm});
            skArc(sketch, "E2768", {"start": v(337.03, -41.95) * mm, "mid": v(337.1, -42.2) * mm, "end": v(337.28, -42.39) * mm});
            skLineSegment(sketch, "E2769", {"start": v(337.03, -41.95) * mm, "end": v(337.03, -33.42) * mm});
            skLineSegment(sketch, "E2770", {"start": v(337.03, -33.42) * mm, "end": v(337.72, -33.42) * mm});
            skArc(sketch, "E2771", {"start": v(343.37, -35.76) * mm, "mid": v(340.78, -34.03) * mm, "end": v(337.72, -33.42) * mm});
            skArc(sketch, "E2772", {"start": v(354.86, -81.17) * mm, "mid": v(355.05, -81.35) * mm, "end": v(355.3, -81.42) * mm});
            skArc(sketch, "E2773", {"start": v(354.86, -81.17) * mm, "mid": v(354.08, -81.07) * mm, "end": v(354.18, -81.85) * mm});
            skArc(sketch, "E2774", {"start": v(354.43, -82.29) * mm, "mid": v(354.36, -82.04) * mm, "end": v(354.18, -81.85) * mm});
            skLineSegment(sketch, "E2775", {"start": v(354.43, -82.29) * mm, "end": v(354.43, -83.92) * mm});
            skArc(sketch, "E2776", {"start": v(353.93, -84.42) * mm, "mid": v(354.28, -84.27) * mm, "end": v(354.43, -83.92) * mm});
            skLineSegment(sketch, "E2777", {"start": v(353.93, -84.42) * mm, "end": v(348.93, -84.42) * mm});
            skArc(sketch, "E2778", {"start": v(348.43, -83.92) * mm, "mid": v(348.58, -84.27) * mm, "end": v(348.93, -84.42) * mm});
            skLineSegment(sketch, "E2779", {"start": v(348.43, -83.92) * mm, "end": v(348.43, -82.29) * mm});
            skArc(sketch, "E2780", {"start": v(348.68, -81.85) * mm, "mid": v(348.5, -82.04) * mm, "end": v(348.43, -82.29) * mm});
            skArc(sketch, "E2781", {"start": v(348.68, -81.85) * mm, "mid": v(348.78, -81.07) * mm, "end": v(348, -81.17) * mm});
            skArc(sketch, "E2782", {"start": v(347.56, -81.42) * mm, "mid": v(347.81, -81.35) * mm, "end": v(348, -81.17) * mm});
            skLineSegment(sketch, "E2783", {"start": v(347.56, -81.42) * mm, "end": v(337.03, -81.42) * mm});
            skArc(sketch, "E2784", {"start": v(334.03, -69.52) * mm, "mid": v(334.18, -69.87) * mm, "end": v(334.53, -70.02) * mm});
            skLineSegment(sketch, "E2785", {"start": v(334.03, -69.52) * mm, "end": v(334.03, -64.52) * mm});
            skArc(sketch, "E2786", {"start": v(334.53, -64.02) * mm, "mid": v(334.18, -64.17) * mm, "end": v(334.03, -64.52) * mm});
            skArc(sketch, "E2787", {"start": v(334.03, -48.32) * mm, "mid": v(334.18, -48.67) * mm, "end": v(334.53, -48.82) * mm});
            skLineSegment(sketch, "E2788", {"start": v(334.03, -48.32) * mm, "end": v(334.03, -43.32) * mm});
            skArc(sketch, "E2789", {"start": v(334.53, -42.82) * mm, "mid": v(334.18, -42.97) * mm, "end": v(334.03, -43.32) * mm});
            skArc(sketch, "E2790", {"start": v(385.03, -80.73) * mm, "mid": v(384.42, -77.67) * mm, "end": v(382.69, -75.08) * mm});
            skLineSegment(sketch, "E2791", {"start": v(385.03, -80.73) * mm, "end": v(385.03, -81.42) * mm});
            skLineSegment(sketch, "E2792", {"start": v(385.03, -81.42) * mm, "end": v(376.5, -81.42) * mm});
            skArc(sketch, "E2793", {"start": v(376.06, -81.17) * mm, "mid": v(376.25, -81.35) * mm, "end": v(376.5, -81.42) * mm});
            skArc(sketch, "E2794", {"start": v(376.06, -81.17) * mm, "mid": v(375.28, -81.07) * mm, "end": v(375.38, -81.85) * mm});
            skArc(sketch, "E2795", {"start": v(375.63, -82.29) * mm, "mid": v(375.56, -82.04) * mm, "end": v(375.38, -81.85) * mm});
            skLineSegment(sketch, "E2796", {"start": v(375.63, -82.29) * mm, "end": v(375.63, -83.92) * mm});
            skArc(sketch, "E2797", {"start": v(375.13, -84.42) * mm, "mid": v(375.48, -84.27) * mm, "end": v(375.63, -83.92) * mm});
            skLineSegment(sketch, "E2798", {"start": v(375.13, -84.42) * mm, "end": v(370.13, -84.42) * mm});
            skArc(sketch, "E2799", {"start": v(369.63, -83.92) * mm, "mid": v(369.78, -84.27) * mm, "end": v(370.13, -84.42) * mm});
            skLineSegment(sketch, "E2800", {"start": v(369.63, -83.92) * mm, "end": v(369.63, -82.29) * mm});
            skArc(sketch, "E2801", {"start": v(369.88, -81.85) * mm, "mid": v(369.7, -82.04) * mm, "end": v(369.63, -82.29) * mm});
            skArc(sketch, "E2802", {"start": v(369.88, -81.85) * mm, "mid": v(369.98, -81.07) * mm, "end": v(369.2, -81.17) * mm});
            skArc(sketch, "E2803", {"start": v(368.76, -81.42) * mm, "mid": v(369.01, -81.35) * mm, "end": v(369.2, -81.17) * mm});
            skLineSegment(sketch, "E2804", {"start": v(368.76, -81.42) * mm, "end": v(363.63, -81.42) * mm});
            skLineSegment(sketch, "E2805", {"start": v(363.63, -81.42) * mm, "end": v(363.63, -78.42) * mm});
            skLineSegment(sketch, "E2806", {"start": v(363.63, -78.42) * mm, "end": v(364.9, -78.42) * mm});
            skLineSegment(sketch, "E2807", {"start": v(364.9, -78.42) * mm, "end": v(364.9, -74.42) * mm});
            skLineSegment(sketch, "E2808", {"start": v(364.9, -74.42) * mm, "end": v(363.63, -74.42) * mm});
            skLineSegment(sketch, "E2809", {"start": v(363.63, -74.42) * mm, "end": v(363.63, -71.42) * mm});
            skLineSegment(sketch, "E2810", {"start": v(363.63, -71.42) * mm, "end": v(360.43, -71.42) * mm});
            skLineSegment(sketch, "E2811", {"start": v(360.43, -71.42) * mm, "end": v(360.43, -74.42) * mm});
            skLineSegment(sketch, "E2812", {"start": v(360.43, -74.42) * mm, "end": v(359.15, -74.42) * mm});
            skLineSegment(sketch, "E2813", {"start": v(359.15, -74.42) * mm, "end": v(359.15, -78.42) * mm});
            skLineSegment(sketch, "E2814", {"start": v(359.15, -78.42) * mm, "end": v(360.43, -78.42) * mm});
            skLineSegment(sketch, "E2815", {"start": v(360.43, -78.42) * mm, "end": v(360.43, -81.42) * mm});
            skLineSegment(sketch, "E2816", {"start": v(360.43, -81.42) * mm, "end": v(355.3, -81.42) * mm});
            skLineSegment(sketch, "E2817", {"start": v(343.37, -35.76) * mm, "end": v(382.69, -75.08) * mm});
            skLineSegment(sketch, "E2818", {"start": v(386.68, -16.72) * mm, "end": v(386.68, -27.26) * mm});
            skArc(sketch, "E2819", {"start": v(386.43, -27.69) * mm, "mid": v(386.62, -27.5) * mm, "end": v(386.68, -27.26) * mm});
            skArc(sketch, "E2820", {"start": v(338.68, -17.4) * mm, "mid": v(339.3, -20.47) * mm, "end": v(341.03, -23.07) * mm});
            skLineSegment(sketch, "E2821", {"start": v(338.68, -17.4) * mm, "end": v(338.68, -16.72) * mm});
            skLineSegment(sketch, "E2822", {"start": v(338.68, -16.72) * mm, "end": v(347.22, -16.72) * mm});
            skArc(sketch, "E2823", {"start": v(347.65, -16.97) * mm, "mid": v(347.47, -16.79) * mm, "end": v(347.22, -16.72) * mm});
            skArc(sketch, "E2824", {"start": v(347.65, -16.97) * mm, "mid": v(348.44, -17.08) * mm, "end": v(348.33, -16.29) * mm});
            skArc(sketch, "E2825", {"start": v(348.08, -15.86) * mm, "mid": v(348.15, -16.1) * mm, "end": v(348.33, -16.29) * mm});
            skLineSegment(sketch, "E2826", {"start": v(348.08, -15.86) * mm, "end": v(348.08, -14.22) * mm});
            skArc(sketch, "E2827", {"start": v(348.58, -13.72) * mm, "mid": v(348.23, -13.87) * mm, "end": v(348.08, -14.22) * mm});
            skLineSegment(sketch, "E2828", {"start": v(348.58, -13.72) * mm, "end": v(353.58, -13.72) * mm});
            skArc(sketch, "E2829", {"start": v(354.08, -14.22) * mm, "mid": v(353.94, -13.87) * mm, "end": v(353.58, -13.72) * mm});
            skLineSegment(sketch, "E2830", {"start": v(354.08, -14.22) * mm, "end": v(354.08, -15.86) * mm});
            skArc(sketch, "E2831", {"start": v(353.83, -16.29) * mm, "mid": v(354.02, -16.1) * mm, "end": v(354.08, -15.86) * mm});
            skArc(sketch, "E2832", {"start": v(353.83, -16.29) * mm, "mid": v(353.73, -17.08) * mm, "end": v(354.52, -16.97) * mm});
            skArc(sketch, "E2833", {"start": v(354.95, -16.72) * mm, "mid": v(354.7, -16.79) * mm, "end": v(354.52, -16.97) * mm});
            skLineSegment(sketch, "E2834", {"start": v(354.95, -16.72) * mm, "end": v(360.08, -16.72) * mm});
            skLineSegment(sketch, "E2835", {"start": v(360.08, -16.72) * mm, "end": v(360.08, -19.72) * mm});
            skLineSegment(sketch, "E2836", {"start": v(360.08, -19.72) * mm, "end": v(358.8, -19.72) * mm});
            skLineSegment(sketch, "E2837", {"start": v(358.8, -19.72) * mm, "end": v(358.8, -23.72) * mm});
            skLineSegment(sketch, "E2838", {"start": v(358.8, -23.72) * mm, "end": v(360.08, -23.72) * mm});
            skLineSegment(sketch, "E2839", {"start": v(360.08, -23.72) * mm, "end": v(360.08, -26.72) * mm});
            skLineSegment(sketch, "E2840", {"start": v(360.08, -26.72) * mm, "end": v(363.28, -26.72) * mm});
            skLineSegment(sketch, "E2841", {"start": v(363.28, -26.72) * mm, "end": v(363.28, -23.72) * mm});
            skLineSegment(sketch, "E2842", {"start": v(363.28, -23.72) * mm, "end": v(364.56, -23.72) * mm});
            skLineSegment(sketch, "E2843", {"start": v(364.56, -23.72) * mm, "end": v(364.56, -19.72) * mm});
            skLineSegment(sketch, "E2844", {"start": v(364.56, -19.72) * mm, "end": v(363.28, -19.72) * mm});
            skLineSegment(sketch, "E2845", {"start": v(363.28, -19.72) * mm, "end": v(363.28, -16.72) * mm});
            skLineSegment(sketch, "E2846", {"start": v(363.28, -16.72) * mm, "end": v(368.42, -16.72) * mm});
            skArc(sketch, "E2847", {"start": v(368.85, -16.97) * mm, "mid": v(368.67, -16.79) * mm, "end": v(368.42, -16.72) * mm});
            skArc(sketch, "E2848", {"start": v(368.85, -16.97) * mm, "mid": v(369.64, -17.08) * mm, "end": v(369.53, -16.29) * mm});
            skArc(sketch, "E2849", {"start": v(369.28, -15.86) * mm, "mid": v(369.35, -16.1) * mm, "end": v(369.53, -16.29) * mm});
            skLineSegment(sketch, "E2850", {"start": v(369.28, -15.86) * mm, "end": v(369.28, -14.22) * mm});
            skArc(sketch, "E2851", {"start": v(369.78, -13.72) * mm, "mid": v(369.43, -13.87) * mm, "end": v(369.28, -14.22) * mm});
            skLineSegment(sketch, "E2852", {"start": v(369.78, -13.72) * mm, "end": v(374.78, -13.72) * mm});
            skArc(sketch, "E2853", {"start": v(375.28, -14.22) * mm, "mid": v(375.14, -13.87) * mm, "end": v(374.78, -13.72) * mm});
            skLineSegment(sketch, "E2854", {"start": v(375.28, -14.22) * mm, "end": v(375.28, -15.86) * mm});
            skArc(sketch, "E2855", {"start": v(375.03, -16.29) * mm, "mid": v(375.22, -16.1) * mm, "end": v(375.28, -15.86) * mm});
            skArc(sketch, "E2856", {"start": v(375.03, -16.29) * mm, "mid": v(374.93, -17.08) * mm, "end": v(375.72, -16.97) * mm});
            skArc(sketch, "E2857", {"start": v(376.15, -16.72) * mm, "mid": v(375.9, -16.79) * mm, "end": v(375.72, -16.97) * mm});
            skLineSegment(sketch, "E2858", {"start": v(376.15, -16.72) * mm, "end": v(386.68, -16.72) * mm});
            skArc(sketch, "E2859", {"start": v(386.43, -27.69) * mm, "mid": v(386.33, -28.48) * mm, "end": v(387.12, -28.37) * mm});
            skArc(sketch, "E2860", {"start": v(387.55, -28.12) * mm, "mid": v(387.3, -28.19) * mm, "end": v(387.12, -28.37) * mm});
            skLineSegment(sketch, "E2861", {"start": v(387.55, -28.12) * mm, "end": v(389.18, -28.12) * mm});
            skArc(sketch, "E2862", {"start": v(389.68, -28.62) * mm, "mid": v(389.54, -28.27) * mm, "end": v(389.18, -28.12) * mm});
            skLineSegment(sketch, "E2863", {"start": v(389.68, -28.62) * mm, "end": v(389.68, -33.62) * mm});
            skArc(sketch, "E2864", {"start": v(389.18, -34.12) * mm, "mid": v(389.54, -33.98) * mm, "end": v(389.68, -33.62) * mm});
            skLineSegment(sketch, "E2865", {"start": v(389.18, -34.12) * mm, "end": v(387.55, -34.12) * mm});
            skArc(sketch, "E2866", {"start": v(387.12, -33.87) * mm, "mid": v(387.3, -34.06) * mm, "end": v(387.55, -34.12) * mm});
            skArc(sketch, "E2867", {"start": v(387.12, -33.87) * mm, "mid": v(386.33, -33.77) * mm, "end": v(386.43, -34.56) * mm});
            skArc(sketch, "E2868", {"start": v(386.68, -34.99) * mm, "mid": v(386.62, -34.74) * mm, "end": v(386.43, -34.56) * mm});
            skLineSegment(sketch, "E2869", {"start": v(386.68, -34.99) * mm, "end": v(386.68, -40.12) * mm});
            skLineSegment(sketch, "E2870", {"start": v(386.68, -40.12) * mm, "end": v(383.68, -40.12) * mm});
            skLineSegment(sketch, "E2871", {"start": v(383.68, -40.12) * mm, "end": v(383.68, -38.85) * mm});
            skLineSegment(sketch, "E2872", {"start": v(383.68, -38.85) * mm, "end": v(379.68, -38.85) * mm});
            skLineSegment(sketch, "E2873", {"start": v(379.68, -38.85) * mm, "end": v(379.68, -40.12) * mm});
            skLineSegment(sketch, "E2874", {"start": v(379.68, -40.12) * mm, "end": v(376.68, -40.12) * mm});
            skLineSegment(sketch, "E2875", {"start": v(376.68, -40.12) * mm, "end": v(376.68, -43.32) * mm});
            skLineSegment(sketch, "E2876", {"start": v(376.68, -43.32) * mm, "end": v(379.68, -43.32) * mm});
            skLineSegment(sketch, "E2877", {"start": v(379.68, -43.32) * mm, "end": v(379.68, -44.6) * mm});
            skLineSegment(sketch, "E2878", {"start": v(379.68, -44.6) * mm, "end": v(383.68, -44.6) * mm});
            skLineSegment(sketch, "E2879", {"start": v(383.68, -44.6) * mm, "end": v(383.68, -43.32) * mm});
            skLineSegment(sketch, "E2880", {"start": v(383.68, -43.32) * mm, "end": v(386.68, -43.32) * mm});
            skLineSegment(sketch, "E2881", {"start": v(386.68, -43.32) * mm, "end": v(386.68, -48.46) * mm});
            skArc(sketch, "E2882", {"start": v(386.43, -48.89) * mm, "mid": v(386.62, -48.7) * mm, "end": v(386.68, -48.46) * mm});
            skArc(sketch, "E2883", {"start": v(386.43, -48.89) * mm, "mid": v(386.33, -49.68) * mm, "end": v(387.12, -49.57) * mm});
            skArc(sketch, "E2884", {"start": v(387.55, -49.32) * mm, "mid": v(387.3, -49.39) * mm, "end": v(387.12, -49.57) * mm});
            skLineSegment(sketch, "E2885", {"start": v(387.55, -49.32) * mm, "end": v(389.18, -49.32) * mm});
            skArc(sketch, "E2886", {"start": v(389.68, -49.82) * mm, "mid": v(389.54, -49.47) * mm, "end": v(389.18, -49.32) * mm});
            skLineSegment(sketch, "E2887", {"start": v(389.68, -49.82) * mm, "end": v(389.68, -54.82) * mm});
            skArc(sketch, "E2888", {"start": v(389.18, -55.32) * mm, "mid": v(389.54, -55.18) * mm, "end": v(389.68, -54.82) * mm});
            skLineSegment(sketch, "E2889", {"start": v(389.18, -55.32) * mm, "end": v(387.55, -55.32) * mm});
            skArc(sketch, "E2890", {"start": v(387.12, -55.07) * mm, "mid": v(387.3, -55.26) * mm, "end": v(387.55, -55.32) * mm});
            skArc(sketch, "E2891", {"start": v(387.12, -55.07) * mm, "mid": v(386.33, -54.97) * mm, "end": v(386.43, -55.76) * mm});
            skArc(sketch, "E2892", {"start": v(386.68, -56.19) * mm, "mid": v(386.62, -55.94) * mm, "end": v(386.43, -55.76) * mm});
            skLineSegment(sketch, "E2893", {"start": v(386.68, -56.19) * mm, "end": v(386.68, -64.72) * mm});
            skLineSegment(sketch, "E2894", {"start": v(386.68, -64.72) * mm, "end": v(386, -64.72) * mm});
            skArc(sketch, "E2895", {"start": v(380.34, -62.38) * mm, "mid": v(382.94, -64.11) * mm, "end": v(386, -64.72) * mm});
            skLineSegment(sketch, "E2896", {"start": v(380.34, -62.38) * mm, "end": v(341.03, -23.07) * mm});
            skLineSegment(sketch, "E2897", {"start": v(388.81, 85.01) * mm, "end": v(388.81, 74.48) * mm});
            skArc(sketch, "E2898", {"start": v(388.56, 74.04) * mm, "mid": v(388.75, 74.23) * mm, "end": v(388.81, 74.48) * mm});
            skArc(sketch, "E2899", {"start": v(340.81, 84.33) * mm, "mid": v(341.42, 81.26) * mm, "end": v(343.16, 78.67) * mm});
            skLineSegment(sketch, "E2900", {"start": v(340.81, 84.33) * mm, "end": v(340.81, 85.01) * mm});
            skLineSegment(sketch, "E2901", {"start": v(340.81, 85.01) * mm, "end": v(349.35, 85.01) * mm});
            skArc(sketch, "E2902", {"start": v(349.78, 84.76) * mm, "mid": v(349.6, 84.94) * mm, "end": v(349.35, 85.01) * mm});
            skArc(sketch, "E2903", {"start": v(349.78, 84.76) * mm, "mid": v(350.57, 84.66) * mm, "end": v(350.46, 85.44) * mm});
            skArc(sketch, "E2904", {"start": v(350.21, 85.88) * mm, "mid": v(350.28, 85.63) * mm, "end": v(350.46, 85.44) * mm});
            skLineSegment(sketch, "E2905", {"start": v(350.21, 85.88) * mm, "end": v(350.21, 87.51) * mm});
            skArc(sketch, "E2906", {"start": v(350.71, 88.01) * mm, "mid": v(350.36, 87.87) * mm, "end": v(350.21, 87.51) * mm});
            skLineSegment(sketch, "E2907", {"start": v(350.71, 88.01) * mm, "end": v(355.71, 88.01) * mm});
            skArc(sketch, "E2908", {"start": v(356.21, 87.51) * mm, "mid": v(356.07, 87.87) * mm, "end": v(355.71, 88.01) * mm});
            skLineSegment(sketch, "E2909", {"start": v(356.21, 87.51) * mm, "end": v(356.21, 85.88) * mm});
            skArc(sketch, "E2910", {"start": v(355.96, 85.44) * mm, "mid": v(356.15, 85.63) * mm, "end": v(356.21, 85.88) * mm});
            skArc(sketch, "E2911", {"start": v(355.96, 85.44) * mm, "mid": v(355.86, 84.66) * mm, "end": v(356.65, 84.76) * mm});
            skArc(sketch, "E2912", {"start": v(357.08, 85.01) * mm, "mid": v(356.83, 84.94) * mm, "end": v(356.65, 84.76) * mm});
            skLineSegment(sketch, "E2913", {"start": v(357.08, 85.01) * mm, "end": v(362.21, 85.01) * mm});
            skLineSegment(sketch, "E2914", {"start": v(362.21, 85.01) * mm, "end": v(362.21, 82.01) * mm});
            skLineSegment(sketch, "E2915", {"start": v(362.21, 82.01) * mm, "end": v(360.94, 82.01) * mm});
            skLineSegment(sketch, "E2916", {"start": v(360.94, 82.01) * mm, "end": v(360.94, 78.01) * mm});
            skLineSegment(sketch, "E2917", {"start": v(360.94, 78.01) * mm, "end": v(362.21, 78.01) * mm});
            skLineSegment(sketch, "E2918", {"start": v(362.21, 78.01) * mm, "end": v(362.21, 75.01) * mm});
            skLineSegment(sketch, "E2919", {"start": v(362.21, 75.01) * mm, "end": v(365.41, 75.01) * mm});
            skLineSegment(sketch, "E2920", {"start": v(365.41, 75.01) * mm, "end": v(365.41, 78.01) * mm});
            skLineSegment(sketch, "E2921", {"start": v(365.41, 78.01) * mm, "end": v(366.69, 78.01) * mm});
            skLineSegment(sketch, "E2922", {"start": v(366.69, 78.01) * mm, "end": v(366.69, 82.01) * mm});
            skLineSegment(sketch, "E2923", {"start": v(366.69, 82.01) * mm, "end": v(365.41, 82.01) * mm});
            skLineSegment(sketch, "E2924", {"start": v(365.41, 82.01) * mm, "end": v(365.41, 85.01) * mm});
            skLineSegment(sketch, "E2925", {"start": v(365.41, 85.01) * mm, "end": v(370.55, 85.01) * mm});
            skArc(sketch, "E2926", {"start": v(370.98, 84.76) * mm, "mid": v(370.8, 84.94) * mm, "end": v(370.55, 85.01) * mm});
            skArc(sketch, "E2927", {"start": v(370.98, 84.76) * mm, "mid": v(371.77, 84.66) * mm, "end": v(371.66, 85.44) * mm});
            skArc(sketch, "E2928", {"start": v(371.41, 85.88) * mm, "mid": v(371.48, 85.63) * mm, "end": v(371.66, 85.44) * mm});
            skLineSegment(sketch, "E2929", {"start": v(371.41, 85.88) * mm, "end": v(371.41, 87.51) * mm});
            skArc(sketch, "E2930", {"start": v(371.91, 88.01) * mm, "mid": v(371.56, 87.87) * mm, "end": v(371.41, 87.51) * mm});
            skLineSegment(sketch, "E2931", {"start": v(371.91, 88.01) * mm, "end": v(376.91, 88.01) * mm});
            skArc(sketch, "E2932", {"start": v(377.41, 87.51) * mm, "mid": v(377.27, 87.87) * mm, "end": v(376.91, 88.01) * mm});
            skLineSegment(sketch, "E2933", {"start": v(377.41, 87.51) * mm, "end": v(377.41, 85.88) * mm});
            skArc(sketch, "E2934", {"start": v(377.16, 85.44) * mm, "mid": v(377.35, 85.63) * mm, "end": v(377.41, 85.88) * mm});
            skArc(sketch, "E2935", {"start": v(377.16, 85.44) * mm, "mid": v(377.06, 84.66) * mm, "end": v(377.85, 84.76) * mm});
            skArc(sketch, "E2936", {"start": v(378.28, 85.01) * mm, "mid": v(378.03, 84.94) * mm, "end": v(377.85, 84.76) * mm});
            skLineSegment(sketch, "E2937", {"start": v(378.28, 85.01) * mm, "end": v(388.81, 85.01) * mm});
            skArc(sketch, "E2938", {"start": v(388.56, 74.04) * mm, "mid": v(388.46, 73.26) * mm, "end": v(389.25, 73.36) * mm});
            skArc(sketch, "E2939", {"start": v(389.68, 73.61) * mm, "mid": v(389.43, 73.54) * mm, "end": v(389.25, 73.36) * mm});
            skLineSegment(sketch, "E2940", {"start": v(389.68, 73.61) * mm, "end": v(391.31, 73.61) * mm});
            skArc(sketch, "E2941", {"start": v(391.81, 73.11) * mm, "mid": v(391.67, 73.47) * mm, "end": v(391.31, 73.61) * mm});
            skLineSegment(sketch, "E2942", {"start": v(391.81, 73.11) * mm, "end": v(391.81, 68.11) * mm});
            skArc(sketch, "E2943", {"start": v(391.31, 67.61) * mm, "mid": v(391.67, 67.76) * mm, "end": v(391.81, 68.11) * mm});
            skLineSegment(sketch, "E2944", {"start": v(391.31, 67.61) * mm, "end": v(389.68, 67.61) * mm});
            skArc(sketch, "E2945", {"start": v(389.25, 67.86) * mm, "mid": v(389.43, 67.68) * mm, "end": v(389.68, 67.61) * mm});
            skArc(sketch, "E2946", {"start": v(389.25, 67.86) * mm, "mid": v(388.46, 67.97) * mm, "end": v(388.56, 67.18) * mm});
            skArc(sketch, "E2947", {"start": v(388.81, 66.75) * mm, "mid": v(388.75, 67) * mm, "end": v(388.56, 67.18) * mm});
            skLineSegment(sketch, "E2948", {"start": v(388.81, 66.75) * mm, "end": v(388.81, 61.61) * mm});
            skLineSegment(sketch, "E2949", {"start": v(388.81, 61.61) * mm, "end": v(385.81, 61.61) * mm});
            skLineSegment(sketch, "E2950", {"start": v(385.81, 61.61) * mm, "end": v(385.81, 62.89) * mm});
            skLineSegment(sketch, "E2951", {"start": v(385.81, 62.89) * mm, "end": v(381.81, 62.89) * mm});
            skLineSegment(sketch, "E2952", {"start": v(381.81, 62.89) * mm, "end": v(381.81, 61.61) * mm});
            skLineSegment(sketch, "E2953", {"start": v(381.81, 61.61) * mm, "end": v(378.81, 61.61) * mm});
            skLineSegment(sketch, "E2954", {"start": v(378.81, 61.61) * mm, "end": v(378.81, 58.41) * mm});
            skLineSegment(sketch, "E2955", {"start": v(378.81, 58.41) * mm, "end": v(381.81, 58.41) * mm});
            skLineSegment(sketch, "E2956", {"start": v(381.81, 58.41) * mm, "end": v(381.81, 57.14) * mm});
            skLineSegment(sketch, "E2957", {"start": v(381.81, 57.14) * mm, "end": v(385.81, 57.14) * mm});
            skLineSegment(sketch, "E2958", {"start": v(385.81, 57.14) * mm, "end": v(385.81, 58.41) * mm});
            skLineSegment(sketch, "E2959", {"start": v(385.81, 58.41) * mm, "end": v(388.81, 58.41) * mm});
            skLineSegment(sketch, "E2960", {"start": v(388.81, 58.41) * mm, "end": v(388.81, 53.28) * mm});
            skArc(sketch, "E2961", {"start": v(388.56, 52.84) * mm, "mid": v(388.75, 53.03) * mm, "end": v(388.81, 53.28) * mm});
            skArc(sketch, "E2962", {"start": v(388.56, 52.84) * mm, "mid": v(388.46, 52.06) * mm, "end": v(389.25, 52.16) * mm});
            skArc(sketch, "E2963", {"start": v(389.68, 52.41) * mm, "mid": v(389.43, 52.34) * mm, "end": v(389.25, 52.16) * mm});
            skLineSegment(sketch, "E2964", {"start": v(389.68, 52.41) * mm, "end": v(391.31, 52.41) * mm});
            skArc(sketch, "E2965", {"start": v(391.81, 51.91) * mm, "mid": v(391.67, 52.27) * mm, "end": v(391.31, 52.41) * mm});
            skLineSegment(sketch, "E2966", {"start": v(391.81, 51.91) * mm, "end": v(391.81, 46.91) * mm});
            skArc(sketch, "E2967", {"start": v(391.31, 46.41) * mm, "mid": v(391.67, 46.56) * mm, "end": v(391.81, 46.91) * mm});
            skLineSegment(sketch, "E2968", {"start": v(391.31, 46.41) * mm, "end": v(389.68, 46.41) * mm});
            skArc(sketch, "E2969", {"start": v(389.25, 46.66) * mm, "mid": v(389.43, 46.48) * mm, "end": v(389.68, 46.41) * mm});
            skArc(sketch, "E2970", {"start": v(389.25, 46.66) * mm, "mid": v(388.46, 46.77) * mm, "end": v(388.56, 45.98) * mm});
            skArc(sketch, "E2971", {"start": v(388.81, 45.55) * mm, "mid": v(388.75, 45.8) * mm, "end": v(388.56, 45.98) * mm});
            skLineSegment(sketch, "E2972", {"start": v(388.81, 45.55) * mm, "end": v(388.81, 37.01) * mm});
            skLineSegment(sketch, "E2973", {"start": v(388.81, 37.01) * mm, "end": v(388.13, 37.01) * mm});
            skArc(sketch, "E2974", {"start": v(382.47, 39.35) * mm, "mid": v(385.07, 37.62) * mm, "end": v(388.13, 37.01) * mm});
            skLineSegment(sketch, "E2975", {"start": v(382.47, 39.35) * mm, "end": v(343.16, 78.67) * mm});
            skSolve(sketch);
        }
        {
            var Q0;
            Q0 = qSketchRegion(id + "F0", true);
            var Q1;
            Q1=makeQuery(id+"F0.imprint","IMPRINT",FACE,{"disambiguationData":[TD([[makeQuery(id+"F0.imprint","IMPRINT",EDGE,{"derivedFrom":sQuery(id+"F0.wireOp",EDGE,"E1843")}),-1.0]])]});
            var Q2;
            Q2=makeQuery(id+"F0.imprint","IMPRINT",FACE,{"disambiguationData":[TD([[makeQuery(id+"F0.imprint","IMPRINT",EDGE,{"derivedFrom":sQuery(id+"F0.wireOp",EDGE,"E1954")}),-1.0]])]});
            var Q3;
            Q3=makeQuery(id+"F0.imprint","IMPRINT",FACE,{"disambiguationData":[TD([[makeQuery(id+"F0.imprint","IMPRINT",EDGE,{"derivedFrom":sQuery(id+"F0.wireOp",EDGE,"E2046")}),-1.0]])]});
            var Q4;
            Q4=makeQuery(id+"F0.imprint","IMPRINT",FACE,{"disambiguationData":[TD([[makeQuery(id+"F0.imprint","IMPRINT",EDGE,{"derivedFrom":sQuery(id+"F0.wireOp",EDGE,"E2196")}),1.0]])]});
            var Q5;
            Q5=makeQuery(id+"F0.imprint","IMPRINT",FACE,{"disambiguationData":[TD([[makeQuery(id+"F0.imprint","IMPRINT",EDGE,{"derivedFrom":sQuery(id+"F0.wireOp",EDGE,"E2195")}),1.0]])]});
            var Q6;
            Q6=makeQuery(id+"F0.imprint","IMPRINT",FACE,{"disambiguationData":[TD([[makeQuery(id+"F0.imprint","IMPRINT",EDGE,{"derivedFrom":sQuery(id+"F0.wireOp",EDGE,"E2198")}),1.0]])]});
            var Q7;
            Q7=makeQuery(id+"F0.imprint","IMPRINT",FACE,{"disambiguationData":[TD([[makeQuery(id+"F0.imprint","IMPRINT",EDGE,{"derivedFrom":sQuery(id+"F0.wireOp",EDGE,"E2197")}),1.0]])]});
            var Q8;
            Q8=makeQuery(id+"F0.imprint","IMPRINT",FACE,{"disambiguationData":[TD([[makeQuery(id+"F0.imprint","IMPRINT",EDGE,{"derivedFrom":sQuery(id+"F0.wireOp",EDGE,"E2533")}),1.0]])]});
            var Q9;
            Q9=makeQuery(id+"F0.imprint","IMPRINT",FACE,{"disambiguationData":[TD([[makeQuery(id+"F0.imprint","IMPRINT",EDGE,{"derivedFrom":sQuery(id+"F0.wireOp",EDGE,"E2495")}),1.0]])]});
            var Q10;
            Q10=makeQuery(id+"F0.imprint","IMPRINT",FACE,{"disambiguationData":[TD([[makeQuery(id+"F0.imprint","IMPRINT",EDGE,{"derivedFrom":sQuery(id+"F0.wireOp",EDGE,"E2571")}),1.0]])]});
            var Q11;
            Q11=makeQuery(id+"F0.imprint","IMPRINT",FACE,{"disambiguationData":[TD([[makeQuery(id+"F0.imprint","IMPRINT",EDGE,{"derivedFrom":sQuery(id+"F0.wireOp",EDGE,"E2457")}),1.0]])]});
            extrude(context, id + "F1", {"entities" : qUnion([Q0, Q1, Q2, Q3, Q4, Q5, Q6, Q7, Q8, Q9, Q10, Q11]), "depth" : 3 * mm});
        }
        {
            var Q0;
            Q0=qCreatedBy(makeId("Top.planeOp"),FACE);
            var sketch = newSketch(context, id + "F2", { "sketchPlane" : qUnion([Q0])});
            skPoint(sketch, "E2976.0", {"position": v(391.17, -118.38) * mm});
            skPoint(sketch, "E2976.1", {"position": v(390.52, -119.3) * mm});
            skPoint(sketch, "E2976.2", {"position": v(390.52, -121.06) * mm});
            skPoint(sketch, "E2976.3", {"position": v(391.17, -121.97) * mm});
            skPoint(sketch, "E2976.4", {"position": v(417.47, -121.97) * mm});
            skPoint(sketch, "E2976.5", {"position": v(418.12, -121.06) * mm});
            skPoint(sketch, "E2976.6", {"position": v(418.12, -119.3) * mm});
            skPoint(sketch, "E2976.7", {"position": v(417.47, -118.38) * mm});
            skLineSegment(sketch, "E2977", {"start": v(390.52, -118.38) * mm, "end": v(418.12, -118.38) * mm, "construction": true});
            skLineSegment(sketch, "E2978", {"start": v(418.12, -118.38) * mm, "end": v(418.12, -121.97) * mm, "construction": true});
            skLineSegment(sketch, "E2979", {"start": v(418.12, -121.97) * mm, "end": v(390.52, -121.97) * mm, "construction": true});
            skLineSegment(sketch, "E2980", {"start": v(390.52, -121.97) * mm, "end": v(390.52, -118.38) * mm, "construction": true});
            skLineSegment(sketch, "E2981", {"start": v(390.52, -120.18) * mm, "end": v(418.12, -120.18) * mm, "construction": true});
            skPoint(sketch, "E2982", {"position": v(404.32, -120.18) * mm});
            skLineSegment(sketch, "E2983.0", {"start": v(390.52, 119.3) * mm, "end": v(390.52, 121.06) * mm, "construction": true});
            skLineSegment(sketch, "E2983.1", {"start": v(404.32, 118.38) * mm, "end": v(391.17, 118.38) * mm, "construction": true});
            skLineSegment(sketch, "E2983.2", {"start": v(404.32, 121.97) * mm, "end": v(391.17, 121.97) * mm, "construction": true});
            skLineSegment(sketch, "E2983.3", {"start": v(404.32, 118.38) * mm, "end": v(417.47, 118.38) * mm, "construction": true});
            skLineSegment(sketch, "E2983.4", {"start": v(404.32, 121.97) * mm, "end": v(417.47, 121.97) * mm, "construction": true});
            skLineSegment(sketch, "E2983.5", {"start": v(418.12, 121.06) * mm, "end": v(418.12, 119.3) * mm, "construction": true});
            skLineSegment(sketch, "E2984.bottom", {"start": v(390.52, 118.38) * mm, "end": v(418.12, 118.38) * mm, "construction": true});
            skLineSegment(sketch, "E2984.top", {"start": v(390.52, 121.97) * mm, "end": v(418.12, 121.97) * mm, "construction": true});
            skLineSegment(sketch, "E2984.left", {"start": v(390.52, 118.38) * mm, "end": v(390.52, 121.97) * mm, "construction": true});
            skLineSegment(sketch, "E2984.right", {"start": v(418.12, 118.38) * mm, "end": v(418.12, 121.97) * mm, "construction": true});
            skLineSegment(sketch, "E2985", {"start": v(390.52, 120.17) * mm, "end": v(418.12, 120.17) * mm, "construction": true});
            skPoint(sketch, "E2986", {"position": v(404.32, 120.17) * mm});
            skLineSegment(sketch, "E2987.0", {"start": v(-375.17, -21.26) * mm, "end": v(-373.6, -21.26) * mm, "construction": true});
            skLineSegment(sketch, "E2987.1", {"start": v(-373.6, -15.06) * mm, "end": v(-375.17, -15.06) * mm, "construction": true});
            skLineSegment(sketch, "E2988", {"start": v(-374.39, -21.26) * mm, "end": v(-374.39, -15.06) * mm, "construction": true});
            skPoint(sketch, "E2989", {"position": v(-374.39, -18.16) * mm});
            skLineSegment(sketch, "E2990.0", {"start": v(-375.17, 35.3) * mm, "end": v(-373.6, 35.3) * mm, "construction": true});
            skLineSegment(sketch, "E2990.1", {"start": v(-373.6, 41.5) * mm, "end": v(-375.17, 41.5) * mm, "construction": true});
            skLineSegment(sketch, "E2991", {"start": v(-374.39, 35.3) * mm, "end": v(-374.39, 41.5) * mm, "construction": true});
            skPoint(sketch, "E2992", {"position": v(-374.39, 38.4) * mm});
            skLineSegment(sketch, "E2993.0", {"start": v(378.46, -179) * mm, "end": v(376.89, -179) * mm, "construction": true});
            skLineSegment(sketch, "E2993.1", {"start": v(376.89, -172.8) * mm, "end": v(378.46, -172.8) * mm, "construction": true});
            skLineSegment(sketch, "E2993.2", {"start": v(390.62, -190.6) * mm, "end": v(390.62, -189.04) * mm, "construction": true});
            skLineSegment(sketch, "E2993.3", {"start": v(396.82, -189.04) * mm, "end": v(396.82, -190.6) * mm, "construction": true});
            skLineSegment(sketch, "E2993.4", {"start": v(390.62, -141.56) * mm, "end": v(390.62, -140) * mm, "construction": true});
            skLineSegment(sketch, "E2993.5", {"start": v(396.82, -140) * mm, "end": v(396.82, -141.56) * mm, "construction": true});
            skLineSegment(sketch, "E2994", {"start": v(377.67, -179) * mm, "end": v(377.67, -172.8) * mm, "construction": true});
            skLineSegment(sketch, "E2995", {"start": v(390.62, -189.82) * mm, "end": v(396.82, -189.82) * mm, "construction": true});
            skLineSegment(sketch, "E2996", {"start": v(390.62, -140.78) * mm, "end": v(396.82, -140.78) * mm, "construction": true});
            skPoint(sketch, "E2997", {"position": v(393.72, -140.78) * mm});
            skPoint(sketch, "E2998", {"position": v(393.72, -189.82) * mm});
            skPoint(sketch, "E2999", {"position": v(377.67, -175.9) * mm});
            skLineSegment(sketch, "E3000.0", {"start": v(376.89, 172.8) * mm, "end": v(378.46, 172.8) * mm, "construction": true});
            skLineSegment(sketch, "E3000.1", {"start": v(378.46, 179) * mm, "end": v(376.89, 179) * mm, "construction": true});
            skLineSegment(sketch, "E3000.2", {"start": v(390.62, 190.6) * mm, "end": v(390.62, 189.04) * mm, "construction": true});
            skLineSegment(sketch, "E3000.3", {"start": v(396.82, 189.04) * mm, "end": v(396.82, 190.6) * mm, "construction": true});
            skLineSegment(sketch, "E3000.4", {"start": v(390.62, 141.56) * mm, "end": v(390.62, 140) * mm, "construction": true});
            skLineSegment(sketch, "E3000.5", {"start": v(396.82, 140) * mm, "end": v(396.82, 141.56) * mm, "construction": true});
            skLineSegment(sketch, "E3001", {"start": v(390.62, 140.78) * mm, "end": v(396.82, 140.78) * mm, "construction": true});
            skLineSegment(sketch, "E3002", {"start": v(377.67, 172.8) * mm, "end": v(377.67, 179) * mm, "construction": true});
            skLineSegment(sketch, "E3003", {"start": v(390.62, 189.82) * mm, "end": v(396.82, 189.82) * mm, "construction": true});
            skPoint(sketch, "E3004", {"position": v(377.67, 175.9) * mm});
            skPoint(sketch, "E3005", {"position": v(393.72, 189.82) * mm});
            skPoint(sketch, "E3006", {"position": v(393.72, 140.78) * mm});
            skLineSegment(sketch, "E3007.0", {"start": v(405.1, 66.03) * mm, "end": v(403.53, 66.03) * mm, "construction": true});
            skLineSegment(sketch, "E3007.1", {"start": v(403.53, 72.23) * mm, "end": v(405.1, 72.23) * mm, "construction": true});
            skLineSegment(sketch, "E3008", {"start": v(404.32, 66.03) * mm, "end": v(404.32, 72.23) * mm, "construction": true});
            skPoint(sketch, "E3009", {"position": v(404.32, 69.13) * mm});
            skLineSegment(sketch, "E3010.0", {"start": v(405.1, -72.23) * mm, "end": v(403.53, -72.23) * mm, "construction": true});
            skLineSegment(sketch, "E3010.1", {"start": v(403.53, -66.03) * mm, "end": v(405.1, -66.03) * mm, "construction": true});
            skLineSegment(sketch, "E3011", {"start": v(404.32, -72.23) * mm, "end": v(404.32, -66.03) * mm, "construction": true});
            skPoint(sketch, "E3012", {"position": v(404.32, -69.13) * mm});
            skSolve(sketch);
        }
        {
            var Q0;
            Q0=makeQuery(id+"F1.opExtrude","SWEPT_FACE",FACE,{"disambiguationData":[OSD([sQuery(id+"F0.wireOp",EDGE,"E1018")])]});
            var sketch = newSketch(context, id + "F3", { "sketchPlane" : qUnion([Q0])});
            skLineSegment(sketch, "E3013.0", {"start": v(-23.4, 3) * mm, "end": v(-23.4, 0) * mm, "construction": true});
            skLineSegment(sketch, "E3013.1", {"start": v(-52.33, 3) * mm, "end": v(-52.33, 0) * mm, "construction": true});
            skLineSegment(sketch, "E3014", {"start": v(-52.33, 1.5) * mm, "end": v(-23.4, 1.5) * mm, "construction": true});
            skPoint(sketch, "E3015", {"position": v(-37.86, 1.5) * mm});
            skSolve(sketch);
        }
        {
            var Q0;
            Q0=makeQuery(id+"F1.opExtrude","SWEPT_FACE",FACE,{"disambiguationData":[OSD([sQuery(id+"F0.wireOp",EDGE,"E610")])]});
            var sketch = newSketch(context, id + "F4", { "sketchPlane" : qUnion([Q0])});
            skLineSegment(sketch, "E3016.0", {"start": v(418.78, 3) * mm, "end": v(418.78, 0) * mm, "construction": true});
            skLineSegment(sketch, "E3016.1", {"start": v(389.85, 3) * mm, "end": v(389.85, 0) * mm, "construction": true});
            skLineSegment(sketch, "E3017", {"start": v(418.78, 1.5) * mm, "end": v(389.85, 1.5) * mm, "construction": true});
            skPoint(sketch, "E3018", {"position": v(404.32, 1.5) * mm});
            skSolve(sketch);
        }
        {
            var Q0;
            Q0=makeQuery(id+"F1.opExtrude","SWEPT_FACE",FACE,{"disambiguationData":[OSD([sQuery(id+"F0.wireOp",EDGE,"E616")])]});
            var sketch = newSketch(context, id + "F5", { "sketchPlane" : qUnion([Q0])});
            skLineSegment(sketch, "E3019.0", {"start": v(417.92, 3) * mm, "end": v(417.92, 0) * mm, "construction": true});
            skLineSegment(sketch, "E3019.1", {"start": v(411.92, 3) * mm, "end": v(411.92, 0) * mm, "construction": true});
            skLineSegment(sketch, "E3020", {"start": v(417.92, 1.5) * mm, "end": v(411.92, 1.5) * mm, "construction": true});
            skPoint(sketch, "E3021", {"position": v(414.92, 1.5) * mm});
            skSolve(sketch);
        }
        {
            var Q0;
            Q0=makeQuery(id+"F1.opExtrude","SWEPT_FACE",FACE,{"disambiguationData":[OSD([sQuery(id+"F0.wireOp",EDGE,"E1161")])]});
            var sketch = newSketch(context, id + "F6", { "sketchPlane" : qUnion([Q0])});
            skLineSegment(sketch, "E3022.0", {"start": v(-24.26, 3) * mm, "end": v(-24.26, 0) * mm, "construction": true});
            skLineSegment(sketch, "E3022.1", {"start": v(-30.26, 3) * mm, "end": v(-30.26, 0) * mm, "construction": true});
            skLineSegment(sketch, "E3023", {"start": v(-30.26, 1.5) * mm, "end": v(-24.26, 1.5) * mm, "construction": true});
            skPoint(sketch, "E3024", {"position": v(-27.26, 1.5) * mm});
            skSolve(sketch);
        }
        {
            var Q0;
            Q0=makeQuery(id+"F1.opExtrude","SWEPT_FACE",FACE,{"disambiguationData":[OSD([sQuery(id+"F0.wireOp",EDGE,"E600")])]});
            var sketch = newSketch(context, id + "F7", { "sketchPlane" : qUnion([Q0])});
            skLineSegment(sketch, "E3025.0", {"start": v(-411.92, 3) * mm, "end": v(-411.92, 0) * mm, "construction": true});
            skLineSegment(sketch, "E3025.1", {"start": v(-417.92, 3) * mm, "end": v(-417.92, 0) * mm, "construction": true});
            skLineSegment(sketch, "E3026", {"start": v(-411.92, 1.5) * mm, "end": v(-417.92, 1.5) * mm, "construction": true});
            skPoint(sketch, "E3027", {"position": v(-414.92, 1.5) * mm});
            skSolve(sketch);
        }
    });
